# Revit family: QMXVP_with_Isolation_Box
name_source: partatom
category: Mechanical Equipment
units: mm (PartAtom-declared; Revit-internal decimal feet)

## family parameters
Always vertical = Yes
Cut with Voids When Loaded = No
Part Type = Normal
Room Calculation Point = No
Round Connector Dimension = Use Diameter
Shared = No
Work Plane-Based = No

## types (224) — shared parameters
0 = 0' - 0"
1" = 0' - 1"
1.5 = 0' - 1 1/2"
1/4 = 0' - 0 1/4"
2" = 0' - 2"
2' = 2' - 0"
3" = 0' - 3"
3.125" = 0' - 3 1/8"
4" = 0' - 4"
5" = 0' - 5"
6" = 0' - 6"
MB_HT = 1' - 4"
MB_HT+.25" = 1' - 4 1/4"
MB_HT-2.75" = 1' - 1 1/4"
Manufacturer = Loren Cook Company
ONE EIGTH = 0' - 0 1/8"
URL = www.lorencook.com

## per-type parameters (varying)
- 90_QMXVP-9L-Isolation_Box: (A/2)+.25"=1' - 2 1/4"; (NOZZLE_HEIGHT-(NOZZLE_HEIGHT/8*2))/2=0' - 10 1/2"; (NOZZLE_WB_OD-NOZZLE_TOP_OD)/2=0' - 2 3/8"; A=2' - 4"; A/2=1' - 2"; B=5' - 5"; B/2=2' - 8 1/2"; C=2' - 6"; C/2=1' - 3"; E=2' - 3 3/16"; GA=0' - 0 3/32"; Model=QMXVP-Isolation Box; NOZZLE_BOTTOM_ID=1' - 0 13/16"; NOZZLE_BOTTOM_RAD=0' - 6 13/32"; NOZZLE_HEIGHT=2' - 4"; NOZZLE_HEIGHT/7*2=0' - 7"; NOZZLE_SIZE=9' - 0"; NOZZLE_TOP_OD=1' - 1 1/2"; NOZZLE_TOP_RAD=0' - 6 3/4"; NOZZLE_WB/4=0' - 4 19/32"; NOZZLE_WB_OD=1' - 11"; NOZZLE_WB_RAD=0' - 11 1/2"; NOZZLE_WB_RAD-2"=0' - 9 1/2"; RO=1' - 9"; RO/2=0' - 10 1/2"; TRANSITION_TOP=3' - 1 1/16"; TYPE=0' - 0"; Type Comments=Vari-Plume Laboratory Exhaust Mixed-Flow Inline Belt Drive With Isolation Box; UNIT_HEIGHT=1' - 7 7/8"; UNIT_HEIGHT*.75=1' - 2 29/32"; UNIT_OD=1' - 0 13/16"; UNIT_RADIUS=0' - 6 13/32"; UNIT_RADIUS*.6=0' - 5 25/32"; UNIT_RADIUS+4"=0' - 10 13/32"
- 90_QMXVP-9H-Isolation_Box: (A/2)+.25"=1' - 2 1/4"; (NOZZLE_HEIGHT-(NOZZLE_HEIGHT/8*2))/2=0' - 10 1/2"; (NOZZLE_WB_OD-NOZZLE_TOP_OD)/2=0' - 2 3/8"; A=2' - 4"; A/2=1' - 2"; B=5' - 5"; B/2=2' - 8 1/2"; C=2' - 6"; C/2=1' - 3"; E=2' - 3 3/16"; GA=0' - 0 3/32"; Model=QMXVP-Isolation Box; NOZZLE_BOTTOM_ID=1' - 0 13/16"; NOZZLE_BOTTOM_RAD=0' - 6 13/32"; NOZZLE_HEIGHT=2' - 4"; NOZZLE_HEIGHT/7*2=0' - 7"; NOZZLE_SIZE=9' - 0"; NOZZLE_TOP_OD=1' - 1 1/2"; NOZZLE_TOP_RAD=0' - 6 3/4"; NOZZLE_WB/4=0' - 4 19/32"; NOZZLE_WB_OD=1' - 11"; NOZZLE_WB_RAD=0' - 11 1/2"; NOZZLE_WB_RAD-2"=0' - 9 1/2"; RO=1' - 9"; RO/2=0' - 10 1/2"; TRANSITION_TOP=3' - 1 1/16"; TYPE=0' - 0"; Type Comments=Vari-Plume Laboratory Exhaust Mixed-Flow Inline Belt Drive With Isolation Box; UNIT_HEIGHT=1' - 7 7/8"; UNIT_HEIGHT*.75=1' - 2 29/32"; UNIT_OD=1' - 0 13/16"; UNIT_RADIUS=0' - 6 13/32"; UNIT_RADIUS*.6=0' - 5 25/32"; UNIT_RADIUS+4"=0' - 10 13/32"
- 120_QMXVP-9L-Isolation_Box: (A/2)+.25"=1' - 2 1/4"; (NOZZLE_HEIGHT-(NOZZLE_HEIGHT/8*2))/2=0' - 10 1/2"; (NOZZLE_WB_OD-NOZZLE_TOP_OD)/2=0' - 2 3/8"; A=2' - 4"; A/2=1' - 2"; B=5' - 11"; B/2=2' - 11 1/2"; C=3' - 1"; C/2=1' - 6 1/2"; E=2' - 3 3/16"; GA=0' - 0 3/32"; Model=QMXVP-Isolation Box; NOZZLE_BOTTOM_ID=1' - 0 13/16"; NOZZLE_BOTTOM_RAD=0' - 6 13/32"; NOZZLE_HEIGHT=2' - 4"; NOZZLE_HEIGHT/7*2=0' - 7"; NOZZLE_SIZE=9' - 0"; NOZZLE_TOP_OD=1' - 1 1/2"; NOZZLE_TOP_RAD=0' - 6 3/4"; NOZZLE_WB/4=0' - 4 19/32"; NOZZLE_WB_OD=1' - 11"; NOZZLE_WB_RAD=0' - 11 1/2"; NOZZLE_WB_RAD-2"=0' - 9 1/2"; RO=1' - 9"; RO/2=0' - 10 1/2"; TRANSITION_TOP=3' - 7 3/16"; TYPE=0' - 0"; Type Comments=Vari-Plume Laboratory Exhaust Mixed-Flow Inline Belt Drive With Isolation Box; UNIT_HEIGHT=1' - 7 7/8"; UNIT_HEIGHT*.75=1' - 2 29/32"; UNIT_OD=1' - 5 1/16"; UNIT_RADIUS=0' - 8 17/32"; UNIT_RADIUS*.6=0' - 7 11/16"; UNIT_RADIUS+4"=1' - 0 17/32"
- 120_QMXVP-9H-Isolation_Box: (A/2)+.25"=1' - 2 1/4"; (NOZZLE_HEIGHT-(NOZZLE_HEIGHT/8*2))/2=0' - 10 1/2"; (NOZZLE_WB_OD-NOZZLE_TOP_OD)/2=0' - 2 3/8"; A=2' - 4"; A/2=1' - 2"; B=5' - 11"; B/2=2' - 11 1/2"; C=3' - 1"; C/2=1' - 6 1/2"; E=2' - 3 3/16"; GA=0' - 0 3/32"; Model=QMXVP-Isolation Box; NOZZLE_BOTTOM_ID=1' - 0 13/16"; NOZZLE_BOTTOM_RAD=0' - 6 13/32"; NOZZLE_HEIGHT=2' - 4"; NOZZLE_HEIGHT/7*2=0' - 7"; NOZZLE_SIZE=9' - 0"; NOZZLE_TOP_OD=1' - 1 1/2"; NOZZLE_TOP_RAD=0' - 6 3/4"; NOZZLE_WB/4=0' - 4 19/32"; NOZZLE_WB_OD=1' - 11"; NOZZLE_WB_RAD=0' - 11 1/2"; NOZZLE_WB_RAD-2"=0' - 9 1/2"; RO=1' - 9"; RO/2=0' - 10 1/2"; TRANSITION_TOP=3' - 7 3/16"; TYPE=0' - 0"; Type Comments=Vari-Plume Laboratory Exhaust Mixed-Flow Inline Belt Drive With Isolation Box; UNIT_HEIGHT=1' - 7 7/8"; UNIT_HEIGHT*.75=1' - 2 29/32"; UNIT_OD=1' - 5 1/16"; UNIT_RADIUS=0' - 8 17/32"; UNIT_RADIUS*.6=0' - 7 11/16"; UNIT_RADIUS+4"=1' - 0 17/32"
- 120_QMXVP-12L-Isolation_Box: (A/2)+.25"=1' - 2 1/4"; (NOZZLE_HEIGHT-(NOZZLE_HEIGHT/8*2))/2=1' - 0"; (NOZZLE_WB_OD-NOZZLE_TOP_OD)/2=0' - 2 1/8"; A=2' - 4"; A/2=1' - 2"; B=5' - 11"; B/2=2' - 11 1/2"; C=3' - 1"; C/2=1' - 6 1/2"; E=2' - 3 3/16"; GA=0' - 0 3/32"; Model=QMXVP-Isolation Box; NOZZLE_BOTTOM_ID=1' - 5 1/16"; NOZZLE_BOTTOM_RAD=0' - 8 17/32"; NOZZLE_HEIGHT=2' - 8"; NOZZLE_HEIGHT/7*2=0' - 8"; NOZZLE_SIZE=12' - 0"; NOZZLE_TOP_OD=1' - 7 1/2"; NOZZLE_TOP_RAD=0' - 9 3/4"; NOZZLE_WB/4=0' - 5 19/32"; NOZZLE_WB_OD=2' - 4"; NOZZLE_WB_RAD=1' - 2"; NOZZLE_WB_RAD-2"=1' - 0"; RO=1' - 9"; RO/2=0' - 10 1/2"; TRANSITION_TOP=3' - 3 7/16"; TYPE=0' - 0"; Type Comments=Vari-Plume Laboratory Exhaust Mixed-Flow Inline Belt Drive With Isolation Box; UNIT_HEIGHT=1' - 7 7/8"; UNIT_HEIGHT*.75=1' - 2 29/32"; UNIT_OD=1' - 5 1/16"; UNIT_RADIUS=0' - 8 17/32"; UNIT_RADIUS*.6=0' - 7 11/16"; UNIT_RADIUS+4"=1' - 0 17/32"
- 120_QMXVP-12H-Isolation_Box: (A/2)+.25"=1' - 2 1/4"; (NOZZLE_HEIGHT-(NOZZLE_HEIGHT/8*2))/2=1' - 0"; (NOZZLE_WB_OD-NOZZLE_TOP_OD)/2=0' - 2 1/8"; A=2' - 4"; A/2=1' - 2"; B=5' - 11"; B/2=2' - 11 1/2"; C=3' - 1"; C/2=1' - 6 1/2"; E=2' - 3 3/16"; GA=0' - 0 3/32"; Model=QMXVP-Isolation Box; NOZZLE_BOTTOM_ID=1' - 5 1/16"; NOZZLE_BOTTOM_RAD=0' - 8 17/32"; NOZZLE_HEIGHT=2' - 8"; NOZZLE_HEIGHT/7*2=0' - 8"; NOZZLE_SIZE=12' - 0"; NOZZLE_TOP_OD=1' - 7 1/2"; NOZZLE_TOP_RAD=0' - 9 3/4"; NOZZLE_WB/4=0' - 5 19/32"; NOZZLE_WB_OD=2' - 4"; NOZZLE_WB_RAD=1' - 2"; NOZZLE_WB_RAD-2"=1' - 0"; RO=1' - 9"; RO/2=0' - 10 1/2"; TRANSITION_TOP=3' - 3 7/16"; TYPE=0' - 0"; Type Comments=Vari-Plume Laboratory Exhaust Mixed-Flow Inline Belt Drive With Isolation Box; UNIT_HEIGHT=1' - 7 7/8"; UNIT_HEIGHT*.75=1' - 2 29/32"; UNIT_OD=1' - 5 1/16"; UNIT_RADIUS=0' - 8 17/32"; UNIT_RADIUS*.6=0' - 7 11/16"; UNIT_RADIUS+4"=1' - 0 17/32"
- 135_QMXVP-9L-Isolation_Box: (A/2)+.25"=1' - 2 1/4"; (NOZZLE_HEIGHT-(NOZZLE_HEIGHT/8*2))/2=0' - 10 1/2"; (NOZZLE_WB_OD-NOZZLE_TOP_OD)/2=0' - 2 3/8"; A=2' - 4"; A/2=1' - 2"; B=6' - 5"; B/2=3' - 2 1/2"; C=3' - 3"; C/2=1' - 7 1/2"; E=2' - 3 1/8"; GA=0' - 0 3/32"; Model=QMXVP-Isolation Box; NOZZLE_BOTTOM_ID=1' - 0 13/16"; NOZZLE_BOTTOM_RAD=0' - 6 13/32"; NOZZLE_HEIGHT=2' - 4"; NOZZLE_HEIGHT/7*2=0' - 7"; NOZZLE_SIZE=9' - 0"; NOZZLE_TOP_OD=1' - 1 1/2"; NOZZLE_TOP_RAD=0' - 6 3/4"; NOZZLE_WB/4=0' - 4 19/32"; NOZZLE_WB_OD=1' - 11"; NOZZLE_WB_RAD=0' - 11 1/2"; NOZZLE_WB_RAD-2"=0' - 9 1/2"; RO=1' - 8 15/16"; RO/2=0' - 10 15/32"; TRANSITION_TOP=4' - 0 11/16"; TYPE=0' - 0"; Type Comments=Vari-Plume Laboratory Exhaust Mixed-Flow Inline Belt Drive With Isolation Box; UNIT_HEIGHT=2' - 3"; UNIT_HEIGHT*.75=1' - 8 1/4"; UNIT_OD=1' - 7 1/4"; UNIT_RADIUS=0' - 9 5/8"; UNIT_RADIUS*.6=0' - 8 21/32"; UNIT_RADIUS+4"=1' - 1 5/8"
- 135_QMXVP-9H-Isolation_Box: (A/2)+.25"=1' - 2 1/4"; (NOZZLE_HEIGHT-(NOZZLE_HEIGHT/8*2))/2=0' - 10 1/2"; (NOZZLE_WB_OD-NOZZLE_TOP_OD)/2=0' - 2 3/8"; A=2' - 4"; A/2=1' - 2"; B=6' - 5"; B/2=3' - 2 1/2"; C=3' - 3"; C/2=1' - 7 1/2"; E=2' - 3 1/8"; GA=0' - 0 3/32"; Model=QMXVP-Isolation Box; NOZZLE_BOTTOM_ID=1' - 0 13/16"; NOZZLE_BOTTOM_RAD=0' - 6 13/32"; NOZZLE_HEIGHT=2' - 4"; NOZZLE_HEIGHT/7*2=0' - 7"; NOZZLE_SIZE=9' - 0"; NOZZLE_TOP_OD=1' - 1 1/2"; NOZZLE_TOP_RAD=0' - 6 3/4"; NOZZLE_WB/4=0' - 4 19/32"; NOZZLE_WB_OD=1' - 11"; NOZZLE_WB_RAD=0' - 11 1/2"; NOZZLE_WB_RAD-2"=0' - 9 1/2"; RO=1' - 8 15/16"; RO/2=0' - 10 15/32"; TRANSITION_TOP=4' - 0 11/16"; TYPE=0' - 0"; Type Comments=Vari-Plume Laboratory Exhaust Mixed-Flow Inline Belt Drive With Isolation Box; UNIT_HEIGHT=2' - 3"; UNIT_HEIGHT*.75=1' - 8 1/4"; UNIT_OD=1' - 7 1/4"; UNIT_RADIUS=0' - 9 5/8"; UNIT_RADIUS*.6=0' - 8 21/32"; UNIT_RADIUS+4"=1' - 1 5/8"
- 150_QMXVP-9L-Isolation_Box: (A/2)+.25"=1' - 3 1/4"; (NOZZLE_HEIGHT-(NOZZLE_HEIGHT/8*2))/2=0' - 10 1/2"; (NOZZLE_WB_OD-NOZZLE_TOP_OD)/2=0' - 2 3/8"; A=2' - 6"; A/2=1' - 3"; B=7' - 3"; B/2=3' - 7 1/2"; C=3' - 6"; C/2=1' - 9"; E=2' - 5 1/8"; GA=0' - 0 3/32"; Model=QMXVP-Isolation Box; NOZZLE_BOTTOM_ID=1' - 0 13/16"; NOZZLE_BOTTOM_RAD=0' - 6 13/32"; NOZZLE_HEIGHT=2' - 4"; NOZZLE_HEIGHT/7*2=0' - 7"; NOZZLE_SIZE=9' - 0"; NOZZLE_TOP_OD=1' - 1 1/2"; NOZZLE_TOP_RAD=0' - 6 3/4"; NOZZLE_WB/4=0' - 4 19/32"; NOZZLE_WB_OD=1' - 11"; NOZZLE_WB_RAD=0' - 11 1/2"; NOZZLE_WB_RAD-2"=0' - 9 1/2"; RO=1' - 10 15/16"; RO/2=0' - 11 15/32"; TRANSITION_TOP=4' - 6 1/4"; TYPE=0' - 0"; Type Comments=Vari-Plume Laboratory Exhaust Mixed-Flow Inline Belt Drive With Isolation Box; UNIT_HEIGHT=2' - 6"; UNIT_HEIGHT*.75=1' - 10 1/2"; UNIT_OD=1' - 9 3/8"; UNIT_RADIUS=0' - 10 11/16"; UNIT_RADIUS*.6=0' - 9 5/8"; UNIT_RADIUS+4"=1' - 2 11/16"
- 135_QMXVP-12L-Isolation_Box: (A/2)+.25"=1' - 2 1/4"; (NOZZLE_HEIGHT-(NOZZLE_HEIGHT/8*2))/2=1' - 0"; (NOZZLE_WB_OD-NOZZLE_TOP_OD)/2=0' - 2 1/8"; A=2' - 4"; A/2=1' - 2"; B=6' - 5"; B/2=3' - 2 1/2"; C=3' - 3"; C/2=1' - 7 1/2"; E=2' - 3 1/8"; GA=0' - 0 3/32"; Model=QMXVP-Isolation Box; NOZZLE_BOTTOM_ID=1' - 5 1/16"; NOZZLE_BOTTOM_RAD=0' - 8 17/32"; NOZZLE_HEIGHT=2' - 8"; NOZZLE_HEIGHT/7*2=0' - 8"; NOZZLE_SIZE=12' - 0"; NOZZLE_TOP_OD=1' - 7 1/2"; NOZZLE_TOP_RAD=0' - 9 3/4"; NOZZLE_WB/4=0' - 5 19/32"; NOZZLE_WB_OD=2' - 4"; NOZZLE_WB_RAD=1' - 2"; NOZZLE_WB_RAD-2"=1' - 0"; RO=1' - 8 15/16"; RO/2=0' - 10 15/32"; TRANSITION_TOP=3' - 4 11/16"; TYPE=0' - 0"; Type Comments=Vari-Plume Laboratory Exhaust Mixed-Flow Inline Belt Drive With Isolation Box; UNIT_HEIGHT=2' - 3"; UNIT_HEIGHT*.75=1' - 8 1/4"; UNIT_OD=1' - 7 1/4"; UNIT_RADIUS=0' - 9 5/8"; UNIT_RADIUS*.6=0' - 8 21/32"; UNIT_RADIUS+4"=1' - 1 5/8"
- 135_QMXVP-12H-Isolation_Box: (A/2)+.25"=1' - 2 1/4"; (NOZZLE_HEIGHT-(NOZZLE_HEIGHT/8*2))/2=1' - 0"; (NOZZLE_WB_OD-NOZZLE_TOP_OD)/2=0' - 2 1/8"; A=2' - 4"; A/2=1' - 2"; B=6' - 5"; B/2=3' - 2 1/2"; C=3' - 3"; C/2=1' - 7 1/2"; E=2' - 3 1/8"; GA=0' - 0 3/32"; Model=QMXVP-Isolation Box; NOZZLE_BOTTOM_ID=1' - 5 1/16"; NOZZLE_BOTTOM_RAD=0' - 8 17/32"; NOZZLE_HEIGHT=2' - 8"; NOZZLE_HEIGHT/7*2=0' - 8"; NOZZLE_SIZE=12' - 0"; NOZZLE_TOP_OD=1' - 7 1/2"; NOZZLE_TOP_RAD=0' - 9 3/4"; NOZZLE_WB/4=0' - 5 19/32"; NOZZLE_WB_OD=2' - 4"; NOZZLE_WB_RAD=1' - 2"; NOZZLE_WB_RAD-2"=1' - 0"; RO=1' - 8 15/16"; RO/2=0' - 10 15/32"; TRANSITION_TOP=3' - 4 11/16"; TYPE=0' - 0"; Type Comments=Vari-Plume Laboratory Exhaust Mixed-Flow Inline Belt Drive With Isolation Box; UNIT_HEIGHT=2' - 3"; UNIT_HEIGHT*.75=1' - 8 1/4"; UNIT_OD=1' - 7 1/4"; UNIT_RADIUS=0' - 9 5/8"; UNIT_RADIUS*.6=0' - 8 21/32"; UNIT_RADIUS+4"=1' - 1 5/8"
- 150_QMXVP-9H-Isolation_Box: (A/2)+.25"=1' - 3 1/4"; (NOZZLE_HEIGHT-(NOZZLE_HEIGHT/8*2))/2=0' - 10 1/2"; (NOZZLE_WB_OD-NOZZLE_TOP_OD)/2=0' - 2 3/8"; A=2' - 6"; A/2=1' - 3"; B=7' - 3"; B/2=3' - 7 1/2"; C=3' - 6"; C/2=1' - 9"; E=2' - 5 1/8"; GA=0' - 0 3/32"; Model=QMXVP-Isolation Box; NOZZLE_BOTTOM_ID=1' - 0 13/16"; NOZZLE_BOTTOM_RAD=0' - 6 13/32"; NOZZLE_HEIGHT=2' - 4"; NOZZLE_HEIGHT/7*2=0' - 7"; NOZZLE_SIZE=9' - 0"; NOZZLE_TOP_OD=1' - 1 1/2"; NOZZLE_TOP_RAD=0' - 6 3/4"; NOZZLE_WB/4=0' - 4 19/32"; NOZZLE_WB_OD=1' - 11"; NOZZLE_WB_RAD=0' - 11 1/2"; NOZZLE_WB_RAD-2"=0' - 9 1/2"; RO=1' - 10 15/16"; RO/2=0' - 11 15/32"; TRANSITION_TOP=4' - 6 1/4"; TYPE=0' - 0"; Type Comments=Vari-Plume Laboratory Exhaust Mixed-Flow Inline Belt Drive With Isolation Box; UNIT_HEIGHT=2' - 6"; UNIT_HEIGHT*.75=1' - 10 1/2"; UNIT_OD=1' - 9 3/8"; UNIT_RADIUS=0' - 10 11/16"; UNIT_RADIUS*.6=0' - 9 5/8"; UNIT_RADIUS+4"=1' - 2 11/16"
- 150_QMXVP-12L-Isolation_Box: (A/2)+.25"=1' - 3 1/4"; (NOZZLE_HEIGHT-(NOZZLE_HEIGHT/8*2))/2=1' - 0"; (NOZZLE_WB_OD-NOZZLE_TOP_OD)/2=0' - 2 1/8"; A=2' - 6"; A/2=1' - 3"; B=7' - 3"; B/2=3' - 7 1/2"; C=3' - 6"; C/2=1' - 9"; E=2' - 5 1/8"; GA=0' - 0 3/32"; Model=QMXVP-Isolation Box; NOZZLE_BOTTOM_ID=1' - 5 1/16"; NOZZLE_BOTTOM_RAD=0' - 8 17/32"; NOZZLE_HEIGHT=2' - 8"; NOZZLE_HEIGHT/7*2=0' - 8"; NOZZLE_SIZE=12' - 0"; NOZZLE_TOP_OD=1' - 7 1/2"; NOZZLE_TOP_RAD=0' - 9 3/4"; NOZZLE_WB/4=0' - 5 19/32"; NOZZLE_WB_OD=2' - 4"; NOZZLE_WB_RAD=1' - 2"; NOZZLE_WB_RAD-2"=1' - 0"; RO=1' - 10 15/16"; RO/2=0' - 11 15/32"; TRANSITION_TOP=3' - 10 1/4"; TYPE=0' - 0"; Type Comments=Vari-Plume Laboratory Exhaust Mixed-Flow Inline Belt Drive With Isolation Box; UNIT_HEIGHT=2' - 6"; UNIT_HEIGHT*.75=1' - 10 1/2"; UNIT_OD=1' - 9 3/8"; UNIT_RADIUS=0' - 10 11/16"; UNIT_RADIUS*.6=0' - 9 5/8"; UNIT_RADIUS+4"=1' - 2 11/16"
- 150_QMXVP-12H-Isolation_Box: (A/2)+.25"=1' - 3 1/4"; (NOZZLE_HEIGHT-(NOZZLE_HEIGHT/8*2))/2=1' - 0"; (NOZZLE_WB_OD-NOZZLE_TOP_OD)/2=0' - 2 1/8"; A=2' - 6"; A/2=1' - 3"; B=7' - 3"; B/2=3' - 7 1/2"; C=3' - 6"; C/2=1' - 9"; E=2' - 5 1/8"; GA=0' - 0 3/32"; Model=QMXVP-Isolation Box; NOZZLE_BOTTOM_ID=1' - 5 1/16"; NOZZLE_BOTTOM_RAD=0' - 8 17/32"; NOZZLE_HEIGHT=2' - 8"; NOZZLE_HEIGHT/7*2=0' - 8"; NOZZLE_SIZE=12' - 0"; NOZZLE_TOP_OD=1' - 7 1/2"; NOZZLE_TOP_RAD=0' - 9 3/4"; NOZZLE_WB/4=0' - 5 19/32"; NOZZLE_WB_OD=2' - 4"; NOZZLE_WB_RAD=1' - 2"; NOZZLE_WB_RAD-2"=1' - 0"; RO=1' - 10 15/16"; RO/2=0' - 11 15/32"; TRANSITION_TOP=3' - 10 1/4"; TYPE=0' - 0"; Type Comments=Vari-Plume Laboratory Exhaust Mixed-Flow Inline Belt Drive With Isolation Box; UNIT_HEIGHT=2' - 6"; UNIT_HEIGHT*.75=1' - 10 1/2"; UNIT_OD=1' - 9 3/8"; UNIT_RADIUS=0' - 10 11/16"; UNIT_RADIUS*.6=0' - 9 5/8"; UNIT_RADIUS+4"=1' - 2 11/16"
- 150_QMXVP-15L-Isolation_Box: (A/2)+.25"=1' - 3 1/4"; (NOZZLE_HEIGHT-(NOZZLE_HEIGHT/8*2))/2=1' - 4 1/8"; (NOZZLE_WB_OD-NOZZLE_TOP_OD)/2=0' - 3 1/4"; A=2' - 6"; A/2=1' - 3"; B=7' - 3"; B/2=3' - 7 1/2"; C=3' - 6"; C/2=1' - 9"; E=2' - 5 1/8"; GA=0' - 0 3/32"; Model=QMXVP-Isolation Box; NOZZLE_BOTTOM_ID=1' - 9 3/8"; NOZZLE_BOTTOM_RAD=0' - 10 11/16"; NOZZLE_HEIGHT=3' - 7"; NOZZLE_HEIGHT/7*2=0' - 10 3/4"; NOZZLE_SIZE=15' - 0"; NOZZLE_TOP_OD=1' - 11"; NOZZLE_TOP_RAD=0' - 11 1/2"; NOZZLE_WB/4=0' - 7 3/16"; NOZZLE_WB_OD=3' - 0"; NOZZLE_WB_RAD=1' - 6"; NOZZLE_WB_RAD-2"=1' - 4"; RO=1' - 10 15/16"; RO/2=0' - 11 15/32"; TRANSITION_TOP=3' - 7 5/16"; TYPE=0' - 0"; Type Comments=Vari-Plume Laboratory Exhaust Mixed-Flow Inline Belt Drive With Isolation Box; UNIT_HEIGHT=2' - 6"; UNIT_HEIGHT*.75=1' - 10 1/2"; UNIT_OD=1' - 9 3/8"; UNIT_RADIUS=0' - 10 11/16"; UNIT_RADIUS*.6=0' - 9 5/8"; UNIT_RADIUS+4"=1' - 2 11/16"
- 150_QMXVP-15H-Isolation_Box: (A/2)+.25"=1' - 3 1/4"; (NOZZLE_HEIGHT-(NOZZLE_HEIGHT/8*2))/2=1' - 4 1/8"; (NOZZLE_WB_OD-NOZZLE_TOP_OD)/2=0' - 3 1/4"; A=2' - 6"; A/2=1' - 3"; B=7' - 3"; B/2=3' - 7 1/2"; C=3' - 6"; C/2=1' - 9"; E=2' - 5 1/8"; GA=0' - 0 3/32"; Model=QMXVP-Isolation Box; NOZZLE_BOTTOM_ID=1' - 9 3/8"; NOZZLE_BOTTOM_RAD=0' - 10 11/16"; NOZZLE_HEIGHT=3' - 7"; NOZZLE_HEIGHT/7*2=0' - 10 3/4"; NOZZLE_SIZE=15' - 0"; NOZZLE_TOP_OD=1' - 11"; NOZZLE_TOP_RAD=0' - 11 1/2"; NOZZLE_WB/4=0' - 7 3/16"; NOZZLE_WB_OD=3' - 0"; NOZZLE_WB_RAD=1' - 6"; NOZZLE_WB_RAD-2"=1' - 4"; RO=1' - 10 15/16"; RO/2=0' - 11 15/32"; TRANSITION_TOP=3' - 7 5/16"; TYPE=0' - 0"; Type Comments=Vari-Plume Laboratory Exhaust Mixed-Flow Inline Belt Drive With Isolation Box; UNIT_HEIGHT=2' - 6"; UNIT_HEIGHT*.75=1' - 10 1/2"; UNIT_OD=1' - 9 3/8"; UNIT_RADIUS=0' - 10 11/16"; UNIT_RADIUS*.6=0' - 9 5/8"; UNIT_RADIUS+4"=1' - 2 11/16"
- 165_QMXVP-9L-Isolation_Box: (A/2)+.25"=1' - 4 1/4"; (NOZZLE_HEIGHT-(NOZZLE_HEIGHT/8*2))/2=0' - 10 1/2"; (NOZZLE_WB_OD-NOZZLE_TOP_OD)/2=0' - 2 3/8"; A=2' - 8"; A/2=1' - 4"; B=7' - 5"; B/2=3' - 8 1/2"; C=3' - 8"; C/2=1' - 10"; E=2' - 7 1/8"; GA=0' - 0 3/32"; Model=QMXVP-Isolation Box; NOZZLE_BOTTOM_ID=1' - 0 13/16"; NOZZLE_BOTTOM_RAD=0' - 6 13/32"; NOZZLE_HEIGHT=2' - 4"; NOZZLE_HEIGHT/7*2=0' - 7"; NOZZLE_SIZE=9' - 0"; NOZZLE_TOP_OD=1' - 1 1/2"; NOZZLE_TOP_RAD=0' - 6 3/4"; NOZZLE_WB/4=0' - 4 19/32"; NOZZLE_WB_OD=1' - 11"; NOZZLE_WB_RAD=0' - 11 1/2"; NOZZLE_WB_RAD-2"=0' - 9 1/2"; RO=2' - 0 15/16"; RO/2=1' - 0 15/32"; TRANSITION_TOP=5' - 1 1/4"; TYPE=0' - 0"; Type Comments=Vari-Plume Laboratory Exhaust Mixed-Flow Inline Belt Drive With Isolation Box; UNIT_HEIGHT=2' - 9"; UNIT_HEIGHT*.75=2' - 0 3/4"; UNIT_OD=1' - 11 1/2"; UNIT_RADIUS=0' - 11 3/4"; UNIT_RADIUS*.6=0' - 10 9/16"; UNIT_RADIUS+4"=1' - 3 3/4"
- 165_QMXVP-9H-Isolation_Box: (A/2)+.25"=1' - 4 1/4"; (NOZZLE_HEIGHT-(NOZZLE_HEIGHT/8*2))/2=0' - 10 1/2"; (NOZZLE_WB_OD-NOZZLE_TOP_OD)/2=0' - 2 3/8"; A=2' - 8"; A/2=1' - 4"; B=7' - 5"; B/2=3' - 8 1/2"; C=3' - 8"; C/2=1' - 10"; E=2' - 7 1/8"; GA=0' - 0 3/32"; Model=QMXVP-Isolation Box; NOZZLE_BOTTOM_ID=1' - 0 13/16"; NOZZLE_BOTTOM_RAD=0' - 6 13/32"; NOZZLE_HEIGHT=2' - 4"; NOZZLE_HEIGHT/7*2=0' - 7"; NOZZLE_SIZE=9' - 0"; NOZZLE_TOP_OD=1' - 1 1/2"; NOZZLE_TOP_RAD=0' - 6 3/4"; NOZZLE_WB/4=0' - 4 19/32"; NOZZLE_WB_OD=1' - 11"; NOZZLE_WB_RAD=0' - 11 1/2"; NOZZLE_WB_RAD-2"=0' - 9 1/2"; RO=2' - 0 15/16"; RO/2=1' - 0 15/32"; TRANSITION_TOP=5' - 1 1/4"; TYPE=0' - 0"; Type Comments=Vari-Plume Laboratory Exhaust Mixed-Flow Inline Belt Drive With Isolation Box; UNIT_HEIGHT=2' - 9"; UNIT_HEIGHT*.75=2' - 0 3/4"; UNIT_OD=1' - 11 1/2"; UNIT_RADIUS=0' - 11 3/4"; UNIT_RADIUS*.6=0' - 10 9/16"; UNIT_RADIUS+4"=1' - 3 3/4"
- 165_QMXVP-12L-Isolation_Box: (A/2)+.25"=1' - 4 1/4"; (NOZZLE_HEIGHT-(NOZZLE_HEIGHT/8*2))/2=1' - 0"; (NOZZLE_WB_OD-NOZZLE_TOP_OD)/2=0' - 2 1/8"; A=2' - 8"; A/2=1' - 4"; B=7' - 5"; B/2=3' - 8 1/2"; C=3' - 8"; C/2=1' - 10"; E=2' - 7 1/8"; GA=0' - 0 3/32"; Model=QMXVP-Isolation Box; NOZZLE_BOTTOM_ID=1' - 5 1/16"; NOZZLE_BOTTOM_RAD=0' - 8 17/32"; NOZZLE_HEIGHT=2' - 8"; NOZZLE_HEIGHT/7*2=0' - 8"; NOZZLE_SIZE=12' - 0"; NOZZLE_TOP_OD=1' - 7 1/2"; NOZZLE_TOP_RAD=0' - 9 3/4"; NOZZLE_WB/4=0' - 5 19/32"; NOZZLE_WB_OD=2' - 4"; NOZZLE_WB_RAD=1' - 2"; NOZZLE_WB_RAD-2"=1' - 0"; RO=2' - 0 15/16"; RO/2=1' - 0 15/32"; TRANSITION_TOP=4' - 5 1/4"; TYPE=0' - 0"; Type Comments=Vari-Plume Laboratory Exhaust Mixed-Flow Inline Belt Drive With Isolation Box; UNIT_HEIGHT=2' - 9"; UNIT_HEIGHT*.75=2' - 0 3/4"; UNIT_OD=1' - 11 1/2"; UNIT_RADIUS=0' - 11 3/4"; UNIT_RADIUS*.6=0' - 10 9/16"; UNIT_RADIUS+4"=1' - 3 3/4"
- 165_QMXVP-12H-Isolation_Box: (A/2)+.25"=1' - 4 1/4"; (NOZZLE_HEIGHT-(NOZZLE_HEIGHT/8*2))/2=1' - 0"; (NOZZLE_WB_OD-NOZZLE_TOP_OD)/2=0' - 2 1/8"; A=2' - 8"; A/2=1' - 4"; B=7' - 5"; B/2=3' - 8 1/2"; C=3' - 8"; C/2=1' - 10"; E=2' - 7 1/8"; GA=0' - 0 3/32"; Model=QMXVP-Isolation Box; NOZZLE_BOTTOM_ID=1' - 5 1/16"; NOZZLE_BOTTOM_RAD=0' - 8 17/32"; NOZZLE_HEIGHT=2' - 8"; NOZZLE_HEIGHT/7*2=0' - 8"; NOZZLE_SIZE=12' - 0"; NOZZLE_TOP_OD=1' - 7 1/2"; NOZZLE_TOP_RAD=0' - 9 3/4"; NOZZLE_WB/4=0' - 5 19/32"; NOZZLE_WB_OD=2' - 4"; NOZZLE_WB_RAD=1' - 2"; NOZZLE_WB_RAD-2"=1' - 0"; RO=2' - 0 15/16"; RO/2=1' - 0 15/32"; TRANSITION_TOP=4' - 5 1/4"; TYPE=0' - 0"; Type Comments=Vari-Plume Laboratory Exhaust Mixed-Flow Inline Belt Drive With Isolation Box; UNIT_HEIGHT=2' - 9"; UNIT_HEIGHT*.75=2' - 0 3/4"; UNIT_OD=1' - 11 1/2"; UNIT_RADIUS=0' - 11 3/4"; UNIT_RADIUS*.6=0' - 10 9/16"; UNIT_RADIUS+4"=1' - 3 3/4"
- 165_QMXVP-15L-Isolation_Box: (A/2)+.25"=1' - 4 1/4"; (NOZZLE_HEIGHT-(NOZZLE_HEIGHT/8*2))/2=1' - 4 1/8"; (NOZZLE_WB_OD-NOZZLE_TOP_OD)/2=0' - 3 1/4"; A=2' - 8"; A/2=1' - 4"; B=7' - 5"; B/2=3' - 8 1/2"; C=3' - 8"; C/2=1' - 10"; E=2' - 7 1/8"; GA=0' - 0 3/32"; Model=QMXVP-Isolation Box; NOZZLE_BOTTOM_ID=1' - 9 3/8"; NOZZLE_BOTTOM_RAD=0' - 10 11/16"; NOZZLE_HEIGHT=3' - 7"; NOZZLE_HEIGHT/7*2=0' - 10 3/4"; NOZZLE_SIZE=15' - 0"; NOZZLE_TOP_OD=1' - 11"; NOZZLE_TOP_RAD=0' - 11 1/2"; NOZZLE_WB/4=0' - 7 3/16"; NOZZLE_WB_OD=3' - 0"; NOZZLE_WB_RAD=1' - 6"; NOZZLE_WB_RAD-2"=1' - 4"; RO=2' - 0 15/16"; RO/2=1' - 0 15/32"; TRANSITION_TOP=3' - 9 5/16"; TYPE=0' - 0"; Type Comments=Vari-Plume Laboratory Exhaust Mixed-Flow Inline Belt Drive With Isolation Box; UNIT_HEIGHT=2' - 9"; UNIT_HEIGHT*.75=2' - 0 3/4"; UNIT_OD=1' - 11 1/2"; UNIT_RADIUS=0' - 11 3/4"; UNIT_RADIUS*.6=0' - 10 9/16"; UNIT_RADIUS+4"=1' - 3 3/4"
- 165_QMXVP-15H-Isolation_Box: (A/2)+.25"=1' - 4 1/4"; (NOZZLE_HEIGHT-(NOZZLE_HEIGHT/8*2))/2=1' - 4 1/8"; (NOZZLE_WB_OD-NOZZLE_TOP_OD)/2=0' - 3 1/4"; A=2' - 8"; A/2=1' - 4"; B=7' - 5"; B/2=3' - 8 1/2"; C=3' - 8"; C/2=1' - 10"; E=2' - 7 1/8"; GA=0' - 0 3/32"; Model=QMXVP-Isolation Box; NOZZLE_BOTTOM_ID=1' - 9 3/8"; NOZZLE_BOTTOM_RAD=0' - 10 11/16"; NOZZLE_HEIGHT=3' - 7"; NOZZLE_HEIGHT/7*2=0' - 10 3/4"; NOZZLE_SIZE=15' - 0"; NOZZLE_TOP_OD=1' - 11"; NOZZLE_TOP_RAD=0' - 11 1/2"; NOZZLE_WB/4=0' - 7 3/16"; NOZZLE_WB_OD=3' - 0"; NOZZLE_WB_RAD=1' - 6"; NOZZLE_WB_RAD-2"=1' - 4"; RO=2' - 0 15/16"; RO/2=1' - 0 15/32"; TRANSITION_TOP=3' - 9 5/16"; TYPE=0' - 0"; Type Comments=Vari-Plume Laboratory Exhaust Mixed-Flow Inline Belt Drive With Isolation Box; UNIT_HEIGHT=2' - 9"; UNIT_HEIGHT*.75=2' - 0 3/4"; UNIT_OD=1' - 11 1/2"; UNIT_RADIUS=0' - 11 3/4"; UNIT_RADIUS*.6=0' - 10 9/16"; UNIT_RADIUS+4"=1' - 3 3/4"
- 180_QMXVP-12L-Isolation_Box: (A/2)+.25"=1' - 5 1/4"; (NOZZLE_HEIGHT-(NOZZLE_HEIGHT/8*2))/2=1' - 0"; (NOZZLE_WB_OD-NOZZLE_TOP_OD)/2=0' - 2 1/8"; A=2' - 10"; A/2=1' - 5"; B=8' - 2"; B/2=4' - 1"; C=3' - 10"; C/2=1' - 11"; E=2' - 9 1/8"; GA=0' - 0 3/32"; Model=QMXVP-Isolation Box; NOZZLE_BOTTOM_ID=1' - 5 1/16"; NOZZLE_BOTTOM_RAD=0' - 8 17/32"; NOZZLE_HEIGHT=2' - 8"; NOZZLE_HEIGHT/7*2=0' - 8"; NOZZLE_SIZE=12' - 0"; NOZZLE_TOP_OD=1' - 7 1/2"; NOZZLE_TOP_RAD=0' - 9 3/4"; NOZZLE_WB/4=0' - 5 19/32"; NOZZLE_WB_OD=2' - 4"; NOZZLE_WB_RAD=1' - 2"; NOZZLE_WB_RAD-2"=1' - 0"; RO=2' - 2 15/16"; RO/2=1' - 1 15/32"; TRANSITION_TOP=4' - 11 1/16"; TYPE=0' - 0"; Type Comments=Vari-Plume Laboratory Exhaust Mixed-Flow Inline Belt Drive With Isolation Box; UNIT_HEIGHT=2' - 11"; UNIT_HEIGHT*.75=2' - 2 1/4"; UNIT_OD=2' - 1 5/8"; UNIT_RADIUS=1' - 0 13/16"; UNIT_RADIUS*.6=0' - 11 17/32"; UNIT_RADIUS+4"=1' - 4 13/16"
- 180_QMXVP-12H-Isolation_Box: (A/2)+.25"=1' - 5 1/4"; (NOZZLE_HEIGHT-(NOZZLE_HEIGHT/8*2))/2=1' - 0"; (NOZZLE_WB_OD-NOZZLE_TOP_OD)/2=0' - 2 1/8"; A=2' - 10"; A/2=1' - 5"; B=8' - 2"; B/2=4' - 1"; C=3' - 10"; C/2=1' - 11"; E=2' - 9 1/8"; GA=0' - 0 3/32"; Model=QMXVP-Isolation Box; NOZZLE_BOTTOM_ID=1' - 5 1/16"; NOZZLE_BOTTOM_RAD=0' - 8 17/32"; NOZZLE_HEIGHT=2' - 8"; NOZZLE_HEIGHT/7*2=0' - 8"; NOZZLE_SIZE=12' - 0"; NOZZLE_TOP_OD=1' - 7 1/2"; NOZZLE_TOP_RAD=0' - 9 3/4"; NOZZLE_WB/4=0' - 5 19/32"; NOZZLE_WB_OD=2' - 4"; NOZZLE_WB_RAD=1' - 2"; NOZZLE_WB_RAD-2"=1' - 0"; RO=2' - 2 15/16"; RO/2=1' - 1 15/32"; TRANSITION_TOP=4' - 11 1/16"; TYPE=0' - 0"; Type Comments=Vari-Plume Laboratory Exhaust Mixed-Flow Inline Belt Drive With Isolation Box; UNIT_HEIGHT=2' - 11"; UNIT_HEIGHT*.75=2' - 2 1/4"; UNIT_OD=2' - 1 5/8"; UNIT_RADIUS=1' - 0 13/16"; UNIT_RADIUS*.6=0' - 11 17/32"; UNIT_RADIUS+4"=1' - 4 13/16"
- 180_QMXVP-15L-Isolation_Box: (A/2)+.25"=1' - 5 1/4"; (NOZZLE_HEIGHT-(NOZZLE_HEIGHT/8*2))/2=1' - 4 1/8"; (NOZZLE_WB_OD-NOZZLE_TOP_OD)/2=0' - 3 1/4"; A=2' - 10"; A/2=1' - 5"; B=8' - 2"; B/2=4' - 1"; C=3' - 10"; C/2=1' - 11"; E=2' - 9 1/8"; GA=0' - 0 3/32"; Model=QMXVP-Isolation Box; NOZZLE_BOTTOM_ID=1' - 9 3/8"; NOZZLE_BOTTOM_RAD=0' - 10 11/16"; NOZZLE_HEIGHT=3' - 7"; NOZZLE_HEIGHT/7*2=0' - 10 3/4"; NOZZLE_SIZE=15' - 0"; NOZZLE_TOP_OD=1' - 11"; NOZZLE_TOP_RAD=0' - 11 1/2"; NOZZLE_WB/4=0' - 7 3/16"; NOZZLE_WB_OD=3' - 0"; NOZZLE_WB_RAD=1' - 6"; NOZZLE_WB_RAD-2"=1' - 4"; RO=2' - 2 15/16"; RO/2=1' - 1 15/32"; TRANSITION_TOP=4' - 3 1/8"; TYPE=0' - 0"; Type Comments=Vari-Plume Laboratory Exhaust Mixed-Flow Inline Belt Drive With Isolation Box; UNIT_HEIGHT=2' - 11"; UNIT_HEIGHT*.75=2' - 2 1/4"; UNIT_OD=2' - 1 5/8"; UNIT_RADIUS=1' - 0 13/16"; UNIT_RADIUS*.6=0' - 11 17/32"; UNIT_RADIUS+4"=1' - 4 13/16"
- 180_QMXVP-15H-Isolation_Box: (A/2)+.25"=1' - 5 1/4"; (NOZZLE_HEIGHT-(NOZZLE_HEIGHT/8*2))/2=1' - 4 1/8"; (NOZZLE_WB_OD-NOZZLE_TOP_OD)/2=0' - 3 1/4"; A=2' - 10"; A/2=1' - 5"; B=8' - 2"; B/2=4' - 1"; C=3' - 10"; C/2=1' - 11"; E=2' - 9 1/8"; GA=0' - 0 3/32"; Model=QMXVP-Isolation Box; NOZZLE_BOTTOM_ID=1' - 9 3/8"; NOZZLE_BOTTOM_RAD=0' - 10 11/16"; NOZZLE_HEIGHT=3' - 7"; NOZZLE_HEIGHT/7*2=0' - 10 3/4"; NOZZLE_SIZE=15' - 0"; NOZZLE_TOP_OD=1' - 11"; NOZZLE_TOP_RAD=0' - 11 1/2"; NOZZLE_WB/4=0' - 7 3/16"; NOZZLE_WB_OD=3' - 0"; NOZZLE_WB_RAD=1' - 6"; NOZZLE_WB_RAD-2"=1' - 4"; RO=2' - 2 15/16"; RO/2=1' - 1 15/32"; TRANSITION_TOP=4' - 3 1/8"; TYPE=0' - 0"; Type Comments=Vari-Plume Laboratory Exhaust Mixed-Flow Inline Belt Drive With Isolation Box; UNIT_HEIGHT=2' - 11"; UNIT_HEIGHT*.75=2' - 2 1/4"; UNIT_OD=2' - 1 5/8"; UNIT_RADIUS=1' - 0 13/16"; UNIT_RADIUS*.6=0' - 11 17/32"; UNIT_RADIUS+4"=1' - 4 13/16"
- 180_QMXVP-18L-Isolation_Box: (A/2)+.25"=1' - 5 1/4"; (NOZZLE_HEIGHT-(NOZZLE_HEIGHT/8*2))/2=1' - 6"; (NOZZLE_WB_OD-NOZZLE_TOP_OD)/2=0' - 3 7/8"; A=2' - 10"; A/2=1' - 5"; B=8' - 2"; B/2=4' - 1"; C=3' - 10"; C/2=1' - 11"; E=2' - 9 1/8"; GA=0' - 0 3/32"; Model=QMXVP-Isolation Box; NOZZLE_BOTTOM_ID=2' - 1 5/8"; NOZZLE_BOTTOM_RAD=1' - 0 13/16"; NOZZLE_HEIGHT=4' - 0"; NOZZLE_HEIGHT/7*2=1' - 0"; NOZZLE_SIZE=18' - 0"; NOZZLE_TOP_OD=2' - 3 1/2"; NOZZLE_TOP_RAD=1' - 1 3/4"; NOZZLE_WB/4=0' - 8 19/32"; NOZZLE_WB_OD=3' - 7"; NOZZLE_WB_RAD=1' - 9 1/2"; NOZZLE_WB_RAD-2"=1' - 7 1/2"; RO=2' - 2 15/16"; RO/2=1' - 1 15/32"; TRANSITION_TOP=4' - 0 1/2"; TYPE=0' - 0"; Type Comments=Vari-Plume Laboratory Exhaust Mixed-Flow Inline Belt Drive With Isolation Box; UNIT_HEIGHT=2' - 11"; UNIT_HEIGHT*.75=2' - 2 1/4"; UNIT_OD=2' - 1 5/8"; UNIT_RADIUS=1' - 0 13/16"; UNIT_RADIUS*.6=0' - 11 17/32"; UNIT_RADIUS+4"=1' - 4 13/16"
- 180_QMXVP-18H-Isolation_Box: (A/2)+.25"=1' - 5 1/4"; (NOZZLE_HEIGHT-(NOZZLE_HEIGHT/8*2))/2=1' - 6"; (NOZZLE_WB_OD-NOZZLE_TOP_OD)/2=0' - 3 7/8"; A=2' - 10"; A/2=1' - 5"; B=8' - 2"; B/2=4' - 1"; C=3' - 10"; C/2=1' - 11"; E=2' - 9 1/8"; GA=0' - 0 3/32"; Model=QMXVP-Isolation Box; NOZZLE_BOTTOM_ID=2' - 1 5/8"; NOZZLE_BOTTOM_RAD=1' - 0 13/16"; NOZZLE_HEIGHT=4' - 0"; NOZZLE_HEIGHT/7*2=1' - 0"; NOZZLE_SIZE=18' - 0"; NOZZLE_TOP_OD=2' - 3 1/2"; NOZZLE_TOP_RAD=1' - 1 3/4"; NOZZLE_WB/4=0' - 8 19/32"; NOZZLE_WB_OD=3' - 7"; NOZZLE_WB_RAD=1' - 9 1/2"; NOZZLE_WB_RAD-2"=1' - 7 1/2"; RO=2' - 2 15/16"; RO/2=1' - 1 15/32"; TRANSITION_TOP=4' - 0 1/2"; TYPE=0' - 0"; Type Comments=Vari-Plume Laboratory Exhaust Mixed-Flow Inline Belt Drive With Isolation Box; UNIT_HEIGHT=2' - 11"; UNIT_HEIGHT*.75=2' - 2 1/4"; UNIT_OD=2' - 1 5/8"; UNIT_RADIUS=1' - 0 13/16"; UNIT_RADIUS*.6=0' - 11 17/32"; UNIT_RADIUS+4"=1' - 4 13/16"
- 202_QMXVP-12L-Isolation_Box: (A/2)+.25"=1' - 7 1/4"; (NOZZLE_HEIGHT-(NOZZLE_HEIGHT/8*2))/2=1' - 0"; (NOZZLE_WB_OD-NOZZLE_TOP_OD)/2=0' - 2 1/8"; A=3' - 2"; A/2=1' - 7"; B=8' - 8"; B/2=4' - 4"; C=4' - 2"; C/2=2' - 1"; E=3' - 0 15/16"; GA=0' - 0 3/32"; Model=QMXVP-Isolation Box; NOZZLE_BOTTOM_ID=1' - 5 1/16"; NOZZLE_BOTTOM_RAD=0' - 8 17/32"; NOZZLE_HEIGHT=2' - 8"; NOZZLE_HEIGHT/7*2=0' - 8"; NOZZLE_SIZE=12' - 0"; NOZZLE_TOP_OD=1' - 7 1/2"; NOZZLE_TOP_RAD=0' - 9 3/4"; NOZZLE_WB/4=0' - 5 19/32"; NOZZLE_WB_OD=2' - 4"; NOZZLE_WB_RAD=1' - 2"; NOZZLE_WB_RAD-2"=1' - 0"; RO=2' - 6 3/4"; RO/2=1' - 3 3/8"; TRANSITION_TOP=5' - 7 9/16"; TYPE=0' - 0"; Type Comments=Vari-Plume Laboratory Exhaust Mixed-Flow Inline Belt Drive With Isolation Box; UNIT_HEIGHT=3' - 1 1/2"; UNIT_HEIGHT*.75=2' - 4 1/8"; UNIT_OD=2' - 4 3/4"; UNIT_RADIUS=1' - 2 3/8"; UNIT_RADIUS*.6=1' - 0 15/16"; UNIT_RADIUS+4"=1' - 6 3/8"
- 202_QMXVP-12H-Isolation_Box: (A/2)+.25"=1' - 7 1/4"; (NOZZLE_HEIGHT-(NOZZLE_HEIGHT/8*2))/2=1' - 0"; (NOZZLE_WB_OD-NOZZLE_TOP_OD)/2=0' - 2 1/8"; A=3' - 2"; A/2=1' - 7"; B=8' - 8"; B/2=4' - 4"; C=4' - 2"; C/2=2' - 1"; E=3' - 0 15/16"; GA=0' - 0 3/32"; Model=QMXVP-Isolation Box; NOZZLE_BOTTOM_ID=1' - 5 1/16"; NOZZLE_BOTTOM_RAD=0' - 8 17/32"; NOZZLE_HEIGHT=2' - 8"; NOZZLE_HEIGHT/7*2=0' - 8"; NOZZLE_SIZE=12' - 0"; NOZZLE_TOP_OD=1' - 7 1/2"; NOZZLE_TOP_RAD=0' - 9 3/4"; NOZZLE_WB/4=0' - 5 19/32"; NOZZLE_WB_OD=2' - 4"; NOZZLE_WB_RAD=1' - 2"; NOZZLE_WB_RAD-2"=1' - 0"; RO=2' - 6 3/4"; RO/2=1' - 3 3/8"; TRANSITION_TOP=5' - 7 9/16"; TYPE=0' - 0"; Type Comments=Vari-Plume Laboratory Exhaust Mixed-Flow Inline Belt Drive With Isolation Box; UNIT_HEIGHT=3' - 1 1/2"; UNIT_HEIGHT*.75=2' - 4 1/8"; UNIT_OD=2' - 4 3/4"; UNIT_RADIUS=1' - 2 3/8"; UNIT_RADIUS*.6=1' - 0 15/16"; UNIT_RADIUS+4"=1' - 6 3/8"
- 202_QMXVP-15L-Isolation_Box: (A/2)+.25"=1' - 7 1/4"; (NOZZLE_HEIGHT-(NOZZLE_HEIGHT/8*2))/2=1' - 4 1/8"; (NOZZLE_WB_OD-NOZZLE_TOP_OD)/2=0' - 3 1/4"; A=3' - 2"; A/2=1' - 7"; B=8' - 8"; B/2=4' - 4"; C=4' - 2"; C/2=2' - 1"; E=3' - 0 15/16"; GA=0' - 0 3/32"; Model=QMXVP-Isolation Box; NOZZLE_BOTTOM_ID=1' - 9 3/8"; NOZZLE_BOTTOM_RAD=0' - 10 11/16"; NOZZLE_HEIGHT=3' - 7"; NOZZLE_HEIGHT/7*2=0' - 10 3/4"; NOZZLE_SIZE=15' - 0"; NOZZLE_TOP_OD=1' - 11"; NOZZLE_TOP_RAD=0' - 11 1/2"; NOZZLE_WB/4=0' - 7 3/16"; NOZZLE_WB_OD=3' - 0"; NOZZLE_WB_RAD=1' - 6"; NOZZLE_WB_RAD-2"=1' - 4"; RO=2' - 6 3/4"; RO/2=1' - 3 3/8"; TRANSITION_TOP=4' - 11 5/8"; TYPE=0' - 0"; Type Comments=Vari-Plume Laboratory Exhaust Mixed-Flow Inline Belt Drive With Isolation Box; UNIT_HEIGHT=3' - 1 1/2"; UNIT_HEIGHT*.75=2' - 4 1/8"; UNIT_OD=2' - 4 3/4"; UNIT_RADIUS=1' - 2 3/8"; UNIT_RADIUS*.6=1' - 0 15/16"; UNIT_RADIUS+4"=1' - 6 3/8"
- 202_QMXVP-15H-Isolation_Box: (A/2)+.25"=1' - 7 1/4"; (NOZZLE_HEIGHT-(NOZZLE_HEIGHT/8*2))/2=1' - 4 1/8"; (NOZZLE_WB_OD-NOZZLE_TOP_OD)/2=0' - 3 1/4"; A=3' - 2"; A/2=1' - 7"; B=8' - 8"; B/2=4' - 4"; C=4' - 2"; C/2=2' - 1"; E=3' - 0 15/16"; GA=0' - 0 3/32"; Model=QMXVP-Isolation Box; NOZZLE_BOTTOM_ID=1' - 9 3/8"; NOZZLE_BOTTOM_RAD=0' - 10 11/16"; NOZZLE_HEIGHT=3' - 7"; NOZZLE_HEIGHT/7*2=0' - 10 3/4"; NOZZLE_SIZE=15' - 0"; NOZZLE_TOP_OD=1' - 11"; NOZZLE_TOP_RAD=0' - 11 1/2"; NOZZLE_WB/4=0' - 7 3/16"; NOZZLE_WB_OD=3' - 0"; NOZZLE_WB_RAD=1' - 6"; NOZZLE_WB_RAD-2"=1' - 4"; RO=2' - 6 3/4"; RO/2=1' - 3 3/8"; TRANSITION_TOP=4' - 11 5/8"; TYPE=0' - 0"; Type Comments=Vari-Plume Laboratory Exhaust Mixed-Flow Inline Belt Drive With Isolation Box; UNIT_HEIGHT=3' - 1 1/2"; UNIT_HEIGHT*.75=2' - 4 1/8"; UNIT_OD=2' - 4 3/4"; UNIT_RADIUS=1' - 2 3/8"; UNIT_RADIUS*.6=1' - 0 15/16"; UNIT_RADIUS+4"=1' - 6 3/8"
- 202_QMXVP-18L-Isolation_Box: (A/2)+.25"=1' - 7 1/4"; (NOZZLE_HEIGHT-(NOZZLE_HEIGHT/8*2))/2=1' - 6"; (NOZZLE_WB_OD-NOZZLE_TOP_OD)/2=0' - 3 7/8"; A=3' - 2"; A/2=1' - 7"; B=8' - 8"; B/2=4' - 4"; C=4' - 2"; C/2=2' - 1"; E=3' - 0 15/16"; GA=0' - 0 3/32"; Model=QMXVP-Isolation Box; NOZZLE_BOTTOM_ID=2' - 1 5/8"; NOZZLE_BOTTOM_RAD=1' - 0 13/16"; NOZZLE_HEIGHT=4' - 0"; NOZZLE_HEIGHT/7*2=1' - 0"; NOZZLE_SIZE=18' - 0"; NOZZLE_TOP_OD=2' - 3 1/2"; NOZZLE_TOP_RAD=1' - 1 3/4"; NOZZLE_WB/4=0' - 8 19/32"; NOZZLE_WB_OD=3' - 7"; NOZZLE_WB_RAD=1' - 9 1/2"; NOZZLE_WB_RAD-2"=1' - 7 1/2"; RO=2' - 6 3/4"; RO/2=1' - 3 3/8"; TRANSITION_TOP=4' - 3 5/8"; TYPE=0' - 0"; Type Comments=Vari-Plume Laboratory Exhaust Mixed-Flow Inline Belt Drive With Isolation Box; UNIT_HEIGHT=3' - 1 1/2"; UNIT_HEIGHT*.75=2' - 4 1/8"; UNIT_OD=2' - 4 3/4"; UNIT_RADIUS=1' - 2 3/8"; UNIT_RADIUS*.6=1' - 0 15/16"; UNIT_RADIUS+4"=1' - 6 3/8"
- 202_QMXVP-18H-Isolation_Box: (A/2)+.25"=1' - 7 1/4"; (NOZZLE_HEIGHT-(NOZZLE_HEIGHT/8*2))/2=1' - 6"; (NOZZLE_WB_OD-NOZZLE_TOP_OD)/2=0' - 3 7/8"; A=3' - 2"; A/2=1' - 7"; B=8' - 8"; B/2=4' - 4"; C=4' - 2"; C/2=2' - 1"; E=3' - 0 15/16"; GA=0' - 0 3/32"; Model=QMXVP-Isolation Box; NOZZLE_BOTTOM_ID=2' - 1 5/8"; NOZZLE_BOTTOM_RAD=1' - 0 13/16"; NOZZLE_HEIGHT=4' - 0"; NOZZLE_HEIGHT/7*2=1' - 0"; NOZZLE_SIZE=18' - 0"; NOZZLE_TOP_OD=2' - 3 1/2"; NOZZLE_TOP_RAD=1' - 1 3/4"; NOZZLE_WB/4=0' - 8 19/32"; NOZZLE_WB_OD=3' - 7"; NOZZLE_WB_RAD=1' - 9 1/2"; NOZZLE_WB_RAD-2"=1' - 7 1/2"; RO=2' - 6 3/4"; RO/2=1' - 3 3/8"; TRANSITION_TOP=4' - 3 5/8"; TYPE=0' - 0"; Type Comments=Vari-Plume Laboratory Exhaust Mixed-Flow Inline Belt Drive With Isolation Box; UNIT_HEIGHT=3' - 1 1/2"; UNIT_HEIGHT*.75=2' - 4 1/8"; UNIT_OD=2' - 4 3/4"; UNIT_RADIUS=1' - 2 3/8"; UNIT_RADIUS*.6=1' - 0 15/16"; UNIT_RADIUS+4"=1' - 6 3/8"
- 225_QMXVP-12L-Isolation_Box: (A/2)+.25"=1' - 9 1/4"; (NOZZLE_HEIGHT-(NOZZLE_HEIGHT/8*2))/2=1' - 0"; (NOZZLE_WB_OD-NOZZLE_TOP_OD)/2=0' - 2 1/8"; A=3' - 6"; A/2=1' - 9"; B=9' - 5"; B/2=4' - 8 1/2"; C=4' - 8"; C/2=2' - 4"; E=3' - 4 15/16"; GA=0' - 0 3/32"; Model=QMXVP-Isolation Box; NOZZLE_BOTTOM_ID=1' - 5 1/16"; NOZZLE_BOTTOM_RAD=0' - 8 17/32"; NOZZLE_HEIGHT=2' - 8"; NOZZLE_HEIGHT/7*2=0' - 8"; NOZZLE_SIZE=12' - 0"; NOZZLE_TOP_OD=1' - 7 1/2"; NOZZLE_TOP_RAD=0' - 9 3/4"; NOZZLE_WB/4=0' - 5 19/32"; NOZZLE_WB_OD=2' - 4"; NOZZLE_WB_RAD=1' - 2"; NOZZLE_WB_RAD-2"=1' - 0"; RO=2' - 10 3/4"; RO/2=1' - 5 3/8"; TRANSITION_TOP=6' - 5 1/16"; TYPE=0' - 0"; Type Comments=Vari-Plume Laboratory Exhaust Mixed-Flow Inline Belt Drive With Isolation Box; UNIT_HEIGHT=3' - 5"; UNIT_HEIGHT*.75=2' - 6 3/4"; UNIT_OD=2' - 7 15/16"; UNIT_RADIUS=1' - 3 31/32"; UNIT_RADIUS*.6=1' - 2 3/8"; UNIT_RADIUS+4"=1' - 7 31/32"
- 225_QMXVP-12H-Isolation_Box: (A/2)+.25"=1' - 9 1/4"; (NOZZLE_HEIGHT-(NOZZLE_HEIGHT/8*2))/2=1' - 0"; (NOZZLE_WB_OD-NOZZLE_TOP_OD)/2=0' - 2 1/8"; A=3' - 6"; A/2=1' - 9"; B=9' - 5"; B/2=4' - 8 1/2"; C=4' - 8"; C/2=2' - 4"; E=3' - 4 15/16"; GA=0' - 0 3/32"; Model=QMXVP-Isolation Box; NOZZLE_BOTTOM_ID=1' - 5 1/16"; NOZZLE_BOTTOM_RAD=0' - 8 17/32"; NOZZLE_HEIGHT=2' - 8"; NOZZLE_HEIGHT/7*2=0' - 8"; NOZZLE_SIZE=12' - 0"; NOZZLE_TOP_OD=1' - 7 1/2"; NOZZLE_TOP_RAD=0' - 9 3/4"; NOZZLE_WB/4=0' - 5 19/32"; NOZZLE_WB_OD=2' - 4"; NOZZLE_WB_RAD=1' - 2"; NOZZLE_WB_RAD-2"=1' - 0"; RO=2' - 10 3/4"; RO/2=1' - 5 3/8"; TRANSITION_TOP=6' - 5 1/16"; TYPE=0' - 0"; Type Comments=Vari-Plume Laboratory Exhaust Mixed-Flow Inline Belt Drive With Isolation Box; UNIT_HEIGHT=3' - 5"; UNIT_HEIGHT*.75=2' - 6 3/4"; UNIT_OD=2' - 7 15/16"; UNIT_RADIUS=1' - 3 31/32"; UNIT_RADIUS*.6=1' - 2 3/8"; UNIT_RADIUS+4"=1' - 7 31/32"
- 225_QMXVP-15L-Isolation_Box: (A/2)+.25"=1' - 9 1/4"; (NOZZLE_HEIGHT-(NOZZLE_HEIGHT/8*2))/2=1' - 4 1/8"; (NOZZLE_WB_OD-NOZZLE_TOP_OD)/2=0' - 3 1/4"; A=3' - 6"; A/2=1' - 9"; B=9' - 5"; B/2=4' - 8 1/2"; C=4' - 8"; C/2=2' - 4"; E=3' - 4 15/16"; GA=0' - 0 3/32"; Model=QMXVP-Isolation Box; NOZZLE_BOTTOM_ID=1' - 9 3/8"; NOZZLE_BOTTOM_RAD=0' - 10 11/16"; NOZZLE_HEIGHT=3' - 7"; NOZZLE_HEIGHT/7*2=0' - 10 3/4"; NOZZLE_SIZE=15' - 0"; NOZZLE_TOP_OD=1' - 11"; NOZZLE_TOP_RAD=0' - 11 1/2"; NOZZLE_WB/4=0' - 7 3/16"; NOZZLE_WB_OD=3' - 0"; NOZZLE_WB_RAD=1' - 6"; NOZZLE_WB_RAD-2"=1' - 4"; RO=2' - 10 3/4"; RO/2=1' - 5 3/8"; TRANSITION_TOP=5' - 9 1/8"; TYPE=0' - 0"; Type Comments=Vari-Plume Laboratory Exhaust Mixed-Flow Inline Belt Drive With Isolation Box; UNIT_HEIGHT=3' - 5"; UNIT_HEIGHT*.75=2' - 6 3/4"; UNIT_OD=2' - 7 15/16"; UNIT_RADIUS=1' - 3 31/32"; UNIT_RADIUS*.6=1' - 2 3/8"; UNIT_RADIUS+4"=1' - 7 31/32"
- 225_QMXVP-15H-Isolation_Box: (A/2)+.25"=1' - 9 1/4"; (NOZZLE_HEIGHT-(NOZZLE_HEIGHT/8*2))/2=1' - 4 1/8"; (NOZZLE_WB_OD-NOZZLE_TOP_OD)/2=0' - 3 1/4"; A=3' - 6"; A/2=1' - 9"; B=9' - 5"; B/2=4' - 8 1/2"; C=4' - 8"; C/2=2' - 4"; E=3' - 4 15/16"; GA=0' - 0 3/32"; Model=QMXVP-Isolation Box; NOZZLE_BOTTOM_ID=1' - 9 3/8"; NOZZLE_BOTTOM_RAD=0' - 10 11/16"; NOZZLE_HEIGHT=3' - 7"; NOZZLE_HEIGHT/7*2=0' - 10 3/4"; NOZZLE_SIZE=15' - 0"; NOZZLE_TOP_OD=1' - 11"; NOZZLE_TOP_RAD=0' - 11 1/2"; NOZZLE_WB/4=0' - 7 3/16"; NOZZLE_WB_OD=3' - 0"; NOZZLE_WB_RAD=1' - 6"; NOZZLE_WB_RAD-2"=1' - 4"; RO=2' - 10 3/4"; RO/2=1' - 5 3/8"; TRANSITION_TOP=5' - 9 1/8"; TYPE=0' - 0"; Type Comments=Vari-Plume Laboratory Exhaust Mixed-Flow Inline Belt Drive With Isolation Box; UNIT_HEIGHT=3' - 5"; UNIT_HEIGHT*.75=2' - 6 3/4"; UNIT_OD=2' - 7 15/16"; UNIT_RADIUS=1' - 3 31/32"; UNIT_RADIUS*.6=1' - 2 3/8"; UNIT_RADIUS+4"=1' - 7 31/32"
- 225_QMXVP-18L-Isolation_Box: (A/2)+.25"=1' - 9 1/4"; (NOZZLE_HEIGHT-(NOZZLE_HEIGHT/8*2))/2=1' - 6"; (NOZZLE_WB_OD-NOZZLE_TOP_OD)/2=0' - 3 7/8"; A=3' - 6"; A/2=1' - 9"; B=9' - 5"; B/2=4' - 8 1/2"; C=4' - 8"; C/2=2' - 4"; E=3' - 4 15/16"; GA=0' - 0 3/32"; Model=QMXVP-Isolation Box; NOZZLE_BOTTOM_ID=2' - 1 5/8"; NOZZLE_BOTTOM_RAD=1' - 0 13/16"; NOZZLE_HEIGHT=4' - 0"; NOZZLE_HEIGHT/7*2=1' - 0"; NOZZLE_SIZE=18' - 0"; NOZZLE_TOP_OD=2' - 3 1/2"; NOZZLE_TOP_RAD=1' - 1 3/4"; NOZZLE_WB/4=0' - 8 19/32"; NOZZLE_WB_OD=3' - 7"; NOZZLE_WB_RAD=1' - 9 1/2"; NOZZLE_WB_RAD-2"=1' - 7 1/2"; RO=2' - 10 3/4"; RO/2=1' - 5 3/8"; TRANSITION_TOP=5' - 1 1/8"; TYPE=0' - 0"; Type Comments=Vari-Plume Laboratory Exhaust Mixed-Flow Inline Belt Drive With Isolation Box; UNIT_HEIGHT=3' - 5"; UNIT_HEIGHT*.75=2' - 6 3/4"; UNIT_OD=2' - 7 15/16"; UNIT_RADIUS=1' - 3 31/32"; UNIT_RADIUS*.6=1' - 2 3/8"; UNIT_RADIUS+4"=1' - 7 31/32"
- 245_QMXVP-15L-Isolation_Box: (A/2)+.25"=1' - 10 1/4"; (NOZZLE_HEIGHT-(NOZZLE_HEIGHT/8*2))/2=1' - 4 1/8"; (NOZZLE_WB_OD-NOZZLE_TOP_OD)/2=0' - 3 1/4"; A=3' - 8"; A/2=1' - 10"; B=10' - 1"; B/2=5' - 0 1/2"; C=4' - 11"; C/2=2' - 5 1/2"; E=3' - 6 15/16"; GA=0' - 0 3/32"; Model=QMXVP-Isolation Box; NOZZLE_BOTTOM_ID=1' - 9 3/8"; NOZZLE_BOTTOM_RAD=0' - 10 11/16"; NOZZLE_HEIGHT=3' - 7"; NOZZLE_HEIGHT/7*2=0' - 10 3/4"; NOZZLE_SIZE=15' - 0"; NOZZLE_TOP_OD=1' - 11"; NOZZLE_TOP_RAD=0' - 11 1/2"; NOZZLE_WB/4=0' - 7 3/16"; NOZZLE_WB_OD=3' - 0"; NOZZLE_WB_RAD=1' - 6"; NOZZLE_WB_RAD-2"=1' - 4"; RO=3' - 0 3/4"; RO/2=1' - 6 3/8"; TRANSITION_TOP=6' - 5 11/16"; TYPE=0' - 0"; Type Comments=Vari-Plume Laboratory Exhaust Mixed-Flow Inline Belt Drive With Isolation Box; UNIT_HEIGHT=3' - 8 1/2"; UNIT_HEIGHT*.75=2' - 9 3/8"; UNIT_OD=2' - 10 3/4"; UNIT_RADIUS=1' - 5 3/8"; UNIT_RADIUS*.6=1' - 3 5/8"; UNIT_RADIUS+4"=1' - 9 3/8"
- 245_QMXVP-15H-Isolation_Box: (A/2)+.25"=1' - 10 1/4"; (NOZZLE_HEIGHT-(NOZZLE_HEIGHT/8*2))/2=1' - 4 1/8"; (NOZZLE_WB_OD-NOZZLE_TOP_OD)/2=0' - 3 1/4"; A=3' - 8"; A/2=1' - 10"; B=10' - 1"; B/2=5' - 0 1/2"; C=4' - 11"; C/2=2' - 5 1/2"; E=3' - 6 15/16"; GA=0' - 0 3/32"; Model=QMXVP-Isolation Box; NOZZLE_BOTTOM_ID=1' - 9 3/8"; NOZZLE_BOTTOM_RAD=0' - 10 11/16"; NOZZLE_HEIGHT=3' - 7"; NOZZLE_HEIGHT/7*2=0' - 10 3/4"; NOZZLE_SIZE=15' - 0"; NOZZLE_TOP_OD=1' - 11"; NOZZLE_TOP_RAD=0' - 11 1/2"; NOZZLE_WB/4=0' - 7 3/16"; NOZZLE_WB_OD=3' - 0"; NOZZLE_WB_RAD=1' - 6"; NOZZLE_WB_RAD-2"=1' - 4"; RO=3' - 0 3/4"; RO/2=1' - 6 3/8"; TRANSITION_TOP=6' - 5 11/16"; TYPE=0' - 0"; Type Comments=Vari-Plume Laboratory Exhaust Mixed-Flow Inline Belt Drive With Isolation Box; UNIT_HEIGHT=3' - 8 1/2"; UNIT_HEIGHT*.75=2' - 9 3/8"; UNIT_OD=2' - 10 3/4"; UNIT_RADIUS=1' - 5 3/8"; UNIT_RADIUS*.6=1' - 3 5/8"; UNIT_RADIUS+4"=1' - 9 3/8"
- 245_QMXVP-18L-Isolation_Box: (A/2)+.25"=1' - 10 1/4"; (NOZZLE_HEIGHT-(NOZZLE_HEIGHT/8*2))/2=1' - 6"; (NOZZLE_WB_OD-NOZZLE_TOP_OD)/2=0' - 3 7/8"; A=3' - 8"; A/2=1' - 10"; B=10' - 1"; B/2=5' - 0 1/2"; C=4' - 11"; C/2=2' - 5 1/2"; E=3' - 6 15/16"; GA=0' - 0 3/32"; Model=QMXVP-Isolation Box; NOZZLE_BOTTOM_ID=2' - 1 5/8"; NOZZLE_BOTTOM_RAD=1' - 0 13/16"; NOZZLE_HEIGHT=4' - 0"; NOZZLE_HEIGHT/7*2=1' - 0"; NOZZLE_SIZE=18' - 0"; NOZZLE_TOP_OD=2' - 3 1/2"; NOZZLE_TOP_RAD=1' - 1 3/4"; NOZZLE_WB/4=0' - 8 19/32"; NOZZLE_WB_OD=3' - 7"; NOZZLE_WB_RAD=1' - 9 1/2"; NOZZLE_WB_RAD-2"=1' - 7 1/2"; RO=3' - 0 3/4"; RO/2=1' - 6 3/8"; TRANSITION_TOP=5' - 9 11/16"; TYPE=0' - 0"; Type Comments=Vari-Plume Laboratory Exhaust Mixed-Flow Inline Belt Drive With Isolation Box; UNIT_HEIGHT=3' - 8 1/2"; UNIT_HEIGHT*.75=2' - 9 3/8"; UNIT_OD=2' - 10 3/4"; UNIT_RADIUS=1' - 5 3/8"; UNIT_RADIUS*.6=1' - 3 5/8"; UNIT_RADIUS+4"=1' - 9 3/8"
- 245_QMXVP-18H-Isolation_Box: (A/2)+.25"=1' - 10 1/4"; (NOZZLE_HEIGHT-(NOZZLE_HEIGHT/8*2))/2=1' - 6"; (NOZZLE_WB_OD-NOZZLE_TOP_OD)/2=0' - 3 7/8"; A=3' - 8"; A/2=1' - 10"; B=10' - 1"; B/2=5' - 0 1/2"; C=4' - 11"; C/2=2' - 5 1/2"; E=3' - 6 15/16"; GA=0' - 0 3/32"; Model=QMXVP-Isolation Box; NOZZLE_BOTTOM_ID=2' - 1 5/8"; NOZZLE_BOTTOM_RAD=1' - 0 13/16"; NOZZLE_HEIGHT=4' - 0"; NOZZLE_HEIGHT/7*2=1' - 0"; NOZZLE_SIZE=18' - 0"; NOZZLE_TOP_OD=2' - 3 1/2"; NOZZLE_TOP_RAD=1' - 1 3/4"; NOZZLE_WB/4=0' - 8 19/32"; NOZZLE_WB_OD=3' - 7"; NOZZLE_WB_RAD=1' - 9 1/2"; NOZZLE_WB_RAD-2"=1' - 7 1/2"; RO=3' - 0 3/4"; RO/2=1' - 6 3/8"; TRANSITION_TOP=5' - 9 11/16"; TYPE=0' - 0"; Type Comments=Vari-Plume Laboratory Exhaust Mixed-Flow Inline Belt Drive With Isolation Box; UNIT_HEIGHT=3' - 8 1/2"; UNIT_HEIGHT*.75=2' - 9 3/8"; UNIT_OD=2' - 10 3/4"; UNIT_RADIUS=1' - 5 3/8"; UNIT_RADIUS*.6=1' - 3 5/8"; UNIT_RADIUS+4"=1' - 9 3/8"
- 245_QMXVP-24L-Isolation_Box: (A/2)+.25"=1' - 10 1/4"; (NOZZLE_HEIGHT-(NOZZLE_HEIGHT/8*2))/2=1' - 11 1/4"; (NOZZLE_WB_OD-NOZZLE_TOP_OD)/2=0' - 6 1/8"; A=3' - 8"; A/2=1' - 10"; B=10' - 1"; B/2=5' - 0 1/2"; C=4' - 11"; C/2=2' - 5 1/2"; E=3' - 6 15/16"; GA=0' - 0 3/32"; Model=QMXVP-Isolation Box; NOZZLE_BOTTOM_ID=2' - 10 3/4"; NOZZLE_BOTTOM_RAD=1' - 5 3/8"; NOZZLE_HEIGHT=5' - 2"; NOZZLE_HEIGHT/7*2=1' - 3 1/2"; NOZZLE_SIZE=24' - 0"; NOZZLE_TOP_OD=3' - 0 1/2"; NOZZLE_TOP_RAD=1' - 6 1/4"; NOZZLE_WB/4=1' - 0 3/16"; NOZZLE_WB_OD=5' - 1"; NOZZLE_WB_RAD=2' - 6 1/2"; NOZZLE_WB_RAD-2"=2' - 4 1/2"; RO=3' - 0 3/4"; RO/2=1' - 6 3/8"; TRANSITION_TOP=4' - 9 3/4"; TYPE=0' - 0"; Type Comments=Vari-Plume Laboratory Exhaust Mixed-Flow Inline Belt Drive With Isolation Box; UNIT_HEIGHT=3' - 8 1/2"; UNIT_HEIGHT*.75=2' - 9 3/8"; UNIT_OD=2' - 10 3/4"; UNIT_RADIUS=1' - 5 3/8"; UNIT_RADIUS*.6=1' - 3 5/8"; UNIT_RADIUS+4"=1' - 9 3/8"
- 245_QMXVP-24H-Isolation_Box: (A/2)+.25"=1' - 10 1/4"; (NOZZLE_HEIGHT-(NOZZLE_HEIGHT/8*2))/2=1' - 11 1/4"; (NOZZLE_WB_OD-NOZZLE_TOP_OD)/2=0' - 6 1/8"; A=3' - 8"; A/2=1' - 10"; B=10' - 1"; B/2=5' - 0 1/2"; C=4' - 11"; C/2=2' - 5 1/2"; E=3' - 6 15/16"; GA=0' - 0 3/32"; Model=QMXVP-Isolation Box; NOZZLE_BOTTOM_ID=2' - 10 3/4"; NOZZLE_BOTTOM_RAD=1' - 5 3/8"; NOZZLE_HEIGHT=5' - 2"; NOZZLE_HEIGHT/7*2=1' - 3 1/2"; NOZZLE_SIZE=24' - 0"; NOZZLE_TOP_OD=3' - 0 1/2"; NOZZLE_TOP_RAD=1' - 6 1/4"; NOZZLE_WB/4=1' - 0 3/16"; NOZZLE_WB_OD=5' - 1"; NOZZLE_WB_RAD=2' - 6 1/2"; NOZZLE_WB_RAD-2"=2' - 4 1/2"; RO=3' - 0 3/4"; RO/2=1' - 6 3/8"; TRANSITION_TOP=4' - 9 3/4"; TYPE=0' - 0"; Type Comments=Vari-Plume Laboratory Exhaust Mixed-Flow Inline Belt Drive With Isolation Box; UNIT_HEIGHT=3' - 8 1/2"; UNIT_HEIGHT*.75=2' - 9 3/8"; UNIT_OD=2' - 10 3/4"; UNIT_RADIUS=1' - 5 3/8"; UNIT_RADIUS*.6=1' - 3 5/8"; UNIT_RADIUS+4"=1' - 9 3/8"
- 270_QMXVP-15L-Isolation_Box: (A/2)+.25"=2' - 0 1/4"; (NOZZLE_HEIGHT-(NOZZLE_HEIGHT/8*2))/2=1' - 4 1/8"; (NOZZLE_WB_OD-NOZZLE_TOP_OD)/2=0' - 3 1/4"; A=4' - 0"; A/2=2' - 0"; B=10' - 8"; B/2=5' - 4"; C=5' - 3"; C/2=2' - 7 1/2"; E=3' - 10 15/16"; GA=0' - 0 3/32"; Model=QMXVP-Isolation Box; NOZZLE_BOTTOM_ID=1' - 9 3/8"; NOZZLE_BOTTOM_RAD=0' - 10 11/16"; NOZZLE_HEIGHT=3' - 7"; NOZZLE_HEIGHT/7*2=0' - 10 3/4"; NOZZLE_SIZE=15' - 0"; NOZZLE_TOP_OD=1' - 11"; NOZZLE_TOP_RAD=0' - 11 1/2"; NOZZLE_WB/4=0' - 7 3/16"; NOZZLE_WB_OD=3' - 0"; NOZZLE_WB_RAD=1' - 6"; NOZZLE_WB_RAD-2"=1' - 4"; RO=3' - 4 3/4"; RO/2=1' - 8 3/8"; TRANSITION_TOP=7' - 2 3/16"; TYPE=0' - 0"; Type Comments=Vari-Plume Laboratory Exhaust Mixed-Flow Inline Belt Drive With Isolation Box; UNIT_HEIGHT=3' - 11"; UNIT_HEIGHT*.75=2' - 11 1/4"; UNIT_OD=3' - 2 5/16"; UNIT_RADIUS=1' - 7 5/32"; UNIT_RADIUS*.6=1' - 5 1/4"; UNIT_RADIUS+4"=1' - 11 5/32"
- 270_QMXVP-15H-Isolation_Box: (A/2)+.25"=2' - 0 1/4"; (NOZZLE_HEIGHT-(NOZZLE_HEIGHT/8*2))/2=1' - 4 1/8"; (NOZZLE_WB_OD-NOZZLE_TOP_OD)/2=0' - 3 1/4"; A=4' - 0"; A/2=2' - 0"; B=10' - 8"; B/2=5' - 4"; C=5' - 3"; C/2=2' - 7 1/2"; E=3' - 10 15/16"; GA=0' - 0 3/32"; Model=QMXVP-Isolation Box; NOZZLE_BOTTOM_ID=1' - 9 3/8"; NOZZLE_BOTTOM_RAD=0' - 10 11/16"; NOZZLE_HEIGHT=3' - 7"; NOZZLE_HEIGHT/7*2=0' - 10 3/4"; NOZZLE_SIZE=15' - 0"; NOZZLE_TOP_OD=1' - 11"; NOZZLE_TOP_RAD=0' - 11 1/2"; NOZZLE_WB/4=0' - 7 3/16"; NOZZLE_WB_OD=3' - 0"; NOZZLE_WB_RAD=1' - 6"; NOZZLE_WB_RAD-2"=1' - 4"; RO=3' - 4 3/4"; RO/2=1' - 8 3/8"; TRANSITION_TOP=7' - 2 3/16"; TYPE=0' - 0"; Type Comments=Vari-Plume Laboratory Exhaust Mixed-Flow Inline Belt Drive With Isolation Box; UNIT_HEIGHT=3' - 11"; UNIT_HEIGHT*.75=2' - 11 1/4"; UNIT_OD=3' - 2 5/16"; UNIT_RADIUS=1' - 7 5/32"; UNIT_RADIUS*.6=1' - 5 1/4"; UNIT_RADIUS+4"=1' - 11 5/32"
- 270_QMXVP-18L-Isolation_Box: (A/2)+.25"=2' - 0 1/4"; (NOZZLE_HEIGHT-(NOZZLE_HEIGHT/8*2))/2=1' - 6"; (NOZZLE_WB_OD-NOZZLE_TOP_OD)/2=0' - 3 7/8"; A=4' - 0"; A/2=2' - 0"; B=10' - 8"; B/2=5' - 4"; C=5' - 3"; C/2=2' - 7 1/2"; E=3' - 10 15/16"; GA=0' - 0 3/32"; Model=QMXVP-Isolation Box; NOZZLE_BOTTOM_ID=2' - 1 5/8"; NOZZLE_BOTTOM_RAD=1' - 0 13/16"; NOZZLE_HEIGHT=4' - 0"; NOZZLE_HEIGHT/7*2=1' - 0"; NOZZLE_SIZE=18' - 0"; NOZZLE_TOP_OD=2' - 3 1/2"; NOZZLE_TOP_RAD=1' - 1 3/4"; NOZZLE_WB/4=0' - 8 19/32"; NOZZLE_WB_OD=3' - 7"; NOZZLE_WB_RAD=1' - 9 1/2"; NOZZLE_WB_RAD-2"=1' - 7 1/2"; RO=3' - 4 3/4"; RO/2=1' - 8 3/8"; TRANSITION_TOP=6' - 7 3/16"; TYPE=0' - 0"; Type Comments=Vari-Plume Laboratory Exhaust Mixed-Flow Inline Belt Drive With Isolation Box; UNIT_HEIGHT=3' - 11"; UNIT_HEIGHT*.75=2' - 11 1/4"; UNIT_OD=3' - 2 5/16"; UNIT_RADIUS=1' - 7 5/32"; UNIT_RADIUS*.6=1' - 5 1/4"; UNIT_RADIUS+4"=1' - 11 5/32"
- 270_QMXVP-18H-Isolation_Box: (A/2)+.25"=2' - 0 1/4"; (NOZZLE_HEIGHT-(NOZZLE_HEIGHT/8*2))/2=1' - 6"; (NOZZLE_WB_OD-NOZZLE_TOP_OD)/2=0' - 3 7/8"; A=4' - 0"; A/2=2' - 0"; B=10' - 8"; B/2=5' - 4"; C=5' - 3"; C/2=2' - 7 1/2"; E=3' - 10 15/16"; GA=0' - 0 3/32"; Model=QMXVP-Isolation Box; NOZZLE_BOTTOM_ID=2' - 1 5/8"; NOZZLE_BOTTOM_RAD=1' - 0 13/16"; NOZZLE_HEIGHT=4' - 0"; NOZZLE_HEIGHT/7*2=1' - 0"; NOZZLE_SIZE=18' - 0"; NOZZLE_TOP_OD=2' - 3 1/2"; NOZZLE_TOP_RAD=1' - 1 3/4"; NOZZLE_WB/4=0' - 8 19/32"; NOZZLE_WB_OD=3' - 7"; NOZZLE_WB_RAD=1' - 9 1/2"; NOZZLE_WB_RAD-2"=1' - 7 1/2"; RO=3' - 4 3/4"; RO/2=1' - 8 3/8"; TRANSITION_TOP=6' - 7 3/16"; TYPE=0' - 0"; Type Comments=Vari-Plume Laboratory Exhaust Mixed-Flow Inline Belt Drive With Isolation Box; UNIT_HEIGHT=3' - 11"; UNIT_HEIGHT*.75=2' - 11 1/4"; UNIT_OD=3' - 2 5/16"; UNIT_RADIUS=1' - 7 5/32"; UNIT_RADIUS*.6=1' - 5 1/4"; UNIT_RADIUS+4"=1' - 11 5/32"
- 270_QMXVP-24L-Isolation_Box: (A/2)+.25"=2' - 0 1/4"; (NOZZLE_HEIGHT-(NOZZLE_HEIGHT/8*2))/2=1' - 11 1/4"; (NOZZLE_WB_OD-NOZZLE_TOP_OD)/2=0' - 6 1/8"; A=4' - 0"; A/2=2' - 0"; B=10' - 8"; B/2=5' - 4"; C=5' - 3"; C/2=2' - 7 1/2"; E=3' - 10 15/16"; GA=0' - 0 3/32"; Model=QMXVP-Isolation Box; NOZZLE_BOTTOM_ID=2' - 10 3/4"; NOZZLE_BOTTOM_RAD=1' - 5 3/8"; NOZZLE_HEIGHT=5' - 2"; NOZZLE_HEIGHT/7*2=1' - 3 1/2"; NOZZLE_SIZE=24' - 0"; NOZZLE_TOP_OD=3' - 0 1/2"; NOZZLE_TOP_RAD=1' - 6 1/4"; NOZZLE_WB/4=1' - 0 3/16"; NOZZLE_WB_OD=5' - 1"; NOZZLE_WB_RAD=2' - 6 1/2"; NOZZLE_WB_RAD-2"=2' - 4 1/2"; RO=3' - 4 3/4"; RO/2=1' - 8 3/8"; TRANSITION_TOP=5' - 2 1/4"; TYPE=0' - 0"; Type Comments=Vari-Plume Laboratory Exhaust Mixed-Flow Inline Belt Drive With Isolation Box; UNIT_HEIGHT=3' - 11"; UNIT_HEIGHT*.75=2' - 11 1/4"; UNIT_OD=3' - 2 5/16"; UNIT_RADIUS=1' - 7 5/32"; UNIT_RADIUS*.6=1' - 5 1/4"; UNIT_RADIUS+4"=1' - 11 5/32"
- 270_QMXVP-24H-Isolation_Box: (A/2)+.25"=2' - 0 1/4"; (NOZZLE_HEIGHT-(NOZZLE_HEIGHT/8*2))/2=1' - 11 1/4"; (NOZZLE_WB_OD-NOZZLE_TOP_OD)/2=0' - 6 1/8"; A=4' - 0"; A/2=2' - 0"; B=10' - 8"; B/2=5' - 4"; C=5' - 3"; C/2=2' - 7 1/2"; E=3' - 10 15/16"; GA=0' - 0 3/32"; Model=QMXVP-Isolation Box; NOZZLE_BOTTOM_ID=2' - 10 3/4"; NOZZLE_BOTTOM_RAD=1' - 5 3/8"; NOZZLE_HEIGHT=5' - 2"; NOZZLE_HEIGHT/7*2=1' - 3 1/2"; NOZZLE_SIZE=24' - 0"; NOZZLE_TOP_OD=3' - 0 1/2"; NOZZLE_TOP_RAD=1' - 6 1/4"; NOZZLE_WB/4=1' - 0 3/16"; NOZZLE_WB_OD=5' - 1"; NOZZLE_WB_RAD=2' - 6 1/2"; NOZZLE_WB_RAD-2"=2' - 4 1/2"; RO=3' - 4 3/4"; RO/2=1' - 8 3/8"; TRANSITION_TOP=5' - 2 1/4"; TYPE=0' - 0"; Type Comments=Vari-Plume Laboratory Exhaust Mixed-Flow Inline Belt Drive With Isolation Box; UNIT_HEIGHT=3' - 11"; UNIT_HEIGHT*.75=2' - 11 1/4"; UNIT_OD=3' - 2 5/16"; UNIT_RADIUS=1' - 7 5/32"; UNIT_RADIUS*.6=1' - 5 1/4"; UNIT_RADIUS+4"=1' - 11 5/32"
- 300_QMXVP-18L-Isolation_Box: (A/2)+.25"=2' - 2 1/4"; (NOZZLE_HEIGHT-(NOZZLE_HEIGHT/8*2))/2=1' - 6"; (NOZZLE_WB_OD-NOZZLE_TOP_OD)/2=0' - 3 7/8"; A=4' - 4"; A/2=2' - 2"; B=12' - 4"; B/2=6' - 2"; C=5' - 7"; C/2=2' - 9 1/2"; E=4' - 2 15/16"; GA=0' - 0 3/32"; Model=QMXVP-Isolation Box; NOZZLE_BOTTOM_ID=2' - 1 5/8"; NOZZLE_BOTTOM_RAD=1' - 0 13/16"; NOZZLE_HEIGHT=4' - 0"; NOZZLE_HEIGHT/7*2=1' - 0"; NOZZLE_SIZE=18' - 0"; NOZZLE_TOP_OD=2' - 3 1/2"; NOZZLE_TOP_RAD=1' - 1 3/4"; NOZZLE_WB/4=0' - 8 19/32"; NOZZLE_WB_OD=3' - 7"; NOZZLE_WB_RAD=1' - 9 1/2"; NOZZLE_WB_RAD-2"=1' - 7 1/2"; RO=3' - 8 3/4"; RO/2=1' - 10 3/8"; TRANSITION_TOP=7' - 10 3/16"; TYPE=0' - 0"; Type Comments=Vari-Plume Laboratory Exhaust Mixed-Flow Inline Belt Drive With Isolation Box; UNIT_HEIGHT=4' - 6"; UNIT_HEIGHT*.75=3' - 4 1/2"; UNIT_OD=3' - 6 1/2"; UNIT_RADIUS=1' - 9 1/4"; UNIT_RADIUS*.6=1' - 7 1/8"; UNIT_RADIUS+4"=2' - 1 1/4"
- 300_QMXVP-18H-Isolation_Box: (A/2)+.25"=2' - 2 1/4"; (NOZZLE_HEIGHT-(NOZZLE_HEIGHT/8*2))/2=1' - 6"; (NOZZLE_WB_OD-NOZZLE_TOP_OD)/2=0' - 3 7/8"; A=4' - 4"; A/2=2' - 2"; B=12' - 4"; B/2=6' - 2"; C=5' - 7"; C/2=2' - 9 1/2"; E=4' - 2 15/16"; GA=0' - 0 3/32"; Model=QMXVP-Isolation Box; NOZZLE_BOTTOM_ID=2' - 1 5/8"; NOZZLE_BOTTOM_RAD=1' - 0 13/16"; NOZZLE_HEIGHT=4' - 0"; NOZZLE_HEIGHT/7*2=1' - 0"; NOZZLE_SIZE=18' - 0"; NOZZLE_TOP_OD=2' - 3 1/2"; NOZZLE_TOP_RAD=1' - 1 3/4"; NOZZLE_WB/4=0' - 8 19/32"; NOZZLE_WB_OD=3' - 7"; NOZZLE_WB_RAD=1' - 9 1/2"; NOZZLE_WB_RAD-2"=1' - 7 1/2"; RO=3' - 8 3/4"; RO/2=1' - 10 3/8"; TRANSITION_TOP=7' - 10 3/16"; TYPE=0' - 0"; Type Comments=Vari-Plume Laboratory Exhaust Mixed-Flow Inline Belt Drive With Isolation Box; UNIT_HEIGHT=4' - 6"; UNIT_HEIGHT*.75=3' - 4 1/2"; UNIT_OD=3' - 6 1/2"; UNIT_RADIUS=1' - 9 1/4"; UNIT_RADIUS*.6=1' - 7 1/8"; UNIT_RADIUS+4"=2' - 1 1/4"
- 300_QMXVP-24L-Isolation_Box: (A/2)+.25"=2' - 2 1/4"; (NOZZLE_HEIGHT-(NOZZLE_HEIGHT/8*2))/2=1' - 11 1/4"; (NOZZLE_WB_OD-NOZZLE_TOP_OD)/2=0' - 6 1/8"; A=4' - 4"; A/2=2' - 2"; B=12' - 4"; B/2=6' - 2"; C=5' - 7"; C/2=2' - 9 1/2"; E=4' - 2 15/16"; GA=0' - 0 3/32"; Model=QMXVP-Isolation Box; NOZZLE_BOTTOM_ID=2' - 10 3/4"; NOZZLE_BOTTOM_RAD=1' - 5 3/8"; NOZZLE_HEIGHT=5' - 2"; NOZZLE_HEIGHT/7*2=1' - 3 1/2"; NOZZLE_SIZE=24' - 0"; NOZZLE_TOP_OD=3' - 0 1/2"; NOZZLE_TOP_RAD=1' - 6 1/4"; NOZZLE_WB/4=1' - 0 3/16"; NOZZLE_WB_OD=5' - 1"; NOZZLE_WB_RAD=2' - 6 1/2"; NOZZLE_WB_RAD-2"=2' - 4 1/2"; RO=3' - 8 3/4"; RO/2=1' - 10 3/8"; TRANSITION_TOP=6' - 5 1/4"; TYPE=0' - 0"; Type Comments=Vari-Plume Laboratory Exhaust Mixed-Flow Inline Belt Drive With Isolation Box; UNIT_HEIGHT=4' - 6"; UNIT_HEIGHT*.75=3' - 4 1/2"; UNIT_OD=3' - 6 1/2"; UNIT_RADIUS=1' - 9 1/4"; UNIT_RADIUS*.6=1' - 7 1/8"; UNIT_RADIUS+4"=2' - 1 1/4"
- 300_QMXVP-24H-Isolation_Box: (A/2)+.25"=2' - 2 1/4"; (NOZZLE_HEIGHT-(NOZZLE_HEIGHT/8*2))/2=1' - 11 1/4"; (NOZZLE_WB_OD-NOZZLE_TOP_OD)/2=0' - 6 1/8"; A=4' - 4"; A/2=2' - 2"; B=12' - 4"; B/2=6' - 2"; C=5' - 7"; C/2=2' - 9 1/2"; E=4' - 2 15/16"; GA=0' - 0 3/32"; Model=QMXVP-Isolation Box; NOZZLE_BOTTOM_ID=2' - 10 3/4"; NOZZLE_BOTTOM_RAD=1' - 5 3/8"; NOZZLE_HEIGHT=5' - 2"; NOZZLE_HEIGHT/7*2=1' - 3 1/2"; NOZZLE_SIZE=24' - 0"; NOZZLE_TOP_OD=3' - 0 1/2"; NOZZLE_TOP_RAD=1' - 6 1/4"; NOZZLE_WB/4=1' - 0 3/16"; NOZZLE_WB_OD=5' - 1"; NOZZLE_WB_RAD=2' - 6 1/2"; NOZZLE_WB_RAD-2"=2' - 4 1/2"; RO=3' - 8 3/4"; RO/2=1' - 10 3/8"; TRANSITION_TOP=6' - 5 1/4"; TYPE=0' - 0"; Type Comments=Vari-Plume Laboratory Exhaust Mixed-Flow Inline Belt Drive With Isolation Box; UNIT_HEIGHT=4' - 6"; UNIT_HEIGHT*.75=3' - 4 1/2"; UNIT_OD=3' - 6 1/2"; UNIT_RADIUS=1' - 9 1/4"; UNIT_RADIUS*.6=1' - 7 1/8"; UNIT_RADIUS+4"=2' - 1 1/4"
- 300_QMXVP-30L-Isolation_Box: (A/2)+.25"=2' - 2 1/4"; (NOZZLE_HEIGHT-(NOZZLE_HEIGHT/8*2))/2=2' - 5 1/4"; (NOZZLE_WB_OD-NOZZLE_TOP_OD)/2=0' - 7 1/8"; A=4' - 4"; A/2=2' - 2"; B=12' - 4"; B/2=6' - 2"; C=5' - 7"; C/2=2' - 9 1/2"; E=4' - 2 15/16"; GA=0' - 0 3/32"; Model=QMXVP-Isolation Box; NOZZLE_BOTTOM_ID=3' - 6 1/2"; NOZZLE_BOTTOM_RAD=1' - 9 1/4"; NOZZLE_HEIGHT=6' - 6"; NOZZLE_HEIGHT/7*2=1' - 7 1/2"; NOZZLE_SIZE=30' - 0"; NOZZLE_TOP_OD=3' - 9 1/2"; NOZZLE_TOP_RAD=1' - 10 3/4"; NOZZLE_WB/4=1' - 2 13/16"; NOZZLE_WB_OD=6' - 2"; NOZZLE_WB_RAD=3' - 1"; NOZZLE_WB_RAD-2"=2' - 11"; RO=3' - 8 3/4"; RO/2=1' - 10 3/8"; TRANSITION_TOP=5' - 8 1/4"; TYPE=0' - 0"; Type Comments=Vari-Plume Laboratory Exhaust Mixed-Flow Inline Belt Drive With Isolation Box; UNIT_HEIGHT=4' - 6"; UNIT_HEIGHT*.75=3' - 4 1/2"; UNIT_OD=3' - 6 1/2"; UNIT_RADIUS=1' - 9 1/4"; UNIT_RADIUS*.6=1' - 7 1/8"; UNIT_RADIUS+4"=2' - 1 1/4"
- 300_QMXVP-30H-Isolation_Box: (A/2)+.25"=2' - 2 1/4"; (NOZZLE_HEIGHT-(NOZZLE_HEIGHT/8*2))/2=2' - 5 1/4"; (NOZZLE_WB_OD-NOZZLE_TOP_OD)/2=0' - 7 1/8"; A=4' - 4"; A/2=2' - 2"; B=12' - 4"; B/2=6' - 2"; C=5' - 7"; C/2=2' - 9 1/2"; E=4' - 2 15/16"; GA=0' - 0 3/32"; Model=QMXVP-Isolation Box; NOZZLE_BOTTOM_ID=3' - 6 1/2"; NOZZLE_BOTTOM_RAD=1' - 9 1/4"; NOZZLE_HEIGHT=6' - 6"; NOZZLE_HEIGHT/7*2=1' - 7 1/2"; NOZZLE_SIZE=30' - 0"; NOZZLE_TOP_OD=3' - 9 1/2"; NOZZLE_TOP_RAD=1' - 10 3/4"; NOZZLE_WB/4=1' - 2 13/16"; NOZZLE_WB_OD=6' - 2"; NOZZLE_WB_RAD=3' - 1"; NOZZLE_WB_RAD-2"=2' - 11"; RO=3' - 8 3/4"; RO/2=1' - 10 3/8"; TRANSITION_TOP=5' - 8 1/4"; TYPE=0' - 0"; Type Comments=Vari-Plume Laboratory Exhaust Mixed-Flow Inline Belt Drive With Isolation Box; UNIT_HEIGHT=4' - 6"; UNIT_HEIGHT*.75=3' - 4 1/2"; UNIT_OD=3' - 6 1/2"; UNIT_RADIUS=1' - 9 1/4"; UNIT_RADIUS*.6=1' - 7 1/8"; UNIT_RADIUS+4"=2' - 1 1/4"
- 330_QMXVP-24L-Isolation_Box: (A/2)+.25"=2' - 4 1/4"; (NOZZLE_HEIGHT-(NOZZLE_HEIGHT/8*2))/2=1' - 11 1/4"; (NOZZLE_WB_OD-NOZZLE_TOP_OD)/2=0' - 6 1/8"; A=4' - 8"; A/2=2' - 4"; B=12' - 10"; B/2=6' - 5"; C=6' - 1"; C/2=3' - 0 1/2"; E=4' - 6 13/16"; GA=0' - 0 3/32"; Model=QMXVP-Isolation Box; NOZZLE_BOTTOM_ID=2' - 10 3/4"; NOZZLE_BOTTOM_RAD=1' - 5 3/8"; NOZZLE_HEIGHT=5' - 2"; NOZZLE_HEIGHT/7*2=1' - 3 1/2"; NOZZLE_SIZE=24' - 0"; NOZZLE_TOP_OD=3' - 0 1/2"; NOZZLE_TOP_RAD=1' - 6 1/4"; NOZZLE_WB/4=1' - 0 3/16"; NOZZLE_WB_OD=5' - 1"; NOZZLE_WB_RAD=2' - 6 1/2"; NOZZLE_WB_RAD-2"=2' - 4 1/2"; RO=4' - 0 5/8"; RO/2=2' - 0 5/16"; TRANSITION_TOP=7' - 5 3/4"; TYPE=0' - 0"; Type Comments=Vari-Plume Laboratory Exhaust Mixed-Flow Inline Belt Drive With Isolation Box; UNIT_HEIGHT=4' - 10 1/2"; UNIT_HEIGHT*.75=3' - 7 7/8"; UNIT_OD=3' - 10 3/4"; UNIT_RADIUS=1' - 11 3/8"; UNIT_RADIUS*.6=1' - 9 1/32"; UNIT_RADIUS+4"=2' - 3 3/8"
- 330_QMXVP-24H-Isolation_Box: (A/2)+.25"=2' - 4 1/4"; (NOZZLE_HEIGHT-(NOZZLE_HEIGHT/8*2))/2=1' - 11 1/4"; (NOZZLE_WB_OD-NOZZLE_TOP_OD)/2=0' - 6 1/8"; A=4' - 8"; A/2=2' - 4"; B=12' - 10"; B/2=6' - 5"; C=6' - 1"; C/2=3' - 0 1/2"; E=4' - 6 13/16"; GA=0' - 0 3/32"; Model=QMXVP-Isolation Box; NOZZLE_BOTTOM_ID=2' - 10 3/4"; NOZZLE_BOTTOM_RAD=1' - 5 3/8"; NOZZLE_HEIGHT=5' - 2"; NOZZLE_HEIGHT/7*2=1' - 3 1/2"; NOZZLE_SIZE=24' - 0"; NOZZLE_TOP_OD=3' - 0 1/2"; NOZZLE_TOP_RAD=1' - 6 1/4"; NOZZLE_WB/4=1' - 0 3/16"; NOZZLE_WB_OD=5' - 1"; NOZZLE_WB_RAD=2' - 6 1/2"; NOZZLE_WB_RAD-2"=2' - 4 1/2"; RO=4' - 0 5/8"; RO/2=2' - 0 5/16"; TRANSITION_TOP=7' - 5 3/4"; TYPE=0' - 0"; Type Comments=Vari-Plume Laboratory Exhaust Mixed-Flow Inline Belt Drive With Isolation Box; UNIT_HEIGHT=4' - 10 1/2"; UNIT_HEIGHT*.75=3' - 7 7/8"; UNIT_OD=3' - 10 3/4"; UNIT_RADIUS=1' - 11 3/8"; UNIT_RADIUS*.6=1' - 9 1/32"; UNIT_RADIUS+4"=2' - 3 3/8"
- 330_QMXVP-30L-Isolation_Box: (A/2)+.25"=2' - 4 1/4"; (NOZZLE_HEIGHT-(NOZZLE_HEIGHT/8*2))/2=2' - 5 1/4"; (NOZZLE_WB_OD-NOZZLE_TOP_OD)/2=0' - 7 1/8"; A=4' - 8"; A/2=2' - 4"; B=12' - 10"; B/2=6' - 5"; C=6' - 1"; C/2=3' - 0 1/2"; E=4' - 6 13/16"; GA=0' - 0 3/32"; Model=QMXVP-Isolation Box; NOZZLE_BOTTOM_ID=3' - 6 1/2"; NOZZLE_BOTTOM_RAD=1' - 9 1/4"; NOZZLE_HEIGHT=6' - 6"; NOZZLE_HEIGHT/7*2=1' - 7 1/2"; NOZZLE_SIZE=30' - 0"; NOZZLE_TOP_OD=3' - 9 1/2"; NOZZLE_TOP_RAD=1' - 10 3/4"; NOZZLE_WB/4=1' - 2 13/16"; NOZZLE_WB_OD=6' - 2"; NOZZLE_WB_RAD=3' - 1"; NOZZLE_WB_RAD-2"=2' - 11"; RO=4' - 0 5/8"; RO/2=2' - 0 5/16"; TRANSITION_TOP=6' - 2 3/4"; TYPE=0' - 0"; Type Comments=Vari-Plume Laboratory Exhaust Mixed-Flow Inline Belt Drive With Isolation Box; UNIT_HEIGHT=4' - 10 1/2"; UNIT_HEIGHT*.75=3' - 7 7/8"; UNIT_OD=3' - 10 3/4"; UNIT_RADIUS=1' - 11 3/8"; UNIT_RADIUS*.6=1' - 9 1/32"; UNIT_RADIUS+4"=2' - 3 3/8"
- 330_QMXVP-30H-Isolation_Box: (A/2)+.25"=2' - 4 1/4"; (NOZZLE_HEIGHT-(NOZZLE_HEIGHT/8*2))/2=2' - 5 1/4"; (NOZZLE_WB_OD-NOZZLE_TOP_OD)/2=0' - 7 1/8"; A=4' - 8"; A/2=2' - 4"; B=12' - 10"; B/2=6' - 5"; C=6' - 1"; C/2=3' - 0 1/2"; E=4' - 6 13/16"; GA=0' - 0 3/32"; Model=QMXVP-Isolation Box; NOZZLE_BOTTOM_ID=3' - 6 1/2"; NOZZLE_BOTTOM_RAD=1' - 9 1/4"; NOZZLE_HEIGHT=6' - 6"; NOZZLE_HEIGHT/7*2=1' - 7 1/2"; NOZZLE_SIZE=30' - 0"; NOZZLE_TOP_OD=3' - 9 1/2"; NOZZLE_TOP_RAD=1' - 10 3/4"; NOZZLE_WB/4=1' - 2 13/16"; NOZZLE_WB_OD=6' - 2"; NOZZLE_WB_RAD=3' - 1"; NOZZLE_WB_RAD-2"=2' - 11"; RO=4' - 0 5/8"; RO/2=2' - 0 5/16"; TRANSITION_TOP=6' - 2 3/4"; TYPE=0' - 0"; Type Comments=Vari-Plume Laboratory Exhaust Mixed-Flow Inline Belt Drive With Isolation Box; UNIT_HEIGHT=4' - 10 1/2"; UNIT_HEIGHT*.75=3' - 7 7/8"; UNIT_OD=3' - 10 3/4"; UNIT_RADIUS=1' - 11 3/8"; UNIT_RADIUS*.6=1' - 9 1/32"; UNIT_RADIUS+4"=2' - 3 3/8"
- 365_QMXVP-24L-Isolation_Box: (A/2)+.25"=2' - 7 1/4"; (NOZZLE_HEIGHT-(NOZZLE_HEIGHT/8*2))/2=1' - 11 1/4"; (NOZZLE_WB_OD-NOZZLE_TOP_OD)/2=0' - 6 1/8"; A=5' - 2"; A/2=2' - 7"; B=14' - 7"; B/2=7' - 3 1/2"; C=6' - 7"; C/2=3' - 3 1/2"; E=5' - 0 3/4"; GA=0' - 0 3/32"; Model=QMXVP-Isolation Box; NOZZLE_BOTTOM_ID=2' - 10 3/4"; NOZZLE_BOTTOM_RAD=1' - 5 3/8"; NOZZLE_HEIGHT=5' - 2"; NOZZLE_HEIGHT/7*2=1' - 3 1/2"; NOZZLE_SIZE=24' - 0"; NOZZLE_TOP_OD=3' - 0 1/2"; NOZZLE_TOP_RAD=1' - 6 1/4"; NOZZLE_WB/4=1' - 0 3/16"; NOZZLE_WB_OD=5' - 1"; NOZZLE_WB_RAD=2' - 6 1/2"; NOZZLE_WB_RAD-2"=2' - 4 1/2"; RO=4' - 6 1/2"; RO/2=2' - 3 1/4"; TRANSITION_TOP=8' - 8 1/4"; TYPE=0' - 0"; Type Comments=Vari-Plume Laboratory Exhaust Mixed-Flow Inline Belt Drive With Isolation Box; UNIT_HEIGHT=5' - 4"; UNIT_HEIGHT*.75=4' - 0"; UNIT_OD=4' - 3 3/4"; UNIT_RADIUS=2' - 1 7/8"; UNIT_RADIUS*.6=1' - 11 9/32"; UNIT_RADIUS+4"=2' - 5 7/8"
- 365_QMXVP-24H-Isolation_Box: (A/2)+.25"=2' - 7 1/4"; (NOZZLE_HEIGHT-(NOZZLE_HEIGHT/8*2))/2=1' - 11 1/4"; (NOZZLE_WB_OD-NOZZLE_TOP_OD)/2=0' - 6 1/8"; A=5' - 2"; A/2=2' - 7"; B=14' - 7"; B/2=7' - 3 1/2"; C=6' - 7"; C/2=3' - 3 1/2"; E=5' - 0 3/4"; GA=0' - 0 3/32"; Model=QMXVP-Isolation Box; NOZZLE_BOTTOM_ID=2' - 10 3/4"; NOZZLE_BOTTOM_RAD=1' - 5 3/8"; NOZZLE_HEIGHT=5' - 2"; NOZZLE_HEIGHT/7*2=1' - 3 1/2"; NOZZLE_SIZE=24' - 0"; NOZZLE_TOP_OD=3' - 0 1/2"; NOZZLE_TOP_RAD=1' - 6 1/4"; NOZZLE_WB/4=1' - 0 3/16"; NOZZLE_WB_OD=5' - 1"; NOZZLE_WB_RAD=2' - 6 1/2"; NOZZLE_WB_RAD-2"=2' - 4 1/2"; RO=4' - 6 1/2"; RO/2=2' - 3 1/4"; TRANSITION_TOP=8' - 8 1/4"; TYPE=0' - 0"; Type Comments=Vari-Plume Laboratory Exhaust Mixed-Flow Inline Belt Drive With Isolation Box; UNIT_HEIGHT=5' - 4"; UNIT_HEIGHT*.75=4' - 0"; UNIT_OD=4' - 3 3/4"; UNIT_RADIUS=2' - 1 7/8"; UNIT_RADIUS*.6=1' - 11 9/32"; UNIT_RADIUS+4"=2' - 5 7/8"
- 365_QMXVP-30L-Isolation_Box: (A/2)+.25"=2' - 7 1/4"; (NOZZLE_HEIGHT-(NOZZLE_HEIGHT/8*2))/2=2' - 5 1/4"; (NOZZLE_WB_OD-NOZZLE_TOP_OD)/2=0' - 7 1/8"; A=5' - 2"; A/2=2' - 7"; B=14' - 7"; B/2=7' - 3 1/2"; C=6' - 7"; C/2=3' - 3 1/2"; E=5' - 0 3/4"; GA=0' - 0 3/32"; Model=QMXVP-Isolation Box; NOZZLE_BOTTOM_ID=3' - 6 1/2"; NOZZLE_BOTTOM_RAD=1' - 9 1/4"; NOZZLE_HEIGHT=6' - 6"; NOZZLE_HEIGHT/7*2=1' - 7 1/2"; NOZZLE_SIZE=30' - 0"; NOZZLE_TOP_OD=3' - 9 1/2"; NOZZLE_TOP_RAD=1' - 10 3/4"; NOZZLE_WB/4=1' - 2 13/16"; NOZZLE_WB_OD=6' - 2"; NOZZLE_WB_RAD=3' - 1"; NOZZLE_WB_RAD-2"=2' - 11"; RO=4' - 6 1/2"; RO/2=2' - 3 1/4"; TRANSITION_TOP=7' - 5 1/2"; TYPE=0' - 0"; Type Comments=Vari-Plume Laboratory Exhaust Mixed-Flow Inline Belt Drive With Isolation Box; UNIT_HEIGHT=5' - 4"; UNIT_HEIGHT*.75=4' - 0"; UNIT_OD=4' - 3 3/4"; UNIT_RADIUS=2' - 1 7/8"; UNIT_RADIUS*.6=1' - 11 9/32"; UNIT_RADIUS+4"=2' - 5 7/8"
- 365_QMXVP-30H-Isolation_Box: (A/2)+.25"=2' - 7 1/4"; (NOZZLE_HEIGHT-(NOZZLE_HEIGHT/8*2))/2=2' - 5 1/4"; (NOZZLE_WB_OD-NOZZLE_TOP_OD)/2=0' - 7 1/8"; A=5' - 2"; A/2=2' - 7"; B=14' - 7"; B/2=7' - 3 1/2"; C=6' - 7"; C/2=3' - 3 1/2"; E=5' - 0 3/4"; GA=0' - 0 3/32"; Model=QMXVP-Isolation Box; NOZZLE_BOTTOM_ID=3' - 6 1/2"; NOZZLE_BOTTOM_RAD=1' - 9 1/4"; NOZZLE_HEIGHT=6' - 6"; NOZZLE_HEIGHT/7*2=1' - 7 1/2"; NOZZLE_SIZE=30' - 0"; NOZZLE_TOP_OD=3' - 9 1/2"; NOZZLE_TOP_RAD=1' - 10 3/4"; NOZZLE_WB/4=1' - 2 13/16"; NOZZLE_WB_OD=6' - 2"; NOZZLE_WB_RAD=3' - 1"; NOZZLE_WB_RAD-2"=2' - 11"; RO=4' - 6 1/2"; RO/2=2' - 3 1/4"; TRANSITION_TOP=7' - 5 1/2"; TYPE=0' - 0"; Type Comments=Vari-Plume Laboratory Exhaust Mixed-Flow Inline Belt Drive With Isolation Box; UNIT_HEIGHT=5' - 4"; UNIT_HEIGHT*.75=4' - 0"; UNIT_OD=4' - 3 3/4"; UNIT_RADIUS=2' - 1 7/8"; UNIT_RADIUS*.6=1' - 11 9/32"; UNIT_RADIUS+4"=2' - 5 7/8"
- 365_QMXVP-36L-Isolation_Box: (A/2)+.25"=2' - 7 1/4"; (NOZZLE_HEIGHT-(NOZZLE_HEIGHT/8*2))/2=2' - 11 5/8"; (NOZZLE_WB_OD-NOZZLE_TOP_OD)/2=0' - 8"; A=5' - 2"; A/2=2' - 7"; B=14' - 7"; B/2=7' - 3 1/2"; C=6' - 7"; C/2=3' - 3 1/2"; E=5' - 0 3/4"; GA=0' - 0 3/32"; Model=QMXVP-Isolation Box; NOZZLE_BOTTOM_ID=4' - 3 3/4"; NOZZLE_BOTTOM_RAD=2' - 1 7/8"; NOZZLE_HEIGHT=7' - 11"; NOZZLE_HEIGHT/7*2=1' - 11 3/4"; NOZZLE_SIZE=36' - 0"; NOZZLE_TOP_OD=4' - 10"; NOZZLE_TOP_RAD=2' - 5"; NOZZLE_WB/4=1' - 6"; NOZZLE_WB_OD=7' - 6"; NOZZLE_WB_RAD=3' - 9"; NOZZLE_WB_RAD-2"=3' - 7"; RO=4' - 6 1/2"; RO/2=2' - 3 1/4"; TRANSITION_TOP=6' - 6 1/4"; TYPE=0' - 0"; Type Comments=Vari-Plume Laboratory Exhaust Mixed-Flow Inline Belt Drive With Isolation Box; UNIT_HEIGHT=5' - 4"; UNIT_HEIGHT*.75=4' - 0"; UNIT_OD=4' - 3 3/4"; UNIT_RADIUS=2' - 1 7/8"; UNIT_RADIUS*.6=1' - 11 9/32"; UNIT_RADIUS+4"=2' - 5 7/8"
- 402_QMXVP-24L-Isolation_Box: (A/2)+.25"=2' - 9 3/4"; (NOZZLE_HEIGHT-(NOZZLE_HEIGHT/8*2))/2=1' - 11 1/4"; (NOZZLE_WB_OD-NOZZLE_TOP_OD)/2=0' - 6 1/8"; A=5' - 7"; A/2=2' - 9 1/2"; B=15' - 3"; B/2=7' - 7 1/2"; C=7' - 4"; C/2=3' - 8"; E=5' - 5 3/4"; GA=0' - 0 3/32"; Model=QMXVP-Isolation Box; NOZZLE_BOTTOM_ID=2' - 10 3/4"; NOZZLE_BOTTOM_RAD=1' - 5 3/8"; NOZZLE_HEIGHT=5' - 2"; NOZZLE_HEIGHT/7*2=1' - 3 1/2"; NOZZLE_SIZE=24' - 0"; NOZZLE_TOP_OD=3' - 0 1/2"; NOZZLE_TOP_RAD=1' - 6 1/4"; NOZZLE_WB/4=1' - 0 3/16"; NOZZLE_WB_OD=5' - 1"; NOZZLE_WB_RAD=2' - 6 1/2"; NOZZLE_WB_RAD-2"=2' - 4 1/2"; RO=4' - 11 7/16"; RO/2=2' - 5 23/32"; TRANSITION_TOP=9' - 10 3/4"; TYPE=0' - 0"; Type Comments=Vari-Plume Laboratory Exhaust Mixed-Flow Inline Belt Drive With Isolation Box; UNIT_HEIGHT=5' - 8 1/2"; UNIT_HEIGHT*.75=4' - 3 3/8"; UNIT_OD=4' - 8 15/16"; UNIT_RADIUS=2' - 4 15/32"; UNIT_RADIUS*.6=2' - 1 5/8"; UNIT_RADIUS+4"=2' - 8 15/32"
- 402_QMXVP-24H-Isolation_Box: (A/2)+.25"=2' - 9 3/4"; (NOZZLE_HEIGHT-(NOZZLE_HEIGHT/8*2))/2=1' - 11 1/4"; (NOZZLE_WB_OD-NOZZLE_TOP_OD)/2=0' - 6 1/8"; A=5' - 7"; A/2=2' - 9 1/2"; B=15' - 3"; B/2=7' - 7 1/2"; C=7' - 4"; C/2=3' - 8"; E=5' - 5 3/4"; GA=0' - 0 3/32"; Model=QMXVP-Isolation Box; NOZZLE_BOTTOM_ID=2' - 10 3/4"; NOZZLE_BOTTOM_RAD=1' - 5 3/8"; NOZZLE_HEIGHT=5' - 2"; NOZZLE_HEIGHT/7*2=1' - 3 1/2"; NOZZLE_SIZE=24' - 0"; NOZZLE_TOP_OD=3' - 0 1/2"; NOZZLE_TOP_RAD=1' - 6 1/4"; NOZZLE_WB/4=1' - 0 3/16"; NOZZLE_WB_OD=5' - 1"; NOZZLE_WB_RAD=2' - 6 1/2"; NOZZLE_WB_RAD-2"=2' - 4 1/2"; RO=4' - 11 7/16"; RO/2=2' - 5 23/32"; TRANSITION_TOP=9' - 10 3/4"; TYPE=0' - 0"; Type Comments=Vari-Plume Laboratory Exhaust Mixed-Flow Inline Belt Drive With Isolation Box; UNIT_HEIGHT=5' - 8 1/2"; UNIT_HEIGHT*.75=4' - 3 3/8"; UNIT_OD=4' - 8 15/16"; UNIT_RADIUS=2' - 4 15/32"; UNIT_RADIUS*.6=2' - 1 5/8"; UNIT_RADIUS+4"=2' - 8 15/32"
- 402_QMXVP-30L-Isolation_Box: (A/2)+.25"=2' - 9 3/4"; (NOZZLE_HEIGHT-(NOZZLE_HEIGHT/8*2))/2=2' - 5 1/4"; (NOZZLE_WB_OD-NOZZLE_TOP_OD)/2=0' - 7 1/8"; A=5' - 7"; A/2=2' - 9 1/2"; B=15' - 3"; B/2=7' - 7 1/2"; C=7' - 4"; C/2=3' - 8"; E=5' - 5 3/4"; GA=0' - 0 3/32"; Model=QMXVP-Isolation Box; NOZZLE_BOTTOM_ID=3' - 6 1/2"; NOZZLE_BOTTOM_RAD=1' - 9 1/4"; NOZZLE_HEIGHT=6' - 6"; NOZZLE_HEIGHT/7*2=1' - 7 1/2"; NOZZLE_SIZE=30' - 0"; NOZZLE_TOP_OD=3' - 9 1/2"; NOZZLE_TOP_RAD=1' - 10 3/4"; NOZZLE_WB/4=1' - 2 13/16"; NOZZLE_WB_OD=6' - 2"; NOZZLE_WB_RAD=3' - 1"; NOZZLE_WB_RAD-2"=2' - 11"; RO=4' - 11 7/16"; RO/2=2' - 5 23/32"; TRANSITION_TOP=8' - 7 3/4"; TYPE=0' - 0"; Type Comments=Vari-Plume Laboratory Exhaust Mixed-Flow Inline Belt Drive With Isolation Box; UNIT_HEIGHT=5' - 8 1/2"; UNIT_HEIGHT*.75=4' - 3 3/8"; UNIT_OD=4' - 8 15/16"; UNIT_RADIUS=2' - 4 15/32"; UNIT_RADIUS*.6=2' - 1 5/8"; UNIT_RADIUS+4"=2' - 8 15/32"
- 402_QMXVP-30H-Isolation_Box: (A/2)+.25"=2' - 9 3/4"; (NOZZLE_HEIGHT-(NOZZLE_HEIGHT/8*2))/2=2' - 5 1/4"; (NOZZLE_WB_OD-NOZZLE_TOP_OD)/2=0' - 7 1/8"; A=5' - 7"; A/2=2' - 9 1/2"; B=15' - 3"; B/2=7' - 7 1/2"; C=7' - 4"; C/2=3' - 8"; E=5' - 5 3/4"; GA=0' - 0 3/32"; Model=QMXVP-Isolation Box; NOZZLE_BOTTOM_ID=3' - 6 1/2"; NOZZLE_BOTTOM_RAD=1' - 9 1/4"; NOZZLE_HEIGHT=6' - 6"; NOZZLE_HEIGHT/7*2=1' - 7 1/2"; NOZZLE_SIZE=30' - 0"; NOZZLE_TOP_OD=3' - 9 1/2"; NOZZLE_TOP_RAD=1' - 10 3/4"; NOZZLE_WB/4=1' - 2 13/16"; NOZZLE_WB_OD=6' - 2"; NOZZLE_WB_RAD=3' - 1"; NOZZLE_WB_RAD-2"=2' - 11"; RO=4' - 11 7/16"; RO/2=2' - 5 23/32"; TRANSITION_TOP=8' - 7 3/4"; TYPE=0' - 0"; Type Comments=Vari-Plume Laboratory Exhaust Mixed-Flow Inline Belt Drive With Isolation Box; UNIT_HEIGHT=5' - 8 1/2"; UNIT_HEIGHT*.75=4' - 3 3/8"; UNIT_OD=4' - 8 15/16"; UNIT_RADIUS=2' - 4 15/32"; UNIT_RADIUS*.6=2' - 1 5/8"; UNIT_RADIUS+4"=2' - 8 15/32"
- 402_QMXVP-36L-Isolation_Box: (A/2)+.25"=2' - 9 3/4"; (NOZZLE_HEIGHT-(NOZZLE_HEIGHT/8*2))/2=2' - 11 5/8"; (NOZZLE_WB_OD-NOZZLE_TOP_OD)/2=0' - 8"; A=5' - 7"; A/2=2' - 9 1/2"; B=15' - 3"; B/2=7' - 7 1/2"; C=7' - 4"; C/2=3' - 8"; E=5' - 5 3/4"; GA=0' - 0 3/32"; Model=QMXVP-Isolation Box; NOZZLE_BOTTOM_ID=4' - 3 3/4"; NOZZLE_BOTTOM_RAD=2' - 1 7/8"; NOZZLE_HEIGHT=7' - 11"; NOZZLE_HEIGHT/7*2=1' - 11 3/4"; NOZZLE_SIZE=36' - 0"; NOZZLE_TOP_OD=4' - 10"; NOZZLE_TOP_RAD=2' - 5"; NOZZLE_WB/4=1' - 6"; NOZZLE_WB_OD=7' - 6"; NOZZLE_WB_RAD=3' - 9"; NOZZLE_WB_RAD-2"=3' - 7"; RO=4' - 11 7/16"; RO/2=2' - 5 23/32"; TRANSITION_TOP=7' - 2 3/4"; TYPE=0' - 0"; Type Comments=Vari-Plume Laboratory Exhaust Mixed-Flow Inline Belt Drive With Isolation Box; UNIT_HEIGHT=5' - 8 1/2"; UNIT_HEIGHT*.75=4' - 3 3/8"; UNIT_OD=4' - 8 15/16"; UNIT_RADIUS=2' - 4 15/32"; UNIT_RADIUS*.6=2' - 1 5/8"; UNIT_RADIUS+4"=2' - 8 15/32"
- 402_QMXVP-36H-Isolation_Box: (A/2)+.25"=2' - 9 3/4"; (NOZZLE_HEIGHT-(NOZZLE_HEIGHT/8*2))/2=2' - 11 5/8"; (NOZZLE_WB_OD-NOZZLE_TOP_OD)/2=0' - 8"; A=5' - 7"; A/2=2' - 9 1/2"; B=15' - 3"; B/2=7' - 7 1/2"; C=7' - 4"; C/2=3' - 8"; E=5' - 5 3/4"; GA=0' - 0 3/32"; Model=QMXVP-Isolation Box; NOZZLE_BOTTOM_ID=4' - 3 3/4"; NOZZLE_BOTTOM_RAD=2' - 1 7/8"; NOZZLE_HEIGHT=7' - 11"; NOZZLE_HEIGHT/7*2=1' - 11 3/4"; NOZZLE_SIZE=36' - 0"; NOZZLE_TOP_OD=4' - 10"; NOZZLE_TOP_RAD=2' - 5"; NOZZLE_WB/4=1' - 6"; NOZZLE_WB_OD=7' - 6"; NOZZLE_WB_RAD=3' - 9"; NOZZLE_WB_RAD-2"=3' - 7"; RO=4' - 11 7/16"; RO/2=2' - 5 23/32"; TRANSITION_TOP=7' - 2 3/4"; TYPE=0' - 0"; Type Comments=Vari-Plume Laboratory Exhaust Mixed-Flow Inline Belt Drive With Isolation Box; UNIT_HEIGHT=5' - 8 1/2"; UNIT_HEIGHT*.75=4' - 3 3/8"; UNIT_OD=4' - 8 15/16"; UNIT_RADIUS=2' - 4 15/32"; UNIT_RADIUS*.6=2' - 1 5/8"; UNIT_RADIUS+4"=2' - 8 15/32"
- 445_QMXVP-30L-Isolation_Box: (A/2)+.25"=3' - 1 1/4"; (NOZZLE_HEIGHT-(NOZZLE_HEIGHT/8*2))/2=2' - 5 1/4"; (NOZZLE_WB_OD-NOZZLE_TOP_OD)/2=0' - 7 1/8"; A=6' - 2"; A/2=3' - 1"; B=16' - 9"; B/2=8' - 4 1/2"; C=7' - 11"; C/2=3' - 11 1/2"; E=6' - 0 5/8"; GA=0' - 0 3/32"; Model=QMXVP-Isolation Box; NOZZLE_BOTTOM_ID=3' - 6 1/2"; NOZZLE_BOTTOM_RAD=1' - 9 1/4"; NOZZLE_HEIGHT=6' - 6"; NOZZLE_HEIGHT/7*2=1' - 7 1/2"; NOZZLE_SIZE=30' - 0"; NOZZLE_TOP_OD=3' - 9 1/2"; NOZZLE_TOP_RAD=1' - 10 3/4"; NOZZLE_WB/4=1' - 2 13/16"; NOZZLE_WB_OD=6' - 2"; NOZZLE_WB_RAD=3' - 1"; NOZZLE_WB_RAD-2"=2' - 11"; RO=5' - 6 7/16"; RO/2=2' - 9 7/32"; TRANSITION_TOP=10' - 1 1/4"; TYPE=0' - 0"; Type Comments=Vari-Plume Laboratory Exhaust Mixed-Flow Inline Belt Drive With Isolation Box; UNIT_HEIGHT=6' - 2"; UNIT_HEIGHT*.75=4' - 7 1/2"; UNIT_OD=5' - 3 1/16"; UNIT_RADIUS=2' - 7 17/32"; UNIT_RADIUS*.6=2' - 4 3/8"; UNIT_RADIUS+4"=2' - 11 17/32"
- 445_QMXVP-30H-Isolation_Box: (A/2)+.25"=3' - 1 1/4"; (NOZZLE_HEIGHT-(NOZZLE_HEIGHT/8*2))/2=2' - 5 1/4"; (NOZZLE_WB_OD-NOZZLE_TOP_OD)/2=0' - 7 1/8"; A=6' - 2"; A/2=3' - 1"; B=16' - 9"; B/2=8' - 4 1/2"; C=7' - 11"; C/2=3' - 11 1/2"; E=6' - 0 5/8"; GA=0' - 0 3/32"; Model=QMXVP-Isolation Box; NOZZLE_BOTTOM_ID=3' - 6 1/2"; NOZZLE_BOTTOM_RAD=1' - 9 1/4"; NOZZLE_HEIGHT=6' - 6"; NOZZLE_HEIGHT/7*2=1' - 7 1/2"; NOZZLE_SIZE=30' - 0"; NOZZLE_TOP_OD=3' - 9 1/2"; NOZZLE_TOP_RAD=1' - 10 3/4"; NOZZLE_WB/4=1' - 2 13/16"; NOZZLE_WB_OD=6' - 2"; NOZZLE_WB_RAD=3' - 1"; NOZZLE_WB_RAD-2"=2' - 11"; RO=5' - 6 7/16"; RO/2=2' - 9 7/32"; TRANSITION_TOP=10' - 1 1/4"; TYPE=0' - 0"; Type Comments=Vari-Plume Laboratory Exhaust Mixed-Flow Inline Belt Drive With Isolation Box; UNIT_HEIGHT=6' - 2"; UNIT_HEIGHT*.75=4' - 7 1/2"; UNIT_OD=5' - 3 1/16"; UNIT_RADIUS=2' - 7 17/32"; UNIT_RADIUS*.6=2' - 4 3/8"; UNIT_RADIUS+4"=2' - 11 17/32"
- 445_QMXVP-36L-Isolation_Box: (A/2)+.25"=3' - 1 1/4"; (NOZZLE_HEIGHT-(NOZZLE_HEIGHT/8*2))/2=2' - 11 5/8"; (NOZZLE_WB_OD-NOZZLE_TOP_OD)/2=0' - 8"; A=6' - 2"; A/2=3' - 1"; B=16' - 9"; B/2=8' - 4 1/2"; C=7' - 11"; C/2=3' - 11 1/2"; E=6' - 0 5/8"; GA=0' - 0 3/32"; Model=QMXVP-Isolation Box; NOZZLE_BOTTOM_ID=4' - 3 3/4"; NOZZLE_BOTTOM_RAD=2' - 1 7/8"; NOZZLE_HEIGHT=7' - 11"; NOZZLE_HEIGHT/7*2=1' - 11 3/4"; NOZZLE_SIZE=36' - 0"; NOZZLE_TOP_OD=4' - 10"; NOZZLE_TOP_RAD=2' - 5"; NOZZLE_WB/4=1' - 6"; NOZZLE_WB_OD=7' - 6"; NOZZLE_WB_RAD=3' - 9"; NOZZLE_WB_RAD-2"=3' - 7"; RO=5' - 6 7/16"; RO/2=2' - 9 7/32"; TRANSITION_TOP=8' - 7 1/4"; TYPE=0' - 0"; Type Comments=Vari-Plume Laboratory Exhaust Mixed-Flow Inline Belt Drive With Isolation Box; UNIT_HEIGHT=6' - 2"; UNIT_HEIGHT*.75=4' - 7 1/2"; UNIT_OD=5' - 3 1/16"; UNIT_RADIUS=2' - 7 17/32"; UNIT_RADIUS*.6=2' - 4 3/8"; UNIT_RADIUS+4"=2' - 11 17/32"
- 445_QMXVP-36H-Isolation_Box: (A/2)+.25"=3' - 1 1/4"; (NOZZLE_HEIGHT-(NOZZLE_HEIGHT/8*2))/2=2' - 11 5/8"; (NOZZLE_WB_OD-NOZZLE_TOP_OD)/2=0' - 8"; A=6' - 2"; A/2=3' - 1"; B=16' - 9"; B/2=8' - 4 1/2"; C=7' - 11"; C/2=3' - 11 1/2"; E=6' - 0 5/8"; GA=0' - 0 3/32"; Model=QMXVP-Isolation Box; NOZZLE_BOTTOM_ID=4' - 3 3/4"; NOZZLE_BOTTOM_RAD=2' - 1 7/8"; NOZZLE_HEIGHT=7' - 11"; NOZZLE_HEIGHT/7*2=1' - 11 3/4"; NOZZLE_SIZE=36' - 0"; NOZZLE_TOP_OD=4' - 10"; NOZZLE_TOP_RAD=2' - 5"; NOZZLE_WB/4=1' - 6"; NOZZLE_WB_OD=7' - 6"; NOZZLE_WB_RAD=3' - 9"; NOZZLE_WB_RAD-2"=3' - 7"; RO=5' - 6 7/16"; RO/2=2' - 9 7/32"; TRANSITION_TOP=8' - 7 1/4"; TYPE=0' - 0"; Type Comments=Vari-Plume Laboratory Exhaust Mixed-Flow Inline Belt Drive With Isolation Box; UNIT_HEIGHT=6' - 2"; UNIT_HEIGHT*.75=4' - 7 1/2"; UNIT_OD=5' - 3 1/16"; UNIT_RADIUS=2' - 7 17/32"; UNIT_RADIUS*.6=2' - 4 3/8"; UNIT_RADIUS+4"=2' - 11 17/32"
- 490_QMXVP-30L-Isolation_Box: (A/2)+.25"=3' - 4 1/4"; (NOZZLE_HEIGHT-(NOZZLE_HEIGHT/8*2))/2=2' - 5 1/4"; (NOZZLE_WB_OD-NOZZLE_TOP_OD)/2=0' - 7 1/8"; A=6' - 8"; A/2=3' - 4"; B=18' - 3"; B/2=9' - 1 1/2"; C=8' - 7"; C/2=4' - 3 1/2"; E=6' - 6 1/2"; GA=0' - 0 1/8"; Model=QMXVP-Isolation Box; NOZZLE_BOTTOM_ID=3' - 6 1/2"; NOZZLE_BOTTOM_RAD=1' - 9 1/4"; NOZZLE_HEIGHT=6' - 6"; NOZZLE_HEIGHT/7*2=1' - 7 1/2"; NOZZLE_SIZE=30' - 0"; NOZZLE_TOP_OD=3' - 9 1/2"; NOZZLE_TOP_RAD=1' - 10 3/4"; NOZZLE_WB/4=1' - 2 13/16"; NOZZLE_WB_OD=6' - 2"; NOZZLE_WB_RAD=3' - 1"; NOZZLE_WB_RAD-2"=2' - 11"; RO=6' - 0 1/4"; RO/2=3' - 0 1/8"; TRANSITION_TOP=11' - 7 3/4"; TYPE=0' - 0"; Type Comments=Vari-Plume Laboratory Exhaust Mixed-Flow Inline Belt Drive With Isolation Box; UNIT_HEIGHT=6' - 8 1/2"; UNIT_HEIGHT*.75=5' - 0 3/8"; UNIT_OD=5' - 9 3/8"; UNIT_RADIUS=2' - 10 11/16"; UNIT_RADIUS*.6=2' - 7 7/32"; UNIT_RADIUS+4"=3' - 2 11/16"
- 490_QMXVP-30H-Isolation_Box: (A/2)+.25"=3' - 4 1/4"; (NOZZLE_HEIGHT-(NOZZLE_HEIGHT/8*2))/2=2' - 5 1/4"; (NOZZLE_WB_OD-NOZZLE_TOP_OD)/2=0' - 7 1/8"; A=6' - 8"; A/2=3' - 4"; B=18' - 3"; B/2=9' - 1 1/2"; C=8' - 7"; C/2=4' - 3 1/2"; E=6' - 6 1/2"; GA=0' - 0 1/8"; Model=QMXVP-Isolation Box; NOZZLE_BOTTOM_ID=3' - 6 1/2"; NOZZLE_BOTTOM_RAD=1' - 9 1/4"; NOZZLE_HEIGHT=6' - 6"; NOZZLE_HEIGHT/7*2=1' - 7 1/2"; NOZZLE_SIZE=30' - 0"; NOZZLE_TOP_OD=3' - 9 1/2"; NOZZLE_TOP_RAD=1' - 10 3/4"; NOZZLE_WB/4=1' - 2 13/16"; NOZZLE_WB_OD=6' - 2"; NOZZLE_WB_RAD=3' - 1"; NOZZLE_WB_RAD-2"=2' - 11"; RO=6' - 0 1/4"; RO/2=3' - 0 1/8"; TRANSITION_TOP=11' - 7 3/4"; TYPE=0' - 0"; Type Comments=Vari-Plume Laboratory Exhaust Mixed-Flow Inline Belt Drive With Isolation Box; UNIT_HEIGHT=6' - 8 1/2"; UNIT_HEIGHT*.75=5' - 0 3/8"; UNIT_OD=5' - 9 3/8"; UNIT_RADIUS=2' - 10 11/16"; UNIT_RADIUS*.6=2' - 7 7/32"; UNIT_RADIUS+4"=3' - 2 11/16"
- 490_QMXVP-36L-Isolation_Box: (A/2)+.25"=3' - 4 1/4"; (NOZZLE_HEIGHT-(NOZZLE_HEIGHT/8*2))/2=2' - 11 5/8"; (NOZZLE_WB_OD-NOZZLE_TOP_OD)/2=0' - 8"; A=6' - 8"; A/2=3' - 4"; B=18' - 3"; B/2=9' - 1 1/2"; C=8' - 7"; C/2=4' - 3 1/2"; E=6' - 6 1/2"; GA=0' - 0 1/8"; Model=QMXVP-Isolation Box; NOZZLE_BOTTOM_ID=4' - 3 3/4"; NOZZLE_BOTTOM_RAD=2' - 1 7/8"; NOZZLE_HEIGHT=7' - 11"; NOZZLE_HEIGHT/7*2=1' - 11 3/4"; NOZZLE_SIZE=36' - 0"; NOZZLE_TOP_OD=4' - 10"; NOZZLE_TOP_RAD=2' - 5"; NOZZLE_WB/4=1' - 6"; NOZZLE_WB_OD=7' - 6"; NOZZLE_WB_RAD=3' - 9"; NOZZLE_WB_RAD-2"=3' - 7"; RO=6' - 0 1/4"; RO/2=3' - 0 1/8"; TRANSITION_TOP=10' - 2 3/4"; TYPE=0' - 0"; Type Comments=Vari-Plume Laboratory Exhaust Mixed-Flow Inline Belt Drive With Isolation Box; UNIT_HEIGHT=6' - 8 1/2"; UNIT_HEIGHT*.75=5' - 0 3/8"; UNIT_OD=5' - 9 3/8"; UNIT_RADIUS=2' - 10 11/16"; UNIT_RADIUS*.6=2' - 7 7/32"; UNIT_RADIUS+4"=3' - 2 11/16"
- 490_QMXVP-36H-Isolation_Box: (A/2)+.25"=3' - 4 1/4"; (NOZZLE_HEIGHT-(NOZZLE_HEIGHT/8*2))/2=2' - 11 5/8"; (NOZZLE_WB_OD-NOZZLE_TOP_OD)/2=0' - 8"; A=6' - 8"; A/2=3' - 4"; B=18' - 3"; B/2=9' - 1 1/2"; C=8' - 7"; C/2=4' - 3 1/2"; E=6' - 6 1/2"; GA=0' - 0 1/8"; Model=QMXVP-Isolation Box; NOZZLE_BOTTOM_ID=4' - 3 3/4"; NOZZLE_BOTTOM_RAD=2' - 1 7/8"; NOZZLE_HEIGHT=7' - 11"; NOZZLE_HEIGHT/7*2=1' - 11 3/4"; NOZZLE_SIZE=36' - 0"; NOZZLE_TOP_OD=4' - 10"; NOZZLE_TOP_RAD=2' - 5"; NOZZLE_WB/4=1' - 6"; NOZZLE_WB_OD=7' - 6"; NOZZLE_WB_RAD=3' - 9"; NOZZLE_WB_RAD-2"=3' - 7"; RO=6' - 0 1/4"; RO/2=3' - 0 1/8"; TRANSITION_TOP=10' - 2 3/4"; TYPE=0' - 0"; Type Comments=Vari-Plume Laboratory Exhaust Mixed-Flow Inline Belt Drive With Isolation Box; UNIT_HEIGHT=6' - 8 1/2"; UNIT_HEIGHT*.75=5' - 0 3/8"; UNIT_OD=5' - 9 3/8"; UNIT_RADIUS=2' - 10 11/16"; UNIT_RADIUS*.6=2' - 7 7/32"; UNIT_RADIUS+4"=3' - 2 11/16"
- 540_QMXVP-36L-Isolation_Box: (A/2)+.25"=3' - 9 1/4"; (NOZZLE_HEIGHT-(NOZZLE_HEIGHT/8*2))/2=2' - 11 5/8"; (NOZZLE_WB_OD-NOZZLE_TOP_OD)/2=0' - 8"; A=7' - 6"; A/2=3' - 9"; B=19' - 11"; B/2=9' - 11 1/2"; C=9' - 3"; C/2=4' - 7 1/2"; E=7' - 1 3/8"; GA=0' - 0 1/8"; Model=QMXVP-Isolation Box; NOZZLE_BOTTOM_ID=4' - 3 3/4"; NOZZLE_BOTTOM_RAD=2' - 1 7/8"; NOZZLE_HEIGHT=7' - 11"; NOZZLE_HEIGHT/7*2=1' - 11 3/4"; NOZZLE_SIZE=36' - 0"; NOZZLE_TOP_OD=4' - 10"; NOZZLE_TOP_RAD=2' - 5"; NOZZLE_WB/4=1' - 6"; NOZZLE_WB_OD=7' - 6"; NOZZLE_WB_RAD=3' - 9"; NOZZLE_WB_RAD-2"=3' - 7"; RO=6' - 7 1/8"; RO/2=3' - 3 9/16"; TRANSITION_TOP=11' - 10 1/4"; TYPE=0' - 0"; Type Comments=Vari-Plume Laboratory Exhaust Mixed-Flow Inline Belt Drive With Isolation Box; UNIT_HEIGHT=7' - 3"; UNIT_HEIGHT*.75=5' - 5 1/4"; UNIT_OD=6' - 4 7/16"; UNIT_RADIUS=3' - 2 7/32"; UNIT_RADIUS*.6=2' - 10 13/32"; UNIT_RADIUS+4"=3' - 6 7/32"
- 540_QMXVP-36H-Isolation_Box: (A/2)+.25"=3' - 9 1/4"; (NOZZLE_HEIGHT-(NOZZLE_HEIGHT/8*2))/2=2' - 11 5/8"; (NOZZLE_WB_OD-NOZZLE_TOP_OD)/2=0' - 8"; A=7' - 6"; A/2=3' - 9"; B=19' - 11"; B/2=9' - 11 1/2"; C=9' - 3"; C/2=4' - 7 1/2"; E=7' - 1 3/8"; GA=0' - 0 1/8"; Model=QMXVP-Isolation Box; NOZZLE_BOTTOM_ID=4' - 3 3/4"; NOZZLE_BOTTOM_RAD=2' - 1 7/8"; NOZZLE_HEIGHT=7' - 11"; NOZZLE_HEIGHT/7*2=1' - 11 3/4"; NOZZLE_SIZE=36' - 0"; NOZZLE_TOP_OD=4' - 10"; NOZZLE_TOP_RAD=2' - 5"; NOZZLE_WB/4=1' - 6"; NOZZLE_WB_OD=7' - 6"; NOZZLE_WB_RAD=3' - 9"; NOZZLE_WB_RAD-2"=3' - 7"; RO=6' - 7 1/8"; RO/2=3' - 3 9/16"; TRANSITION_TOP=11' - 10 1/4"; TYPE=0' - 0"; Type Comments=Vari-Plume Laboratory Exhaust Mixed-Flow Inline Belt Drive With Isolation Box; UNIT_HEIGHT=7' - 3"; UNIT_HEIGHT*.75=5' - 5 1/4"; UNIT_OD=6' - 4 7/16"; UNIT_RADIUS=3' - 2 7/32"; UNIT_RADIUS*.6=2' - 10 13/32"; UNIT_RADIUS+4"=3' - 6 7/32"
- 540_QMXVP-49L-Isolation_Box: (A/2)+.25"=3' - 9 1/4"; (NOZZLE_HEIGHT-(NOZZLE_HEIGHT/8*2))/2=3' - 5 1/4"; (NOZZLE_WB_OD-NOZZLE_TOP_OD)/2=0' - 6 1/4"; A=7' - 6"; A/2=3' - 9"; B=19' - 11"; B/2=9' - 11 1/2"; C=9' - 3"; C/2=4' - 7 1/2"; E=7' - 1 3/8"; GA=0' - 0 1/8"; Model=QMXVP-Isolation Box; NOZZLE_BOTTOM_ID=5' - 9 3/8"; NOZZLE_BOTTOM_RAD=2' - 10 11/16"; NOZZLE_HEIGHT=9' - 2"; NOZZLE_HEIGHT/7*2=2' - 3 1/2"; NOZZLE_SIZE=49' - 0"; NOZZLE_TOP_OD=6' - 4"; NOZZLE_TOP_RAD=3' - 2"; NOZZLE_WB/4=1' - 8 3/16"; NOZZLE_WB_OD=8' - 5"; NOZZLE_WB_RAD=4' - 2 1/2"; NOZZLE_WB_RAD-2"=4' - 0 1/2"; RO=6' - 7 1/8"; RO/2=3' - 3 9/16"; TRANSITION_TOP=10' - 1 1/4"; TYPE=0' - 0"; Type Comments=Vari-Plume Laboratory Exhaust Mixed-Flow Inline Belt Drive With Isolation Box; UNIT_HEIGHT=7' - 3"; UNIT_HEIGHT*.75=5' - 5 1/4"; UNIT_OD=6' - 4 7/16"; UNIT_RADIUS=3' - 2 7/32"; UNIT_RADIUS*.6=2' - 10 13/32"; UNIT_RADIUS+4"=3' - 6 7/32"
- 540_QMXVP-49H-Isolation_Box: (A/2)+.25"=3' - 9 1/4"; (NOZZLE_HEIGHT-(NOZZLE_HEIGHT/8*2))/2=3' - 5 1/4"; (NOZZLE_WB_OD-NOZZLE_TOP_OD)/2=0' - 6 1/4"; A=7' - 6"; A/2=3' - 9"; B=19' - 11"; B/2=9' - 11 1/2"; C=9' - 3"; C/2=4' - 7 1/2"; E=7' - 1 3/8"; GA=0' - 0 1/8"; Model=QMXVP-Isolation Box; NOZZLE_BOTTOM_ID=5' - 9 3/8"; NOZZLE_BOTTOM_RAD=2' - 10 11/16"; NOZZLE_HEIGHT=9' - 2"; NOZZLE_HEIGHT/7*2=2' - 3 1/2"; NOZZLE_SIZE=49' - 0"; NOZZLE_TOP_OD=6' - 4"; NOZZLE_TOP_RAD=3' - 2"; NOZZLE_WB/4=1' - 8 3/16"; NOZZLE_WB_OD=8' - 5"; NOZZLE_WB_RAD=4' - 2 1/2"; NOZZLE_WB_RAD-2"=4' - 0 1/2"; RO=6' - 7 1/8"; RO/2=3' - 3 9/16"; TRANSITION_TOP=10' - 1 1/4"; TYPE=0' - 0"; Type Comments=Vari-Plume Laboratory Exhaust Mixed-Flow Inline Belt Drive With Isolation Box; UNIT_HEIGHT=7' - 3"; UNIT_HEIGHT*.75=5' - 5 1/4"; UNIT_OD=6' - 4 7/16"; UNIT_RADIUS=3' - 2 7/32"; UNIT_RADIUS*.6=2' - 10 13/32"; UNIT_RADIUS+4"=3' - 6 7/32"
- 600_QMXVP-36L-Isolation_Box: (A/2)+.25"=4' - 2 3/4"; (NOZZLE_HEIGHT-(NOZZLE_HEIGHT/8*2))/2=2' - 11 5/8"; (NOZZLE_WB_OD-NOZZLE_TOP_OD)/2=0' - 8"; A=8' - 5"; A/2=4' - 2 1/2"; B=21' - 11"; B/2=10' - 11 1/2"; C=10' - 2"; C/2=5' - 1"; E=7' - 10 3/8"; GA=0' - 0 3/16"; Model=QMXVP-Isolation Box; NOZZLE_BOTTOM_ID=4' - 3 3/4"; NOZZLE_BOTTOM_RAD=2' - 1 7/8"; NOZZLE_HEIGHT=7' - 11"; NOZZLE_HEIGHT/7*2=1' - 11 3/4"; NOZZLE_SIZE=36' - 0"; NOZZLE_TOP_OD=4' - 10"; NOZZLE_TOP_RAD=2' - 5"; NOZZLE_WB/4=1' - 6"; NOZZLE_WB_OD=7' - 6"; NOZZLE_WB_RAD=3' - 9"; NOZZLE_WB_RAD-2"=3' - 7"; RO=7' - 4 1/16"; RO/2=3' - 8 1/32"; TRANSITION_TOP=14' - 2 3/4"; TYPE=0' - 0"; Type Comments=Vari-Plume Laboratory Exhaust Mixed-Flow Inline Belt Drive With Isolation Box; UNIT_HEIGHT=7' - 11 1/2"; UNIT_HEIGHT*.75=5' - 11 5/8"; UNIT_OD=7' - 0 7/8"; UNIT_RADIUS=3' - 6 7/16"; UNIT_RADIUS*.6=3' - 2 3/16"; UNIT_RADIUS+4"=3' - 10 7/16"
- 600_QMXVP-36H-Isolation_Box: (A/2)+.25"=4' - 2 3/4"; (NOZZLE_HEIGHT-(NOZZLE_HEIGHT/8*2))/2=2' - 11 5/8"; (NOZZLE_WB_OD-NOZZLE_TOP_OD)/2=0' - 8"; A=8' - 5"; A/2=4' - 2 1/2"; B=21' - 11"; B/2=10' - 11 1/2"; C=10' - 2"; C/2=5' - 1"; E=7' - 10 3/8"; GA=0' - 0 3/16"; Model=QMXVP-Isolation Box; NOZZLE_BOTTOM_ID=4' - 3 3/4"; NOZZLE_BOTTOM_RAD=2' - 1 7/8"; NOZZLE_HEIGHT=7' - 11"; NOZZLE_HEIGHT/7*2=1' - 11 3/4"; NOZZLE_SIZE=36' - 0"; NOZZLE_TOP_OD=4' - 10"; NOZZLE_TOP_RAD=2' - 5"; NOZZLE_WB/4=1' - 6"; NOZZLE_WB_OD=7' - 6"; NOZZLE_WB_RAD=3' - 9"; NOZZLE_WB_RAD-2"=3' - 7"; RO=7' - 4 1/16"; RO/2=3' - 8 1/32"; TRANSITION_TOP=14' - 2 3/4"; TYPE=0' - 0"; Type Comments=Vari-Plume Laboratory Exhaust Mixed-Flow Inline Belt Drive With Isolation Box; UNIT_HEIGHT=7' - 11 1/2"; UNIT_HEIGHT*.75=5' - 11 5/8"; UNIT_OD=7' - 0 7/8"; UNIT_RADIUS=3' - 6 7/16"; UNIT_RADIUS*.6=3' - 2 3/16"; UNIT_RADIUS+4"=3' - 10 7/16"
- 600_QMXVP-49L-Isolation_Box: (A/2)+.25"=4' - 2 3/4"; (NOZZLE_HEIGHT-(NOZZLE_HEIGHT/8*2))/2=3' - 5 1/4"; (NOZZLE_WB_OD-NOZZLE_TOP_OD)/2=0' - 6 1/4"; A=8' - 5"; A/2=4' - 2 1/2"; B=21' - 11"; B/2=10' - 11 1/2"; C=10' - 2"; C/2=5' - 1"; E=7' - 10 3/8"; GA=0' - 0 3/16"; Model=QMXVP-Isolation Box; NOZZLE_BOTTOM_ID=5' - 9 3/8"; NOZZLE_BOTTOM_RAD=2' - 10 11/16"; NOZZLE_HEIGHT=9' - 2"; NOZZLE_HEIGHT/7*2=2' - 3 1/2"; NOZZLE_SIZE=49' - 0"; NOZZLE_TOP_OD=6' - 4"; NOZZLE_TOP_RAD=3' - 2"; NOZZLE_WB/4=1' - 8 3/16"; NOZZLE_WB_OD=8' - 5"; NOZZLE_WB_RAD=4' - 2 1/2"; NOZZLE_WB_RAD-2"=4' - 0 1/2"; RO=7' - 4 1/16"; RO/2=3' - 8 1/32"; TRANSITION_TOP=12' - 4 3/4"; TYPE=0' - 0"; Type Comments=Vari-Plume Laboratory Exhaust Mixed-Flow Inline Belt Drive With Isolation Box; UNIT_HEIGHT=7' - 11 1/2"; UNIT_HEIGHT*.75=5' - 11 5/8"; UNIT_OD=7' - 0 7/8"; UNIT_RADIUS=3' - 6 7/16"; UNIT_RADIUS*.6=3' - 2 3/16"; UNIT_RADIUS+4"=3' - 10 7/16"
- 600_QMXVP-49H-Isolation_Box: (A/2)+.25"=4' - 2 3/4"; (NOZZLE_HEIGHT-(NOZZLE_HEIGHT/8*2))/2=3' - 5 1/4"; (NOZZLE_WB_OD-NOZZLE_TOP_OD)/2=0' - 6 1/4"; A=8' - 5"; A/2=4' - 2 1/2"; B=21' - 11"; B/2=10' - 11 1/2"; C=10' - 2"; C/2=5' - 1"; E=7' - 10 3/8"; GA=0' - 0 3/16"; Model=QMXVP-Isolation Box; NOZZLE_BOTTOM_ID=5' - 9 3/8"; NOZZLE_BOTTOM_RAD=2' - 10 11/16"; NOZZLE_HEIGHT=9' - 2"; NOZZLE_HEIGHT/7*2=2' - 3 1/2"; NOZZLE_SIZE=49' - 0"; NOZZLE_TOP_OD=6' - 4"; NOZZLE_TOP_RAD=3' - 2"; NOZZLE_WB/4=1' - 8 3/16"; NOZZLE_WB_OD=8' - 5"; NOZZLE_WB_RAD=4' - 2 1/2"; NOZZLE_WB_RAD-2"=4' - 0 1/2"; RO=7' - 4 1/16"; RO/2=3' - 8 1/32"; TRANSITION_TOP=12' - 4 3/4"; TYPE=0' - 0"; Type Comments=Vari-Plume Laboratory Exhaust Mixed-Flow Inline Belt Drive With Isolation Box; UNIT_HEIGHT=7' - 11 1/2"; UNIT_HEIGHT*.75=5' - 11 5/8"; UNIT_OD=7' - 0 7/8"; UNIT_RADIUS=3' - 6 7/16"; UNIT_RADIUS*.6=3' - 2 3/16"; UNIT_RADIUS+4"=3' - 10 7/16"
- 120_QMXHPVP-12H-Isolation_Box: (A/2)+.25"=1' - 2 1/4"; (NOZZLE_HEIGHT-(NOZZLE_HEIGHT/8*2))/2=1' - 0"; (NOZZLE_WB_OD-NOZZLE_TOP_OD)/2=0' - 2 1/8"; A=2' - 4"; A/2=1' - 2"; B=5' - 11"; B/2=2' - 11 1/2"; C=3' - 1"; C/2=1' - 6 1/2"; E=2' - 3 3/16"; GA=0' - 0 3/32"; Model=QMXHPVP-Isolation Box; NOZZLE_BOTTOM_ID=1' - 5 1/16"; NOZZLE_BOTTOM_RAD=0' - 8 17/32"; NOZZLE_HEIGHT=2' - 8"; NOZZLE_HEIGHT/7*2=0' - 8"; NOZZLE_SIZE=12' - 0"; NOZZLE_TOP_OD=1' - 7 1/2"; NOZZLE_TOP_RAD=0' - 9 3/4"; NOZZLE_WB/4=0' - 5 19/32"; NOZZLE_WB_OD=2' - 4"; NOZZLE_WB_RAD=1' - 2"; NOZZLE_WB_RAD-2"=1' - 0"; RO=1' - 9"; RO/2=0' - 10 1/2"; TRANSITION_TOP=3' - 3 7/16"; TYPE=1' - 0"; Type Comments=Vari-Plume Laboratory Exhaust Mixed-Flow High Pressure Inline Belt Drive With Isolation Box; UNIT_HEIGHT=1' - 7 7/8"; UNIT_HEIGHT*.75=1' - 2 29/32"; UNIT_OD=1' - 5 1/16"; UNIT_RADIUS=0' - 8 17/32"; UNIT_RADIUS*.6=0' - 7 11/16"; UNIT_RADIUS+4"=1' - 0 17/32"
- 120_QMXHPVP-12L-Isolation_Box: (A/2)+.25"=1' - 2 1/4"; (NOZZLE_HEIGHT-(NOZZLE_HEIGHT/8*2))/2=1' - 0"; (NOZZLE_WB_OD-NOZZLE_TOP_OD)/2=0' - 2 1/8"; A=2' - 4"; A/2=1' - 2"; B=5' - 11"; B/2=2' - 11 1/2"; C=3' - 1"; C/2=1' - 6 1/2"; E=2' - 3 3/16"; GA=0' - 0 3/32"; Model=QMXHPVP-Isolation Box; NOZZLE_BOTTOM_ID=1' - 5 1/16"; NOZZLE_BOTTOM_RAD=0' - 8 17/32"; NOZZLE_HEIGHT=2' - 8"; NOZZLE_HEIGHT/7*2=0' - 8"; NOZZLE_SIZE=12' - 0"; NOZZLE_TOP_OD=1' - 7 1/2"; NOZZLE_TOP_RAD=0' - 9 3/4"; NOZZLE_WB/4=0' - 5 19/32"; NOZZLE_WB_OD=2' - 4"; NOZZLE_WB_RAD=1' - 2"; NOZZLE_WB_RAD-2"=1' - 0"; RO=1' - 9"; RO/2=0' - 10 1/2"; TRANSITION_TOP=3' - 3 7/16"; TYPE=1' - 0"; Type Comments=Vari-Plume Laboratory Exhaust Mixed-Flow High Pressure Inline Belt Drive With Isolation Box; UNIT_HEIGHT=1' - 7 7/8"; UNIT_HEIGHT*.75=1' - 2 29/32"; UNIT_OD=1' - 5 1/16"; UNIT_RADIUS=0' - 8 17/32"; UNIT_RADIUS*.6=0' - 7 11/16"; UNIT_RADIUS+4"=1' - 0 17/32"
- 120_QMXHPVP-9H-Isolation_Box: (A/2)+.25"=1' - 2 1/4"; (NOZZLE_HEIGHT-(NOZZLE_HEIGHT/8*2))/2=0' - 10 1/2"; (NOZZLE_WB_OD-NOZZLE_TOP_OD)/2=0' - 2 3/8"; A=2' - 4"; A/2=1' - 2"; B=5' - 11"; B/2=2' - 11 1/2"; C=3' - 1"; C/2=1' - 6 1/2"; E=2' - 3 3/16"; GA=0' - 0 3/32"; Model=QMXHPVP-Isolation Box; NOZZLE_BOTTOM_ID=1' - 0 13/16"; NOZZLE_BOTTOM_RAD=0' - 6 13/32"; NOZZLE_HEIGHT=2' - 4"; NOZZLE_HEIGHT/7*2=0' - 7"; NOZZLE_SIZE=9' - 0"; NOZZLE_TOP_OD=1' - 1 1/2"; NOZZLE_TOP_RAD=0' - 6 3/4"; NOZZLE_WB/4=0' - 4 19/32"; NOZZLE_WB_OD=1' - 11"; NOZZLE_WB_RAD=0' - 11 1/2"; NOZZLE_WB_RAD-2"=0' - 9 1/2"; RO=1' - 9"; RO/2=0' - 10 1/2"; TRANSITION_TOP=3' - 7 3/16"; TYPE=1' - 0"; Type Comments=Vari-Plume Laboratory Exhaust Mixed-Flow High Pressure Inline Belt Drive With Isolation Box; UNIT_HEIGHT=1' - 7 7/8"; UNIT_HEIGHT*.75=1' - 2 29/32"; UNIT_OD=1' - 5 1/16"; UNIT_RADIUS=0' - 8 17/32"; UNIT_RADIUS*.6=0' - 7 11/16"; UNIT_RADIUS+4"=1' - 0 17/32"
- 120_QMXHPVP-9L-Isolation_Box: (A/2)+.25"=1' - 2 1/4"; (NOZZLE_HEIGHT-(NOZZLE_HEIGHT/8*2))/2=0' - 10 1/2"; (NOZZLE_WB_OD-NOZZLE_TOP_OD)/2=0' - 2 3/8"; A=2' - 4"; A/2=1' - 2"; B=5' - 11"; B/2=2' - 11 1/2"; C=3' - 1"; C/2=1' - 6 1/2"; E=2' - 3 3/16"; GA=0' - 0 3/32"; Model=QMXHPVP-Isolation Box; NOZZLE_BOTTOM_ID=1' - 0 13/16"; NOZZLE_BOTTOM_RAD=0' - 6 13/32"; NOZZLE_HEIGHT=2' - 4"; NOZZLE_HEIGHT/7*2=0' - 7"; NOZZLE_SIZE=9' - 0"; NOZZLE_TOP_OD=1' - 1 1/2"; NOZZLE_TOP_RAD=0' - 6 3/4"; NOZZLE_WB/4=0' - 4 19/32"; NOZZLE_WB_OD=1' - 11"; NOZZLE_WB_RAD=0' - 11 1/2"; NOZZLE_WB_RAD-2"=0' - 9 1/2"; RO=1' - 9"; RO/2=0' - 10 1/2"; TRANSITION_TOP=3' - 7 3/16"; TYPE=1' - 0"; Type Comments=Vari-Plume Laboratory Exhaust Mixed-Flow High Pressure Inline Belt Drive With Isolation Box; UNIT_HEIGHT=1' - 7 7/8"; UNIT_HEIGHT*.75=1' - 2 29/32"; UNIT_OD=1' - 5 1/16"; UNIT_RADIUS=0' - 8 17/32"; UNIT_RADIUS*.6=0' - 7 11/16"; UNIT_RADIUS+4"=1' - 0 17/32"
- 135_QMXHPVP-12H-Isolation_Box: (A/2)+.25"=1' - 2 1/4"; (NOZZLE_HEIGHT-(NOZZLE_HEIGHT/8*2))/2=1' - 0"; (NOZZLE_WB_OD-NOZZLE_TOP_OD)/2=0' - 2 1/8"; A=2' - 4"; A/2=1' - 2"; B=6' - 5"; B/2=3' - 2 1/2"; C=3' - 3"; C/2=1' - 7 1/2"; E=2' - 3 1/8"; GA=0' - 0 3/32"; Model=QMXHPVP-Isolation Box; NOZZLE_BOTTOM_ID=1' - 5 1/16"; NOZZLE_BOTTOM_RAD=0' - 8 17/32"; NOZZLE_HEIGHT=2' - 8"; NOZZLE_HEIGHT/7*2=0' - 8"; NOZZLE_SIZE=12' - 0"; NOZZLE_TOP_OD=1' - 7 1/2"; NOZZLE_TOP_RAD=0' - 9 3/4"; NOZZLE_WB/4=0' - 5 19/32"; NOZZLE_WB_OD=2' - 4"; NOZZLE_WB_RAD=1' - 2"; NOZZLE_WB_RAD-2"=1' - 0"; RO=1' - 8 15/16"; RO/2=0' - 10 15/32"; TRANSITION_TOP=3' - 4 11/16"; TYPE=1' - 0"; Type Comments=Vari-Plume Laboratory Exhaust Mixed-Flow High Pressure Inline Belt Drive With Isolation Box; UNIT_HEIGHT=2' - 3"; UNIT_HEIGHT*.75=1' - 8 1/4"; UNIT_OD=1' - 7 1/4"; UNIT_RADIUS=0' - 9 5/8"; UNIT_RADIUS*.6=0' - 8 21/32"; UNIT_RADIUS+4"=1' - 1 5/8"
- 135_QMXHPVP-12L-Isolation_Box: (A/2)+.25"=1' - 2 1/4"; (NOZZLE_HEIGHT-(NOZZLE_HEIGHT/8*2))/2=1' - 0"; (NOZZLE_WB_OD-NOZZLE_TOP_OD)/2=0' - 2 1/8"; A=2' - 4"; A/2=1' - 2"; B=6' - 5"; B/2=3' - 2 1/2"; C=3' - 3"; C/2=1' - 7 1/2"; E=2' - 3 1/8"; GA=0' - 0 3/32"; Model=QMXHPVP-Isolation Box; NOZZLE_BOTTOM_ID=1' - 5 1/16"; NOZZLE_BOTTOM_RAD=0' - 8 17/32"; NOZZLE_HEIGHT=2' - 8"; NOZZLE_HEIGHT/7*2=0' - 8"; NOZZLE_SIZE=12' - 0"; NOZZLE_TOP_OD=1' - 7 1/2"; NOZZLE_TOP_RAD=0' - 9 3/4"; NOZZLE_WB/4=0' - 5 19/32"; NOZZLE_WB_OD=2' - 4"; NOZZLE_WB_RAD=1' - 2"; NOZZLE_WB_RAD-2"=1' - 0"; RO=1' - 8 15/16"; RO/2=0' - 10 15/32"; TRANSITION_TOP=3' - 4 11/16"; TYPE=1' - 0"; Type Comments=Vari-Plume Laboratory Exhaust Mixed-Flow High Pressure Inline Belt Drive With Isolation Box; UNIT_HEIGHT=2' - 3"; UNIT_HEIGHT*.75=1' - 8 1/4"; UNIT_OD=1' - 7 1/4"; UNIT_RADIUS=0' - 9 5/8"; UNIT_RADIUS*.6=0' - 8 21/32"; UNIT_RADIUS+4"=1' - 1 5/8"
- 135_QMXHPVP-9H-Isolation_Box: (A/2)+.25"=1' - 2 1/4"; (NOZZLE_HEIGHT-(NOZZLE_HEIGHT/8*2))/2=0' - 10 1/2"; (NOZZLE_WB_OD-NOZZLE_TOP_OD)/2=0' - 2 3/8"; A=2' - 4"; A/2=1' - 2"; B=6' - 5"; B/2=3' - 2 1/2"; C=3' - 3"; C/2=1' - 7 1/2"; E=2' - 3 1/8"; GA=0' - 0 3/32"; Model=QMXHPVP-Isolation Box; NOZZLE_BOTTOM_ID=1' - 0 13/16"; NOZZLE_BOTTOM_RAD=0' - 6 13/32"; NOZZLE_HEIGHT=2' - 4"; NOZZLE_HEIGHT/7*2=0' - 7"; NOZZLE_SIZE=9' - 0"; NOZZLE_TOP_OD=1' - 1 1/2"; NOZZLE_TOP_RAD=0' - 6 3/4"; NOZZLE_WB/4=0' - 4 19/32"; NOZZLE_WB_OD=1' - 11"; NOZZLE_WB_RAD=0' - 11 1/2"; NOZZLE_WB_RAD-2"=0' - 9 1/2"; RO=1' - 8 15/16"; RO/2=0' - 10 15/32"; TRANSITION_TOP=4' - 0 11/16"; TYPE=1' - 0"; Type Comments=Vari-Plume Laboratory Exhaust Mixed-Flow High Pressure Inline Belt Drive With Isolation Box; UNIT_HEIGHT=2' - 3"; UNIT_HEIGHT*.75=1' - 8 1/4"; UNIT_OD=1' - 7 1/4"; UNIT_RADIUS=0' - 9 5/8"; UNIT_RADIUS*.6=0' - 8 21/32"; UNIT_RADIUS+4"=1' - 1 5/8"
- 135_QMXHPVP-9L-Isolation_Box: (A/2)+.25"=1' - 2 1/4"; (NOZZLE_HEIGHT-(NOZZLE_HEIGHT/8*2))/2=0' - 10 1/2"; (NOZZLE_WB_OD-NOZZLE_TOP_OD)/2=0' - 2 3/8"; A=2' - 4"; A/2=1' - 2"; B=6' - 5"; B/2=3' - 2 1/2"; C=3' - 3"; C/2=1' - 7 1/2"; E=2' - 3 1/8"; GA=0' - 0 3/32"; Model=QMXHPVP-Isolation Box; NOZZLE_BOTTOM_ID=1' - 0 13/16"; NOZZLE_BOTTOM_RAD=0' - 6 13/32"; NOZZLE_HEIGHT=2' - 4"; NOZZLE_HEIGHT/7*2=0' - 7"; NOZZLE_SIZE=9' - 0"; NOZZLE_TOP_OD=1' - 1 1/2"; NOZZLE_TOP_RAD=0' - 6 3/4"; NOZZLE_WB/4=0' - 4 19/32"; NOZZLE_WB_OD=1' - 11"; NOZZLE_WB_RAD=0' - 11 1/2"; NOZZLE_WB_RAD-2"=0' - 9 1/2"; RO=1' - 8 15/16"; RO/2=0' - 10 15/32"; TRANSITION_TOP=4' - 0 11/16"; TYPE=1' - 0"; Type Comments=Vari-Plume Laboratory Exhaust Mixed-Flow High Pressure Inline Belt Drive With Isolation Box; UNIT_HEIGHT=2' - 3"; UNIT_HEIGHT*.75=1' - 8 1/4"; UNIT_OD=1' - 7 1/4"; UNIT_RADIUS=0' - 9 5/8"; UNIT_RADIUS*.6=0' - 8 21/32"; UNIT_RADIUS+4"=1' - 1 5/8"
- 150_QMXHPVP-12H-Isolation_Box: (A/2)+.25"=1' - 3 1/4"; (NOZZLE_HEIGHT-(NOZZLE_HEIGHT/8*2))/2=1' - 0"; (NOZZLE_WB_OD-NOZZLE_TOP_OD)/2=0' - 2 1/8"; A=2' - 6"; A/2=1' - 3"; B=7' - 3"; B/2=3' - 7 1/2"; C=3' - 6"; C/2=1' - 9"; E=2' - 5 1/8"; GA=0' - 0 3/32"; Model=QMXHPVP-Isolation Box; NOZZLE_BOTTOM_ID=1' - 5 1/16"; NOZZLE_BOTTOM_RAD=0' - 8 17/32"; NOZZLE_HEIGHT=2' - 8"; NOZZLE_HEIGHT/7*2=0' - 8"; NOZZLE_SIZE=12' - 0"; NOZZLE_TOP_OD=1' - 7 1/2"; NOZZLE_TOP_RAD=0' - 9 3/4"; NOZZLE_WB/4=0' - 5 19/32"; NOZZLE_WB_OD=2' - 4"; NOZZLE_WB_RAD=1' - 2"; NOZZLE_WB_RAD-2"=1' - 0"; RO=1' - 10 15/16"; RO/2=0' - 11 15/32"; TRANSITION_TOP=3' - 10 1/4"; TYPE=1' - 0"; Type Comments=Vari-Plume Laboratory Exhaust Mixed-Flow High Pressure Inline Belt Drive With Isolation Box; UNIT_HEIGHT=2' - 6"; UNIT_HEIGHT*.75=1' - 10 1/2"; UNIT_OD=1' - 9 3/8"; UNIT_RADIUS=0' - 10 11/16"; UNIT_RADIUS*.6=0' - 9 5/8"; UNIT_RADIUS+4"=1' - 2 11/16"
- 150_QMXHPVP-12L-Isolation_Box: (A/2)+.25"=1' - 3 1/4"; (NOZZLE_HEIGHT-(NOZZLE_HEIGHT/8*2))/2=1' - 0"; (NOZZLE_WB_OD-NOZZLE_TOP_OD)/2=0' - 2 1/8"; A=2' - 6"; A/2=1' - 3"; B=7' - 3"; B/2=3' - 7 1/2"; C=3' - 6"; C/2=1' - 9"; E=2' - 5 1/8"; GA=0' - 0 3/32"; Model=QMXHPVP-Isolation Box; NOZZLE_BOTTOM_ID=1' - 5 1/16"; NOZZLE_BOTTOM_RAD=0' - 8 17/32"; NOZZLE_HEIGHT=2' - 8"; NOZZLE_HEIGHT/7*2=0' - 8"; NOZZLE_SIZE=12' - 0"; NOZZLE_TOP_OD=1' - 7 1/2"; NOZZLE_TOP_RAD=0' - 9 3/4"; NOZZLE_WB/4=0' - 5 19/32"; NOZZLE_WB_OD=2' - 4"; NOZZLE_WB_RAD=1' - 2"; NOZZLE_WB_RAD-2"=1' - 0"; RO=1' - 10 15/16"; RO/2=0' - 11 15/32"; TRANSITION_TOP=3' - 10 1/4"; TYPE=1' - 0"; Type Comments=Vari-Plume Laboratory Exhaust Mixed-Flow High Pressure Inline Belt Drive With Isolation Box; UNIT_HEIGHT=2' - 6"; UNIT_HEIGHT*.75=1' - 10 1/2"; UNIT_OD=1' - 9 3/8"; UNIT_RADIUS=0' - 10 11/16"; UNIT_RADIUS*.6=0' - 9 5/8"; UNIT_RADIUS+4"=1' - 2 11/16"
- 150_QMXHPVP-15H-Isolation_Box: (A/2)+.25"=1' - 3 1/4"; (NOZZLE_HEIGHT-(NOZZLE_HEIGHT/8*2))/2=1' - 4 1/8"; (NOZZLE_WB_OD-NOZZLE_TOP_OD)/2=0' - 3 1/4"; A=2' - 6"; A/2=1' - 3"; B=7' - 3"; B/2=3' - 7 1/2"; C=3' - 6"; C/2=1' - 9"; E=2' - 5 1/8"; GA=0' - 0 3/32"; Model=QMXHPVP-Isolation Box; NOZZLE_BOTTOM_ID=1' - 9 3/8"; NOZZLE_BOTTOM_RAD=0' - 10 11/16"; NOZZLE_HEIGHT=3' - 7"; NOZZLE_HEIGHT/7*2=0' - 10 3/4"; NOZZLE_SIZE=15' - 0"; NOZZLE_TOP_OD=1' - 11"; NOZZLE_TOP_RAD=0' - 11 1/2"; NOZZLE_WB/4=0' - 7 3/16"; NOZZLE_WB_OD=3' - 0"; NOZZLE_WB_RAD=1' - 6"; NOZZLE_WB_RAD-2"=1' - 4"; RO=1' - 10 15/16"; RO/2=0' - 11 15/32"; TRANSITION_TOP=3' - 7 5/16"; TYPE=1' - 0"; Type Comments=Vari-Plume Laboratory Exhaust Mixed-Flow High Pressure Inline Belt Drive With Isolation Box; UNIT_HEIGHT=2' - 6"; UNIT_HEIGHT*.75=1' - 10 1/2"; UNIT_OD=1' - 9 3/8"; UNIT_RADIUS=0' - 10 11/16"; UNIT_RADIUS*.6=0' - 9 5/8"; UNIT_RADIUS+4"=1' - 2 11/16"
- 150_QMXHPVP-15L-Isolation_Box: (A/2)+.25"=1' - 3 1/4"; (NOZZLE_HEIGHT-(NOZZLE_HEIGHT/8*2))/2=1' - 4 1/8"; (NOZZLE_WB_OD-NOZZLE_TOP_OD)/2=0' - 3 1/4"; A=2' - 6"; A/2=1' - 3"; B=7' - 3"; B/2=3' - 7 1/2"; C=3' - 6"; C/2=1' - 9"; E=2' - 5 1/8"; GA=0' - 0 3/32"; Model=QMXHPVP-Isolation Box; NOZZLE_BOTTOM_ID=1' - 9 3/8"; NOZZLE_BOTTOM_RAD=0' - 10 11/16"; NOZZLE_HEIGHT=3' - 7"; NOZZLE_HEIGHT/7*2=0' - 10 3/4"; NOZZLE_SIZE=15' - 0"; NOZZLE_TOP_OD=1' - 11"; NOZZLE_TOP_RAD=0' - 11 1/2"; NOZZLE_WB/4=0' - 7 3/16"; NOZZLE_WB_OD=3' - 0"; NOZZLE_WB_RAD=1' - 6"; NOZZLE_WB_RAD-2"=1' - 4"; RO=1' - 10 15/16"; RO/2=0' - 11 15/32"; TRANSITION_TOP=3' - 7 5/16"; TYPE=1' - 0"; Type Comments=Vari-Plume Laboratory Exhaust Mixed-Flow High Pressure Inline Belt Drive With Isolation Box; UNIT_HEIGHT=2' - 6"; UNIT_HEIGHT*.75=1' - 10 1/2"; UNIT_OD=1' - 9 3/8"; UNIT_RADIUS=0' - 10 11/16"; UNIT_RADIUS*.6=0' - 9 5/8"; UNIT_RADIUS+4"=1' - 2 11/16"
- 150_QMXHPVP-9H-Isolation_Box: (A/2)+.25"=1' - 3 1/4"; (NOZZLE_HEIGHT-(NOZZLE_HEIGHT/8*2))/2=0' - 10 1/2"; (NOZZLE_WB_OD-NOZZLE_TOP_OD)/2=0' - 2 3/8"; A=2' - 6"; A/2=1' - 3"; B=7' - 3"; B/2=3' - 7 1/2"; C=3' - 6"; C/2=1' - 9"; E=2' - 5 1/8"; GA=0' - 0 3/32"; Model=QMXHPVP-Isolation Box; NOZZLE_BOTTOM_ID=1' - 0 13/16"; NOZZLE_BOTTOM_RAD=0' - 6 13/32"; NOZZLE_HEIGHT=2' - 4"; NOZZLE_HEIGHT/7*2=0' - 7"; NOZZLE_SIZE=9' - 0"; NOZZLE_TOP_OD=1' - 1 1/2"; NOZZLE_TOP_RAD=0' - 6 3/4"; NOZZLE_WB/4=0' - 4 19/32"; NOZZLE_WB_OD=1' - 11"; NOZZLE_WB_RAD=0' - 11 1/2"; NOZZLE_WB_RAD-2"=0' - 9 1/2"; RO=1' - 10 15/16"; RO/2=0' - 11 15/32"; TRANSITION_TOP=4' - 6 1/4"; TYPE=1' - 0"; Type Comments=Vari-Plume Laboratory Exhaust Mixed-Flow High Pressure Inline Belt Drive With Isolation Box; UNIT_HEIGHT=2' - 6"; UNIT_HEIGHT*.75=1' - 10 1/2"; UNIT_OD=1' - 9 3/8"; UNIT_RADIUS=0' - 10 11/16"; UNIT_RADIUS*.6=0' - 9 5/8"; UNIT_RADIUS+4"=1' - 2 11/16"
- 150_QMXHPVP-9L-Isolation_Box: (A/2)+.25"=1' - 3 1/4"; (NOZZLE_HEIGHT-(NOZZLE_HEIGHT/8*2))/2=0' - 10 1/2"; (NOZZLE_WB_OD-NOZZLE_TOP_OD)/2=0' - 2 3/8"; A=2' - 6"; A/2=1' - 3"; B=7' - 3"; B/2=3' - 7 1/2"; C=3' - 6"; C/2=1' - 9"; E=2' - 5 1/8"; GA=0' - 0 3/32"; Model=QMXHPVP-Isolation Box; NOZZLE_BOTTOM_ID=1' - 0 13/16"; NOZZLE_BOTTOM_RAD=0' - 6 13/32"; NOZZLE_HEIGHT=2' - 4"; NOZZLE_HEIGHT/7*2=0' - 7"; NOZZLE_SIZE=9' - 0"; NOZZLE_TOP_OD=1' - 1 1/2"; NOZZLE_TOP_RAD=0' - 6 3/4"; NOZZLE_WB/4=0' - 4 19/32"; NOZZLE_WB_OD=1' - 11"; NOZZLE_WB_RAD=0' - 11 1/2"; NOZZLE_WB_RAD-2"=0' - 9 1/2"; RO=1' - 10 15/16"; RO/2=0' - 11 15/32"; TRANSITION_TOP=4' - 6 1/4"; TYPE=1' - 0"; Type Comments=Vari-Plume Laboratory Exhaust Mixed-Flow High Pressure Inline Belt Drive With Isolation Box; UNIT_HEIGHT=2' - 6"; UNIT_HEIGHT*.75=1' - 10 1/2"; UNIT_OD=1' - 9 3/8"; UNIT_RADIUS=0' - 10 11/16"; UNIT_RADIUS*.6=0' - 9 5/8"; UNIT_RADIUS+4"=1' - 2 11/16"
- 165_QMXHPVP-12H-Isolation_Box: (A/2)+.25"=1' - 4 1/4"; (NOZZLE_HEIGHT-(NOZZLE_HEIGHT/8*2))/2=1' - 0"; (NOZZLE_WB_OD-NOZZLE_TOP_OD)/2=0' - 2 1/8"; A=2' - 8"; A/2=1' - 4"; B=7' - 5"; B/2=3' - 8 1/2"; C=3' - 8"; C/2=1' - 10"; E=2' - 7 1/8"; GA=0' - 0 3/32"; Model=QMXHPVP-Isolation Box; NOZZLE_BOTTOM_ID=1' - 5 1/16"; NOZZLE_BOTTOM_RAD=0' - 8 17/32"; NOZZLE_HEIGHT=2' - 8"; NOZZLE_HEIGHT/7*2=0' - 8"; NOZZLE_SIZE=12' - 0"; NOZZLE_TOP_OD=1' - 7 1/2"; NOZZLE_TOP_RAD=0' - 9 3/4"; NOZZLE_WB/4=0' - 5 19/32"; NOZZLE_WB_OD=2' - 4"; NOZZLE_WB_RAD=1' - 2"; NOZZLE_WB_RAD-2"=1' - 0"; RO=2' - 0 15/16"; RO/2=1' - 0 15/32"; TRANSITION_TOP=4' - 5 1/4"; TYPE=1' - 0"; Type Comments=Vari-Plume Laboratory Exhaust Mixed-Flow High Pressure Inline Belt Drive With Isolation Box; UNIT_HEIGHT=2' - 9"; UNIT_HEIGHT*.75=2' - 0 3/4"; UNIT_OD=1' - 11 1/2"; UNIT_RADIUS=0' - 11 3/4"; UNIT_RADIUS*.6=0' - 10 9/16"; UNIT_RADIUS+4"=1' - 3 3/4"
- 165_QMXHPVP-12L-Isolation_Box: (A/2)+.25"=1' - 4 1/4"; (NOZZLE_HEIGHT-(NOZZLE_HEIGHT/8*2))/2=1' - 0"; (NOZZLE_WB_OD-NOZZLE_TOP_OD)/2=0' - 2 1/8"; A=2' - 8"; A/2=1' - 4"; B=7' - 5"; B/2=3' - 8 1/2"; C=3' - 8"; C/2=1' - 10"; E=2' - 7 1/8"; GA=0' - 0 3/32"; Model=QMXHPVP-Isolation Box; NOZZLE_BOTTOM_ID=1' - 5 1/16"; NOZZLE_BOTTOM_RAD=0' - 8 17/32"; NOZZLE_HEIGHT=2' - 8"; NOZZLE_HEIGHT/7*2=0' - 8"; NOZZLE_SIZE=12' - 0"; NOZZLE_TOP_OD=1' - 7 1/2"; NOZZLE_TOP_RAD=0' - 9 3/4"; NOZZLE_WB/4=0' - 5 19/32"; NOZZLE_WB_OD=2' - 4"; NOZZLE_WB_RAD=1' - 2"; NOZZLE_WB_RAD-2"=1' - 0"; RO=2' - 0 15/16"; RO/2=1' - 0 15/32"; TRANSITION_TOP=4' - 5 1/4"; TYPE=1' - 0"; Type Comments=Vari-Plume Laboratory Exhaust Mixed-Flow High Pressure Inline Belt Drive With Isolation Box; UNIT_HEIGHT=2' - 9"; UNIT_HEIGHT*.75=2' - 0 3/4"; UNIT_OD=1' - 11 1/2"; UNIT_RADIUS=0' - 11 3/4"; UNIT_RADIUS*.6=0' - 10 9/16"; UNIT_RADIUS+4"=1' - 3 3/4"
- 165_QMXHPVP-15H-Isolation_Box: (A/2)+.25"=1' - 4 1/4"; (NOZZLE_HEIGHT-(NOZZLE_HEIGHT/8*2))/2=1' - 4 1/8"; (NOZZLE_WB_OD-NOZZLE_TOP_OD)/2=0' - 3 1/4"; A=2' - 8"; A/2=1' - 4"; B=7' - 5"; B/2=3' - 8 1/2"; C=3' - 8"; C/2=1' - 10"; E=2' - 7 1/8"; GA=0' - 0 3/32"; Model=QMXHPVP-Isolation Box; NOZZLE_BOTTOM_ID=1' - 9 3/8"; NOZZLE_BOTTOM_RAD=0' - 10 11/16"; NOZZLE_HEIGHT=3' - 7"; NOZZLE_HEIGHT/7*2=0' - 10 3/4"; NOZZLE_SIZE=15' - 0"; NOZZLE_TOP_OD=1' - 11"; NOZZLE_TOP_RAD=0' - 11 1/2"; NOZZLE_WB/4=0' - 7 3/16"; NOZZLE_WB_OD=3' - 0"; NOZZLE_WB_RAD=1' - 6"; NOZZLE_WB_RAD-2"=1' - 4"; RO=2' - 0 15/16"; RO/2=1' - 0 15/32"; TRANSITION_TOP=3' - 9 5/16"; TYPE=1' - 0"; Type Comments=Vari-Plume Laboratory Exhaust Mixed-Flow High Pressure Inline Belt Drive With Isolation Box; UNIT_HEIGHT=2' - 9"; UNIT_HEIGHT*.75=2' - 0 3/4"; UNIT_OD=1' - 11 1/2"; UNIT_RADIUS=0' - 11 3/4"; UNIT_RADIUS*.6=0' - 10 9/16"; UNIT_RADIUS+4"=1' - 3 3/4"
- 165_QMXHPVP-15L-Isolation_Box: (A/2)+.25"=1' - 4 1/4"; (NOZZLE_HEIGHT-(NOZZLE_HEIGHT/8*2))/2=1' - 4 1/8"; (NOZZLE_WB_OD-NOZZLE_TOP_OD)/2=0' - 3 1/4"; A=2' - 8"; A/2=1' - 4"; B=7' - 5"; B/2=3' - 8 1/2"; C=3' - 8"; C/2=1' - 10"; E=2' - 7 1/8"; GA=0' - 0 3/32"; Model=QMXHPVP-Isolation Box; NOZZLE_BOTTOM_ID=1' - 9 3/8"; NOZZLE_BOTTOM_RAD=0' - 10 11/16"; NOZZLE_HEIGHT=3' - 7"; NOZZLE_HEIGHT/7*2=0' - 10 3/4"; NOZZLE_SIZE=15' - 0"; NOZZLE_TOP_OD=1' - 11"; NOZZLE_TOP_RAD=0' - 11 1/2"; NOZZLE_WB/4=0' - 7 3/16"; NOZZLE_WB_OD=3' - 0"; NOZZLE_WB_RAD=1' - 6"; NOZZLE_WB_RAD-2"=1' - 4"; RO=2' - 0 15/16"; RO/2=1' - 0 15/32"; TRANSITION_TOP=3' - 9 5/16"; TYPE=1' - 0"; Type Comments=Vari-Plume Laboratory Exhaust Mixed-Flow High Pressure Inline Belt Drive With Isolation Box; UNIT_HEIGHT=2' - 9"; UNIT_HEIGHT*.75=2' - 0 3/4"; UNIT_OD=1' - 11 1/2"; UNIT_RADIUS=0' - 11 3/4"; UNIT_RADIUS*.6=0' - 10 9/16"; UNIT_RADIUS+4"=1' - 3 3/4"
- 165_QMXHPVP-9H-Isolation_Box: (A/2)+.25"=1' - 4 1/4"; (NOZZLE_HEIGHT-(NOZZLE_HEIGHT/8*2))/2=0' - 10 1/2"; (NOZZLE_WB_OD-NOZZLE_TOP_OD)/2=0' - 2 3/8"; A=2' - 8"; A/2=1' - 4"; B=7' - 5"; B/2=3' - 8 1/2"; C=3' - 8"; C/2=1' - 10"; E=2' - 7 1/8"; GA=0' - 0 3/32"; Model=QMXHPVP-Isolation Box; NOZZLE_BOTTOM_ID=1' - 0 13/16"; NOZZLE_BOTTOM_RAD=0' - 6 13/32"; NOZZLE_HEIGHT=2' - 4"; NOZZLE_HEIGHT/7*2=0' - 7"; NOZZLE_SIZE=9' - 0"; NOZZLE_TOP_OD=1' - 1 1/2"; NOZZLE_TOP_RAD=0' - 6 3/4"; NOZZLE_WB/4=0' - 4 19/32"; NOZZLE_WB_OD=1' - 11"; NOZZLE_WB_RAD=0' - 11 1/2"; NOZZLE_WB_RAD-2"=0' - 9 1/2"; RO=2' - 0 15/16"; RO/2=1' - 0 15/32"; TRANSITION_TOP=5' - 1 1/4"; TYPE=1' - 0"; Type Comments=Vari-Plume Laboratory Exhaust Mixed-Flow High Pressure Inline Belt Drive With Isolation Box; UNIT_HEIGHT=2' - 9"; UNIT_HEIGHT*.75=2' - 0 3/4"; UNIT_OD=1' - 11 1/2"; UNIT_RADIUS=0' - 11 3/4"; UNIT_RADIUS*.6=0' - 10 9/16"; UNIT_RADIUS+4"=1' - 3 3/4"
- 165_QMXHPVP-9L-Isolation_Box: (A/2)+.25"=1' - 4 1/4"; (NOZZLE_HEIGHT-(NOZZLE_HEIGHT/8*2))/2=0' - 10 1/2"; (NOZZLE_WB_OD-NOZZLE_TOP_OD)/2=0' - 2 3/8"; A=2' - 8"; A/2=1' - 4"; B=7' - 5"; B/2=3' - 8 1/2"; C=3' - 8"; C/2=1' - 10"; E=2' - 7 1/8"; GA=0' - 0 3/32"; Model=QMXHPVP-Isolation Box; NOZZLE_BOTTOM_ID=1' - 0 13/16"; NOZZLE_BOTTOM_RAD=0' - 6 13/32"; NOZZLE_HEIGHT=2' - 4"; NOZZLE_HEIGHT/7*2=0' - 7"; NOZZLE_SIZE=9' - 0"; NOZZLE_TOP_OD=1' - 1 1/2"; NOZZLE_TOP_RAD=0' - 6 3/4"; NOZZLE_WB/4=0' - 4 19/32"; NOZZLE_WB_OD=1' - 11"; NOZZLE_WB_RAD=0' - 11 1/2"; NOZZLE_WB_RAD-2"=0' - 9 1/2"; RO=2' - 0 15/16"; RO/2=1' - 0 15/32"; TRANSITION_TOP=5' - 1 1/4"; TYPE=1' - 0"; Type Comments=Vari-Plume Laboratory Exhaust Mixed-Flow High Pressure Inline Belt Drive With Isolation Box; UNIT_HEIGHT=2' - 9"; UNIT_HEIGHT*.75=2' - 0 3/4"; UNIT_OD=1' - 11 1/2"; UNIT_RADIUS=0' - 11 3/4"; UNIT_RADIUS*.6=0' - 10 9/16"; UNIT_RADIUS+4"=1' - 3 3/4"
- 180_QMXHPVP-12H-Isolation_Box: (A/2)+.25"=1' - 5 1/4"; (NOZZLE_HEIGHT-(NOZZLE_HEIGHT/8*2))/2=1' - 0"; (NOZZLE_WB_OD-NOZZLE_TOP_OD)/2=0' - 2 1/8"; A=2' - 10"; A/2=1' - 5"; B=8' - 2"; B/2=4' - 1"; C=3' - 10"; C/2=1' - 11"; E=2' - 9 1/8"; GA=0' - 0 3/32"; Model=QMXHPVP-Isolation Box; NOZZLE_BOTTOM_ID=1' - 5 1/16"; NOZZLE_BOTTOM_RAD=0' - 8 17/32"; NOZZLE_HEIGHT=2' - 8"; NOZZLE_HEIGHT/7*2=0' - 8"; NOZZLE_SIZE=12' - 0"; NOZZLE_TOP_OD=1' - 7 1/2"; NOZZLE_TOP_RAD=0' - 9 3/4"; NOZZLE_WB/4=0' - 5 19/32"; NOZZLE_WB_OD=2' - 4"; NOZZLE_WB_RAD=1' - 2"; NOZZLE_WB_RAD-2"=1' - 0"; RO=2' - 2 15/16"; RO/2=1' - 1 15/32"; TRANSITION_TOP=4' - 11 1/16"; TYPE=1' - 0"; Type Comments=Vari-Plume Laboratory Exhaust Mixed-Flow High Pressure Inline Belt Drive With Isolation Box; UNIT_HEIGHT=2' - 11"; UNIT_HEIGHT*.75=2' - 2 1/4"; UNIT_OD=2' - 1 5/8"; UNIT_RADIUS=1' - 0 13/16"; UNIT_RADIUS*.6=0' - 11 17/32"; UNIT_RADIUS+4"=1' - 4 13/16"
- 180_QMXHPVP-12L-Isolation_Box: (A/2)+.25"=1' - 5 1/4"; (NOZZLE_HEIGHT-(NOZZLE_HEIGHT/8*2))/2=1' - 0"; (NOZZLE_WB_OD-NOZZLE_TOP_OD)/2=0' - 2 1/8"; A=2' - 10"; A/2=1' - 5"; B=8' - 2"; B/2=4' - 1"; C=3' - 10"; C/2=1' - 11"; E=2' - 9 1/8"; GA=0' - 0 3/32"; Model=QMXHPVP-Isolation Box; NOZZLE_BOTTOM_ID=1' - 5 1/16"; NOZZLE_BOTTOM_RAD=0' - 8 17/32"; NOZZLE_HEIGHT=2' - 8"; NOZZLE_HEIGHT/7*2=0' - 8"; NOZZLE_SIZE=12' - 0"; NOZZLE_TOP_OD=1' - 7 1/2"; NOZZLE_TOP_RAD=0' - 9 3/4"; NOZZLE_WB/4=0' - 5 19/32"; NOZZLE_WB_OD=2' - 4"; NOZZLE_WB_RAD=1' - 2"; NOZZLE_WB_RAD-2"=1' - 0"; RO=2' - 2 15/16"; RO/2=1' - 1 15/32"; TRANSITION_TOP=4' - 11 1/16"; TYPE=1' - 0"; Type Comments=Vari-Plume Laboratory Exhaust Mixed-Flow High Pressure Inline Belt Drive With Isolation Box; UNIT_HEIGHT=2' - 11"; UNIT_HEIGHT*.75=2' - 2 1/4"; UNIT_OD=2' - 1 5/8"; UNIT_RADIUS=1' - 0 13/16"; UNIT_RADIUS*.6=0' - 11 17/32"; UNIT_RADIUS+4"=1' - 4 13/16"
- 180_QMXHPVP-15H-Isolation_Box: (A/2)+.25"=1' - 5 1/4"; (NOZZLE_HEIGHT-(NOZZLE_HEIGHT/8*2))/2=1' - 4 1/8"; (NOZZLE_WB_OD-NOZZLE_TOP_OD)/2=0' - 3 1/4"; A=2' - 10"; A/2=1' - 5"; B=8' - 2"; B/2=4' - 1"; C=3' - 10"; C/2=1' - 11"; E=2' - 9 1/8"; GA=0' - 0 3/32"; Model=QMXHPVP-Isolation Box; NOZZLE_BOTTOM_ID=1' - 9 3/8"; NOZZLE_BOTTOM_RAD=0' - 10 11/16"; NOZZLE_HEIGHT=3' - 7"; NOZZLE_HEIGHT/7*2=0' - 10 3/4"; NOZZLE_SIZE=15' - 0"; NOZZLE_TOP_OD=1' - 11"; NOZZLE_TOP_RAD=0' - 11 1/2"; NOZZLE_WB/4=0' - 7 3/16"; NOZZLE_WB_OD=3' - 0"; NOZZLE_WB_RAD=1' - 6"; NOZZLE_WB_RAD-2"=1' - 4"; RO=2' - 2 15/16"; RO/2=1' - 1 15/32"; TRANSITION_TOP=4' - 3 1/8"; TYPE=1' - 0"; Type Comments=Vari-Plume Laboratory Exhaust Mixed-Flow High Pressure Inline Belt Drive With Isolation Box; UNIT_HEIGHT=2' - 11"; UNIT_HEIGHT*.75=2' - 2 1/4"; UNIT_OD=2' - 1 5/8"; UNIT_RADIUS=1' - 0 13/16"; UNIT_RADIUS*.6=0' - 11 17/32"; UNIT_RADIUS+4"=1' - 4 13/16"
- 180_QMXHPVP-15L-Isolation_Box: (A/2)+.25"=1' - 5 1/4"; (NOZZLE_HEIGHT-(NOZZLE_HEIGHT/8*2))/2=1' - 4 1/8"; (NOZZLE_WB_OD-NOZZLE_TOP_OD)/2=0' - 3 1/4"; A=2' - 10"; A/2=1' - 5"; B=8' - 2"; B/2=4' - 1"; C=3' - 10"; C/2=1' - 11"; E=2' - 9 1/8"; GA=0' - 0 3/32"; Model=QMXHPVP-Isolation Box; NOZZLE_BOTTOM_ID=1' - 9 3/8"; NOZZLE_BOTTOM_RAD=0' - 10 11/16"; NOZZLE_HEIGHT=3' - 7"; NOZZLE_HEIGHT/7*2=0' - 10 3/4"; NOZZLE_SIZE=15' - 0"; NOZZLE_TOP_OD=1' - 11"; NOZZLE_TOP_RAD=0' - 11 1/2"; NOZZLE_WB/4=0' - 7 3/16"; NOZZLE_WB_OD=3' - 0"; NOZZLE_WB_RAD=1' - 6"; NOZZLE_WB_RAD-2"=1' - 4"; RO=2' - 2 15/16"; RO/2=1' - 1 15/32"; TRANSITION_TOP=4' - 3 1/8"; TYPE=1' - 0"; Type Comments=Vari-Plume Laboratory Exhaust Mixed-Flow High Pressure Inline Belt Drive With Isolation Box; UNIT_HEIGHT=2' - 11"; UNIT_HEIGHT*.75=2' - 2 1/4"; UNIT_OD=2' - 1 5/8"; UNIT_RADIUS=1' - 0 13/16"; UNIT_RADIUS*.6=0' - 11 17/32"; UNIT_RADIUS+4"=1' - 4 13/16"
- 180_QMXHPVP-18H-Isolation_Box: (A/2)+.25"=1' - 5 1/4"; (NOZZLE_HEIGHT-(NOZZLE_HEIGHT/8*2))/2=1' - 6"; (NOZZLE_WB_OD-NOZZLE_TOP_OD)/2=0' - 3 7/8"; A=2' - 10"; A/2=1' - 5"; B=8' - 2"; B/2=4' - 1"; C=3' - 10"; C/2=1' - 11"; E=2' - 9 1/8"; GA=0' - 0 3/32"; Model=QMXHPVP-Isolation Box; NOZZLE_BOTTOM_ID=2' - 1 5/8"; NOZZLE_BOTTOM_RAD=1' - 0 13/16"; NOZZLE_HEIGHT=4' - 0"; NOZZLE_HEIGHT/7*2=1' - 0"; NOZZLE_SIZE=18' - 0"; NOZZLE_TOP_OD=2' - 3 1/2"; NOZZLE_TOP_RAD=1' - 1 3/4"; NOZZLE_WB/4=0' - 8 19/32"; NOZZLE_WB_OD=3' - 7"; NOZZLE_WB_RAD=1' - 9 1/2"; NOZZLE_WB_RAD-2"=1' - 7 1/2"; RO=2' - 2 15/16"; RO/2=1' - 1 15/32"; TRANSITION_TOP=4' - 0 1/2"; TYPE=1' - 0"; Type Comments=Vari-Plume Laboratory Exhaust Mixed-Flow High Pressure Inline Belt Drive With Isolation Box; UNIT_HEIGHT=2' - 11"; UNIT_HEIGHT*.75=2' - 2 1/4"; UNIT_OD=2' - 1 5/8"; UNIT_RADIUS=1' - 0 13/16"; UNIT_RADIUS*.6=0' - 11 17/32"; UNIT_RADIUS+4"=1' - 4 13/16"
- 180_QMXHPVP-18L-Isolation_Box: (A/2)+.25"=1' - 5 1/4"; (NOZZLE_HEIGHT-(NOZZLE_HEIGHT/8*2))/2=1' - 6"; (NOZZLE_WB_OD-NOZZLE_TOP_OD)/2=0' - 3 7/8"; A=2' - 10"; A/2=1' - 5"; B=8' - 2"; B/2=4' - 1"; C=3' - 10"; C/2=1' - 11"; E=2' - 9 1/8"; GA=0' - 0 3/32"; Model=QMXHPVP-Isolation Box; NOZZLE_BOTTOM_ID=2' - 1 5/8"; NOZZLE_BOTTOM_RAD=1' - 0 13/16"; NOZZLE_HEIGHT=4' - 0"; NOZZLE_HEIGHT/7*2=1' - 0"; NOZZLE_SIZE=18' - 0"; NOZZLE_TOP_OD=2' - 3 1/2"; NOZZLE_TOP_RAD=1' - 1 3/4"; NOZZLE_WB/4=0' - 8 19/32"; NOZZLE_WB_OD=3' - 7"; NOZZLE_WB_RAD=1' - 9 1/2"; NOZZLE_WB_RAD-2"=1' - 7 1/2"; RO=2' - 2 15/16"; RO/2=1' - 1 15/32"; TRANSITION_TOP=4' - 0 1/2"; TYPE=1' - 0"; Type Comments=Vari-Plume Laboratory Exhaust Mixed-Flow High Pressure Inline Belt Drive With Isolation Box; UNIT_HEIGHT=2' - 11"; UNIT_HEIGHT*.75=2' - 2 1/4"; UNIT_OD=2' - 1 5/8"; UNIT_RADIUS=1' - 0 13/16"; UNIT_RADIUS*.6=0' - 11 17/32"; UNIT_RADIUS+4"=1' - 4 13/16"
- 202_QMXHPVP-12H-Isolation_Box: (A/2)+.25"=1' - 7 1/4"; (NOZZLE_HEIGHT-(NOZZLE_HEIGHT/8*2))/2=1' - 0"; (NOZZLE_WB_OD-NOZZLE_TOP_OD)/2=0' - 2 1/8"; A=3' - 2"; A/2=1' - 7"; B=8' - 8"; B/2=4' - 4"; C=4' - 2"; C/2=2' - 1"; E=3' - 0 15/16"; GA=0' - 0 3/32"; Model=QMXHPVP-Isolation Box; NOZZLE_BOTTOM_ID=1' - 5 1/16"; NOZZLE_BOTTOM_RAD=0' - 8 17/32"; NOZZLE_HEIGHT=2' - 8"; NOZZLE_HEIGHT/7*2=0' - 8"; NOZZLE_SIZE=12' - 0"; NOZZLE_TOP_OD=1' - 7 1/2"; NOZZLE_TOP_RAD=0' - 9 3/4"; NOZZLE_WB/4=0' - 5 19/32"; NOZZLE_WB_OD=2' - 4"; NOZZLE_WB_RAD=1' - 2"; NOZZLE_WB_RAD-2"=1' - 0"; RO=2' - 6 3/4"; RO/2=1' - 3 3/8"; TRANSITION_TOP=5' - 7 9/16"; TYPE=1' - 0"; Type Comments=Vari-Plume Laboratory Exhaust Mixed-Flow High Pressure Inline Belt Drive With Isolation Box; UNIT_HEIGHT=3' - 1 1/2"; UNIT_HEIGHT*.75=2' - 4 1/8"; UNIT_OD=2' - 4 3/4"; UNIT_RADIUS=1' - 2 3/8"; UNIT_RADIUS*.6=1' - 0 15/16"; UNIT_RADIUS+4"=1' - 6 3/8"
- 202_QMXHPVP-12L-Isolation_Box: (A/2)+.25"=1' - 7 1/4"; (NOZZLE_HEIGHT-(NOZZLE_HEIGHT/8*2))/2=1' - 0"; (NOZZLE_WB_OD-NOZZLE_TOP_OD)/2=0' - 2 1/8"; A=3' - 2"; A/2=1' - 7"; B=8' - 8"; B/2=4' - 4"; C=4' - 2"; C/2=2' - 1"; E=3' - 0 15/16"; GA=0' - 0 3/32"; Model=QMXHPVP-Isolation Box; NOZZLE_BOTTOM_ID=1' - 5 1/16"; NOZZLE_BOTTOM_RAD=0' - 8 17/32"; NOZZLE_HEIGHT=2' - 8"; NOZZLE_HEIGHT/7*2=0' - 8"; NOZZLE_SIZE=12' - 0"; NOZZLE_TOP_OD=1' - 7 1/2"; NOZZLE_TOP_RAD=0' - 9 3/4"; NOZZLE_WB/4=0' - 5 19/32"; NOZZLE_WB_OD=2' - 4"; NOZZLE_WB_RAD=1' - 2"; NOZZLE_WB_RAD-2"=1' - 0"; RO=2' - 6 3/4"; RO/2=1' - 3 3/8"; TRANSITION_TOP=5' - 7 9/16"; TYPE=1' - 0"; Type Comments=Vari-Plume Laboratory Exhaust Mixed-Flow High Pressure Inline Belt Drive With Isolation Box; UNIT_HEIGHT=3' - 1 1/2"; UNIT_HEIGHT*.75=2' - 4 1/8"; UNIT_OD=2' - 4 3/4"; UNIT_RADIUS=1' - 2 3/8"; UNIT_RADIUS*.6=1' - 0 15/16"; UNIT_RADIUS+4"=1' - 6 3/8"
- 202_QMXHPVP-15H-Isolation_Box: (A/2)+.25"=1' - 7 1/4"; (NOZZLE_HEIGHT-(NOZZLE_HEIGHT/8*2))/2=1' - 4 1/8"; (NOZZLE_WB_OD-NOZZLE_TOP_OD)/2=0' - 3 1/4"; A=3' - 2"; A/2=1' - 7"; B=8' - 8"; B/2=4' - 4"; C=4' - 2"; C/2=2' - 1"; E=3' - 0 15/16"; GA=0' - 0 3/32"; Model=QMXHPVP-Isolation Box; NOZZLE_BOTTOM_ID=1' - 9 3/8"; NOZZLE_BOTTOM_RAD=0' - 10 11/16"; NOZZLE_HEIGHT=3' - 7"; NOZZLE_HEIGHT/7*2=0' - 10 3/4"; NOZZLE_SIZE=15' - 0"; NOZZLE_TOP_OD=1' - 11"; NOZZLE_TOP_RAD=0' - 11 1/2"; NOZZLE_WB/4=0' - 7 3/16"; NOZZLE_WB_OD=3' - 0"; NOZZLE_WB_RAD=1' - 6"; NOZZLE_WB_RAD-2"=1' - 4"; RO=2' - 6 3/4"; RO/2=1' - 3 3/8"; TRANSITION_TOP=4' - 11 5/8"; TYPE=1' - 0"; Type Comments=Vari-Plume Laboratory Exhaust Mixed-Flow High Pressure Inline Belt Drive With Isolation Box; UNIT_HEIGHT=3' - 1 1/2"; UNIT_HEIGHT*.75=2' - 4 1/8"; UNIT_OD=2' - 4 3/4"; UNIT_RADIUS=1' - 2 3/8"; UNIT_RADIUS*.6=1' - 0 15/16"; UNIT_RADIUS+4"=1' - 6 3/8"
- 202_QMXHPVP-15L-Isolation_Box: (A/2)+.25"=1' - 7 1/4"; (NOZZLE_HEIGHT-(NOZZLE_HEIGHT/8*2))/2=1' - 4 1/8"; (NOZZLE_WB_OD-NOZZLE_TOP_OD)/2=0' - 3 1/4"; A=3' - 2"; A/2=1' - 7"; B=8' - 8"; B/2=4' - 4"; C=4' - 2"; C/2=2' - 1"; E=3' - 0 15/16"; GA=0' - 0 3/32"; Model=QMXHPVP-Isolation Box; NOZZLE_BOTTOM_ID=1' - 9 3/8"; NOZZLE_BOTTOM_RAD=0' - 10 11/16"; NOZZLE_HEIGHT=3' - 7"; NOZZLE_HEIGHT/7*2=0' - 10 3/4"; NOZZLE_SIZE=15' - 0"; NOZZLE_TOP_OD=1' - 11"; NOZZLE_TOP_RAD=0' - 11 1/2"; NOZZLE_WB/4=0' - 7 3/16"; NOZZLE_WB_OD=3' - 0"; NOZZLE_WB_RAD=1' - 6"; NOZZLE_WB_RAD-2"=1' - 4"; RO=2' - 6 3/4"; RO/2=1' - 3 3/8"; TRANSITION_TOP=4' - 11 5/8"; TYPE=1' - 0"; Type Comments=Vari-Plume Laboratory Exhaust Mixed-Flow High Pressure Inline Belt Drive With Isolation Box; UNIT_HEIGHT=3' - 1 1/2"; UNIT_HEIGHT*.75=2' - 4 1/8"; UNIT_OD=2' - 4 3/4"; UNIT_RADIUS=1' - 2 3/8"; UNIT_RADIUS*.6=1' - 0 15/16"; UNIT_RADIUS+4"=1' - 6 3/8"
- 202_QMXHPVP-18H-Isolation_Box: (A/2)+.25"=1' - 7 1/4"; (NOZZLE_HEIGHT-(NOZZLE_HEIGHT/8*2))/2=1' - 6"; (NOZZLE_WB_OD-NOZZLE_TOP_OD)/2=0' - 3 7/8"; A=3' - 2"; A/2=1' - 7"; B=8' - 8"; B/2=4' - 4"; C=4' - 2"; C/2=2' - 1"; E=3' - 0 15/16"; GA=0' - 0 3/32"; Model=QMXHPVP-Isolation Box; NOZZLE_BOTTOM_ID=2' - 1 5/8"; NOZZLE_BOTTOM_RAD=1' - 0 13/16"; NOZZLE_HEIGHT=4' - 0"; NOZZLE_HEIGHT/7*2=1' - 0"; NOZZLE_SIZE=18' - 0"; NOZZLE_TOP_OD=2' - 3 1/2"; NOZZLE_TOP_RAD=1' - 1 3/4"; NOZZLE_WB/4=0' - 8 19/32"; NOZZLE_WB_OD=3' - 7"; NOZZLE_WB_RAD=1' - 9 1/2"; NOZZLE_WB_RAD-2"=1' - 7 1/2"; RO=2' - 6 3/4"; RO/2=1' - 3 3/8"; TRANSITION_TOP=4' - 3 5/8"; TYPE=1' - 0"; Type Comments=Vari-Plume Laboratory Exhaust Mixed-Flow High Pressure Inline Belt Drive With Isolation Box; UNIT_HEIGHT=3' - 1 1/2"; UNIT_HEIGHT*.75=2' - 4 1/8"; UNIT_OD=2' - 4 3/4"; UNIT_RADIUS=1' - 2 3/8"; UNIT_RADIUS*.6=1' - 0 15/16"; UNIT_RADIUS+4"=1' - 6 3/8"
- 202_QMXHPVP-18L-Isolation_Box: (A/2)+.25"=1' - 7 1/4"; (NOZZLE_HEIGHT-(NOZZLE_HEIGHT/8*2))/2=1' - 6"; (NOZZLE_WB_OD-NOZZLE_TOP_OD)/2=0' - 3 7/8"; A=3' - 2"; A/2=1' - 7"; B=8' - 8"; B/2=4' - 4"; C=4' - 2"; C/2=2' - 1"; E=3' - 0 15/16"; GA=0' - 0 3/32"; Model=QMXHPVP-Isolation Box; NOZZLE_BOTTOM_ID=2' - 1 5/8"; NOZZLE_BOTTOM_RAD=1' - 0 13/16"; NOZZLE_HEIGHT=4' - 0"; NOZZLE_HEIGHT/7*2=1' - 0"; NOZZLE_SIZE=18' - 0"; NOZZLE_TOP_OD=2' - 3 1/2"; NOZZLE_TOP_RAD=1' - 1 3/4"; NOZZLE_WB/4=0' - 8 19/32"; NOZZLE_WB_OD=3' - 7"; NOZZLE_WB_RAD=1' - 9 1/2"; NOZZLE_WB_RAD-2"=1' - 7 1/2"; RO=2' - 6 3/4"; RO/2=1' - 3 3/8"; TRANSITION_TOP=4' - 3 5/8"; TYPE=1' - 0"; Type Comments=Vari-Plume Laboratory Exhaust Mixed-Flow High Pressure Inline Belt Drive With Isolation Box; UNIT_HEIGHT=3' - 1 1/2"; UNIT_HEIGHT*.75=2' - 4 1/8"; UNIT_OD=2' - 4 3/4"; UNIT_RADIUS=1' - 2 3/8"; UNIT_RADIUS*.6=1' - 0 15/16"; UNIT_RADIUS+4"=1' - 6 3/8"
- 225_QMXHPVP-12H-Isolation_Box: (A/2)+.25"=1' - 9 1/4"; (NOZZLE_HEIGHT-(NOZZLE_HEIGHT/8*2))/2=1' - 0"; (NOZZLE_WB_OD-NOZZLE_TOP_OD)/2=0' - 2 1/8"; A=3' - 6"; A/2=1' - 9"; B=9' - 5"; B/2=4' - 8 1/2"; C=4' - 8"; C/2=2' - 4"; E=3' - 4 15/16"; GA=0' - 0 3/32"; Model=QMXHPVP-Isolation Box; NOZZLE_BOTTOM_ID=1' - 5 1/16"; NOZZLE_BOTTOM_RAD=0' - 8 17/32"; NOZZLE_HEIGHT=2' - 8"; NOZZLE_HEIGHT/7*2=0' - 8"; NOZZLE_SIZE=12' - 0"; NOZZLE_TOP_OD=1' - 7 1/2"; NOZZLE_TOP_RAD=0' - 9 3/4"; NOZZLE_WB/4=0' - 5 19/32"; NOZZLE_WB_OD=2' - 4"; NOZZLE_WB_RAD=1' - 2"; NOZZLE_WB_RAD-2"=1' - 0"; RO=2' - 10 3/4"; RO/2=1' - 5 3/8"; TRANSITION_TOP=6' - 5 1/16"; TYPE=1' - 0"; Type Comments=Vari-Plume Laboratory Exhaust Mixed-Flow High Pressure Inline Belt Drive With Isolation Box; UNIT_HEIGHT=3' - 5"; UNIT_HEIGHT*.75=2' - 6 3/4"; UNIT_OD=2' - 7 15/16"; UNIT_RADIUS=1' - 3 31/32"; UNIT_RADIUS*.6=1' - 2 3/8"; UNIT_RADIUS+4"=1' - 7 31/32"
- 225_QMXHPVP-12L-Isolation_Box: (A/2)+.25"=1' - 9 1/4"; (NOZZLE_HEIGHT-(NOZZLE_HEIGHT/8*2))/2=1' - 0"; (NOZZLE_WB_OD-NOZZLE_TOP_OD)/2=0' - 2 1/8"; A=3' - 6"; A/2=1' - 9"; B=9' - 5"; B/2=4' - 8 1/2"; C=4' - 8"; C/2=2' - 4"; E=3' - 4 15/16"; GA=0' - 0 3/32"; Model=QMXHPVP-Isolation Box; NOZZLE_BOTTOM_ID=1' - 5 1/16"; NOZZLE_BOTTOM_RAD=0' - 8 17/32"; NOZZLE_HEIGHT=2' - 8"; NOZZLE_HEIGHT/7*2=0' - 8"; NOZZLE_SIZE=12' - 0"; NOZZLE_TOP_OD=1' - 7 1/2"; NOZZLE_TOP_RAD=0' - 9 3/4"; NOZZLE_WB/4=0' - 5 19/32"; NOZZLE_WB_OD=2' - 4"; NOZZLE_WB_RAD=1' - 2"; NOZZLE_WB_RAD-2"=1' - 0"; RO=2' - 10 3/4"; RO/2=1' - 5 3/8"; TRANSITION_TOP=6' - 5 1/16"; TYPE=1' - 0"; Type Comments=Vari-Plume Laboratory Exhaust Mixed-Flow High Pressure Inline Belt Drive With Isolation Box; UNIT_HEIGHT=3' - 5"; UNIT_HEIGHT*.75=2' - 6 3/4"; UNIT_OD=2' - 7 15/16"; UNIT_RADIUS=1' - 3 31/32"; UNIT_RADIUS*.6=1' - 2 3/8"; UNIT_RADIUS+4"=1' - 7 31/32"
- 225_QMXHPVP-15H-Isolation_Box: (A/2)+.25"=1' - 9 1/4"; (NOZZLE_HEIGHT-(NOZZLE_HEIGHT/8*2))/2=1' - 4 1/8"; (NOZZLE_WB_OD-NOZZLE_TOP_OD)/2=0' - 3 1/4"; A=3' - 6"; A/2=1' - 9"; B=9' - 5"; B/2=4' - 8 1/2"; C=4' - 8"; C/2=2' - 4"; E=3' - 4 15/16"; GA=0' - 0 3/32"; Model=QMXHPVP-Isolation Box; NOZZLE_BOTTOM_ID=1' - 9 3/8"; NOZZLE_BOTTOM_RAD=0' - 10 11/16"; NOZZLE_HEIGHT=3' - 7"; NOZZLE_HEIGHT/7*2=0' - 10 3/4"; NOZZLE_SIZE=15' - 0"; NOZZLE_TOP_OD=1' - 11"; NOZZLE_TOP_RAD=0' - 11 1/2"; NOZZLE_WB/4=0' - 7 3/16"; NOZZLE_WB_OD=3' - 0"; NOZZLE_WB_RAD=1' - 6"; NOZZLE_WB_RAD-2"=1' - 4"; RO=2' - 10 3/4"; RO/2=1' - 5 3/8"; TRANSITION_TOP=5' - 9 1/8"; TYPE=1' - 0"; Type Comments=Vari-Plume Laboratory Exhaust Mixed-Flow High Pressure Inline Belt Drive With Isolation Box; UNIT_HEIGHT=3' - 5"; UNIT_HEIGHT*.75=2' - 6 3/4"; UNIT_OD=2' - 7 15/16"; UNIT_RADIUS=1' - 3 31/32"; UNIT_RADIUS*.6=1' - 2 3/8"; UNIT_RADIUS+4"=1' - 7 31/32"
- 225_QMXHPVP-15L-Isolation_Box: (A/2)+.25"=1' - 9 1/4"; (NOZZLE_HEIGHT-(NOZZLE_HEIGHT/8*2))/2=1' - 4 1/8"; (NOZZLE_WB_OD-NOZZLE_TOP_OD)/2=0' - 3 1/4"; A=3' - 6"; A/2=1' - 9"; B=9' - 5"; B/2=4' - 8 1/2"; C=4' - 8"; C/2=2' - 4"; E=3' - 4 15/16"; GA=0' - 0 3/32"; Model=QMXHPVP-Isolation Box; NOZZLE_BOTTOM_ID=1' - 9 3/8"; NOZZLE_BOTTOM_RAD=0' - 10 11/16"; NOZZLE_HEIGHT=3' - 7"; NOZZLE_HEIGHT/7*2=0' - 10 3/4"; NOZZLE_SIZE=15' - 0"; NOZZLE_TOP_OD=1' - 11"; NOZZLE_TOP_RAD=0' - 11 1/2"; NOZZLE_WB/4=0' - 7 3/16"; NOZZLE_WB_OD=3' - 0"; NOZZLE_WB_RAD=1' - 6"; NOZZLE_WB_RAD-2"=1' - 4"; RO=2' - 10 3/4"; RO/2=1' - 5 3/8"; TRANSITION_TOP=5' - 9 1/8"; TYPE=1' - 0"; Type Comments=Vari-Plume Laboratory Exhaust Mixed-Flow High Pressure Inline Belt Drive With Isolation Box; UNIT_HEIGHT=3' - 5"; UNIT_HEIGHT*.75=2' - 6 3/4"; UNIT_OD=2' - 7 15/16"; UNIT_RADIUS=1' - 3 31/32"; UNIT_RADIUS*.6=1' - 2 3/8"; UNIT_RADIUS+4"=1' - 7 31/32"
- 225_QMXVP-18H-Isolation_Box: (A/2)+.25"=1' - 9 1/4"; (NOZZLE_HEIGHT-(NOZZLE_HEIGHT/8*2))/2=1' - 6"; (NOZZLE_WB_OD-NOZZLE_TOP_OD)/2=0' - 3 7/8"; A=3' - 6"; A/2=1' - 9"; B=9' - 5"; B/2=4' - 8 1/2"; C=4' - 8"; C/2=2' - 4"; E=3' - 4 15/16"; GA=0' - 0 3/32"; Model=QMXVP-Isolation Box; NOZZLE_BOTTOM_ID=2' - 1 5/8"; NOZZLE_BOTTOM_RAD=1' - 0 13/16"; NOZZLE_HEIGHT=4' - 0"; NOZZLE_HEIGHT/7*2=1' - 0"; NOZZLE_SIZE=18' - 0"; NOZZLE_TOP_OD=2' - 3 1/2"; NOZZLE_TOP_RAD=1' - 1 3/4"; NOZZLE_WB/4=0' - 8 19/32"; NOZZLE_WB_OD=3' - 7"; NOZZLE_WB_RAD=1' - 9 1/2"; NOZZLE_WB_RAD-2"=1' - 7 1/2"; RO=2' - 10 3/4"; RO/2=1' - 5 3/8"; TRANSITION_TOP=5' - 1 1/8"; TYPE=0' - 0"; Type Comments=Vari-Plume Laboratory Exhaust Mixed-Flow Inline Belt Drive With Isolation Box; UNIT_HEIGHT=3' - 5"; UNIT_HEIGHT*.75=2' - 6 3/4"; UNIT_OD=2' - 7 15/16"; UNIT_RADIUS=1' - 3 31/32"; UNIT_RADIUS*.6=1' - 2 3/8"; UNIT_RADIUS+4"=1' - 7 31/32"
- 225_QMXHPVP-18L-Isolation_Box: (A/2)+.25"=1' - 9 1/4"; (NOZZLE_HEIGHT-(NOZZLE_HEIGHT/8*2))/2=1' - 6"; (NOZZLE_WB_OD-NOZZLE_TOP_OD)/2=0' - 3 7/8"; A=3' - 6"; A/2=1' - 9"; B=9' - 5"; B/2=4' - 8 1/2"; C=4' - 8"; C/2=2' - 4"; E=3' - 4 15/16"; GA=0' - 0 3/32"; Model=QMXHPVP-Isolation Box; NOZZLE_BOTTOM_ID=2' - 1 5/8"; NOZZLE_BOTTOM_RAD=1' - 0 13/16"; NOZZLE_HEIGHT=4' - 0"; NOZZLE_HEIGHT/7*2=1' - 0"; NOZZLE_SIZE=18' - 0"; NOZZLE_TOP_OD=2' - 3 1/2"; NOZZLE_TOP_RAD=1' - 1 3/4"; NOZZLE_WB/4=0' - 8 19/32"; NOZZLE_WB_OD=3' - 7"; NOZZLE_WB_RAD=1' - 9 1/2"; NOZZLE_WB_RAD-2"=1' - 7 1/2"; RO=2' - 10 3/4"; RO/2=1' - 5 3/8"; TRANSITION_TOP=5' - 1 1/8"; TYPE=1' - 0"; Type Comments=Vari-Plume Laboratory Exhaust Mixed-Flow High Pressure Inline Belt Drive With Isolation Box; UNIT_HEIGHT=3' - 5"; UNIT_HEIGHT*.75=2' - 6 3/4"; UNIT_OD=2' - 7 15/16"; UNIT_RADIUS=1' - 3 31/32"; UNIT_RADIUS*.6=1' - 2 3/8"; UNIT_RADIUS+4"=1' - 7 31/32"
- 225_QMXHPVP-18H-Isolation_Box: (A/2)+.25"=1' - 9 1/4"; (NOZZLE_HEIGHT-(NOZZLE_HEIGHT/8*2))/2=1' - 6"; (NOZZLE_WB_OD-NOZZLE_TOP_OD)/2=0' - 3 7/8"; A=3' - 6"; A/2=1' - 9"; B=9' - 5"; B/2=4' - 8 1/2"; C=4' - 8"; C/2=2' - 4"; E=3' - 4 15/16"; GA=0' - 0 3/32"; Model=QMXHPVP-Isolation Box; NOZZLE_BOTTOM_ID=2' - 1 5/8"; NOZZLE_BOTTOM_RAD=1' - 0 13/16"; NOZZLE_HEIGHT=4' - 0"; NOZZLE_HEIGHT/7*2=1' - 0"; NOZZLE_SIZE=18' - 0"; NOZZLE_TOP_OD=2' - 3 1/2"; NOZZLE_TOP_RAD=1' - 1 3/4"; NOZZLE_WB/4=0' - 8 19/32"; NOZZLE_WB_OD=3' - 7"; NOZZLE_WB_RAD=1' - 9 1/2"; NOZZLE_WB_RAD-2"=1' - 7 1/2"; RO=2' - 10 3/4"; RO/2=1' - 5 3/8"; TRANSITION_TOP=5' - 1 1/8"; TYPE=1' - 0"; Type Comments=Vari-Plume Laboratory Exhaust Mixed-Flow High Pressure Inline Belt Drive With Isolation Box; UNIT_HEIGHT=3' - 5"; UNIT_HEIGHT*.75=2' - 6 3/4"; UNIT_OD=2' - 7 15/16"; UNIT_RADIUS=1' - 3 31/32"; UNIT_RADIUS*.6=1' - 2 3/8"; UNIT_RADIUS+4"=1' - 7 31/32"
- 245_QMXHPVP-15H-Isolation_Box: (A/2)+.25"=1' - 10 1/4"; (NOZZLE_HEIGHT-(NOZZLE_HEIGHT/8*2))/2=1' - 4 1/8"; (NOZZLE_WB_OD-NOZZLE_TOP_OD)/2=0' - 3 1/4"; A=3' - 8"; A/2=1' - 10"; B=10' - 1"; B/2=5' - 0 1/2"; C=4' - 11"; C/2=2' - 5 1/2"; E=3' - 6 15/16"; GA=0' - 0 3/32"; Model=QMXHPVP-Isolation Box; NOZZLE_BOTTOM_ID=1' - 9 3/8"; NOZZLE_BOTTOM_RAD=0' - 10 11/16"; NOZZLE_HEIGHT=3' - 7"; NOZZLE_HEIGHT/7*2=0' - 10 3/4"; NOZZLE_SIZE=15' - 0"; NOZZLE_TOP_OD=1' - 11"; NOZZLE_TOP_RAD=0' - 11 1/2"; NOZZLE_WB/4=0' - 7 3/16"; NOZZLE_WB_OD=3' - 0"; NOZZLE_WB_RAD=1' - 6"; NOZZLE_WB_RAD-2"=1' - 4"; RO=3' - 0 3/4"; RO/2=1' - 6 3/8"; TRANSITION_TOP=6' - 5 11/16"; TYPE=1' - 0"; Type Comments=Vari-Plume Laboratory Exhaust Mixed-Flow High Pressure Inline Belt Drive With Isolation Box; UNIT_HEIGHT=3' - 8 1/2"; UNIT_HEIGHT*.75=2' - 9 3/8"; UNIT_OD=2' - 10 3/4"; UNIT_RADIUS=1' - 5 3/8"; UNIT_RADIUS*.6=1' - 3 5/8"; UNIT_RADIUS+4"=1' - 9 3/8"
- 245_QMXHPVP-15L-Isolation_Box: (A/2)+.25"=1' - 10 1/4"; (NOZZLE_HEIGHT-(NOZZLE_HEIGHT/8*2))/2=1' - 4 1/8"; (NOZZLE_WB_OD-NOZZLE_TOP_OD)/2=0' - 3 1/4"; A=3' - 8"; A/2=1' - 10"; B=10' - 1"; B/2=5' - 0 1/2"; C=4' - 11"; C/2=2' - 5 1/2"; E=3' - 6 15/16"; GA=0' - 0 3/32"; Model=QMXHPVP-Isolation Box; NOZZLE_BOTTOM_ID=1' - 9 3/8"; NOZZLE_BOTTOM_RAD=0' - 10 11/16"; NOZZLE_HEIGHT=3' - 7"; NOZZLE_HEIGHT/7*2=0' - 10 3/4"; NOZZLE_SIZE=15' - 0"; NOZZLE_TOP_OD=1' - 11"; NOZZLE_TOP_RAD=0' - 11 1/2"; NOZZLE_WB/4=0' - 7 3/16"; NOZZLE_WB_OD=3' - 0"; NOZZLE_WB_RAD=1' - 6"; NOZZLE_WB_RAD-2"=1' - 4"; RO=3' - 0 3/4"; RO/2=1' - 6 3/8"; TRANSITION_TOP=6' - 5 11/16"; TYPE=1' - 0"; Type Comments=Vari-Plume Laboratory Exhaust Mixed-Flow High Pressure Inline Belt Drive With Isolation Box; UNIT_HEIGHT=3' - 8 1/2"; UNIT_HEIGHT*.75=2' - 9 3/8"; UNIT_OD=2' - 10 3/4"; UNIT_RADIUS=1' - 5 3/8"; UNIT_RADIUS*.6=1' - 3 5/8"; UNIT_RADIUS+4"=1' - 9 3/8"
- 245_QMXHPVP-18H-Isolation_Box: (A/2)+.25"=1' - 10 1/4"; (NOZZLE_HEIGHT-(NOZZLE_HEIGHT/8*2))/2=1' - 6"; (NOZZLE_WB_OD-NOZZLE_TOP_OD)/2=0' - 3 7/8"; A=3' - 8"; A/2=1' - 10"; B=10' - 1"; B/2=5' - 0 1/2"; C=4' - 11"; C/2=2' - 5 1/2"; E=3' - 6 15/16"; GA=0' - 0 3/32"; Model=QMXHPVP-Isolation Box; NOZZLE_BOTTOM_ID=2' - 1 5/8"; NOZZLE_BOTTOM_RAD=1' - 0 13/16"; NOZZLE_HEIGHT=4' - 0"; NOZZLE_HEIGHT/7*2=1' - 0"; NOZZLE_SIZE=18' - 0"; NOZZLE_TOP_OD=2' - 3 1/2"; NOZZLE_TOP_RAD=1' - 1 3/4"; NOZZLE_WB/4=0' - 8 19/32"; NOZZLE_WB_OD=3' - 7"; NOZZLE_WB_RAD=1' - 9 1/2"; NOZZLE_WB_RAD-2"=1' - 7 1/2"; RO=3' - 0 3/4"; RO/2=1' - 6 3/8"; TRANSITION_TOP=5' - 9 11/16"; TYPE=1' - 0"; Type Comments=Vari-Plume Laboratory Exhaust Mixed-Flow High Pressure Inline Belt Drive With Isolation Box; UNIT_HEIGHT=3' - 8 1/2"; UNIT_HEIGHT*.75=2' - 9 3/8"; UNIT_OD=2' - 10 3/4"; UNIT_RADIUS=1' - 5 3/8"; UNIT_RADIUS*.6=1' - 3 5/8"; UNIT_RADIUS+4"=1' - 9 3/8"
- 245_QMXHPVP-18L-Isolation_Box: (A/2)+.25"=1' - 10 1/4"; (NOZZLE_HEIGHT-(NOZZLE_HEIGHT/8*2))/2=1' - 6"; (NOZZLE_WB_OD-NOZZLE_TOP_OD)/2=0' - 3 7/8"; A=3' - 8"; A/2=1' - 10"; B=10' - 1"; B/2=5' - 0 1/2"; C=4' - 11"; C/2=2' - 5 1/2"; E=3' - 6 15/16"; GA=0' - 0 3/32"; Model=QMXHPVP-Isolation Box; NOZZLE_BOTTOM_ID=2' - 1 5/8"; NOZZLE_BOTTOM_RAD=1' - 0 13/16"; NOZZLE_HEIGHT=4' - 0"; NOZZLE_HEIGHT/7*2=1' - 0"; NOZZLE_SIZE=18' - 0"; NOZZLE_TOP_OD=2' - 3 1/2"; NOZZLE_TOP_RAD=1' - 1 3/4"; NOZZLE_WB/4=0' - 8 19/32"; NOZZLE_WB_OD=3' - 7"; NOZZLE_WB_RAD=1' - 9 1/2"; NOZZLE_WB_RAD-2"=1' - 7 1/2"; RO=3' - 0 3/4"; RO/2=1' - 6 3/8"; TRANSITION_TOP=5' - 9 11/16"; TYPE=1' - 0"; Type Comments=Vari-Plume Laboratory Exhaust Mixed-Flow High Pressure Inline Belt Drive With Isolation Box; UNIT_HEIGHT=3' - 8 1/2"; UNIT_HEIGHT*.75=2' - 9 3/8"; UNIT_OD=2' - 10 3/4"; UNIT_RADIUS=1' - 5 3/8"; UNIT_RADIUS*.6=1' - 3 5/8"; UNIT_RADIUS+4"=1' - 9 3/8"
- 245_QMXHPVP-24H-Isolation_Box: (A/2)+.25"=1' - 10 1/4"; (NOZZLE_HEIGHT-(NOZZLE_HEIGHT/8*2))/2=1' - 11 1/4"; (NOZZLE_WB_OD-NOZZLE_TOP_OD)/2=0' - 6 1/8"; A=3' - 8"; A/2=1' - 10"; B=10' - 1"; B/2=5' - 0 1/2"; C=4' - 11"; C/2=2' - 5 1/2"; E=3' - 6 15/16"; GA=0' - 0 3/32"; Model=QMXHPVP-Isolation Box; NOZZLE_BOTTOM_ID=2' - 10 3/4"; NOZZLE_BOTTOM_RAD=1' - 5 3/8"; NOZZLE_HEIGHT=5' - 2"; NOZZLE_HEIGHT/7*2=1' - 3 1/2"; NOZZLE_SIZE=24' - 0"; NOZZLE_TOP_OD=3' - 0 1/2"; NOZZLE_TOP_RAD=1' - 6 1/4"; NOZZLE_WB/4=1' - 0 3/16"; NOZZLE_WB_OD=5' - 1"; NOZZLE_WB_RAD=2' - 6 1/2"; NOZZLE_WB_RAD-2"=2' - 4 1/2"; RO=3' - 0 3/4"; RO/2=1' - 6 3/8"; TRANSITION_TOP=4' - 9 3/4"; TYPE=1' - 0"; Type Comments=Vari-Plume Laboratory Exhaust Mixed-Flow High Pressure Inline Belt Drive With Isolation Box; UNIT_HEIGHT=3' - 8 1/2"; UNIT_HEIGHT*.75=2' - 9 3/8"; UNIT_OD=2' - 10 3/4"; UNIT_RADIUS=1' - 5 3/8"; UNIT_RADIUS*.6=1' - 3 5/8"; UNIT_RADIUS+4"=1' - 9 3/8"
- 245_QMXHPVP-24L-Isolation_Box: (A/2)+.25"=1' - 10 1/4"; (NOZZLE_HEIGHT-(NOZZLE_HEIGHT/8*2))/2=1' - 11 1/4"; (NOZZLE_WB_OD-NOZZLE_TOP_OD)/2=0' - 6 1/8"; A=3' - 8"; A/2=1' - 10"; B=10' - 1"; B/2=5' - 0 1/2"; C=4' - 11"; C/2=2' - 5 1/2"; E=3' - 6 15/16"; GA=0' - 0 3/32"; Model=QMXHPVP-Isolation Box; NOZZLE_BOTTOM_ID=2' - 10 3/4"; NOZZLE_BOTTOM_RAD=1' - 5 3/8"; NOZZLE_HEIGHT=5' - 2"; NOZZLE_HEIGHT/7*2=1' - 3 1/2"; NOZZLE_SIZE=24' - 0"; NOZZLE_TOP_OD=3' - 0 1/2"; NOZZLE_TOP_RAD=1' - 6 1/4"; NOZZLE_WB/4=1' - 0 3/16"; NOZZLE_WB_OD=5' - 1"; NOZZLE_WB_RAD=2' - 6 1/2"; NOZZLE_WB_RAD-2"=2' - 4 1/2"; RO=3' - 0 3/4"; RO/2=1' - 6 3/8"; TRANSITION_TOP=4' - 9 3/4"; TYPE=1' - 0"; Type Comments=Vari-Plume Laboratory Exhaust Mixed-Flow High Pressure Inline Belt Drive With Isolation Box; UNIT_HEIGHT=3' - 8 1/2"; UNIT_HEIGHT*.75=2' - 9 3/8"; UNIT_OD=2' - 10 3/4"; UNIT_RADIUS=1' - 5 3/8"; UNIT_RADIUS*.6=1' - 3 5/8"; UNIT_RADIUS+4"=1' - 9 3/8"
- 270_QMXHPVP-15H-Isolation_Box: (A/2)+.25"=2' - 0 1/4"; (NOZZLE_HEIGHT-(NOZZLE_HEIGHT/8*2))/2=1' - 4 1/8"; (NOZZLE_WB_OD-NOZZLE_TOP_OD)/2=0' - 3 1/4"; A=4' - 0"; A/2=2' - 0"; B=10' - 8"; B/2=5' - 4"; C=5' - 3"; C/2=2' - 7 1/2"; E=3' - 10 15/16"; GA=0' - 0 3/32"; Model=QMXHPVP-Isolation Box; NOZZLE_BOTTOM_ID=1' - 9 3/8"; NOZZLE_BOTTOM_RAD=0' - 10 11/16"; NOZZLE_HEIGHT=3' - 7"; NOZZLE_HEIGHT/7*2=0' - 10 3/4"; NOZZLE_SIZE=15' - 0"; NOZZLE_TOP_OD=1' - 11"; NOZZLE_TOP_RAD=0' - 11 1/2"; NOZZLE_WB/4=0' - 7 3/16"; NOZZLE_WB_OD=3' - 0"; NOZZLE_WB_RAD=1' - 6"; NOZZLE_WB_RAD-2"=1' - 4"; RO=3' - 4 3/4"; RO/2=1' - 8 3/8"; TRANSITION_TOP=7' - 2 3/16"; TYPE=1' - 0"; Type Comments=Vari-Plume Laboratory Exhaust Mixed-Flow High Pressure Inline Belt Drive With Isolation Box; UNIT_HEIGHT=3' - 11"; UNIT_HEIGHT*.75=2' - 11 1/4"; UNIT_OD=3' - 2 5/16"; UNIT_RADIUS=1' - 7 5/32"; UNIT_RADIUS*.6=1' - 5 1/4"; UNIT_RADIUS+4"=1' - 11 5/32"
- 270_QMXHPVP-15L-Isolation_Box: (A/2)+.25"=2' - 0 1/4"; (NOZZLE_HEIGHT-(NOZZLE_HEIGHT/8*2))/2=1' - 4 1/8"; (NOZZLE_WB_OD-NOZZLE_TOP_OD)/2=0' - 3 1/4"; A=4' - 0"; A/2=2' - 0"; B=10' - 8"; B/2=5' - 4"; C=5' - 3"; C/2=2' - 7 1/2"; E=3' - 10 15/16"; GA=0' - 0 3/32"; Model=QMXHPVP-Isolation Box; NOZZLE_BOTTOM_ID=1' - 9 3/8"; NOZZLE_BOTTOM_RAD=0' - 10 11/16"; NOZZLE_HEIGHT=3' - 7"; NOZZLE_HEIGHT/7*2=0' - 10 3/4"; NOZZLE_SIZE=15' - 0"; NOZZLE_TOP_OD=1' - 11"; NOZZLE_TOP_RAD=0' - 11 1/2"; NOZZLE_WB/4=0' - 7 3/16"; NOZZLE_WB_OD=3' - 0"; NOZZLE_WB_RAD=1' - 6"; NOZZLE_WB_RAD-2"=1' - 4"; RO=3' - 4 3/4"; RO/2=1' - 8 3/8"; TRANSITION_TOP=7' - 2 3/16"; TYPE=1' - 0"; Type Comments=Vari-Plume Laboratory Exhaust Mixed-Flow High Pressure Inline Belt Drive With Isolation Box; UNIT_HEIGHT=3' - 11"; UNIT_HEIGHT*.75=2' - 11 1/4"; UNIT_OD=3' - 2 5/16"; UNIT_RADIUS=1' - 7 5/32"; UNIT_RADIUS*.6=1' - 5 1/4"; UNIT_RADIUS+4"=1' - 11 5/32"
- 270_QMXHPVP-18H-Isolation_Box: (A/2)+.25"=2' - 0 1/4"; (NOZZLE_HEIGHT-(NOZZLE_HEIGHT/8*2))/2=1' - 6"; (NOZZLE_WB_OD-NOZZLE_TOP_OD)/2=0' - 3 7/8"; A=4' - 0"; A/2=2' - 0"; B=10' - 8"; B/2=5' - 4"; C=5' - 3"; C/2=2' - 7 1/2"; E=3' - 10 15/16"; GA=0' - 0 3/32"; Model=QMXHPVP-Isolation Box; NOZZLE_BOTTOM_ID=2' - 1 5/8"; NOZZLE_BOTTOM_RAD=1' - 0 13/16"; NOZZLE_HEIGHT=4' - 0"; NOZZLE_HEIGHT/7*2=1' - 0"; NOZZLE_SIZE=18' - 0"; NOZZLE_TOP_OD=2' - 3 1/2"; NOZZLE_TOP_RAD=1' - 1 3/4"; NOZZLE_WB/4=0' - 8 19/32"; NOZZLE_WB_OD=3' - 7"; NOZZLE_WB_RAD=1' - 9 1/2"; NOZZLE_WB_RAD-2"=1' - 7 1/2"; RO=3' - 4 3/4"; RO/2=1' - 8 3/8"; TRANSITION_TOP=6' - 7 3/16"; TYPE=1' - 0"; Type Comments=Vari-Plume Laboratory Exhaust Mixed-Flow High Pressure Inline Belt Drive With Isolation Box; UNIT_HEIGHT=3' - 11"; UNIT_HEIGHT*.75=2' - 11 1/4"; UNIT_OD=3' - 2 5/16"; UNIT_RADIUS=1' - 7 5/32"; UNIT_RADIUS*.6=1' - 5 1/4"; UNIT_RADIUS+4"=1' - 11 5/32"
- 270_QMXHPVP-18L-Isolation_Box: (A/2)+.25"=2' - 0 1/4"; (NOZZLE_HEIGHT-(NOZZLE_HEIGHT/8*2))/2=1' - 6"; (NOZZLE_WB_OD-NOZZLE_TOP_OD)/2=0' - 3 7/8"; A=4' - 0"; A/2=2' - 0"; B=10' - 8"; B/2=5' - 4"; C=5' - 3"; C/2=2' - 7 1/2"; E=3' - 10 15/16"; GA=0' - 0 3/32"; Model=QMXHPVP-Isolation Box; NOZZLE_BOTTOM_ID=2' - 1 5/8"; NOZZLE_BOTTOM_RAD=1' - 0 13/16"; NOZZLE_HEIGHT=4' - 0"; NOZZLE_HEIGHT/7*2=1' - 0"; NOZZLE_SIZE=18' - 0"; NOZZLE_TOP_OD=2' - 3 1/2"; NOZZLE_TOP_RAD=1' - 1 3/4"; NOZZLE_WB/4=0' - 8 19/32"; NOZZLE_WB_OD=3' - 7"; NOZZLE_WB_RAD=1' - 9 1/2"; NOZZLE_WB_RAD-2"=1' - 7 1/2"; RO=3' - 4 3/4"; RO/2=1' - 8 3/8"; TRANSITION_TOP=6' - 7 3/16"; TYPE=1' - 0"; Type Comments=Vari-Plume Laboratory Exhaust Mixed-Flow High Pressure Inline Belt Drive With Isolation Box; UNIT_HEIGHT=3' - 11"; UNIT_HEIGHT*.75=2' - 11 1/4"; UNIT_OD=3' - 2 5/16"; UNIT_RADIUS=1' - 7 5/32"; UNIT_RADIUS*.6=1' - 5 1/4"; UNIT_RADIUS+4"=1' - 11 5/32"
- 270_QMXHPVP-24H-Isolation_Box: (A/2)+.25"=2' - 0 1/4"; (NOZZLE_HEIGHT-(NOZZLE_HEIGHT/8*2))/2=1' - 11 1/4"; (NOZZLE_WB_OD-NOZZLE_TOP_OD)/2=0' - 6 1/8"; A=4' - 0"; A/2=2' - 0"; B=10' - 8"; B/2=5' - 4"; C=5' - 3"; C/2=2' - 7 1/2"; E=3' - 10 15/16"; GA=0' - 0 3/32"; Model=QMXHPVP-Isolation Box; NOZZLE_BOTTOM_ID=2' - 10 3/4"; NOZZLE_BOTTOM_RAD=1' - 5 3/8"; NOZZLE_HEIGHT=5' - 2"; NOZZLE_HEIGHT/7*2=1' - 3 1/2"; NOZZLE_SIZE=24' - 0"; NOZZLE_TOP_OD=3' - 0 1/2"; NOZZLE_TOP_RAD=1' - 6 1/4"; NOZZLE_WB/4=1' - 0 3/16"; NOZZLE_WB_OD=5' - 1"; NOZZLE_WB_RAD=2' - 6 1/2"; NOZZLE_WB_RAD-2"=2' - 4 1/2"; RO=3' - 4 3/4"; RO/2=1' - 8 3/8"; TRANSITION_TOP=5' - 2 1/4"; TYPE=1' - 0"; Type Comments=Vari-Plume Laboratory Exhaust Mixed-Flow High Pressure Inline Belt Drive With Isolation Box; UNIT_HEIGHT=3' - 11"; UNIT_HEIGHT*.75=2' - 11 1/4"; UNIT_OD=3' - 2 5/16"; UNIT_RADIUS=1' - 7 5/32"; UNIT_RADIUS*.6=1' - 5 1/4"; UNIT_RADIUS+4"=1' - 11 5/32"
- 270_QMXHPVP-24L-Isolation_Box: (A/2)+.25"=2' - 0 1/4"; (NOZZLE_HEIGHT-(NOZZLE_HEIGHT/8*2))/2=1' - 11 1/4"; (NOZZLE_WB_OD-NOZZLE_TOP_OD)/2=0' - 6 1/8"; A=4' - 0"; A/2=2' - 0"; B=10' - 8"; B/2=5' - 4"; C=5' - 3"; C/2=2' - 7 1/2"; E=3' - 10 15/16"; GA=0' - 0 3/32"; Model=QMXHPVP-Isolation Box; NOZZLE_BOTTOM_ID=2' - 10 3/4"; NOZZLE_BOTTOM_RAD=1' - 5 3/8"; NOZZLE_HEIGHT=5' - 2"; NOZZLE_HEIGHT/7*2=1' - 3 1/2"; NOZZLE_SIZE=24' - 0"; NOZZLE_TOP_OD=3' - 0 1/2"; NOZZLE_TOP_RAD=1' - 6 1/4"; NOZZLE_WB/4=1' - 0 3/16"; NOZZLE_WB_OD=5' - 1"; NOZZLE_WB_RAD=2' - 6 1/2"; NOZZLE_WB_RAD-2"=2' - 4 1/2"; RO=3' - 4 3/4"; RO/2=1' - 8 3/8"; TRANSITION_TOP=5' - 2 1/4"; TYPE=1' - 0"; Type Comments=Vari-Plume Laboratory Exhaust Mixed-Flow High Pressure Inline Belt Drive With Isolation Box; UNIT_HEIGHT=3' - 11"; UNIT_HEIGHT*.75=2' - 11 1/4"; UNIT_OD=3' - 2 5/16"; UNIT_RADIUS=1' - 7 5/32"; UNIT_RADIUS*.6=1' - 5 1/4"; UNIT_RADIUS+4"=1' - 11 5/32"
- 300_QMXHPVP-18H-Isolation_Box: (A/2)+.25"=2' - 2 1/4"; (NOZZLE_HEIGHT-(NOZZLE_HEIGHT/8*2))/2=1' - 6"; (NOZZLE_WB_OD-NOZZLE_TOP_OD)/2=0' - 3 7/8"; A=4' - 4"; A/2=2' - 2"; B=12' - 4"; B/2=6' - 2"; C=5' - 7"; C/2=2' - 9 1/2"; E=4' - 2 15/16"; GA=0' - 0 3/32"; Model=QMXHPVP-Isolation Box; NOZZLE_BOTTOM_ID=2' - 1 5/8"; NOZZLE_BOTTOM_RAD=1' - 0 13/16"; NOZZLE_HEIGHT=4' - 0"; NOZZLE_HEIGHT/7*2=1' - 0"; NOZZLE_SIZE=18' - 0"; NOZZLE_TOP_OD=2' - 3 1/2"; NOZZLE_TOP_RAD=1' - 1 3/4"; NOZZLE_WB/4=0' - 8 19/32"; NOZZLE_WB_OD=3' - 7"; NOZZLE_WB_RAD=1' - 9 1/2"; NOZZLE_WB_RAD-2"=1' - 7 1/2"; RO=3' - 8 3/4"; RO/2=1' - 10 3/8"; TRANSITION_TOP=7' - 10 3/16"; TYPE=1' - 0"; Type Comments=Vari-Plume Laboratory Exhaust Mixed-Flow High Pressure Inline Belt Drive With Isolation Box; UNIT_HEIGHT=4' - 6"; UNIT_HEIGHT*.75=3' - 4 1/2"; UNIT_OD=3' - 6 1/2"; UNIT_RADIUS=1' - 9 1/4"; UNIT_RADIUS*.6=1' - 7 1/8"; UNIT_RADIUS+4"=2' - 1 1/4"
- 300_QMXHPVP-18L-Isolation_Box: (A/2)+.25"=2' - 2 1/4"; (NOZZLE_HEIGHT-(NOZZLE_HEIGHT/8*2))/2=1' - 6"; (NOZZLE_WB_OD-NOZZLE_TOP_OD)/2=0' - 3 7/8"; A=4' - 4"; A/2=2' - 2"; B=12' - 4"; B/2=6' - 2"; C=5' - 7"; C/2=2' - 9 1/2"; E=4' - 2 15/16"; GA=0' - 0 3/32"; Model=QMXHPVP-Isolation Box; NOZZLE_BOTTOM_ID=2' - 1 5/8"; NOZZLE_BOTTOM_RAD=1' - 0 13/16"; NOZZLE_HEIGHT=4' - 0"; NOZZLE_HEIGHT/7*2=1' - 0"; NOZZLE_SIZE=18' - 0"; NOZZLE_TOP_OD=2' - 3 1/2"; NOZZLE_TOP_RAD=1' - 1 3/4"; NOZZLE_WB/4=0' - 8 19/32"; NOZZLE_WB_OD=3' - 7"; NOZZLE_WB_RAD=1' - 9 1/2"; NOZZLE_WB_RAD-2"=1' - 7 1/2"; RO=3' - 8 3/4"; RO/2=1' - 10 3/8"; TRANSITION_TOP=7' - 10 3/16"; TYPE=1' - 0"; Type Comments=Vari-Plume Laboratory Exhaust Mixed-Flow High Pressure Inline Belt Drive With Isolation Box; UNIT_HEIGHT=4' - 6"; UNIT_HEIGHT*.75=3' - 4 1/2"; UNIT_OD=3' - 6 1/2"; UNIT_RADIUS=1' - 9 1/4"; UNIT_RADIUS*.6=1' - 7 1/8"; UNIT_RADIUS+4"=2' - 1 1/4"
- 300_QMXHPVP-24H-Isolation_Box: (A/2)+.25"=2' - 2 1/4"; (NOZZLE_HEIGHT-(NOZZLE_HEIGHT/8*2))/2=1' - 11 1/4"; (NOZZLE_WB_OD-NOZZLE_TOP_OD)/2=0' - 6 1/8"; A=4' - 4"; A/2=2' - 2"; B=12' - 4"; B/2=6' - 2"; C=5' - 7"; C/2=2' - 9 1/2"; E=4' - 2 15/16"; GA=0' - 0 3/32"; Model=QMXHPVP-Isolation Box; NOZZLE_BOTTOM_ID=2' - 10 3/4"; NOZZLE_BOTTOM_RAD=1' - 5 3/8"; NOZZLE_HEIGHT=5' - 2"; NOZZLE_HEIGHT/7*2=1' - 3 1/2"; NOZZLE_SIZE=24' - 0"; NOZZLE_TOP_OD=3' - 0 1/2"; NOZZLE_TOP_RAD=1' - 6 1/4"; NOZZLE_WB/4=1' - 0 3/16"; NOZZLE_WB_OD=5' - 1"; NOZZLE_WB_RAD=2' - 6 1/2"; NOZZLE_WB_RAD-2"=2' - 4 1/2"; RO=3' - 8 3/4"; RO/2=1' - 10 3/8"; TRANSITION_TOP=6' - 5 1/4"; TYPE=1' - 0"; Type Comments=Vari-Plume Laboratory Exhaust Mixed-Flow High Pressure Inline Belt Drive With Isolation Box; UNIT_HEIGHT=4' - 6"; UNIT_HEIGHT*.75=3' - 4 1/2"; UNIT_OD=3' - 6 1/2"; UNIT_RADIUS=1' - 9 1/4"; UNIT_RADIUS*.6=1' - 7 1/8"; UNIT_RADIUS+4"=2' - 1 1/4"
- 300_QMXHPVP-24L-Isolation_Box: (A/2)+.25"=2' - 2 1/4"; (NOZZLE_HEIGHT-(NOZZLE_HEIGHT/8*2))/2=1' - 11 1/4"; (NOZZLE_WB_OD-NOZZLE_TOP_OD)/2=0' - 6 1/8"; A=4' - 4"; A/2=2' - 2"; B=12' - 4"; B/2=6' - 2"; C=5' - 7"; C/2=2' - 9 1/2"; E=4' - 2 15/16"; GA=0' - 0 3/32"; Model=QMXHPVP-Isolation Box; NOZZLE_BOTTOM_ID=2' - 10 3/4"; NOZZLE_BOTTOM_RAD=1' - 5 3/8"; NOZZLE_HEIGHT=5' - 2"; NOZZLE_HEIGHT/7*2=1' - 3 1/2"; NOZZLE_SIZE=24' - 0"; NOZZLE_TOP_OD=3' - 0 1/2"; NOZZLE_TOP_RAD=1' - 6 1/4"; NOZZLE_WB/4=1' - 0 3/16"; NOZZLE_WB_OD=5' - 1"; NOZZLE_WB_RAD=2' - 6 1/2"; NOZZLE_WB_RAD-2"=2' - 4 1/2"; RO=3' - 8 3/4"; RO/2=1' - 10 3/8"; TRANSITION_TOP=6' - 5 1/4"; TYPE=1' - 0"; Type Comments=Vari-Plume Laboratory Exhaust Mixed-Flow High Pressure Inline Belt Drive With Isolation Box; UNIT_HEIGHT=4' - 6"; UNIT_HEIGHT*.75=3' - 4 1/2"; UNIT_OD=3' - 6 1/2"; UNIT_RADIUS=1' - 9 1/4"; UNIT_RADIUS*.6=1' - 7 1/8"; UNIT_RADIUS+4"=2' - 1 1/4"
- 300_QMXHPVP-30H-Isolation_Box: (A/2)+.25"=2' - 2 1/4"; (NOZZLE_HEIGHT-(NOZZLE_HEIGHT/8*2))/2=2' - 5 1/4"; (NOZZLE_WB_OD-NOZZLE_TOP_OD)/2=0' - 7 1/8"; A=4' - 4"; A/2=2' - 2"; B=12' - 4"; B/2=6' - 2"; C=5' - 7"; C/2=2' - 9 1/2"; E=4' - 2 15/16"; GA=0' - 0 3/32"; Model=QMXHPVP-Isolation Box; NOZZLE_BOTTOM_ID=3' - 6 1/2"; NOZZLE_BOTTOM_RAD=1' - 9 1/4"; NOZZLE_HEIGHT=6' - 6"; NOZZLE_HEIGHT/7*2=1' - 7 1/2"; NOZZLE_SIZE=30' - 0"; NOZZLE_TOP_OD=3' - 9 1/2"; NOZZLE_TOP_RAD=1' - 10 3/4"; NOZZLE_WB/4=1' - 2 13/16"; NOZZLE_WB_OD=6' - 2"; NOZZLE_WB_RAD=3' - 1"; NOZZLE_WB_RAD-2"=2' - 11"; RO=3' - 8 3/4"; RO/2=1' - 10 3/8"; TRANSITION_TOP=5' - 8 1/4"; TYPE=1' - 0"; Type Comments=Vari-Plume Laboratory Exhaust Mixed-Flow High Pressure Inline Belt Drive With Isolation Box; UNIT_HEIGHT=4' - 6"; UNIT_HEIGHT*.75=3' - 4 1/2"; UNIT_OD=3' - 6 1/2"; UNIT_RADIUS=1' - 9 1/4"; UNIT_RADIUS*.6=1' - 7 1/8"; UNIT_RADIUS+4"=2' - 1 1/4"
- 300_QMXHPVP-30L-Isolation_Box: (A/2)+.25"=2' - 2 1/4"; (NOZZLE_HEIGHT-(NOZZLE_HEIGHT/8*2))/2=2' - 5 1/4"; (NOZZLE_WB_OD-NOZZLE_TOP_OD)/2=0' - 7 1/8"; A=4' - 4"; A/2=2' - 2"; B=12' - 4"; B/2=6' - 2"; C=5' - 7"; C/2=2' - 9 1/2"; E=4' - 2 15/16"; GA=0' - 0 3/32"; Model=QMXHPVP-Isolation Box; NOZZLE_BOTTOM_ID=3' - 6 1/2"; NOZZLE_BOTTOM_RAD=1' - 9 1/4"; NOZZLE_HEIGHT=6' - 6"; NOZZLE_HEIGHT/7*2=1' - 7 1/2"; NOZZLE_SIZE=30' - 0"; NOZZLE_TOP_OD=3' - 9 1/2"; NOZZLE_TOP_RAD=1' - 10 3/4"; NOZZLE_WB/4=1' - 2 13/16"; NOZZLE_WB_OD=6' - 2"; NOZZLE_WB_RAD=3' - 1"; NOZZLE_WB_RAD-2"=2' - 11"; RO=3' - 8 3/4"; RO/2=1' - 10 3/8"; TRANSITION_TOP=5' - 8 1/4"; TYPE=1' - 0"; Type Comments=Vari-Plume Laboratory Exhaust Mixed-Flow High Pressure Inline Belt Drive With Isolation Box; UNIT_HEIGHT=4' - 6"; UNIT_HEIGHT*.75=3' - 4 1/2"; UNIT_OD=3' - 6 1/2"; UNIT_RADIUS=1' - 9 1/4"; UNIT_RADIUS*.6=1' - 7 1/8"; UNIT_RADIUS+4"=2' - 1 1/4"
- 330_QMXHPVP-24H-Isolation_Box: (A/2)+.25"=2' - 4 1/4"; (NOZZLE_HEIGHT-(NOZZLE_HEIGHT/8*2))/2=1' - 11 1/4"; (NOZZLE_WB_OD-NOZZLE_TOP_OD)/2=0' - 6 1/8"; A=4' - 8"; A/2=2' - 4"; B=12' - 10"; B/2=6' - 5"; C=6' - 1"; C/2=3' - 0 1/2"; E=4' - 6 13/16"; GA=0' - 0 3/32"; Model=QMXHPVP-Isolation Box; NOZZLE_BOTTOM_ID=2' - 10 3/4"; NOZZLE_BOTTOM_RAD=1' - 5 3/8"; NOZZLE_HEIGHT=5' - 2"; NOZZLE_HEIGHT/7*2=1' - 3 1/2"; NOZZLE_SIZE=24' - 0"; NOZZLE_TOP_OD=3' - 0 1/2"; NOZZLE_TOP_RAD=1' - 6 1/4"; NOZZLE_WB/4=1' - 0 3/16"; NOZZLE_WB_OD=5' - 1"; NOZZLE_WB_RAD=2' - 6 1/2"; NOZZLE_WB_RAD-2"=2' - 4 1/2"; RO=4' - 0 5/8"; RO/2=2' - 0 5/16"; TRANSITION_TOP=7' - 5 3/4"; TYPE=1' - 0"; Type Comments=Vari-Plume Laboratory Exhaust Mixed-Flow High Pressure Inline Belt Drive With Isolation Box; UNIT_HEIGHT=4' - 10 1/2"; UNIT_HEIGHT*.75=3' - 7 7/8"; UNIT_OD=3' - 10 3/4"; UNIT_RADIUS=1' - 11 3/8"; UNIT_RADIUS*.6=1' - 9 1/32"; UNIT_RADIUS+4"=2' - 3 3/8"
- 330_QMXHPVP-24L-Isolation_Box: (A/2)+.25"=2' - 4 1/4"; (NOZZLE_HEIGHT-(NOZZLE_HEIGHT/8*2))/2=1' - 11 1/4"; (NOZZLE_WB_OD-NOZZLE_TOP_OD)/2=0' - 6 1/8"; A=4' - 8"; A/2=2' - 4"; B=12' - 10"; B/2=6' - 5"; C=6' - 1"; C/2=3' - 0 1/2"; E=4' - 6 13/16"; GA=0' - 0 3/32"; Model=QMXHPVP-Isolation Box; NOZZLE_BOTTOM_ID=2' - 10 3/4"; NOZZLE_BOTTOM_RAD=1' - 5 3/8"; NOZZLE_HEIGHT=5' - 2"; NOZZLE_HEIGHT/7*2=1' - 3 1/2"; NOZZLE_SIZE=24' - 0"; NOZZLE_TOP_OD=3' - 0 1/2"; NOZZLE_TOP_RAD=1' - 6 1/4"; NOZZLE_WB/4=1' - 0 3/16"; NOZZLE_WB_OD=5' - 1"; NOZZLE_WB_RAD=2' - 6 1/2"; NOZZLE_WB_RAD-2"=2' - 4 1/2"; RO=4' - 0 5/8"; RO/2=2' - 0 5/16"; TRANSITION_TOP=7' - 5 3/4"; TYPE=1' - 0"; Type Comments=Vari-Plume Laboratory Exhaust Mixed-Flow High Pressure Inline Belt Drive With Isolation Box; UNIT_HEIGHT=4' - 10 1/2"; UNIT_HEIGHT*.75=3' - 7 7/8"; UNIT_OD=3' - 10 3/4"; UNIT_RADIUS=1' - 11 3/8"; UNIT_RADIUS*.6=1' - 9 1/32"; UNIT_RADIUS+4"=2' - 3 3/8"
- 330_QMXHPVP-30H-Isolation_Box: (A/2)+.25"=2' - 4 1/4"; (NOZZLE_HEIGHT-(NOZZLE_HEIGHT/8*2))/2=2' - 5 1/4"; (NOZZLE_WB_OD-NOZZLE_TOP_OD)/2=0' - 7 1/8"; A=4' - 8"; A/2=2' - 4"; B=12' - 10"; B/2=6' - 5"; C=6' - 1"; C/2=3' - 0 1/2"; E=4' - 6 13/16"; GA=0' - 0 3/32"; Model=QMXHPVP-Isolation Box; NOZZLE_BOTTOM_ID=3' - 6 1/2"; NOZZLE_BOTTOM_RAD=1' - 9 1/4"; NOZZLE_HEIGHT=6' - 6"; NOZZLE_HEIGHT/7*2=1' - 7 1/2"; NOZZLE_SIZE=30' - 0"; NOZZLE_TOP_OD=3' - 9 1/2"; NOZZLE_TOP_RAD=1' - 10 3/4"; NOZZLE_WB/4=1' - 2 13/16"; NOZZLE_WB_OD=6' - 2"; NOZZLE_WB_RAD=3' - 1"; NOZZLE_WB_RAD-2"=2' - 11"; RO=4' - 0 5/8"; RO/2=2' - 0 5/16"; TRANSITION_TOP=6' - 2 3/4"; TYPE=1' - 0"; Type Comments=Vari-Plume Laboratory Exhaust Mixed-Flow High Pressure Inline Belt Drive With Isolation Box; UNIT_HEIGHT=4' - 10 1/2"; UNIT_HEIGHT*.75=3' - 7 7/8"; UNIT_OD=3' - 10 3/4"; UNIT_RADIUS=1' - 11 3/8"; UNIT_RADIUS*.6=1' - 9 1/32"; UNIT_RADIUS+4"=2' - 3 3/8"
- 330_QMXHPVP-30L-Isolation_Box: (A/2)+.25"=2' - 4 1/4"; (NOZZLE_HEIGHT-(NOZZLE_HEIGHT/8*2))/2=2' - 5 1/4"; (NOZZLE_WB_OD-NOZZLE_TOP_OD)/2=0' - 7 1/8"; A=4' - 8"; A/2=2' - 4"; B=12' - 10"; B/2=6' - 5"; C=6' - 1"; C/2=3' - 0 1/2"; E=4' - 6 13/16"; GA=0' - 0 3/32"; Model=QMXHPVP-Isolation Box; NOZZLE_BOTTOM_ID=3' - 6 1/2"; NOZZLE_BOTTOM_RAD=1' - 9 1/4"; NOZZLE_HEIGHT=6' - 6"; NOZZLE_HEIGHT/7*2=1' - 7 1/2"; NOZZLE_SIZE=30' - 0"; NOZZLE_TOP_OD=3' - 9 1/2"; NOZZLE_TOP_RAD=1' - 10 3/4"; NOZZLE_WB/4=1' - 2 13/16"; NOZZLE_WB_OD=6' - 2"; NOZZLE_WB_RAD=3' - 1"; NOZZLE_WB_RAD-2"=2' - 11"; RO=4' - 0 5/8"; RO/2=2' - 0 5/16"; TRANSITION_TOP=6' - 2 3/4"; TYPE=1' - 0"; Type Comments=Vari-Plume Laboratory Exhaust Mixed-Flow High Pressure Inline Belt Drive With Isolation Box; UNIT_HEIGHT=4' - 10 1/2"; UNIT_HEIGHT*.75=3' - 7 7/8"; UNIT_OD=3' - 10 3/4"; UNIT_RADIUS=1' - 11 3/8"; UNIT_RADIUS*.6=1' - 9 1/32"; UNIT_RADIUS+4"=2' - 3 3/8"
- 365_QMXHPVP-24H-Isolation_Box: (A/2)+.25"=2' - 7 1/4"; (NOZZLE_HEIGHT-(NOZZLE_HEIGHT/8*2))/2=1' - 11 1/4"; (NOZZLE_WB_OD-NOZZLE_TOP_OD)/2=0' - 6 1/8"; A=5' - 2"; A/2=2' - 7"; B=14' - 7"; B/2=7' - 3 1/2"; C=6' - 7"; C/2=3' - 3 1/2"; E=5' - 0 3/4"; GA=0' - 0 3/32"; Model=QMXHPVP-Isolation Box; NOZZLE_BOTTOM_ID=2' - 10 3/4"; NOZZLE_BOTTOM_RAD=1' - 5 3/8"; NOZZLE_HEIGHT=5' - 2"; NOZZLE_HEIGHT/7*2=1' - 3 1/2"; NOZZLE_SIZE=24' - 0"; NOZZLE_TOP_OD=3' - 0 1/2"; NOZZLE_TOP_RAD=1' - 6 1/4"; NOZZLE_WB/4=1' - 0 3/16"; NOZZLE_WB_OD=5' - 1"; NOZZLE_WB_RAD=2' - 6 1/2"; NOZZLE_WB_RAD-2"=2' - 4 1/2"; RO=4' - 6 1/2"; RO/2=2' - 3 1/4"; TRANSITION_TOP=8' - 8 1/4"; TYPE=1' - 0"; Type Comments=Vari-Plume Laboratory Exhaust Mixed-Flow High Pressure Inline Belt Drive With Isolation Box; UNIT_HEIGHT=5' - 4"; UNIT_HEIGHT*.75=4' - 0"; UNIT_OD=4' - 3 3/4"; UNIT_RADIUS=2' - 1 7/8"; UNIT_RADIUS*.6=1' - 11 9/32"; UNIT_RADIUS+4"=2' - 5 7/8"
- 365_QMXHPVP-24L-Isolation_Box: (A/2)+.25"=2' - 7 1/4"; (NOZZLE_HEIGHT-(NOZZLE_HEIGHT/8*2))/2=1' - 11 1/4"; (NOZZLE_WB_OD-NOZZLE_TOP_OD)/2=0' - 6 1/8"; A=5' - 2"; A/2=2' - 7"; B=14' - 7"; B/2=7' - 3 1/2"; C=6' - 7"; C/2=3' - 3 1/2"; E=5' - 0 3/4"; GA=0' - 0 3/32"; Model=QMXHPVP-Isolation Box; NOZZLE_BOTTOM_ID=2' - 10 3/4"; NOZZLE_BOTTOM_RAD=1' - 5 3/8"; NOZZLE_HEIGHT=5' - 2"; NOZZLE_HEIGHT/7*2=1' - 3 1/2"; NOZZLE_SIZE=24' - 0"; NOZZLE_TOP_OD=3' - 0 1/2"; NOZZLE_TOP_RAD=1' - 6 1/4"; NOZZLE_WB/4=1' - 0 3/16"; NOZZLE_WB_OD=5' - 1"; NOZZLE_WB_RAD=2' - 6 1/2"; NOZZLE_WB_RAD-2"=2' - 4 1/2"; RO=4' - 6 1/2"; RO/2=2' - 3 1/4"; TRANSITION_TOP=8' - 8 1/4"; TYPE=1' - 0"; Type Comments=Vari-Plume Laboratory Exhaust Mixed-Flow High Pressure Inline Belt Drive With Isolation Box; UNIT_HEIGHT=5' - 4"; UNIT_HEIGHT*.75=4' - 0"; UNIT_OD=4' - 3 3/4"; UNIT_RADIUS=2' - 1 7/8"; UNIT_RADIUS*.6=1' - 11 9/32"; UNIT_RADIUS+4"=2' - 5 7/8"
- 365_QMXHPVP-30H-Isolation_Box: (A/2)+.25"=2' - 7 1/4"; (NOZZLE_HEIGHT-(NOZZLE_HEIGHT/8*2))/2=2' - 5 1/4"; (NOZZLE_WB_OD-NOZZLE_TOP_OD)/2=0' - 7 1/8"; A=5' - 2"; A/2=2' - 7"; B=14' - 7"; B/2=7' - 3 1/2"; C=6' - 7"; C/2=3' - 3 1/2"; E=5' - 0 3/4"; GA=0' - 0 3/32"; Model=QMXHPVP-Isolation Box; NOZZLE_BOTTOM_ID=3' - 6 1/2"; NOZZLE_BOTTOM_RAD=1' - 9 1/4"; NOZZLE_HEIGHT=6' - 6"; NOZZLE_HEIGHT/7*2=1' - 7 1/2"; NOZZLE_SIZE=30' - 0"; NOZZLE_TOP_OD=3' - 9 1/2"; NOZZLE_TOP_RAD=1' - 10 3/4"; NOZZLE_WB/4=1' - 2 13/16"; NOZZLE_WB_OD=6' - 2"; NOZZLE_WB_RAD=3' - 1"; NOZZLE_WB_RAD-2"=2' - 11"; RO=4' - 6 1/2"; RO/2=2' - 3 1/4"; TRANSITION_TOP=7' - 5 1/2"; TYPE=1' - 0"; Type Comments=Vari-Plume Laboratory Exhaust Mixed-Flow High Pressure Inline Belt Drive With Isolation Box; UNIT_HEIGHT=5' - 4"; UNIT_HEIGHT*.75=4' - 0"; UNIT_OD=4' - 3 3/4"; UNIT_RADIUS=2' - 1 7/8"; UNIT_RADIUS*.6=1' - 11 9/32"; UNIT_RADIUS+4"=2' - 5 7/8"
- 365_QMXHPVP-30L-Isolation_Box: (A/2)+.25"=2' - 7 1/4"; (NOZZLE_HEIGHT-(NOZZLE_HEIGHT/8*2))/2=2' - 5 1/4"; (NOZZLE_WB_OD-NOZZLE_TOP_OD)/2=0' - 7 1/8"; A=5' - 2"; A/2=2' - 7"; B=14' - 7"; B/2=7' - 3 1/2"; C=6' - 7"; C/2=3' - 3 1/2"; E=5' - 0 3/4"; GA=0' - 0 3/32"; Model=QMXHPVP-Isolation Box; NOZZLE_BOTTOM_ID=3' - 6 1/2"; NOZZLE_BOTTOM_RAD=1' - 9 1/4"; NOZZLE_HEIGHT=6' - 6"; NOZZLE_HEIGHT/7*2=1' - 7 1/2"; NOZZLE_SIZE=30' - 0"; NOZZLE_TOP_OD=3' - 9 1/2"; NOZZLE_TOP_RAD=1' - 10 3/4"; NOZZLE_WB/4=1' - 2 13/16"; NOZZLE_WB_OD=6' - 2"; NOZZLE_WB_RAD=3' - 1"; NOZZLE_WB_RAD-2"=2' - 11"; RO=4' - 6 1/2"; RO/2=2' - 3 1/4"; TRANSITION_TOP=7' - 5 1/2"; TYPE=1' - 0"; Type Comments=Vari-Plume Laboratory Exhaust Mixed-Flow High Pressure Inline Belt Drive With Isolation Box; UNIT_HEIGHT=5' - 4"; UNIT_HEIGHT*.75=4' - 0"; UNIT_OD=4' - 3 3/4"; UNIT_RADIUS=2' - 1 7/8"; UNIT_RADIUS*.6=1' - 11 9/32"; UNIT_RADIUS+4"=2' - 5 7/8"
- 365_QMXVP-36H-Isolation_Box: (A/2)+.25"=2' - 7 1/4"; (NOZZLE_HEIGHT-(NOZZLE_HEIGHT/8*2))/2=2' - 11 5/8"; (NOZZLE_WB_OD-NOZZLE_TOP_OD)/2=0' - 8"; A=5' - 2"; A/2=2' - 7"; B=14' - 7"; B/2=7' - 3 1/2"; C=6' - 7"; C/2=3' - 3 1/2"; E=5' - 0 3/4"; GA=0' - 0 3/32"; Model=QMXVP-Isolation Box; NOZZLE_BOTTOM_ID=4' - 3 3/4"; NOZZLE_BOTTOM_RAD=2' - 1 7/8"; NOZZLE_HEIGHT=7' - 11"; NOZZLE_HEIGHT/7*2=1' - 11 3/4"; NOZZLE_SIZE=36' - 0"; NOZZLE_TOP_OD=4' - 10"; NOZZLE_TOP_RAD=2' - 5"; NOZZLE_WB/4=1' - 6"; NOZZLE_WB_OD=7' - 6"; NOZZLE_WB_RAD=3' - 9"; NOZZLE_WB_RAD-2"=3' - 7"; RO=4' - 6 1/2"; RO/2=2' - 3 1/4"; TRANSITION_TOP=6' - 6 1/4"; TYPE=0' - 0"; Type Comments=Vari-Plume Laboratory Exhaust Mixed-Flow Inline Belt Drive With Isolation Box; UNIT_HEIGHT=5' - 4"; UNIT_HEIGHT*.75=4' - 0"; UNIT_OD=4' - 3 3/4"; UNIT_RADIUS=2' - 1 7/8"; UNIT_RADIUS*.6=1' - 11 9/32"; UNIT_RADIUS+4"=2' - 5 7/8"
- 365_QMXHPVP-36L-Isolation_Box: (A/2)+.25"=2' - 7 1/4"; (NOZZLE_HEIGHT-(NOZZLE_HEIGHT/8*2))/2=2' - 11 5/8"; (NOZZLE_WB_OD-NOZZLE_TOP_OD)/2=0' - 8"; A=5' - 2"; A/2=2' - 7"; B=14' - 7"; B/2=7' - 3 1/2"; C=6' - 7"; C/2=3' - 3 1/2"; E=5' - 0 3/4"; GA=0' - 0 3/32"; Model=QMXHPVP-Isolation Box; NOZZLE_BOTTOM_ID=4' - 3 3/4"; NOZZLE_BOTTOM_RAD=2' - 1 7/8"; NOZZLE_HEIGHT=7' - 11"; NOZZLE_HEIGHT/7*2=1' - 11 3/4"; NOZZLE_SIZE=36' - 0"; NOZZLE_TOP_OD=4' - 10"; NOZZLE_TOP_RAD=2' - 5"; NOZZLE_WB/4=1' - 6"; NOZZLE_WB_OD=7' - 6"; NOZZLE_WB_RAD=3' - 9"; NOZZLE_WB_RAD-2"=3' - 7"; RO=4' - 6 1/2"; RO/2=2' - 3 1/4"; TRANSITION_TOP=6' - 6 1/4"; TYPE=1' - 0"; Type Comments=Vari-Plume Laboratory Exhaust Mixed-Flow High Pressure Inline Belt Drive With Isolation Box; UNIT_HEIGHT=5' - 4"; UNIT_HEIGHT*.75=4' - 0"; UNIT_OD=4' - 3 3/4"; UNIT_RADIUS=2' - 1 7/8"; UNIT_RADIUS*.6=1' - 11 9/32"; UNIT_RADIUS+4"=2' - 5 7/8"
- 365_QMXHPVP-36H-Isolation_Box: (A/2)+.25"=2' - 7 1/4"; (NOZZLE_HEIGHT-(NOZZLE_HEIGHT/8*2))/2=2' - 11 5/8"; (NOZZLE_WB_OD-NOZZLE_TOP_OD)/2=0' - 8"; A=5' - 2"; A/2=2' - 7"; B=14' - 7"; B/2=7' - 3 1/2"; C=6' - 7"; C/2=3' - 3 1/2"; E=5' - 0 3/4"; GA=0' - 0 3/32"; Model=QMXHPVP-Isolation Box; NOZZLE_BOTTOM_ID=4' - 3 3/4"; NOZZLE_BOTTOM_RAD=2' - 1 7/8"; NOZZLE_HEIGHT=7' - 11"; NOZZLE_HEIGHT/7*2=1' - 11 3/4"; NOZZLE_SIZE=36' - 0"; NOZZLE_TOP_OD=4' - 10"; NOZZLE_TOP_RAD=2' - 5"; NOZZLE_WB/4=1' - 6"; NOZZLE_WB_OD=7' - 6"; NOZZLE_WB_RAD=3' - 9"; NOZZLE_WB_RAD-2"=3' - 7"; RO=4' - 6 1/2"; RO/2=2' - 3 1/4"; TRANSITION_TOP=6' - 6 1/4"; TYPE=1' - 0"; Type Comments=Vari-Plume Laboratory Exhaust Mixed-Flow High Pressure Inline Belt Drive With Isolation Box; UNIT_HEIGHT=5' - 4"; UNIT_HEIGHT*.75=4' - 0"; UNIT_OD=4' - 3 3/4"; UNIT_RADIUS=2' - 1 7/8"; UNIT_RADIUS*.6=1' - 11 9/32"; UNIT_RADIUS+4"=2' - 5 7/8"
- 402_QMXHPVP-24H-Isolation_Box: (A/2)+.25"=2' - 9 3/4"; (NOZZLE_HEIGHT-(NOZZLE_HEIGHT/8*2))/2=1' - 11 1/4"; (NOZZLE_WB_OD-NOZZLE_TOP_OD)/2=0' - 6 1/8"; A=5' - 7"; A/2=2' - 9 1/2"; B=15' - 3"; B/2=7' - 7 1/2"; C=7' - 4"; C/2=3' - 8"; E=5' - 5 3/4"; GA=0' - 0 3/32"; Model=QMXHPVP-Isolation Box; NOZZLE_BOTTOM_ID=2' - 10 3/4"; NOZZLE_BOTTOM_RAD=1' - 5 3/8"; NOZZLE_HEIGHT=5' - 2"; NOZZLE_HEIGHT/7*2=1' - 3 1/2"; NOZZLE_SIZE=24' - 0"; NOZZLE_TOP_OD=3' - 0 1/2"; NOZZLE_TOP_RAD=1' - 6 1/4"; NOZZLE_WB/4=1' - 0 3/16"; NOZZLE_WB_OD=5' - 1"; NOZZLE_WB_RAD=2' - 6 1/2"; NOZZLE_WB_RAD-2"=2' - 4 1/2"; RO=4' - 11 7/16"; RO/2=2' - 5 23/32"; TRANSITION_TOP=9' - 10 3/4"; TYPE=1' - 0"; Type Comments=Vari-Plume Laboratory Exhaust Mixed-Flow High Pressure Inline Belt Drive With Isolation Box; UNIT_HEIGHT=5' - 8 1/2"; UNIT_HEIGHT*.75=4' - 3 3/8"; UNIT_OD=4' - 8 15/16"; UNIT_RADIUS=2' - 4 15/32"; UNIT_RADIUS*.6=2' - 1 5/8"; UNIT_RADIUS+4"=2' - 8 15/32"
- 402_QMXHPVP-24L-Isolation_Box: (A/2)+.25"=2' - 9 3/4"; (NOZZLE_HEIGHT-(NOZZLE_HEIGHT/8*2))/2=1' - 11 1/4"; (NOZZLE_WB_OD-NOZZLE_TOP_OD)/2=0' - 6 1/8"; A=5' - 7"; A/2=2' - 9 1/2"; B=15' - 3"; B/2=7' - 7 1/2"; C=7' - 4"; C/2=3' - 8"; E=5' - 5 3/4"; GA=0' - 0 3/32"; Model=QMXHPVP-Isolation Box; NOZZLE_BOTTOM_ID=2' - 10 3/4"; NOZZLE_BOTTOM_RAD=1' - 5 3/8"; NOZZLE_HEIGHT=5' - 2"; NOZZLE_HEIGHT/7*2=1' - 3 1/2"; NOZZLE_SIZE=24' - 0"; NOZZLE_TOP_OD=3' - 0 1/2"; NOZZLE_TOP_RAD=1' - 6 1/4"; NOZZLE_WB/4=1' - 0 3/16"; NOZZLE_WB_OD=5' - 1"; NOZZLE_WB_RAD=2' - 6 1/2"; NOZZLE_WB_RAD-2"=2' - 4 1/2"; RO=4' - 11 7/16"; RO/2=2' - 5 23/32"; TRANSITION_TOP=9' - 10 3/4"; TYPE=1' - 0"; Type Comments=Vari-Plume Laboratory Exhaust Mixed-Flow High Pressure Inline Belt Drive With Isolation Box; UNIT_HEIGHT=5' - 8 1/2"; UNIT_HEIGHT*.75=4' - 3 3/8"; UNIT_OD=4' - 8 15/16"; UNIT_RADIUS=2' - 4 15/32"; UNIT_RADIUS*.6=2' - 1 5/8"; UNIT_RADIUS+4"=2' - 8 15/32"
- 402_QMXHPVP-30H-Isolation_Box: (A/2)+.25"=2' - 9 3/4"; (NOZZLE_HEIGHT-(NOZZLE_HEIGHT/8*2))/2=2' - 5 1/4"; (NOZZLE_WB_OD-NOZZLE_TOP_OD)/2=0' - 7 1/8"; A=5' - 7"; A/2=2' - 9 1/2"; B=15' - 3"; B/2=7' - 7 1/2"; C=7' - 4"; C/2=3' - 8"; E=5' - 5 3/4"; GA=0' - 0 3/32"; Model=QMXHPVP-Isolation Box; NOZZLE_BOTTOM_ID=3' - 6 1/2"; NOZZLE_BOTTOM_RAD=1' - 9 1/4"; NOZZLE_HEIGHT=6' - 6"; NOZZLE_HEIGHT/7*2=1' - 7 1/2"; NOZZLE_SIZE=30' - 0"; NOZZLE_TOP_OD=3' - 9 1/2"; NOZZLE_TOP_RAD=1' - 10 3/4"; NOZZLE_WB/4=1' - 2 13/16"; NOZZLE_WB_OD=6' - 2"; NOZZLE_WB_RAD=3' - 1"; NOZZLE_WB_RAD-2"=2' - 11"; RO=4' - 11 7/16"; RO/2=2' - 5 23/32"; TRANSITION_TOP=8' - 7 3/4"; TYPE=1' - 0"; Type Comments=Vari-Plume Laboratory Exhaust Mixed-Flow High Pressure Inline Belt Drive With Isolation Box; UNIT_HEIGHT=5' - 8 1/2"; UNIT_HEIGHT*.75=4' - 3 3/8"; UNIT_OD=4' - 8 15/16"; UNIT_RADIUS=2' - 4 15/32"; UNIT_RADIUS*.6=2' - 1 5/8"; UNIT_RADIUS+4"=2' - 8 15/32"
- 402_QMXHPVP-30L-Isolation_Box: (A/2)+.25"=2' - 9 3/4"; (NOZZLE_HEIGHT-(NOZZLE_HEIGHT/8*2))/2=2' - 5 1/4"; (NOZZLE_WB_OD-NOZZLE_TOP_OD)/2=0' - 7 1/8"; A=5' - 7"; A/2=2' - 9 1/2"; B=15' - 3"; B/2=7' - 7 1/2"; C=7' - 4"; C/2=3' - 8"; E=5' - 5 3/4"; GA=0' - 0 3/32"; Model=QMXHPVP-Isolation Box; NOZZLE_BOTTOM_ID=3' - 6 1/2"; NOZZLE_BOTTOM_RAD=1' - 9 1/4"; NOZZLE_HEIGHT=6' - 6"; NOZZLE_HEIGHT/7*2=1' - 7 1/2"; NOZZLE_SIZE=30' - 0"; NOZZLE_TOP_OD=3' - 9 1/2"; NOZZLE_TOP_RAD=1' - 10 3/4"; NOZZLE_WB/4=1' - 2 13/16"; NOZZLE_WB_OD=6' - 2"; NOZZLE_WB_RAD=3' - 1"; NOZZLE_WB_RAD-2"=2' - 11"; RO=4' - 11 7/16"; RO/2=2' - 5 23/32"; TRANSITION_TOP=8' - 7 3/4"; TYPE=1' - 0"; Type Comments=Vari-Plume Laboratory Exhaust Mixed-Flow High Pressure Inline Belt Drive With Isolation Box; UNIT_HEIGHT=5' - 8 1/2"; UNIT_HEIGHT*.75=4' - 3 3/8"; UNIT_OD=4' - 8 15/16"; UNIT_RADIUS=2' - 4 15/32"; UNIT_RADIUS*.6=2' - 1 5/8"; UNIT_RADIUS+4"=2' - 8 15/32"
- 402_QMXHPVP-36H-Isolation_Box: (A/2)+.25"=2' - 9 3/4"; (NOZZLE_HEIGHT-(NOZZLE_HEIGHT/8*2))/2=2' - 11 5/8"; (NOZZLE_WB_OD-NOZZLE_TOP_OD)/2=0' - 8"; A=5' - 7"; A/2=2' - 9 1/2"; B=15' - 3"; B/2=7' - 7 1/2"; C=7' - 4"; C/2=3' - 8"; E=5' - 5 3/4"; GA=0' - 0 3/32"; Model=QMXHPVP-Isolation Box; NOZZLE_BOTTOM_ID=4' - 3 3/4"; NOZZLE_BOTTOM_RAD=2' - 1 7/8"; NOZZLE_HEIGHT=7' - 11"; NOZZLE_HEIGHT/7*2=1' - 11 3/4"; NOZZLE_SIZE=36' - 0"; NOZZLE_TOP_OD=4' - 10"; NOZZLE_TOP_RAD=2' - 5"; NOZZLE_WB/4=1' - 6"; NOZZLE_WB_OD=7' - 6"; NOZZLE_WB_RAD=3' - 9"; NOZZLE_WB_RAD-2"=3' - 7"; RO=4' - 11 7/16"; RO/2=2' - 5 23/32"; TRANSITION_TOP=7' - 2 3/4"; TYPE=1' - 0"; Type Comments=Vari-Plume Laboratory Exhaust Mixed-Flow High Pressure Inline Belt Drive With Isolation Box; UNIT_HEIGHT=5' - 8 1/2"; UNIT_HEIGHT*.75=4' - 3 3/8"; UNIT_OD=4' - 8 15/16"; UNIT_RADIUS=2' - 4 15/32"; UNIT_RADIUS*.6=2' - 1 5/8"; UNIT_RADIUS+4"=2' - 8 15/32"
- 402_QMXHPVP-36L-Isolation_Box: (A/2)+.25"=2' - 9 3/4"; (NOZZLE_HEIGHT-(NOZZLE_HEIGHT/8*2))/2=2' - 11 5/8"; (NOZZLE_WB_OD-NOZZLE_TOP_OD)/2=0' - 8"; A=5' - 7"; A/2=2' - 9 1/2"; B=15' - 3"; B/2=7' - 7 1/2"; C=7' - 4"; C/2=3' - 8"; E=5' - 5 3/4"; GA=0' - 0 3/32"; Model=QMXHPVP-Isolation Box; NOZZLE_BOTTOM_ID=4' - 3 3/4"; NOZZLE_BOTTOM_RAD=2' - 1 7/8"; NOZZLE_HEIGHT=7' - 11"; NOZZLE_HEIGHT/7*2=1' - 11 3/4"; NOZZLE_SIZE=36' - 0"; NOZZLE_TOP_OD=4' - 10"; NOZZLE_TOP_RAD=2' - 5"; NOZZLE_WB/4=1' - 6"; NOZZLE_WB_OD=7' - 6"; NOZZLE_WB_RAD=3' - 9"; NOZZLE_WB_RAD-2"=3' - 7"; RO=4' - 11 7/16"; RO/2=2' - 5 23/32"; TRANSITION_TOP=7' - 2 3/4"; TYPE=1' - 0"; Type Comments=Vari-Plume Laboratory Exhaust Mixed-Flow High Pressure Inline Belt Drive With Isolation Box; UNIT_HEIGHT=5' - 8 1/2"; UNIT_HEIGHT*.75=4' - 3 3/8"; UNIT_OD=4' - 8 15/16"; UNIT_RADIUS=2' - 4 15/32"; UNIT_RADIUS*.6=2' - 1 5/8"; UNIT_RADIUS+4"=2' - 8 15/32"
- 445_QMXHPVP-30H-Isolation_Box: (A/2)+.25"=3' - 1 1/4"; (NOZZLE_HEIGHT-(NOZZLE_HEIGHT/8*2))/2=2' - 5 1/4"; (NOZZLE_WB_OD-NOZZLE_TOP_OD)/2=0' - 7 1/8"; A=6' - 2"; A/2=3' - 1"; B=16' - 9"; B/2=8' - 4 1/2"; C=7' - 11"; C/2=3' - 11 1/2"; E=6' - 0 5/8"; GA=0' - 0 3/32"; Model=QMXHPVP-Isolation Box; NOZZLE_BOTTOM_ID=3' - 6 1/2"; NOZZLE_BOTTOM_RAD=1' - 9 1/4"; NOZZLE_HEIGHT=6' - 6"; NOZZLE_HEIGHT/7*2=1' - 7 1/2"; NOZZLE_SIZE=30' - 0"; NOZZLE_TOP_OD=3' - 9 1/2"; NOZZLE_TOP_RAD=1' - 10 3/4"; NOZZLE_WB/4=1' - 2 13/16"; NOZZLE_WB_OD=6' - 2"; NOZZLE_WB_RAD=3' - 1"; NOZZLE_WB_RAD-2"=2' - 11"; RO=5' - 6 7/16"; RO/2=2' - 9 7/32"; TRANSITION_TOP=10' - 1 1/4"; TYPE=1' - 0"; Type Comments=Vari-Plume Laboratory Exhaust Mixed-Flow High Pressure Inline Belt Drive With Isolation Box; UNIT_HEIGHT=6' - 2"; UNIT_HEIGHT*.75=4' - 7 1/2"; UNIT_OD=5' - 3 1/16"; UNIT_RADIUS=2' - 7 17/32"; UNIT_RADIUS*.6=2' - 4 3/8"; UNIT_RADIUS+4"=2' - 11 17/32"
- 445_QMXHPVP-30L-Isolation_Box: (A/2)+.25"=3' - 1 1/4"; (NOZZLE_HEIGHT-(NOZZLE_HEIGHT/8*2))/2=2' - 5 1/4"; (NOZZLE_WB_OD-NOZZLE_TOP_OD)/2=0' - 7 1/8"; A=6' - 2"; A/2=3' - 1"; B=16' - 9"; B/2=8' - 4 1/2"; C=7' - 11"; C/2=3' - 11 1/2"; E=6' - 0 5/8"; GA=0' - 0 3/32"; Model=QMXHPVP-Isolation Box; NOZZLE_BOTTOM_ID=3' - 6 1/2"; NOZZLE_BOTTOM_RAD=1' - 9 1/4"; NOZZLE_HEIGHT=6' - 6"; NOZZLE_HEIGHT/7*2=1' - 7 1/2"; NOZZLE_SIZE=30' - 0"; NOZZLE_TOP_OD=3' - 9 1/2"; NOZZLE_TOP_RAD=1' - 10 3/4"; NOZZLE_WB/4=1' - 2 13/16"; NOZZLE_WB_OD=6' - 2"; NOZZLE_WB_RAD=3' - 1"; NOZZLE_WB_RAD-2"=2' - 11"; RO=5' - 6 7/16"; RO/2=2' - 9 7/32"; TRANSITION_TOP=10' - 1 1/4"; TYPE=1' - 0"; Type Comments=Vari-Plume Laboratory Exhaust Mixed-Flow High Pressure Inline Belt Drive With Isolation Box; UNIT_HEIGHT=6' - 2"; UNIT_HEIGHT*.75=4' - 7 1/2"; UNIT_OD=5' - 3 1/16"; UNIT_RADIUS=2' - 7 17/32"; UNIT_RADIUS*.6=2' - 4 3/8"; UNIT_RADIUS+4"=2' - 11 17/32"
- 445_QMXHPVP-36H-Isolation_Box: (A/2)+.25"=3' - 1 1/4"; (NOZZLE_HEIGHT-(NOZZLE_HEIGHT/8*2))/2=2' - 11 5/8"; (NOZZLE_WB_OD-NOZZLE_TOP_OD)/2=0' - 8"; A=6' - 2"; A/2=3' - 1"; B=16' - 9"; B/2=8' - 4 1/2"; C=7' - 11"; C/2=3' - 11 1/2"; E=6' - 0 5/8"; GA=0' - 0 3/32"; Model=QMXHPVP-Isolation Box; NOZZLE_BOTTOM_ID=4' - 3 3/4"; NOZZLE_BOTTOM_RAD=2' - 1 7/8"; NOZZLE_HEIGHT=7' - 11"; NOZZLE_HEIGHT/7*2=1' - 11 3/4"; NOZZLE_SIZE=36' - 0"; NOZZLE_TOP_OD=4' - 10"; NOZZLE_TOP_RAD=2' - 5"; NOZZLE_WB/4=1' - 6"; NOZZLE_WB_OD=7' - 6"; NOZZLE_WB_RAD=3' - 9"; NOZZLE_WB_RAD-2"=3' - 7"; RO=5' - 6 7/16"; RO/2=2' - 9 7/32"; TRANSITION_TOP=8' - 7 1/4"; TYPE=1' - 0"; Type Comments=Vari-Plume Laboratory Exhaust Mixed-Flow High Pressure Inline Belt Drive With Isolation Box; UNIT_HEIGHT=6' - 2"; UNIT_HEIGHT*.75=4' - 7 1/2"; UNIT_OD=5' - 3 1/16"; UNIT_RADIUS=2' - 7 17/32"; UNIT_RADIUS*.6=2' - 4 3/8"; UNIT_RADIUS+4"=2' - 11 17/32"
- 445_QMXHPVP-36L-Isolation_Box: (A/2)+.25"=3' - 1 1/4"; (NOZZLE_HEIGHT-(NOZZLE_HEIGHT/8*2))/2=2' - 11 5/8"; (NOZZLE_WB_OD-NOZZLE_TOP_OD)/2=0' - 8"; A=6' - 2"; A/2=3' - 1"; B=16' - 9"; B/2=8' - 4 1/2"; C=7' - 11"; C/2=3' - 11 1/2"; E=6' - 0 5/8"; GA=0' - 0 3/32"; Model=QMXHPVP-Isolation Box; NOZZLE_BOTTOM_ID=4' - 3 3/4"; NOZZLE_BOTTOM_RAD=2' - 1 7/8"; NOZZLE_HEIGHT=7' - 11"; NOZZLE_HEIGHT/7*2=1' - 11 3/4"; NOZZLE_SIZE=36' - 0"; NOZZLE_TOP_OD=4' - 10"; NOZZLE_TOP_RAD=2' - 5"; NOZZLE_WB/4=1' - 6"; NOZZLE_WB_OD=7' - 6"; NOZZLE_WB_RAD=3' - 9"; NOZZLE_WB_RAD-2"=3' - 7"; RO=5' - 6 7/16"; RO/2=2' - 9 7/32"; TRANSITION_TOP=8' - 7 1/4"; TYPE=1' - 0"; Type Comments=Vari-Plume Laboratory Exhaust Mixed-Flow High Pressure Inline Belt Drive With Isolation Box; UNIT_HEIGHT=6' - 2"; UNIT_HEIGHT*.75=4' - 7 1/2"; UNIT_OD=5' - 3 1/16"; UNIT_RADIUS=2' - 7 17/32"; UNIT_RADIUS*.6=2' - 4 3/8"; UNIT_RADIUS+4"=2' - 11 17/32"
- 490_QMXHPVP-30H-Isolation_Box: (A/2)+.25"=3' - 4 1/4"; (NOZZLE_HEIGHT-(NOZZLE_HEIGHT/8*2))/2=2' - 5 1/4"; (NOZZLE_WB_OD-NOZZLE_TOP_OD)/2=0' - 7 1/8"; A=6' - 8"; A/2=3' - 4"; B=18' - 3"; B/2=9' - 1 1/2"; C=8' - 7"; C/2=4' - 3 1/2"; E=6' - 6 1/2"; GA=0' - 0 1/8"; Model=QMXHPVP-Isolation Box; NOZZLE_BOTTOM_ID=3' - 6 1/2"; NOZZLE_BOTTOM_RAD=1' - 9 1/4"; NOZZLE_HEIGHT=6' - 6"; NOZZLE_HEIGHT/7*2=1' - 7 1/2"; NOZZLE_SIZE=30' - 0"; NOZZLE_TOP_OD=3' - 9 1/2"; NOZZLE_TOP_RAD=1' - 10 3/4"; NOZZLE_WB/4=1' - 2 13/16"; NOZZLE_WB_OD=6' - 2"; NOZZLE_WB_RAD=3' - 1"; NOZZLE_WB_RAD-2"=2' - 11"; RO=6' - 0 1/4"; RO/2=3' - 0 1/8"; TRANSITION_TOP=11' - 7 3/4"; TYPE=1' - 0"; Type Comments=Vari-Plume Laboratory Exhaust Mixed-Flow High Pressure Inline Belt Drive With Isolation Box; UNIT_HEIGHT=6' - 8 1/2"; UNIT_HEIGHT*.75=5' - 0 3/8"; UNIT_OD=5' - 9 3/8"; UNIT_RADIUS=2' - 10 11/16"; UNIT_RADIUS*.6=2' - 7 7/32"; UNIT_RADIUS+4"=3' - 2 11/16"
- 490_QMXHPVP-30L-Isolation_Box: (A/2)+.25"=3' - 4 1/4"; (NOZZLE_HEIGHT-(NOZZLE_HEIGHT/8*2))/2=2' - 5 1/4"; (NOZZLE_WB_OD-NOZZLE_TOP_OD)/2=0' - 7 1/8"; A=6' - 8"; A/2=3' - 4"; B=18' - 3"; B/2=9' - 1 1/2"; C=8' - 7"; C/2=4' - 3 1/2"; E=6' - 6 1/2"; GA=0' - 0 1/8"; Model=QMXHPVP-Isolation Box; NOZZLE_BOTTOM_ID=3' - 6 1/2"; NOZZLE_BOTTOM_RAD=1' - 9 1/4"; NOZZLE_HEIGHT=6' - 6"; NOZZLE_HEIGHT/7*2=1' - 7 1/2"; NOZZLE_SIZE=30' - 0"; NOZZLE_TOP_OD=3' - 9 1/2"; NOZZLE_TOP_RAD=1' - 10 3/4"; NOZZLE_WB/4=1' - 2 13/16"; NOZZLE_WB_OD=6' - 2"; NOZZLE_WB_RAD=3' - 1"; NOZZLE_WB_RAD-2"=2' - 11"; RO=6' - 0 1/4"; RO/2=3' - 0 1/8"; TRANSITION_TOP=11' - 7 3/4"; TYPE=1' - 0"; Type Comments=Vari-Plume Laboratory Exhaust Mixed-Flow High Pressure Inline Belt Drive With Isolation Box; UNIT_HEIGHT=6' - 8 1/2"; UNIT_HEIGHT*.75=5' - 0 3/8"; UNIT_OD=5' - 9 3/8"; UNIT_RADIUS=2' - 10 11/16"; UNIT_RADIUS*.6=2' - 7 7/32"; UNIT_RADIUS+4"=3' - 2 11/16"
- 490_QMXHPVP-36H-Isolation_Box: (A/2)+.25"=3' - 4 1/4"; (NOZZLE_HEIGHT-(NOZZLE_HEIGHT/8*2))/2=2' - 11 5/8"; (NOZZLE_WB_OD-NOZZLE_TOP_OD)/2=0' - 8"; A=6' - 8"; A/2=3' - 4"; B=18' - 3"; B/2=9' - 1 1/2"; C=8' - 7"; C/2=4' - 3 1/2"; E=6' - 6 1/2"; GA=0' - 0 1/8"; Model=QMXHPVP-Isolation Box; NOZZLE_BOTTOM_ID=4' - 3 3/4"; NOZZLE_BOTTOM_RAD=2' - 1 7/8"; NOZZLE_HEIGHT=7' - 11"; NOZZLE_HEIGHT/7*2=1' - 11 3/4"; NOZZLE_SIZE=36' - 0"; NOZZLE_TOP_OD=4' - 10"; NOZZLE_TOP_RAD=2' - 5"; NOZZLE_WB/4=1' - 6"; NOZZLE_WB_OD=7' - 6"; NOZZLE_WB_RAD=3' - 9"; NOZZLE_WB_RAD-2"=3' - 7"; RO=6' - 0 1/4"; RO/2=3' - 0 1/8"; TRANSITION_TOP=10' - 2 3/4"; TYPE=1' - 0"; Type Comments=Vari-Plume Laboratory Exhaust Mixed-Flow High Pressure Inline Belt Drive With Isolation Box; UNIT_HEIGHT=6' - 8 1/2"; UNIT_HEIGHT*.75=5' - 0 3/8"; UNIT_OD=5' - 9 3/8"; UNIT_RADIUS=2' - 10 11/16"; UNIT_RADIUS*.6=2' - 7 7/32"; UNIT_RADIUS+4"=3' - 2 11/16"
- 490_QMXHPVP-36L-Isolation_Box: (A/2)+.25"=3' - 4 1/4"; (NOZZLE_HEIGHT-(NOZZLE_HEIGHT/8*2))/2=2' - 11 5/8"; (NOZZLE_WB_OD-NOZZLE_TOP_OD)/2=0' - 8"; A=6' - 8"; A/2=3' - 4"; B=18' - 3"; B/2=9' - 1 1/2"; C=8' - 7"; C/2=4' - 3 1/2"; E=6' - 6 1/2"; GA=0' - 0 1/8"; Model=QMXHPVP-Isolation Box; NOZZLE_BOTTOM_ID=4' - 3 3/4"; NOZZLE_BOTTOM_RAD=2' - 1 7/8"; NOZZLE_HEIGHT=7' - 11"; NOZZLE_HEIGHT/7*2=1' - 11 3/4"; NOZZLE_SIZE=36' - 0"; NOZZLE_TOP_OD=4' - 10"; NOZZLE_TOP_RAD=2' - 5"; NOZZLE_WB/4=1' - 6"; NOZZLE_WB_OD=7' - 6"; NOZZLE_WB_RAD=3' - 9"; NOZZLE_WB_RAD-2"=3' - 7"; RO=6' - 0 1/4"; RO/2=3' - 0 1/8"; TRANSITION_TOP=10' - 2 3/4"; TYPE=1' - 0"; Type Comments=Vari-Plume Laboratory Exhaust Mixed-Flow High Pressure Inline Belt Drive With Isolation Box; UNIT_HEIGHT=6' - 8 1/2"; UNIT_HEIGHT*.75=5' - 0 3/8"; UNIT_OD=5' - 9 3/8"; UNIT_RADIUS=2' - 10 11/16"; UNIT_RADIUS*.6=2' - 7 7/32"; UNIT_RADIUS+4"=3' - 2 11/16"
- 490_QMXHPVP-49H-Isolation_Box: (A/2)+.25"=3' - 4 1/4"; (NOZZLE_HEIGHT-(NOZZLE_HEIGHT/8*2))/2=3' - 5 1/4"; (NOZZLE_WB_OD-NOZZLE_TOP_OD)/2=0' - 6 1/4"; A=6' - 8"; A/2=3' - 4"; B=18' - 3"; B/2=9' - 1 1/2"; C=8' - 7"; C/2=4' - 3 1/2"; E=6' - 6 1/2"; GA=0' - 0 1/8"; Model=QMXHPVP-Isolation Box; NOZZLE_BOTTOM_ID=5' - 9 3/8"; NOZZLE_BOTTOM_RAD=2' - 10 11/16"; NOZZLE_HEIGHT=9' - 2"; NOZZLE_HEIGHT/7*2=2' - 3 1/2"; NOZZLE_SIZE=49' - 0"; NOZZLE_TOP_OD=6' - 4"; NOZZLE_TOP_RAD=3' - 2"; NOZZLE_WB/4=1' - 8 3/16"; NOZZLE_WB_OD=8' - 5"; NOZZLE_WB_RAD=4' - 2 1/2"; NOZZLE_WB_RAD-2"=4' - 0 1/2"; RO=6' - 0 1/4"; RO/2=3' - 0 1/8"; TRANSITION_TOP=8' - 0 3/4"; TYPE=1' - 0"; Type Comments=Vari-Plume Laboratory Exhaust Mixed-Flow High Pressure Inline Belt Drive With Isolation Box; UNIT_HEIGHT=6' - 8 1/2"; UNIT_HEIGHT*.75=5' - 0 3/8"; UNIT_OD=5' - 9 3/8"; UNIT_RADIUS=2' - 10 11/16"; UNIT_RADIUS*.6=2' - 7 7/32"; UNIT_RADIUS+4"=3' - 2 11/16"
- 540_QMXHPVP-36H-Isolation_Box: (A/2)+.25"=3' - 9 1/4"; (NOZZLE_HEIGHT-(NOZZLE_HEIGHT/8*2))/2=2' - 11 5/8"; (NOZZLE_WB_OD-NOZZLE_TOP_OD)/2=0' - 8"; A=7' - 6"; A/2=3' - 9"; B=19' - 11"; B/2=9' - 11 1/2"; C=9' - 3"; C/2=4' - 7 1/2"; E=7' - 1 3/8"; GA=0' - 0 1/8"; Model=QMXHPVP-Isolation Box; NOZZLE_BOTTOM_ID=4' - 3 3/4"; NOZZLE_BOTTOM_RAD=2' - 1 7/8"; NOZZLE_HEIGHT=7' - 11"; NOZZLE_HEIGHT/7*2=1' - 11 3/4"; NOZZLE_SIZE=36' - 0"; NOZZLE_TOP_OD=4' - 10"; NOZZLE_TOP_RAD=2' - 5"; NOZZLE_WB/4=1' - 6"; NOZZLE_WB_OD=7' - 6"; NOZZLE_WB_RAD=3' - 9"; NOZZLE_WB_RAD-2"=3' - 7"; RO=6' - 7 1/8"; RO/2=3' - 3 9/16"; TRANSITION_TOP=11' - 10 1/4"; TYPE=1' - 0"; Type Comments=Vari-Plume Laboratory Exhaust Mixed-Flow High Pressure Inline Belt Drive With Isolation Box; UNIT_HEIGHT=7' - 3"; UNIT_HEIGHT*.75=5' - 5 1/4"; UNIT_OD=6' - 4 7/16"; UNIT_RADIUS=3' - 2 7/32"; UNIT_RADIUS*.6=2' - 10 13/32"; UNIT_RADIUS+4"=3' - 6 7/32"
- 540_QMXHPVP-36L-Isolation_Box: (A/2)+.25"=3' - 9 1/4"; (NOZZLE_HEIGHT-(NOZZLE_HEIGHT/8*2))/2=2' - 11 5/8"; (NOZZLE_WB_OD-NOZZLE_TOP_OD)/2=0' - 8"; A=7' - 6"; A/2=3' - 9"; B=19' - 11"; B/2=9' - 11 1/2"; C=9' - 3"; C/2=4' - 7 1/2"; E=7' - 1 3/8"; GA=0' - 0 1/8"; Model=QMXHPVP-Isolation Box; NOZZLE_BOTTOM_ID=4' - 3 3/4"; NOZZLE_BOTTOM_RAD=2' - 1 7/8"; NOZZLE_HEIGHT=7' - 11"; NOZZLE_HEIGHT/7*2=1' - 11 3/4"; NOZZLE_SIZE=36' - 0"; NOZZLE_TOP_OD=4' - 10"; NOZZLE_TOP_RAD=2' - 5"; NOZZLE_WB/4=1' - 6"; NOZZLE_WB_OD=7' - 6"; NOZZLE_WB_RAD=3' - 9"; NOZZLE_WB_RAD-2"=3' - 7"; RO=6' - 7 1/8"; RO/2=3' - 3 9/16"; TRANSITION_TOP=11' - 10 1/4"; TYPE=1' - 0"; Type Comments=Vari-Plume Laboratory Exhaust Mixed-Flow High Pressure Inline Belt Drive With Isolation Box; UNIT_HEIGHT=7' - 3"; UNIT_HEIGHT*.75=5' - 5 1/4"; UNIT_OD=6' - 4 7/16"; UNIT_RADIUS=3' - 2 7/32"; UNIT_RADIUS*.6=2' - 10 13/32"; UNIT_RADIUS+4"=3' - 6 7/32"
- 540_QMXHPVP-49H-Isolation_Box: (A/2)+.25"=3' - 9 1/4"; (NOZZLE_HEIGHT-(NOZZLE_HEIGHT/8*2))/2=3' - 5 1/4"; (NOZZLE_WB_OD-NOZZLE_TOP_OD)/2=0' - 6 1/4"; A=7' - 6"; A/2=3' - 9"; B=19' - 11"; B/2=9' - 11 1/2"; C=9' - 3"; C/2=4' - 7 1/2"; E=7' - 1 3/8"; GA=0' - 0 1/8"; Model=QMXHPVP-Isolation Box; NOZZLE_BOTTOM_ID=5' - 9 3/8"; NOZZLE_BOTTOM_RAD=2' - 10 11/16"; NOZZLE_HEIGHT=9' - 2"; NOZZLE_HEIGHT/7*2=2' - 3 1/2"; NOZZLE_SIZE=49' - 0"; NOZZLE_TOP_OD=6' - 4"; NOZZLE_TOP_RAD=3' - 2"; NOZZLE_WB/4=1' - 8 3/16"; NOZZLE_WB_OD=8' - 5"; NOZZLE_WB_RAD=4' - 2 1/2"; NOZZLE_WB_RAD-2"=4' - 0 1/2"; RO=6' - 7 1/8"; RO/2=3' - 3 9/16"; TRANSITION_TOP=10' - 1 1/4"; TYPE=1' - 0"; Type Comments=Vari-Plume Laboratory Exhaust Mixed-Flow High Pressure Inline Belt Drive With Isolation Box; UNIT_HEIGHT=7' - 3"; UNIT_HEIGHT*.75=5' - 5 1/4"; UNIT_OD=6' - 4 7/16"; UNIT_RADIUS=3' - 2 7/32"; UNIT_RADIUS*.6=2' - 10 13/32"; UNIT_RADIUS+4"=3' - 6 7/32"
- 540_QMXHPVP-49L-Isolation_Box: (A/2)+.25"=3' - 9 1/4"; (NOZZLE_HEIGHT-(NOZZLE_HEIGHT/8*2))/2=3' - 5 1/4"; (NOZZLE_WB_OD-NOZZLE_TOP_OD)/2=0' - 6 1/4"; A=7' - 6"; A/2=3' - 9"; B=19' - 11"; B/2=9' - 11 1/2"; C=9' - 3"; C/2=4' - 7 1/2"; E=7' - 1 3/8"; GA=0' - 0 1/8"; Model=QMXHPVP-Isolation Box; NOZZLE_BOTTOM_ID=5' - 9 3/8"; NOZZLE_BOTTOM_RAD=2' - 10 11/16"; NOZZLE_HEIGHT=9' - 2"; NOZZLE_HEIGHT/7*2=2' - 3 1/2"; NOZZLE_SIZE=49' - 0"; NOZZLE_TOP_OD=6' - 4"; NOZZLE_TOP_RAD=3' - 2"; NOZZLE_WB/4=1' - 8 3/16"; NOZZLE_WB_OD=8' - 5"; NOZZLE_WB_RAD=4' - 2 1/2"; NOZZLE_WB_RAD-2"=4' - 0 1/2"; RO=6' - 7 1/8"; RO/2=3' - 3 9/16"; TRANSITION_TOP=10' - 1 1/4"; TYPE=1' - 0"; Type Comments=Vari-Plume Laboratory Exhaust Mixed-Flow High Pressure Inline Belt Drive With Isolation Box; UNIT_HEIGHT=7' - 3"; UNIT_HEIGHT*.75=5' - 5 1/4"; UNIT_OD=6' - 4 7/16"; UNIT_RADIUS=3' - 2 7/32"; UNIT_RADIUS*.6=2' - 10 13/32"; UNIT_RADIUS+4"=3' - 6 7/32"
- 600_QMXHPVP-36H-Isolation_Box: (A/2)+.25"=4' - 2 3/4"; (NOZZLE_HEIGHT-(NOZZLE_HEIGHT/8*2))/2=2' - 11 5/8"; (NOZZLE_WB_OD-NOZZLE_TOP_OD)/2=0' - 8"; A=8' - 5"; A/2=4' - 2 1/2"; B=21' - 11"; B/2=10' - 11 1/2"; C=10' - 2"; C/2=5' - 1"; E=7' - 10 3/8"; GA=0' - 0 3/16"; Model=QMXHPVP-Isolation Box; NOZZLE_BOTTOM_ID=4' - 3 3/4"; NOZZLE_BOTTOM_RAD=2' - 1 7/8"; NOZZLE_HEIGHT=7' - 11"; NOZZLE_HEIGHT/7*2=1' - 11 3/4"; NOZZLE_SIZE=36' - 0"; NOZZLE_TOP_OD=4' - 10"; NOZZLE_TOP_RAD=2' - 5"; NOZZLE_WB/4=1' - 6"; NOZZLE_WB_OD=7' - 6"; NOZZLE_WB_RAD=3' - 9"; NOZZLE_WB_RAD-2"=3' - 7"; RO=7' - 4 1/16"; RO/2=3' - 8 1/32"; TRANSITION_TOP=14' - 2 3/4"; TYPE=1' - 0"; Type Comments=Vari-Plume Laboratory Exhaust Mixed-Flow High Pressure Inline Belt Drive With Isolation Box; UNIT_HEIGHT=7' - 11 1/2"; UNIT_HEIGHT*.75=5' - 11 5/8"; UNIT_OD=7' - 0 7/8"; UNIT_RADIUS=3' - 6 7/16"; UNIT_RADIUS*.6=3' - 2 3/16"; UNIT_RADIUS+4"=3' - 10 7/16"
- 600_QMXHPVP-36L-Isolation_Box: (A/2)+.25"=4' - 2 3/4"; (NOZZLE_HEIGHT-(NOZZLE_HEIGHT/8*2))/2=2' - 11 5/8"; (NOZZLE_WB_OD-NOZZLE_TOP_OD)/2=0' - 8"; A=8' - 5"; A/2=4' - 2 1/2"; B=21' - 11"; B/2=10' - 11 1/2"; C=10' - 2"; C/2=5' - 1"; E=7' - 10 3/8"; GA=0' - 0 3/16"; Model=QMXHPVP-Isolation Box; NOZZLE_BOTTOM_ID=4' - 3 3/4"; NOZZLE_BOTTOM_RAD=2' - 1 7/8"; NOZZLE_HEIGHT=7' - 11"; NOZZLE_HEIGHT/7*2=1' - 11 3/4"; NOZZLE_SIZE=36' - 0"; NOZZLE_TOP_OD=4' - 10"; NOZZLE_TOP_RAD=2' - 5"; NOZZLE_WB/4=1' - 6"; NOZZLE_WB_OD=7' - 6"; NOZZLE_WB_RAD=3' - 9"; NOZZLE_WB_RAD-2"=3' - 7"; RO=7' - 4 1/16"; RO/2=3' - 8 1/32"; TRANSITION_TOP=14' - 2 3/4"; TYPE=1' - 0"; Type Comments=Vari-Plume Laboratory Exhaust Mixed-Flow High Pressure Inline Belt Drive With Isolation Box; UNIT_HEIGHT=7' - 11 1/2"; UNIT_HEIGHT*.75=5' - 11 5/8"; UNIT_OD=7' - 0 7/8"; UNIT_RADIUS=3' - 6 7/16"; UNIT_RADIUS*.6=3' - 2 3/16"; UNIT_RADIUS+4"=3' - 10 7/16"
- 600_QMXHPVP-49H-Isolation_Box: (A/2)+.25"=4' - 2 3/4"; (NOZZLE_HEIGHT-(NOZZLE_HEIGHT/8*2))/2=3' - 5 1/4"; (NOZZLE_WB_OD-NOZZLE_TOP_OD)/2=0' - 6 1/4"; A=8' - 5"; A/2=4' - 2 1/2"; B=21' - 11"; B/2=10' - 11 1/2"; C=10' - 2"; C/2=5' - 1"; E=7' - 10 3/8"; GA=0' - 0 3/16"; Model=QMXHPVP-Isolation Box; NOZZLE_BOTTOM_ID=5' - 9 3/8"; NOZZLE_BOTTOM_RAD=2' - 10 11/16"; NOZZLE_HEIGHT=9' - 2"; NOZZLE_HEIGHT/7*2=2' - 3 1/2"; NOZZLE_SIZE=49' - 0"; NOZZLE_TOP_OD=6' - 4"; NOZZLE_TOP_RAD=3' - 2"; NOZZLE_WB/4=1' - 8 3/16"; NOZZLE_WB_OD=8' - 5"; NOZZLE_WB_RAD=4' - 2 1/2"; NOZZLE_WB_RAD-2"=4' - 0 1/2"; RO=7' - 4 1/16"; RO/2=3' - 8 1/32"; TRANSITION_TOP=12' - 4 3/4"; TYPE=1' - 0"; Type Comments=Vari-Plume Laboratory Exhaust Mixed-Flow High Pressure Inline Belt Drive With Isolation Box; UNIT_HEIGHT=7' - 11 1/2"; UNIT_HEIGHT*.75=5' - 11 5/8"; UNIT_OD=7' - 0 7/8"; UNIT_RADIUS=3' - 6 7/16"; UNIT_RADIUS*.6=3' - 2 3/16"; UNIT_RADIUS+4"=3' - 10 7/16"
- 600_QMXHPVP-49L-Isolation_Box: (A/2)+.25"=4' - 2 3/4"; (NOZZLE_HEIGHT-(NOZZLE_HEIGHT/8*2))/2=3' - 5 1/4"; (NOZZLE_WB_OD-NOZZLE_TOP_OD)/2=0' - 6 1/4"; A=8' - 5"; A/2=4' - 2 1/2"; B=21' - 11"; B/2=10' - 11 1/2"; C=10' - 2"; C/2=5' - 1"; E=7' - 10 3/8"; GA=0' - 0 3/16"; Model=QMXHPVP-Isolation Box; NOZZLE_BOTTOM_ID=5' - 9 3/8"; NOZZLE_BOTTOM_RAD=2' - 10 11/16"; NOZZLE_HEIGHT=9' - 2"; NOZZLE_HEIGHT/7*2=2' - 3 1/2"; NOZZLE_SIZE=49' - 0"; NOZZLE_TOP_OD=6' - 4"; NOZZLE_TOP_RAD=3' - 2"; NOZZLE_WB/4=1' - 8 3/16"; NOZZLE_WB_OD=8' - 5"; NOZZLE_WB_RAD=4' - 2 1/2"; NOZZLE_WB_RAD-2"=4' - 0 1/2"; RO=7' - 4 1/16"; RO/2=3' - 8 1/32"; TRANSITION_TOP=12' - 4 3/4"; TYPE=1' - 0"; Type Comments=Vari-Plume Laboratory Exhaust Mixed-Flow High Pressure Inline Belt Drive With Isolation Box; UNIT_HEIGHT=7' - 11 1/2"; UNIT_HEIGHT*.75=5' - 11 5/8"; UNIT_OD=7' - 0 7/8"; UNIT_RADIUS=3' - 6 7/16"; UNIT_RADIUS*.6=3' - 2 3/16"; UNIT_RADIUS+4"=3' - 10 7/16"
- 90_QMXHPVP-9H-Isolation_Box: (A/2)+.25"=1' - 2 1/4"; (NOZZLE_HEIGHT-(NOZZLE_HEIGHT/8*2))/2=0' - 10 1/2"; (NOZZLE_WB_OD-NOZZLE_TOP_OD)/2=0' - 2 3/8"; A=2' - 4"; A/2=1' - 2"; B=5' - 5"; B/2=2' - 8 1/2"; C=2' - 6"; C/2=1' - 3"; E=2' - 3 3/16"; GA=0' - 0 3/32"; Model=QMXHPVP-Isolation Box; NOZZLE_BOTTOM_ID=1' - 0 13/16"; NOZZLE_BOTTOM_RAD=0' - 6 13/32"; NOZZLE_HEIGHT=2' - 4"; NOZZLE_HEIGHT/7*2=0' - 7"; NOZZLE_SIZE=9' - 0"; NOZZLE_TOP_OD=1' - 1 1/2"; NOZZLE_TOP_RAD=0' - 6 3/4"; NOZZLE_WB/4=0' - 4 19/32"; NOZZLE_WB_OD=1' - 11"; NOZZLE_WB_RAD=0' - 11 1/2"; NOZZLE_WB_RAD-2"=0' - 9 1/2"; RO=1' - 9"; RO/2=0' - 10 1/2"; TRANSITION_TOP=3' - 1 1/16"; TYPE=1' - 0"; Type Comments=Vari-Plume Laboratory Exhaust Mixed-Flow High Pressure Inline Belt Drive With Isolation Box; UNIT_HEIGHT=1' - 7 7/8"; UNIT_HEIGHT*.75=1' - 2 29/32"; UNIT_OD=1' - 0 13/16"; UNIT_RADIUS=0' - 6 13/32"; UNIT_RADIUS*.6=0' - 5 25/32"; UNIT_RADIUS+4"=0' - 10 13/32"
- 90_QMXHPVP-9L-Isolation_Box: (A/2)+.25"=1' - 2 1/4"; (NOZZLE_HEIGHT-(NOZZLE_HEIGHT/8*2))/2=0' - 10 1/2"; (NOZZLE_WB_OD-NOZZLE_TOP_OD)/2=0' - 2 3/8"; A=2' - 4"; A/2=1' - 2"; B=5' - 5"; B/2=2' - 8 1/2"; C=2' - 6"; C/2=1' - 3"; E=2' - 3 3/16"; GA=0' - 0 3/32"; Model=QMXHPVP-Isolation Box; NOZZLE_BOTTOM_ID=1' - 0 13/16"; NOZZLE_BOTTOM_RAD=0' - 6 13/32"; NOZZLE_HEIGHT=2' - 4"; NOZZLE_HEIGHT/7*2=0' - 7"; NOZZLE_SIZE=9' - 0"; NOZZLE_TOP_OD=1' - 1 1/2"; NOZZLE_TOP_RAD=0' - 6 3/4"; NOZZLE_WB/4=0' - 4 19/32"; NOZZLE_WB_OD=1' - 11"; NOZZLE_WB_RAD=0' - 11 1/2"; NOZZLE_WB_RAD-2"=0' - 9 1/2"; RO=1' - 9"; RO/2=0' - 10 1/2"; TRANSITION_TOP=3' - 1 1/16"; TYPE=1' - 0"; Type Comments=Vari-Plume Laboratory Exhaust Mixed-Flow High Pressure Inline Belt Drive With Isolation Box; UNIT_HEIGHT=1' - 7 7/8"; UNIT_HEIGHT*.75=1' - 2 29/32"; UNIT_OD=1' - 0 13/16"; UNIT_RADIUS=0' - 6 13/32"; UNIT_RADIUS*.6=0' - 5 25/32"; UNIT_RADIUS+4"=0' - 10 13/32"
- 490_QMXHPVP-49L-Isolation_Box: (A/2)+.25"=3' - 4 1/4"; (NOZZLE_HEIGHT-(NOZZLE_HEIGHT/8*2))/2=3' - 5 1/4"; (NOZZLE_WB_OD-NOZZLE_TOP_OD)/2=0' - 6 1/4"; A=6' - 8"; A/2=3' - 4"; B=18' - 3"; B/2=9' - 1 1/2"; C=8' - 7"; C/2=4' - 3 1/2"; E=6' - 6 1/2"; GA=0' - 0 1/8"; Model=QMXHPVP-Isolation Box; NOZZLE_BOTTOM_ID=5' - 9 3/8"; NOZZLE_BOTTOM_RAD=2' - 10 11/16"; NOZZLE_HEIGHT=9' - 2"; NOZZLE_HEIGHT/7*2=2' - 3 1/2"; NOZZLE_SIZE=49' - 0"; NOZZLE_TOP_OD=6' - 4"; NOZZLE_TOP_RAD=3' - 2"; NOZZLE_WB/4=1' - 8 3/16"; NOZZLE_WB_OD=8' - 5"; NOZZLE_WB_RAD=4' - 2 1/2"; NOZZLE_WB_RAD-2"=4' - 0 1/2"; RO=6' - 0 1/4"; RO/2=3' - 0 1/8"; TRANSITION_TOP=8' - 0 3/4"; TYPE=1' - 0"; Type Comments=Vari-Plume Laboratory Exhaust Mixed-Flow High Pressure Inline Belt Drive With Isolation Box; UNIT_HEIGHT=6' - 8 1/2"; UNIT_HEIGHT*.75=5' - 0 3/8"; UNIT_OD=5' - 9 3/8"; UNIT_RADIUS=2' - 10 11/16"; UNIT_RADIUS*.6=2' - 7 7/32"; UNIT_RADIUS+4"=3' - 2 11/16"
- 490_QMXVP-49H-Isolation_Box: (A/2)+.25"=3' - 4 1/4"; (NOZZLE_HEIGHT-(NOZZLE_HEIGHT/8*2))/2=3' - 5 1/4"; (NOZZLE_WB_OD-NOZZLE_TOP_OD)/2=0' - 6 1/4"; A=6' - 8"; A/2=3' - 4"; B=18' - 3"; B/2=9' - 1 1/2"; C=8' - 7"; C/2=4' - 3 1/2"; E=6' - 6 1/2"; GA=0' - 0 1/8"; Model=QMXVP-Isolation Box; NOZZLE_BOTTOM_ID=5' - 9 3/8"; NOZZLE_BOTTOM_RAD=2' - 10 11/16"; NOZZLE_HEIGHT=9' - 2"; NOZZLE_HEIGHT/7*2=2' - 3 1/2"; NOZZLE_SIZE=49' - 0"; NOZZLE_TOP_OD=6' - 4"; NOZZLE_TOP_RAD=3' - 2"; NOZZLE_WB/4=1' - 8 3/16"; NOZZLE_WB_OD=8' - 5"; NOZZLE_WB_RAD=4' - 2 1/2"; NOZZLE_WB_RAD-2"=4' - 0 1/2"; RO=6' - 0 1/4"; RO/2=3' - 0 1/8"; TRANSITION_TOP=8' - 0 3/4"; TYPE=0' - 0"; Type Comments=Vari-Plume Laboratory Exhaust Mixed-Flow Inline Belt Drive With Isolation Box; UNIT_HEIGHT=6' - 8 1/2"; UNIT_HEIGHT*.75=5' - 0 3/8"; UNIT_OD=5' - 9 3/8"; UNIT_RADIUS=2' - 10 11/16"; UNIT_RADIUS*.6=2' - 7 7/32"; UNIT_RADIUS+4"=3' - 2 11/16"
- 490_QMXVP-49L-Isolation_Box: (A/2)+.25"=3' - 4 1/4"; (NOZZLE_HEIGHT-(NOZZLE_HEIGHT/8*2))/2=3' - 5 1/4"; (NOZZLE_WB_OD-NOZZLE_TOP_OD)/2=0' - 6 1/4"; A=6' - 8"; A/2=3' - 4"; B=18' - 3"; B/2=9' - 1 1/2"; C=8' - 7"; C/2=4' - 3 1/2"; E=6' - 6 1/2"; GA=0' - 0 1/8"; Model=QMXVP-Isolation Box; NOZZLE_BOTTOM_ID=5' - 9 3/8"; NOZZLE_BOTTOM_RAD=2' - 10 11/16"; NOZZLE_HEIGHT=9' - 2"; NOZZLE_HEIGHT/7*2=2' - 3 1/2"; NOZZLE_SIZE=49' - 0"; NOZZLE_TOP_OD=6' - 4"; NOZZLE_TOP_RAD=3' - 2"; NOZZLE_WB/4=1' - 8 3/16"; NOZZLE_WB_OD=8' - 5"; NOZZLE_WB_RAD=4' - 2 1/2"; NOZZLE_WB_RAD-2"=4' - 0 1/2"; RO=6' - 0 1/4"; RO/2=3' - 0 1/8"; TRANSITION_TOP=8' - 0 3/4"; TYPE=0' - 0"; Type Comments=Vari-Plume Laboratory Exhaust Mixed-Flow Inline Belt Drive With Isolation Box; UNIT_HEIGHT=6' - 8 1/2"; UNIT_HEIGHT*.75=5' - 0 3/8"; UNIT_OD=5' - 9 3/8"; UNIT_RADIUS=2' - 10 11/16"; UNIT_RADIUS*.6=2' - 7 7/32"; UNIT_RADIUS+4"=3' - 2 11/16"
- 202_QMXHPVP-21H-Isolation_Box: (A/2)+.25"=1' - 7 1/4"; (NOZZLE_HEIGHT-(NOZZLE_HEIGHT/8*2))/2=1' - 7 25/32"; (NOZZLE_WB_OD-NOZZLE_TOP_OD)/2=0' - 4 9/16"; A=3' - 2"; A/2=1' - 7"; B=8' - 8"; B/2=4' - 4"; C=4' - 2"; C/2=2' - 1"; E=3' - 0 15/16"; GA=0' - 0 3/32"; Model=QMXHPVP-Isolation Box; NOZZLE_BOTTOM_ID=2' - 4 3/4"; NOZZLE_BOTTOM_RAD=1' - 2 3/8"; NOZZLE_HEIGHT=4' - 4 3/4"; NOZZLE_HEIGHT/7*2=1' - 1 3/16"; NOZZLE_SIZE=21' - 0"; NOZZLE_TOP_OD=2' - 6 3/4"; NOZZLE_TOP_RAD=1' - 3 3/8"; NOZZLE_WB/4=0' - 9 13/16"; NOZZLE_WB_OD=4' - 1"; NOZZLE_WB_RAD=2' - 0 1/2"; NOZZLE_WB_RAD-2"=1' - 10 1/2"; RO=2' - 6 3/4"; RO/2=1' - 3 3/8"; TRANSITION_TOP=4' - 3 5/8"; TYPE=1' - 0"; Type Comments=Vari-Plume Laboratory Exhaust Mixed-Flow High Pressure Inline Belt Drive With Isolation Box; UNIT_HEIGHT=3' - 1 1/2"; UNIT_HEIGHT*.75=2' - 4 1/8"; UNIT_OD=2' - 4 3/4"; UNIT_RADIUS=1' - 2 3/8"; UNIT_RADIUS*.6=1' - 0 15/16"; UNIT_RADIUS+4"=1' - 6 3/8"
- 202_QMXHPVP-21L-Isolation_Box: (A/2)+.25"=1' - 7 1/4"; (NOZZLE_HEIGHT-(NOZZLE_HEIGHT/8*2))/2=1' - 7 25/32"; (NOZZLE_WB_OD-NOZZLE_TOP_OD)/2=0' - 4 9/16"; A=3' - 2"; A/2=1' - 7"; B=8' - 8"; B/2=4' - 4"; C=4' - 2"; C/2=2' - 1"; E=3' - 0 15/16"; GA=0' - 0 3/32"; Model=QMXHPVP-Isolation Box; NOZZLE_BOTTOM_ID=2' - 4 3/4"; NOZZLE_BOTTOM_RAD=1' - 2 3/8"; NOZZLE_HEIGHT=4' - 4 3/4"; NOZZLE_HEIGHT/7*2=1' - 1 3/16"; NOZZLE_SIZE=21' - 0"; NOZZLE_TOP_OD=2' - 6 3/4"; NOZZLE_TOP_RAD=1' - 3 3/8"; NOZZLE_WB/4=0' - 9 13/16"; NOZZLE_WB_OD=4' - 1"; NOZZLE_WB_RAD=2' - 0 1/2"; NOZZLE_WB_RAD-2"=1' - 10 1/2"; RO=2' - 6 3/4"; RO/2=1' - 3 3/8"; TRANSITION_TOP=4' - 3 5/8"; TYPE=1' - 0"; Type Comments=Vari-Plume Laboratory Exhaust Mixed-Flow High Pressure Inline Belt Drive With Isolation Box; UNIT_HEIGHT=3' - 1 1/2"; UNIT_HEIGHT*.75=2' - 4 1/8"; UNIT_OD=2' - 4 3/4"; UNIT_RADIUS=1' - 2 3/8"; UNIT_RADIUS*.6=1' - 0 15/16"; UNIT_RADIUS+4"=1' - 6 3/8"
- 202_QMXVP-21H-Isolation_Box: (A/2)+.25"=1' - 7 1/4"; (NOZZLE_HEIGHT-(NOZZLE_HEIGHT/8*2))/2=1' - 7 25/32"; (NOZZLE_WB_OD-NOZZLE_TOP_OD)/2=0' - 4 9/16"; A=3' - 2"; A/2=1' - 7"; B=8' - 8"; B/2=4' - 4"; C=4' - 2"; C/2=2' - 1"; E=3' - 0 15/16"; GA=0' - 0 3/32"; Model=QMXVP-Isolation Box; NOZZLE_BOTTOM_ID=2' - 4 3/4"; NOZZLE_BOTTOM_RAD=1' - 2 3/8"; NOZZLE_HEIGHT=4' - 4 3/4"; NOZZLE_HEIGHT/7*2=1' - 1 3/16"; NOZZLE_SIZE=21' - 0"; NOZZLE_TOP_OD=2' - 6 3/4"; NOZZLE_TOP_RAD=1' - 3 3/8"; NOZZLE_WB/4=0' - 9 13/16"; NOZZLE_WB_OD=4' - 1"; NOZZLE_WB_RAD=2' - 0 1/2"; NOZZLE_WB_RAD-2"=1' - 10 1/2"; RO=2' - 6 3/4"; RO/2=1' - 3 3/8"; TRANSITION_TOP=4' - 3 5/8"; TYPE=0' - 0"; Type Comments=Vari-Plume Laboratory Exhaust Mixed-Flow Inline Belt Drive With Isolation Box; UNIT_HEIGHT=3' - 1 1/2"; UNIT_HEIGHT*.75=2' - 4 1/8"; UNIT_OD=2' - 4 3/4"; UNIT_RADIUS=1' - 2 3/8"; UNIT_RADIUS*.6=1' - 0 15/16"; UNIT_RADIUS+4"=1' - 6 3/8"
- 202_QMXVP-21L-Isolation_Box: (A/2)+.25"=1' - 7 1/4"; (NOZZLE_HEIGHT-(NOZZLE_HEIGHT/8*2))/2=1' - 7 25/32"; (NOZZLE_WB_OD-NOZZLE_TOP_OD)/2=0' - 4 9/16"; A=3' - 2"; A/2=1' - 7"; B=8' - 8"; B/2=4' - 4"; C=4' - 2"; C/2=2' - 1"; E=3' - 0 15/16"; GA=0' - 0 3/32"; Model=QMXVP-Isolation Box; NOZZLE_BOTTOM_ID=2' - 4 3/4"; NOZZLE_BOTTOM_RAD=1' - 2 3/8"; NOZZLE_HEIGHT=4' - 4 3/4"; NOZZLE_HEIGHT/7*2=1' - 1 3/16"; NOZZLE_SIZE=21' - 0"; NOZZLE_TOP_OD=2' - 6 3/4"; NOZZLE_TOP_RAD=1' - 3 3/8"; NOZZLE_WB/4=0' - 9 13/16"; NOZZLE_WB_OD=4' - 1"; NOZZLE_WB_RAD=2' - 0 1/2"; NOZZLE_WB_RAD-2"=1' - 10 1/2"; RO=2' - 6 3/4"; RO/2=1' - 3 3/8"; TRANSITION_TOP=4' - 3 5/8"; TYPE=0' - 0"; Type Comments=Vari-Plume Laboratory Exhaust Mixed-Flow Inline Belt Drive With Isolation Box; UNIT_HEIGHT=3' - 1 1/2"; UNIT_HEIGHT*.75=2' - 4 1/8"; UNIT_OD=2' - 4 3/4"; UNIT_RADIUS=1' - 2 3/8"; UNIT_RADIUS*.6=1' - 0 15/16"; UNIT_RADIUS+4"=1' - 6 3/8"
- 225_QMXHPVP-21H-Isolation_Box: (A/2)+.25"=1' - 9 1/4"; (NOZZLE_HEIGHT-(NOZZLE_HEIGHT/8*2))/2=1' - 7 25/32"; (NOZZLE_WB_OD-NOZZLE_TOP_OD)/2=0' - 4 9/16"; A=3' - 6"; A/2=1' - 9"; B=9' - 5"; B/2=4' - 8 1/2"; C=4' - 8"; C/2=2' - 4"; E=3' - 4 15/16"; GA=0' - 0 3/32"; Model=QMXHPVP-Isolation Box; NOZZLE_BOTTOM_ID=2' - 4 3/4"; NOZZLE_BOTTOM_RAD=1' - 2 3/8"; NOZZLE_HEIGHT=4' - 4 3/4"; NOZZLE_HEIGHT/7*2=1' - 1 3/16"; NOZZLE_SIZE=21' - 0"; NOZZLE_TOP_OD=2' - 6 3/4"; NOZZLE_TOP_RAD=1' - 3 3/8"; NOZZLE_WB/4=0' - 9 13/16"; NOZZLE_WB_OD=4' - 1"; NOZZLE_WB_RAD=2' - 0 1/2"; NOZZLE_WB_RAD-2"=1' - 10 1/2"; RO=2' - 10 3/4"; RO/2=1' - 5 3/8"; TRANSITION_TOP=5' - 1 1/8"; TYPE=1' - 0"; Type Comments=Vari-Plume Laboratory Exhaust Mixed-Flow High Pressure Inline Belt Drive With Isolation Box; UNIT_HEIGHT=3' - 5"; UNIT_HEIGHT*.75=2' - 6 3/4"; UNIT_OD=2' - 7 15/16"; UNIT_RADIUS=1' - 3 31/32"; UNIT_RADIUS*.6=1' - 2 3/8"; UNIT_RADIUS+4"=1' - 7 31/32"
- 225_QMXHPVP-21L-Isolation_Box: (A/2)+.25"=1' - 9 1/4"; (NOZZLE_HEIGHT-(NOZZLE_HEIGHT/8*2))/2=1' - 7 25/32"; (NOZZLE_WB_OD-NOZZLE_TOP_OD)/2=0' - 4 9/16"; A=3' - 6"; A/2=1' - 9"; B=9' - 5"; B/2=4' - 8 1/2"; C=4' - 8"; C/2=2' - 4"; E=3' - 4 15/16"; GA=0' - 0 3/32"; Model=QMXHPVP-Isolation Box; NOZZLE_BOTTOM_ID=2' - 4 3/4"; NOZZLE_BOTTOM_RAD=1' - 2 3/8"; NOZZLE_HEIGHT=4' - 4 3/4"; NOZZLE_HEIGHT/7*2=1' - 1 3/16"; NOZZLE_SIZE=21' - 0"; NOZZLE_TOP_OD=2' - 6 3/4"; NOZZLE_TOP_RAD=1' - 3 3/8"; NOZZLE_WB/4=0' - 9 13/16"; NOZZLE_WB_OD=4' - 1"; NOZZLE_WB_RAD=2' - 0 1/2"; NOZZLE_WB_RAD-2"=1' - 10 1/2"; RO=2' - 10 3/4"; RO/2=1' - 5 3/8"; TRANSITION_TOP=5' - 1 1/8"; TYPE=1' - 0"; Type Comments=Vari-Plume Laboratory Exhaust Mixed-Flow High Pressure Inline Belt Drive With Isolation Box; UNIT_HEIGHT=3' - 5"; UNIT_HEIGHT*.75=2' - 6 3/4"; UNIT_OD=2' - 7 15/16"; UNIT_RADIUS=1' - 3 31/32"; UNIT_RADIUS*.6=1' - 2 3/8"; UNIT_RADIUS+4"=1' - 7 31/32"
- 225_QMXVP-21H-Isolation_Box: (A/2)+.25"=1' - 9 1/4"; (NOZZLE_HEIGHT-(NOZZLE_HEIGHT/8*2))/2=1' - 7 25/32"; (NOZZLE_WB_OD-NOZZLE_TOP_OD)/2=0' - 4 9/16"; A=3' - 6"; A/2=1' - 9"; B=9' - 5"; B/2=4' - 8 1/2"; C=4' - 8"; C/2=2' - 4"; E=3' - 4 15/16"; GA=0' - 0 3/32"; Model=QMXVP-Isolation Box; NOZZLE_BOTTOM_ID=2' - 4 3/4"; NOZZLE_BOTTOM_RAD=1' - 2 3/8"; NOZZLE_HEIGHT=4' - 4 3/4"; NOZZLE_HEIGHT/7*2=1' - 1 3/16"; NOZZLE_SIZE=21' - 0"; NOZZLE_TOP_OD=2' - 6 3/4"; NOZZLE_TOP_RAD=1' - 3 3/8"; NOZZLE_WB/4=0' - 9 13/16"; NOZZLE_WB_OD=4' - 1"; NOZZLE_WB_RAD=2' - 0 1/2"; NOZZLE_WB_RAD-2"=1' - 10 1/2"; RO=2' - 10 3/4"; RO/2=1' - 5 3/8"; TRANSITION_TOP=5' - 1 1/8"; TYPE=0' - 0"; Type Comments=Vari-Plume Laboratory Exhaust Mixed-Flow Inline Belt Drive With Isolation Box; UNIT_HEIGHT=3' - 5"; UNIT_HEIGHT*.75=2' - 6 3/4"; UNIT_OD=2' - 7 15/16"; UNIT_RADIUS=1' - 3 31/32"; UNIT_RADIUS*.6=1' - 2 3/8"; UNIT_RADIUS+4"=1' - 7 31/32"
- 225_QMXVP-21L-Isolation_Box: (A/2)+.25"=1' - 9 1/4"; (NOZZLE_HEIGHT-(NOZZLE_HEIGHT/8*2))/2=1' - 7 25/32"; (NOZZLE_WB_OD-NOZZLE_TOP_OD)/2=0' - 4 9/16"; A=3' - 6"; A/2=1' - 9"; B=9' - 5"; B/2=4' - 8 1/2"; C=4' - 8"; C/2=2' - 4"; E=3' - 4 15/16"; GA=0' - 0 3/32"; Model=QMXVP-Isolation Box; NOZZLE_BOTTOM_ID=2' - 4 3/4"; NOZZLE_BOTTOM_RAD=1' - 2 3/8"; NOZZLE_HEIGHT=4' - 4 3/4"; NOZZLE_HEIGHT/7*2=1' - 1 3/16"; NOZZLE_SIZE=21' - 0"; NOZZLE_TOP_OD=2' - 6 3/4"; NOZZLE_TOP_RAD=1' - 3 3/8"; NOZZLE_WB/4=0' - 9 13/16"; NOZZLE_WB_OD=4' - 1"; NOZZLE_WB_RAD=2' - 0 1/2"; NOZZLE_WB_RAD-2"=1' - 10 1/2"; RO=2' - 10 3/4"; RO/2=1' - 5 3/8"; TRANSITION_TOP=5' - 1 1/8"; TYPE=0' - 0"; Type Comments=Vari-Plume Laboratory Exhaust Mixed-Flow Inline Belt Drive With Isolation Box; UNIT_HEIGHT=3' - 5"; UNIT_HEIGHT*.75=2' - 6 3/4"; UNIT_OD=2' - 7 15/16"; UNIT_RADIUS=1' - 3 31/32"; UNIT_RADIUS*.6=1' - 2 3/8"; UNIT_RADIUS+4"=1' - 7 31/32"
- 245_QMXHPVP-21H-Isolation_Box: (A/2)+.25"=1' - 10 1/4"; (NOZZLE_HEIGHT-(NOZZLE_HEIGHT/8*2))/2=1' - 7 25/32"; (NOZZLE_WB_OD-NOZZLE_TOP_OD)/2=0' - 4 9/16"; A=3' - 8"; A/2=1' - 10"; B=10' - 1"; B/2=5' - 0 1/2"; C=4' - 11"; C/2=2' - 5 1/2"; E=3' - 6 15/16"; GA=0' - 0 3/32"; Model=QMXHPVP-Isolation Box; NOZZLE_BOTTOM_ID=2' - 4 3/4"; NOZZLE_BOTTOM_RAD=1' - 2 3/8"; NOZZLE_HEIGHT=4' - 4 3/4"; NOZZLE_HEIGHT/7*2=1' - 1 3/16"; NOZZLE_SIZE=21' - 0"; NOZZLE_TOP_OD=2' - 6 3/4"; NOZZLE_TOP_RAD=1' - 3 3/8"; NOZZLE_WB/4=0' - 9 13/16"; NOZZLE_WB_OD=4' - 1"; NOZZLE_WB_RAD=2' - 0 1/2"; NOZZLE_WB_RAD-2"=1' - 10 1/2"; RO=3' - 0 3/4"; RO/2=1' - 6 3/8"; TRANSITION_TOP=5' - 9 11/16"; TYPE=1' - 0"; Type Comments=Vari-Plume Laboratory Exhaust Mixed-Flow High Pressure Inline Belt Drive With Isolation Box; UNIT_HEIGHT=3' - 8 1/2"; UNIT_HEIGHT*.75=2' - 9 3/8"; UNIT_OD=2' - 10 3/4"; UNIT_RADIUS=1' - 5 3/8"; UNIT_RADIUS*.6=1' - 3 5/8"; UNIT_RADIUS+4"=1' - 9 3/8"
- 245_QMXHPVP-21L-Isolation_Box: (A/2)+.25"=1' - 10 1/4"; (NOZZLE_HEIGHT-(NOZZLE_HEIGHT/8*2))/2=1' - 7 25/32"; (NOZZLE_WB_OD-NOZZLE_TOP_OD)/2=0' - 4 9/16"; A=3' - 8"; A/2=1' - 10"; B=10' - 1"; B/2=5' - 0 1/2"; C=4' - 11"; C/2=2' - 5 1/2"; E=3' - 6 15/16"; GA=0' - 0 3/32"; Model=QMXHPVP-Isolation Box; NOZZLE_BOTTOM_ID=2' - 4 3/4"; NOZZLE_BOTTOM_RAD=1' - 2 3/8"; NOZZLE_HEIGHT=4' - 4 3/4"; NOZZLE_HEIGHT/7*2=1' - 1 3/16"; NOZZLE_SIZE=21' - 0"; NOZZLE_TOP_OD=2' - 6 3/4"; NOZZLE_TOP_RAD=1' - 3 3/8"; NOZZLE_WB/4=0' - 9 13/16"; NOZZLE_WB_OD=4' - 1"; NOZZLE_WB_RAD=2' - 0 1/2"; NOZZLE_WB_RAD-2"=1' - 10 1/2"; RO=3' - 0 3/4"; RO/2=1' - 6 3/8"; TRANSITION_TOP=5' - 9 11/16"; TYPE=1' - 0"; Type Comments=Vari-Plume Laboratory Exhaust Mixed-Flow High Pressure Inline Belt Drive With Isolation Box; UNIT_HEIGHT=3' - 8 1/2"; UNIT_HEIGHT*.75=2' - 9 3/8"; UNIT_OD=2' - 10 3/4"; UNIT_RADIUS=1' - 5 3/8"; UNIT_RADIUS*.6=1' - 3 5/8"; UNIT_RADIUS+4"=1' - 9 3/8"
- 245_QMXVP-21H-Isolation_Box: (A/2)+.25"=1' - 10 1/4"; (NOZZLE_HEIGHT-(NOZZLE_HEIGHT/8*2))/2=1' - 7 25/32"; (NOZZLE_WB_OD-NOZZLE_TOP_OD)/2=0' - 4 9/16"; A=3' - 8"; A/2=1' - 10"; B=10' - 1"; B/2=5' - 0 1/2"; C=4' - 11"; C/2=2' - 5 1/2"; E=3' - 6 15/16"; GA=0' - 0 3/32"; Model=QMXVP-Isolation Box; NOZZLE_BOTTOM_ID=2' - 4 3/4"; NOZZLE_BOTTOM_RAD=1' - 2 3/8"; NOZZLE_HEIGHT=4' - 4 3/4"; NOZZLE_HEIGHT/7*2=1' - 1 3/16"; NOZZLE_SIZE=21' - 0"; NOZZLE_TOP_OD=2' - 6 3/4"; NOZZLE_TOP_RAD=1' - 3 3/8"; NOZZLE_WB/4=0' - 9 13/16"; NOZZLE_WB_OD=4' - 1"; NOZZLE_WB_RAD=2' - 0 1/2"; NOZZLE_WB_RAD-2"=1' - 10 1/2"; RO=3' - 0 3/4"; RO/2=1' - 6 3/8"; TRANSITION_TOP=5' - 9 11/16"; TYPE=0' - 0"; Type Comments=Vari-Plume Laboratory Exhaust Mixed-Flow Inline Belt Drive With Isolation Box; UNIT_HEIGHT=3' - 8 1/2"; UNIT_HEIGHT*.75=2' - 9 3/8"; UNIT_OD=2' - 10 3/4"; UNIT_RADIUS=1' - 5 3/8"; UNIT_RADIUS*.6=1' - 3 5/8"; UNIT_RADIUS+4"=1' - 9 3/8"
- 245_QMXVP-21L-Isolation_Box: (A/2)+.25"=1' - 10 1/4"; (NOZZLE_HEIGHT-(NOZZLE_HEIGHT/8*2))/2=1' - 7 25/32"; (NOZZLE_WB_OD-NOZZLE_TOP_OD)/2=0' - 4 9/16"; A=3' - 8"; A/2=1' - 10"; B=10' - 1"; B/2=5' - 0 1/2"; C=4' - 11"; C/2=2' - 5 1/2"; E=3' - 6 15/16"; GA=0' - 0 3/32"; Model=QMXVP-Isolation Box; NOZZLE_BOTTOM_ID=2' - 4 3/4"; NOZZLE_BOTTOM_RAD=1' - 2 3/8"; NOZZLE_HEIGHT=4' - 4 3/4"; NOZZLE_HEIGHT/7*2=1' - 1 3/16"; NOZZLE_SIZE=21' - 0"; NOZZLE_TOP_OD=2' - 6 3/4"; NOZZLE_TOP_RAD=1' - 3 3/8"; NOZZLE_WB/4=0' - 9 13/16"; NOZZLE_WB_OD=4' - 1"; NOZZLE_WB_RAD=2' - 0 1/2"; NOZZLE_WB_RAD-2"=1' - 10 1/2"; RO=3' - 0 3/4"; RO/2=1' - 6 3/8"; TRANSITION_TOP=5' - 9 11/16"; TYPE=0' - 0"; Type Comments=Vari-Plume Laboratory Exhaust Mixed-Flow Inline Belt Drive With Isolation Box; UNIT_HEIGHT=3' - 8 1/2"; UNIT_HEIGHT*.75=2' - 9 3/8"; UNIT_OD=2' - 10 3/4"; UNIT_RADIUS=1' - 5 3/8"; UNIT_RADIUS*.6=1' - 3 5/8"; UNIT_RADIUS+4"=1' - 9 3/8"
- 270_QMXHPVP-21H-Isolation_Box: (A/2)+.25"=2' - 0 1/4"; (NOZZLE_HEIGHT-(NOZZLE_HEIGHT/8*2))/2=1' - 7 25/32"; (NOZZLE_WB_OD-NOZZLE_TOP_OD)/2=0' - 4 9/16"; A=4' - 0"; A/2=2' - 0"; B=10' - 8"; B/2=5' - 4"; C=5' - 3"; C/2=2' - 7 1/2"; E=3' - 10 15/16"; GA=0' - 0 3/32"; Model=QMXHPVP-Isolation Box; NOZZLE_BOTTOM_ID=2' - 4 3/4"; NOZZLE_BOTTOM_RAD=1' - 2 3/8"; NOZZLE_HEIGHT=4' - 4 3/4"; NOZZLE_HEIGHT/7*2=1' - 1 3/16"; NOZZLE_SIZE=21' - 0"; NOZZLE_TOP_OD=2' - 6 3/4"; NOZZLE_TOP_RAD=1' - 3 3/8"; NOZZLE_WB/4=0' - 9 13/16"; NOZZLE_WB_OD=4' - 1"; NOZZLE_WB_RAD=2' - 0 1/2"; NOZZLE_WB_RAD-2"=1' - 10 1/2"; RO=3' - 4 3/4"; RO/2=1' - 8 3/8"; TRANSITION_TOP=6' - 7 3/16"; TYPE=1' - 0"; Type Comments=Vari-Plume Laboratory Exhaust Mixed-Flow High Pressure Inline Belt Drive With Isolation Box; UNIT_HEIGHT=3' - 11"; UNIT_HEIGHT*.75=2' - 11 1/4"; UNIT_OD=3' - 2 5/16"; UNIT_RADIUS=1' - 7 5/32"; UNIT_RADIUS*.6=1' - 5 1/4"; UNIT_RADIUS+4"=1' - 11 5/32"
- 270_QMXHPVP-21L-Isolation_Box: (A/2)+.25"=2' - 0 1/4"; (NOZZLE_HEIGHT-(NOZZLE_HEIGHT/8*2))/2=1' - 7 25/32"; (NOZZLE_WB_OD-NOZZLE_TOP_OD)/2=0' - 4 9/16"; A=4' - 0"; A/2=2' - 0"; B=10' - 8"; B/2=5' - 4"; C=5' - 3"; C/2=2' - 7 1/2"; E=3' - 10 15/16"; GA=0' - 0 3/32"; Model=QMXHPVP-Isolation Box; NOZZLE_BOTTOM_ID=2' - 4 3/4"; NOZZLE_BOTTOM_RAD=1' - 2 3/8"; NOZZLE_HEIGHT=4' - 4 3/4"; NOZZLE_HEIGHT/7*2=1' - 1 3/16"; NOZZLE_SIZE=21' - 0"; NOZZLE_TOP_OD=2' - 6 3/4"; NOZZLE_TOP_RAD=1' - 3 3/8"; NOZZLE_WB/4=0' - 9 13/16"; NOZZLE_WB_OD=4' - 1"; NOZZLE_WB_RAD=2' - 0 1/2"; NOZZLE_WB_RAD-2"=1' - 10 1/2"; RO=3' - 4 3/4"; RO/2=1' - 8 3/8"; TRANSITION_TOP=6' - 7 3/16"; TYPE=1' - 0"; Type Comments=Vari-Plume Laboratory Exhaust Mixed-Flow High Pressure Inline Belt Drive With Isolation Box; UNIT_HEIGHT=3' - 11"; UNIT_HEIGHT*.75=2' - 11 1/4"; UNIT_OD=3' - 2 5/16"; UNIT_RADIUS=1' - 7 5/32"; UNIT_RADIUS*.6=1' - 5 1/4"; UNIT_RADIUS+4"=1' - 11 5/32"
- 270_QMXVP-21H-Isolation_Box: (A/2)+.25"=2' - 0 1/4"; (NOZZLE_HEIGHT-(NOZZLE_HEIGHT/8*2))/2=1' - 7 25/32"; (NOZZLE_WB_OD-NOZZLE_TOP_OD)/2=0' - 4 9/16"; A=4' - 0"; A/2=2' - 0"; B=10' - 8"; B/2=5' - 4"; C=5' - 3"; C/2=2' - 7 1/2"; E=3' - 10 15/16"; GA=0' - 0 3/32"; Model=QMXVP-Isolation Box; NOZZLE_BOTTOM_ID=2' - 4 3/4"; NOZZLE_BOTTOM_RAD=1' - 2 3/8"; NOZZLE_HEIGHT=4' - 4 3/4"; NOZZLE_HEIGHT/7*2=1' - 1 3/16"; NOZZLE_SIZE=21' - 0"; NOZZLE_TOP_OD=2' - 6 3/4"; NOZZLE_TOP_RAD=1' - 3 3/8"; NOZZLE_WB/4=0' - 9 13/16"; NOZZLE_WB_OD=4' - 1"; NOZZLE_WB_RAD=2' - 0 1/2"; NOZZLE_WB_RAD-2"=1' - 10 1/2"; RO=3' - 4 3/4"; RO/2=1' - 8 3/8"; TRANSITION_TOP=6' - 7 3/16"; TYPE=0' - 0"; Type Comments=Vari-Plume Laboratory Exhaust Mixed-Flow Inline Belt Drive With Isolation Box; UNIT_HEIGHT=3' - 11"; UNIT_HEIGHT*.75=2' - 11 1/4"; UNIT_OD=3' - 2 5/16"; UNIT_RADIUS=1' - 7 5/32"; UNIT_RADIUS*.6=1' - 5 1/4"; UNIT_RADIUS+4"=1' - 11 5/32"
- 270_QMXVP-21L-Isolation_Box: (A/2)+.25"=2' - 0 1/4"; (NOZZLE_HEIGHT-(NOZZLE_HEIGHT/8*2))/2=1' - 7 25/32"; (NOZZLE_WB_OD-NOZZLE_TOP_OD)/2=0' - 4 9/16"; A=4' - 0"; A/2=2' - 0"; B=10' - 8"; B/2=5' - 4"; C=5' - 3"; C/2=2' - 7 1/2"; E=3' - 10 15/16"; GA=0' - 0 3/32"; Model=QMXVP-Isolation Box; NOZZLE_BOTTOM_ID=2' - 4 3/4"; NOZZLE_BOTTOM_RAD=1' - 2 3/8"; NOZZLE_HEIGHT=4' - 4 3/4"; NOZZLE_HEIGHT/7*2=1' - 1 3/16"; NOZZLE_SIZE=21' - 0"; NOZZLE_TOP_OD=2' - 6 3/4"; NOZZLE_TOP_RAD=1' - 3 3/8"; NOZZLE_WB/4=0' - 9 13/16"; NOZZLE_WB_OD=4' - 1"; NOZZLE_WB_RAD=2' - 0 1/2"; NOZZLE_WB_RAD-2"=1' - 10 1/2"; RO=3' - 4 3/4"; RO/2=1' - 8 3/8"; TRANSITION_TOP=6' - 7 3/16"; TYPE=0' - 0"; Type Comments=Vari-Plume Laboratory Exhaust Mixed-Flow Inline Belt Drive With Isolation Box; UNIT_HEIGHT=3' - 11"; UNIT_HEIGHT*.75=2' - 11 1/4"; UNIT_OD=3' - 2 5/16"; UNIT_RADIUS=1' - 7 5/32"; UNIT_RADIUS*.6=1' - 5 1/4"; UNIT_RADIUS+4"=1' - 11 5/32"
- 300_QMXHPVP-21H-Isolation_Box: (A/2)+.25"=2' - 2 1/4"; (NOZZLE_HEIGHT-(NOZZLE_HEIGHT/8*2))/2=1' - 7 25/32"; (NOZZLE_WB_OD-NOZZLE_TOP_OD)/2=0' - 4 9/16"; A=4' - 4"; A/2=2' - 2"; B=12' - 4"; B/2=6' - 2"; C=5' - 7"; C/2=2' - 9 1/2"; E=4' - 2 15/16"; GA=0' - 0 3/32"; Model=QMXHPVP-Isolation Box; NOZZLE_BOTTOM_ID=2' - 4 3/4"; NOZZLE_BOTTOM_RAD=1' - 2 3/8"; NOZZLE_HEIGHT=4' - 4 3/4"; NOZZLE_HEIGHT/7*2=1' - 1 3/16"; NOZZLE_SIZE=21' - 0"; NOZZLE_TOP_OD=2' - 6 3/4"; NOZZLE_TOP_RAD=1' - 3 3/8"; NOZZLE_WB/4=0' - 9 13/16"; NOZZLE_WB_OD=4' - 1"; NOZZLE_WB_RAD=2' - 0 1/2"; NOZZLE_WB_RAD-2"=1' - 10 1/2"; RO=3' - 8 3/4"; RO/2=1' - 10 3/8"; TRANSITION_TOP=7' - 10 3/16"; TYPE=1' - 0"; Type Comments=Vari-Plume Laboratory Exhaust Mixed-Flow High Pressure Inline Belt Drive With Isolation Box; UNIT_HEIGHT=4' - 6"; UNIT_HEIGHT*.75=3' - 4 1/2"; UNIT_OD=3' - 6 1/2"; UNIT_RADIUS=1' - 9 1/4"; UNIT_RADIUS*.6=1' - 7 1/8"; UNIT_RADIUS+4"=2' - 1 1/4"
- 300_QMXHPVP-21L-Isolation_Box: (A/2)+.25"=2' - 2 1/4"; (NOZZLE_HEIGHT-(NOZZLE_HEIGHT/8*2))/2=1' - 7 25/32"; (NOZZLE_WB_OD-NOZZLE_TOP_OD)/2=0' - 4 9/16"; A=4' - 4"; A/2=2' - 2"; B=12' - 4"; B/2=6' - 2"; C=5' - 7"; C/2=2' - 9 1/2"; E=4' - 2 15/16"; GA=0' - 0 3/32"; Model=QMXHPVP-Isolation Box; NOZZLE_BOTTOM_ID=2' - 4 3/4"; NOZZLE_BOTTOM_RAD=1' - 2 3/8"; NOZZLE_HEIGHT=4' - 4 3/4"; NOZZLE_HEIGHT/7*2=1' - 1 3/16"; NOZZLE_SIZE=21' - 0"; NOZZLE_TOP_OD=2' - 6 3/4"; NOZZLE_TOP_RAD=1' - 3 3/8"; NOZZLE_WB/4=0' - 9 13/16"; NOZZLE_WB_OD=4' - 1"; NOZZLE_WB_RAD=2' - 0 1/2"; NOZZLE_WB_RAD-2"=1' - 10 1/2"; RO=3' - 8 3/4"; RO/2=1' - 10 3/8"; TRANSITION_TOP=7' - 10 3/16"; TYPE=1' - 0"; Type Comments=Vari-Plume Laboratory Exhaust Mixed-Flow High Pressure Inline Belt Drive With Isolation Box; UNIT_HEIGHT=4' - 6"; UNIT_HEIGHT*.75=3' - 4 1/2"; UNIT_OD=3' - 6 1/2"; UNIT_RADIUS=1' - 9 1/4"; UNIT_RADIUS*.6=1' - 7 1/8"; UNIT_RADIUS+4"=2' - 1 1/4"
- 300_QMXVP-21H-Isolation_Box: (A/2)+.25"=2' - 2 1/4"; (NOZZLE_HEIGHT-(NOZZLE_HEIGHT/8*2))/2=1' - 7 25/32"; (NOZZLE_WB_OD-NOZZLE_TOP_OD)/2=0' - 4 9/16"; A=4' - 4"; A/2=2' - 2"; B=12' - 4"; B/2=6' - 2"; C=5' - 7"; C/2=2' - 9 1/2"; E=4' - 2 15/16"; GA=0' - 0 3/32"; Model=QMXVP-Isolation Box; NOZZLE_BOTTOM_ID=2' - 4 3/4"; NOZZLE_BOTTOM_RAD=1' - 2 3/8"; NOZZLE_HEIGHT=4' - 4 3/4"; NOZZLE_HEIGHT/7*2=1' - 1 3/16"; NOZZLE_SIZE=21' - 0"; NOZZLE_TOP_OD=2' - 6 3/4"; NOZZLE_TOP_RAD=1' - 3 3/8"; NOZZLE_WB/4=0' - 9 13/16"; NOZZLE_WB_OD=4' - 1"; NOZZLE_WB_RAD=2' - 0 1/2"; NOZZLE_WB_RAD-2"=1' - 10 1/2"; RO=3' - 8 3/4"; RO/2=1' - 10 3/8"; TRANSITION_TOP=7' - 10 3/16"; TYPE=0' - 0"; Type Comments=Vari-Plume Laboratory Exhaust Mixed-Flow Inline Belt Drive With Isolation Box; UNIT_HEIGHT=4' - 6"; UNIT_HEIGHT*.75=3' - 4 1/2"; UNIT_OD=3' - 6 1/2"; UNIT_RADIUS=1' - 9 1/4"; UNIT_RADIUS*.6=1' - 7 1/8"; UNIT_RADIUS+4"=2' - 1 1/4"
- 300_QMXVP-21L-Isolation_Box: (A/2)+.25"=2' - 2 1/4"; (NOZZLE_HEIGHT-(NOZZLE_HEIGHT/8*2))/2=1' - 7 25/32"; (NOZZLE_WB_OD-NOZZLE_TOP_OD)/2=0' - 4 9/16"; A=4' - 4"; A/2=2' - 2"; B=12' - 4"; B/2=6' - 2"; C=5' - 7"; C/2=2' - 9 1/2"; E=4' - 2 15/16"; GA=0' - 0 3/32"; Model=QMXVP-Isolation Box; NOZZLE_BOTTOM_ID=2' - 4 3/4"; NOZZLE_BOTTOM_RAD=1' - 2 3/8"; NOZZLE_HEIGHT=4' - 4 3/4"; NOZZLE_HEIGHT/7*2=1' - 1 3/16"; NOZZLE_SIZE=21' - 0"; NOZZLE_TOP_OD=2' - 6 3/4"; NOZZLE_TOP_RAD=1' - 3 3/8"; NOZZLE_WB/4=0' - 9 13/16"; NOZZLE_WB_OD=4' - 1"; NOZZLE_WB_RAD=2' - 0 1/2"; NOZZLE_WB_RAD-2"=1' - 10 1/2"; RO=3' - 8 3/4"; RO/2=1' - 10 3/8"; TRANSITION_TOP=7' - 10 3/16"; TYPE=0' - 0"; Type Comments=Vari-Plume Laboratory Exhaust Mixed-Flow Inline Belt Drive With Isolation Box; UNIT_HEIGHT=4' - 6"; UNIT_HEIGHT*.75=3' - 4 1/2"; UNIT_OD=3' - 6 1/2"; UNIT_RADIUS=1' - 9 1/4"; UNIT_RADIUS*.6=1' - 7 1/8"; UNIT_RADIUS+4"=2' - 1 1/4"
- 270_QMXHPVP-27H-Isolation_Box: (A/2)+.25"=2' - 0 1/4"; (NOZZLE_HEIGHT-(NOZZLE_HEIGHT/8*2))/2=1' - 10 3/4"; (NOZZLE_WB_OD-NOZZLE_TOP_OD)/2=0' - 5 11/32"; A=4' - 0"; A/2=2' - 0"; B=10' - 8"; B/2=5' - 4"; C=5' - 3"; C/2=2' - 7 1/2"; E=3' - 10 15/16"; GA=0' - 0 3/32"; Model=QMXHPVP-Isolation Box; NOZZLE_BOTTOM_ID=3' - 2 5/16"; NOZZLE_BOTTOM_RAD=1' - 7 5/32"; NOZZLE_HEIGHT=5' - 0 5/8"; NOZZLE_HEIGHT/7*2=1' - 3 5/32"; NOZZLE_SIZE=27' - 0"; NOZZLE_TOP_OD=3' - 3 11/16"; NOZZLE_TOP_RAD=1' - 7 27/32"; NOZZLE_WB/4=1' - 0 3/16"; NOZZLE_WB_OD=5' - 1"; NOZZLE_WB_RAD=2' - 6 1/2"; NOZZLE_WB_RAD-2"=2' - 4 1/2"; RO=3' - 4 3/4"; RO/2=1' - 8 3/8"; TRANSITION_TOP=5' - 2 1/4"; TYPE=1' - 0"; Type Comments=Vari-Plume Laboratory Exhaust Mixed-Flow High Pressure Inline Belt Drive With Isolation Box; UNIT_HEIGHT=3' - 11"; UNIT_HEIGHT*.75=2' - 11 1/4"; UNIT_OD=3' - 2 5/16"; UNIT_RADIUS=1' - 7 5/32"; UNIT_RADIUS*.6=1' - 5 1/4"; UNIT_RADIUS+4"=1' - 11 5/32"
- 270_QMXHPVP-27L-Isolation_Box: (A/2)+.25"=2' - 0 1/4"; (NOZZLE_HEIGHT-(NOZZLE_HEIGHT/8*2))/2=1' - 10 3/4"; (NOZZLE_WB_OD-NOZZLE_TOP_OD)/2=0' - 5 11/32"; A=4' - 0"; A/2=2' - 0"; B=10' - 8"; B/2=5' - 4"; C=5' - 3"; C/2=2' - 7 1/2"; E=3' - 10 15/16"; GA=0' - 0 3/32"; Model=QMXHPVP-Isolation Box; NOZZLE_BOTTOM_ID=3' - 2 5/16"; NOZZLE_BOTTOM_RAD=1' - 7 5/32"; NOZZLE_HEIGHT=5' - 0 5/8"; NOZZLE_HEIGHT/7*2=1' - 3 5/32"; NOZZLE_SIZE=27' - 0"; NOZZLE_TOP_OD=3' - 3 11/16"; NOZZLE_TOP_RAD=1' - 7 27/32"; NOZZLE_WB/4=1' - 0 3/16"; NOZZLE_WB_OD=5' - 1"; NOZZLE_WB_RAD=2' - 6 1/2"; NOZZLE_WB_RAD-2"=2' - 4 1/2"; RO=3' - 4 3/4"; RO/2=1' - 8 3/8"; TRANSITION_TOP=5' - 2 1/4"; TYPE=1' - 0"; Type Comments=Vari-Plume Laboratory Exhaust Mixed-Flow High Pressure Inline Belt Drive With Isolation Box; UNIT_HEIGHT=3' - 11"; UNIT_HEIGHT*.75=2' - 11 1/4"; UNIT_OD=3' - 2 5/16"; UNIT_RADIUS=1' - 7 5/32"; UNIT_RADIUS*.6=1' - 5 1/4"; UNIT_RADIUS+4"=1' - 11 5/32"
- 270_QMXVP-27H-Isolation_Box: (A/2)+.25"=2' - 0 1/4"; (NOZZLE_HEIGHT-(NOZZLE_HEIGHT/8*2))/2=1' - 10 3/4"; (NOZZLE_WB_OD-NOZZLE_TOP_OD)/2=0' - 5 11/32"; A=4' - 0"; A/2=2' - 0"; B=10' - 8"; B/2=5' - 4"; C=5' - 3"; C/2=2' - 7 1/2"; E=3' - 10 15/16"; GA=0' - 0 3/32"; Model=QMXVP-Isolation Box; NOZZLE_BOTTOM_ID=3' - 2 5/16"; NOZZLE_BOTTOM_RAD=1' - 7 5/32"; NOZZLE_HEIGHT=5' - 0 5/8"; NOZZLE_HEIGHT/7*2=1' - 3 5/32"; NOZZLE_SIZE=27' - 0"; NOZZLE_TOP_OD=3' - 3 11/16"; NOZZLE_TOP_RAD=1' - 7 27/32"; NOZZLE_WB/4=1' - 0 3/16"; NOZZLE_WB_OD=5' - 1"; NOZZLE_WB_RAD=2' - 6 1/2"; NOZZLE_WB_RAD-2"=2' - 4 1/2"; RO=3' - 4 3/4"; RO/2=1' - 8 3/8"; TRANSITION_TOP=5' - 2 1/4"; TYPE=0' - 0"; Type Comments=Vari-Plume Laboratory Exhaust Mixed-Flow Inline Belt Drive With Isolation Box; UNIT_HEIGHT=3' - 11"; UNIT_HEIGHT*.75=2' - 11 1/4"; UNIT_OD=3' - 2 5/16"; UNIT_RADIUS=1' - 7 5/32"; UNIT_RADIUS*.6=1' - 5 1/4"; UNIT_RADIUS+4"=1' - 11 5/32"
- 270_QMXVP-27L-Isolation_Box: (A/2)+.25"=2' - 0 1/4"; (NOZZLE_HEIGHT-(NOZZLE_HEIGHT/8*2))/2=1' - 10 3/4"; (NOZZLE_WB_OD-NOZZLE_TOP_OD)/2=0' - 5 11/32"; A=4' - 0"; A/2=2' - 0"; B=10' - 8"; B/2=5' - 4"; C=5' - 3"; C/2=2' - 7 1/2"; E=3' - 10 15/16"; GA=0' - 0 3/32"; Model=QMXVP-Isolation Box; NOZZLE_BOTTOM_ID=3' - 2 5/16"; NOZZLE_BOTTOM_RAD=1' - 7 5/32"; NOZZLE_HEIGHT=5' - 0 5/8"; NOZZLE_HEIGHT/7*2=1' - 3 5/32"; NOZZLE_SIZE=27' - 0"; NOZZLE_TOP_OD=3' - 3 11/16"; NOZZLE_TOP_RAD=1' - 7 27/32"; NOZZLE_WB/4=1' - 0 3/16"; NOZZLE_WB_OD=5' - 1"; NOZZLE_WB_RAD=2' - 6 1/2"; NOZZLE_WB_RAD-2"=2' - 4 1/2"; RO=3' - 4 3/4"; RO/2=1' - 8 3/8"; TRANSITION_TOP=5' - 2 1/4"; TYPE=0' - 0"; Type Comments=Vari-Plume Laboratory Exhaust Mixed-Flow Inline Belt Drive With Isolation Box; UNIT_HEIGHT=3' - 11"; UNIT_HEIGHT*.75=2' - 11 1/4"; UNIT_OD=3' - 2 5/16"; UNIT_RADIUS=1' - 7 5/32"; UNIT_RADIUS*.6=1' - 5 1/4"; UNIT_RADIUS+4"=1' - 11 5/32"
- 300_QMXHPVP-27H-Isolation_Box: (A/2)+.25"=2' - 2 1/4"; (NOZZLE_HEIGHT-(NOZZLE_HEIGHT/8*2))/2=1' - 10 3/4"; (NOZZLE_WB_OD-NOZZLE_TOP_OD)/2=0' - 5 11/32"; A=4' - 4"; A/2=2' - 2"; B=12' - 4"; B/2=6' - 2"; C=5' - 7"; C/2=2' - 9 1/2"; E=4' - 2 15/16"; GA=0' - 0 3/32"; Model=QMXHPVP-Isolation Box; NOZZLE_BOTTOM_ID=3' - 2 5/16"; NOZZLE_BOTTOM_RAD=1' - 7 5/32"; NOZZLE_HEIGHT=5' - 0 5/8"; NOZZLE_HEIGHT/7*2=1' - 3 5/32"; NOZZLE_SIZE=27' - 0"; NOZZLE_TOP_OD=3' - 3 11/16"; NOZZLE_TOP_RAD=1' - 7 27/32"; NOZZLE_WB/4=1' - 0 3/16"; NOZZLE_WB_OD=5' - 1"; NOZZLE_WB_RAD=2' - 6 1/2"; NOZZLE_WB_RAD-2"=2' - 4 1/2"; RO=3' - 8 3/4"; RO/2=1' - 10 3/8"; TRANSITION_TOP=6' - 5 1/4"; TYPE=1' - 0"; Type Comments=Vari-Plume Laboratory Exhaust Mixed-Flow High Pressure Inline Belt Drive With Isolation Box; UNIT_HEIGHT=4' - 6"; UNIT_HEIGHT*.75=3' - 4 1/2"; UNIT_OD=3' - 6 1/2"; UNIT_RADIUS=1' - 9 1/4"; UNIT_RADIUS*.6=1' - 7 1/8"; UNIT_RADIUS+4"=2' - 1 1/4"
- 300_QMXHPVP-27L-Isolation_Box: (A/2)+.25"=2' - 2 1/4"; (NOZZLE_HEIGHT-(NOZZLE_HEIGHT/8*2))/2=1' - 10 3/4"; (NOZZLE_WB_OD-NOZZLE_TOP_OD)/2=0' - 5 11/32"; A=4' - 4"; A/2=2' - 2"; B=12' - 4"; B/2=6' - 2"; C=5' - 7"; C/2=2' - 9 1/2"; E=4' - 2 15/16"; GA=0' - 0 3/32"; Model=QMXHPVP-Isolation Box; NOZZLE_BOTTOM_ID=3' - 2 5/16"; NOZZLE_BOTTOM_RAD=1' - 7 5/32"; NOZZLE_HEIGHT=5' - 0 5/8"; NOZZLE_HEIGHT/7*2=1' - 3 5/32"; NOZZLE_SIZE=27' - 0"; NOZZLE_TOP_OD=3' - 3 11/16"; NOZZLE_TOP_RAD=1' - 7 27/32"; NOZZLE_WB/4=1' - 0 3/16"; NOZZLE_WB_OD=5' - 1"; NOZZLE_WB_RAD=2' - 6 1/2"; NOZZLE_WB_RAD-2"=2' - 4 1/2"; RO=3' - 8 3/4"; RO/2=1' - 10 3/8"; TRANSITION_TOP=6' - 5 1/4"; TYPE=1' - 0"; Type Comments=Vari-Plume Laboratory Exhaust Mixed-Flow High Pressure Inline Belt Drive With Isolation Box; UNIT_HEIGHT=4' - 6"; UNIT_HEIGHT*.75=3' - 4 1/2"; UNIT_OD=3' - 6 1/2"; UNIT_RADIUS=1' - 9 1/4"; UNIT_RADIUS*.6=1' - 7 1/8"; UNIT_RADIUS+4"=2' - 1 1/4"
- 300_QMXVP-27H-Isolation_Box: (A/2)+.25"=2' - 2 1/4"; (NOZZLE_HEIGHT-(NOZZLE_HEIGHT/8*2))/2=1' - 10 3/4"; (NOZZLE_WB_OD-NOZZLE_TOP_OD)/2=0' - 5 11/32"; A=4' - 4"; A/2=2' - 2"; B=12' - 4"; B/2=6' - 2"; C=5' - 7"; C/2=2' - 9 1/2"; E=4' - 2 15/16"; GA=0' - 0 3/32"; Model=QMXVP-Isolation Box; NOZZLE_BOTTOM_ID=3' - 2 5/16"; NOZZLE_BOTTOM_RAD=1' - 7 5/32"; NOZZLE_HEIGHT=5' - 0 5/8"; NOZZLE_HEIGHT/7*2=1' - 3 5/32"; NOZZLE_SIZE=27' - 0"; NOZZLE_TOP_OD=3' - 3 11/16"; NOZZLE_TOP_RAD=1' - 7 27/32"; NOZZLE_WB/4=1' - 0 3/16"; NOZZLE_WB_OD=5' - 1"; NOZZLE_WB_RAD=2' - 6 1/2"; NOZZLE_WB_RAD-2"=2' - 4 1/2"; RO=3' - 8 3/4"; RO/2=1' - 10 3/8"; TRANSITION_TOP=6' - 5 1/4"; TYPE=0' - 0"; Type Comments=Vari-Plume Laboratory Exhaust Mixed-Flow Inline Belt Drive With Isolation Box; UNIT_HEIGHT=4' - 6"; UNIT_HEIGHT*.75=3' - 4 1/2"; UNIT_OD=3' - 6 1/2"; UNIT_RADIUS=1' - 9 1/4"; UNIT_RADIUS*.6=1' - 7 1/8"; UNIT_RADIUS+4"=2' - 1 1/4"
- 300_QMXVP-27L-Isolation_Box: (A/2)+.25"=2' - 2 1/4"; (NOZZLE_HEIGHT-(NOZZLE_HEIGHT/8*2))/2=1' - 10 3/4"; (NOZZLE_WB_OD-NOZZLE_TOP_OD)/2=0' - 5 11/32"; A=4' - 4"; A/2=2' - 2"; B=12' - 4"; B/2=6' - 2"; C=5' - 7"; C/2=2' - 9 1/2"; E=4' - 2 15/16"; GA=0' - 0 3/32"; Model=QMXVP-Isolation Box; NOZZLE_BOTTOM_ID=3' - 2 5/16"; NOZZLE_BOTTOM_RAD=1' - 7 5/32"; NOZZLE_HEIGHT=5' - 0 5/8"; NOZZLE_HEIGHT/7*2=1' - 3 5/32"; NOZZLE_SIZE=27' - 0"; NOZZLE_TOP_OD=3' - 3 11/16"; NOZZLE_TOP_RAD=1' - 7 27/32"; NOZZLE_WB/4=1' - 0 3/16"; NOZZLE_WB_OD=5' - 1"; NOZZLE_WB_RAD=2' - 6 1/2"; NOZZLE_WB_RAD-2"=2' - 4 1/2"; RO=3' - 8 3/4"; RO/2=1' - 10 3/8"; TRANSITION_TOP=6' - 5 1/4"; TYPE=0' - 0"; Type Comments=Vari-Plume Laboratory Exhaust Mixed-Flow Inline Belt Drive With Isolation Box; UNIT_HEIGHT=4' - 6"; UNIT_HEIGHT*.75=3' - 4 1/2"; UNIT_OD=3' - 6 1/2"; UNIT_RADIUS=1' - 9 1/4"; UNIT_RADIUS*.6=1' - 7 1/8"; UNIT_RADIUS+4"=2' - 1 1/4"
- 330_QMXHPVP-27H-Isolation_Box: (A/2)+.25"=2' - 4 1/4"; (NOZZLE_HEIGHT-(NOZZLE_HEIGHT/8*2))/2=1' - 10 3/4"; (NOZZLE_WB_OD-NOZZLE_TOP_OD)/2=0' - 5 11/32"; A=4' - 8"; A/2=2' - 4"; B=12' - 10"; B/2=6' - 5"; C=6' - 1"; C/2=3' - 0 1/2"; E=4' - 6 13/16"; GA=0' - 0 3/32"; Model=QMXHPVP-Isolation Box; NOZZLE_BOTTOM_ID=3' - 2 5/16"; NOZZLE_BOTTOM_RAD=1' - 7 5/32"; NOZZLE_HEIGHT=5' - 0 5/8"; NOZZLE_HEIGHT/7*2=1' - 3 5/32"; NOZZLE_SIZE=27' - 0"; NOZZLE_TOP_OD=3' - 3 11/16"; NOZZLE_TOP_RAD=1' - 7 27/32"; NOZZLE_WB/4=1' - 0 3/16"; NOZZLE_WB_OD=5' - 1"; NOZZLE_WB_RAD=2' - 6 1/2"; NOZZLE_WB_RAD-2"=2' - 4 1/2"; RO=4' - 0 5/8"; RO/2=2' - 0 5/16"; TRANSITION_TOP=7' - 5 3/4"; TYPE=1' - 0"; Type Comments=Vari-Plume Laboratory Exhaust Mixed-Flow High Pressure Inline Belt Drive With Isolation Box; UNIT_HEIGHT=4' - 10 1/2"; UNIT_HEIGHT*.75=3' - 7 7/8"; UNIT_OD=3' - 10 3/4"; UNIT_RADIUS=1' - 11 3/8"; UNIT_RADIUS*.6=1' - 9 1/32"; UNIT_RADIUS+4"=2' - 3 3/8"
- 330_QMXHPVP-27L-Isolation_Box: (A/2)+.25"=2' - 4 1/4"; (NOZZLE_HEIGHT-(NOZZLE_HEIGHT/8*2))/2=1' - 10 3/4"; (NOZZLE_WB_OD-NOZZLE_TOP_OD)/2=0' - 5 11/32"; A=4' - 8"; A/2=2' - 4"; B=12' - 10"; B/2=6' - 5"; C=6' - 1"; C/2=3' - 0 1/2"; E=4' - 6 13/16"; GA=0' - 0 3/32"; Model=QMXHPVP-Isolation Box; NOZZLE_BOTTOM_ID=3' - 2 5/16"; NOZZLE_BOTTOM_RAD=1' - 7 5/32"; NOZZLE_HEIGHT=5' - 0 5/8"; NOZZLE_HEIGHT/7*2=1' - 3 5/32"; NOZZLE_SIZE=27' - 0"; NOZZLE_TOP_OD=3' - 3 11/16"; NOZZLE_TOP_RAD=1' - 7 27/32"; NOZZLE_WB/4=1' - 0 3/16"; NOZZLE_WB_OD=5' - 1"; NOZZLE_WB_RAD=2' - 6 1/2"; NOZZLE_WB_RAD-2"=2' - 4 1/2"; RO=4' - 0 5/8"; RO/2=2' - 0 5/16"; TRANSITION_TOP=7' - 5 3/4"; TYPE=1' - 0"; Type Comments=Vari-Plume Laboratory Exhaust Mixed-Flow High Pressure Inline Belt Drive With Isolation Box; UNIT_HEIGHT=4' - 10 1/2"; UNIT_HEIGHT*.75=3' - 7 7/8"; UNIT_OD=3' - 10 3/4"; UNIT_RADIUS=1' - 11 3/8"; UNIT_RADIUS*.6=1' - 9 1/32"; UNIT_RADIUS+4"=2' - 3 3/8"
- 330_QMXVP-27H-Isolation_Box: (A/2)+.25"=2' - 4 1/4"; (NOZZLE_HEIGHT-(NOZZLE_HEIGHT/8*2))/2=1' - 10 3/4"; (NOZZLE_WB_OD-NOZZLE_TOP_OD)/2=0' - 5 11/32"; A=4' - 8"; A/2=2' - 4"; B=12' - 10"; B/2=6' - 5"; C=6' - 1"; C/2=3' - 0 1/2"; E=4' - 6 13/16"; GA=0' - 0 3/32"; Model=QMXVP-Isolation Box; NOZZLE_BOTTOM_ID=3' - 2 5/16"; NOZZLE_BOTTOM_RAD=1' - 7 5/32"; NOZZLE_HEIGHT=5' - 0 5/8"; NOZZLE_HEIGHT/7*2=1' - 3 5/32"; NOZZLE_SIZE=27' - 0"; NOZZLE_TOP_OD=3' - 3 11/16"; NOZZLE_TOP_RAD=1' - 7 27/32"; NOZZLE_WB/4=1' - 0 3/16"; NOZZLE_WB_OD=5' - 1"; NOZZLE_WB_RAD=2' - 6 1/2"; NOZZLE_WB_RAD-2"=2' - 4 1/2"; RO=4' - 0 5/8"; RO/2=2' - 0 5/16"; TRANSITION_TOP=7' - 5 3/4"; TYPE=0' - 0"; Type Comments=Vari-Plume Laboratory Exhaust Mixed-Flow Inline Belt Drive With Isolation Box; UNIT_HEIGHT=4' - 10 1/2"; UNIT_HEIGHT*.75=3' - 7 7/8"; UNIT_OD=3' - 10 3/4"; UNIT_RADIUS=1' - 11 3/8"; UNIT_RADIUS*.6=1' - 9 1/32"; UNIT_RADIUS+4"=2' - 3 3/8"
- 330_QMXVP-27L-Isolation_Box: (A/2)+.25"=2' - 4 1/4"; (NOZZLE_HEIGHT-(NOZZLE_HEIGHT/8*2))/2=1' - 10 3/4"; (NOZZLE_WB_OD-NOZZLE_TOP_OD)/2=0' - 5 11/32"; A=4' - 8"; A/2=2' - 4"; B=12' - 10"; B/2=6' - 5"; C=6' - 1"; C/2=3' - 0 1/2"; E=4' - 6 13/16"; GA=0' - 0 3/32"; Model=QMXVP-Isolation Box; NOZZLE_BOTTOM_ID=3' - 2 5/16"; NOZZLE_BOTTOM_RAD=1' - 7 5/32"; NOZZLE_HEIGHT=5' - 0 5/8"; NOZZLE_HEIGHT/7*2=1' - 3 5/32"; NOZZLE_SIZE=27' - 0"; NOZZLE_TOP_OD=3' - 3 11/16"; NOZZLE_TOP_RAD=1' - 7 27/32"; NOZZLE_WB/4=1' - 0 3/16"; NOZZLE_WB_OD=5' - 1"; NOZZLE_WB_RAD=2' - 6 1/2"; NOZZLE_WB_RAD-2"=2' - 4 1/2"; RO=4' - 0 5/8"; RO/2=2' - 0 5/16"; TRANSITION_TOP=7' - 5 3/4"; TYPE=0' - 0"; Type Comments=Vari-Plume Laboratory Exhaust Mixed-Flow Inline Belt Drive With Isolation Box; UNIT_HEIGHT=4' - 10 1/2"; UNIT_HEIGHT*.75=3' - 7 7/8"; UNIT_OD=3' - 10 3/4"; UNIT_RADIUS=1' - 11 3/8"; UNIT_RADIUS*.6=1' - 9 1/32"; UNIT_RADIUS+4"=2' - 3 3/8"
- 365_QMXHPVP-27H-Isolation_Box: (A/2)+.25"=2' - 7 1/4"; (NOZZLE_HEIGHT-(NOZZLE_HEIGHT/8*2))/2=1' - 10 3/4"; (NOZZLE_WB_OD-NOZZLE_TOP_OD)/2=0' - 5 11/32"; A=5' - 2"; A/2=2' - 7"; B=14' - 7"; B/2=7' - 3 1/2"; C=6' - 7"; C/2=3' - 3 1/2"; E=5' - 0 3/4"; GA=0' - 0 3/32"; Model=QMXHPVP-Isolation Box; NOZZLE_BOTTOM_ID=3' - 2 5/16"; NOZZLE_BOTTOM_RAD=1' - 7 5/32"; NOZZLE_HEIGHT=5' - 0 5/8"; NOZZLE_HEIGHT/7*2=1' - 3 5/32"; NOZZLE_SIZE=27' - 0"; NOZZLE_TOP_OD=3' - 3 11/16"; NOZZLE_TOP_RAD=1' - 7 27/32"; NOZZLE_WB/4=1' - 0 3/16"; NOZZLE_WB_OD=5' - 1"; NOZZLE_WB_RAD=2' - 6 1/2"; NOZZLE_WB_RAD-2"=2' - 4 1/2"; RO=4' - 6 1/2"; RO/2=2' - 3 1/4"; TRANSITION_TOP=8' - 8 1/4"; TYPE=1' - 0"; Type Comments=Vari-Plume Laboratory Exhaust Mixed-Flow High Pressure Inline Belt Drive With Isolation Box; UNIT_HEIGHT=5' - 4"; UNIT_HEIGHT*.75=4' - 0"; UNIT_OD=4' - 3 3/4"; UNIT_RADIUS=2' - 1 7/8"; UNIT_RADIUS*.6=1' - 11 9/32"; UNIT_RADIUS+4"=2' - 5 7/8"
- 365_QMXHPVP-27L-Isolation_Box: (A/2)+.25"=2' - 7 1/4"; (NOZZLE_HEIGHT-(NOZZLE_HEIGHT/8*2))/2=1' - 10 3/4"; (NOZZLE_WB_OD-NOZZLE_TOP_OD)/2=0' - 5 11/32"; A=5' - 2"; A/2=2' - 7"; B=14' - 7"; B/2=7' - 3 1/2"; C=6' - 7"; C/2=3' - 3 1/2"; E=5' - 0 3/4"; GA=0' - 0 3/32"; Model=QMXHPVP-Isolation Box; NOZZLE_BOTTOM_ID=3' - 2 5/16"; NOZZLE_BOTTOM_RAD=1' - 7 5/32"; NOZZLE_HEIGHT=5' - 0 5/8"; NOZZLE_HEIGHT/7*2=1' - 3 5/32"; NOZZLE_SIZE=27' - 0"; NOZZLE_TOP_OD=3' - 3 11/16"; NOZZLE_TOP_RAD=1' - 7 27/32"; NOZZLE_WB/4=1' - 0 3/16"; NOZZLE_WB_OD=5' - 1"; NOZZLE_WB_RAD=2' - 6 1/2"; NOZZLE_WB_RAD-2"=2' - 4 1/2"; RO=4' - 6 1/2"; RO/2=2' - 3 1/4"; TRANSITION_TOP=8' - 8 1/4"; TYPE=1' - 0"; Type Comments=Vari-Plume Laboratory Exhaust Mixed-Flow High Pressure Inline Belt Drive With Isolation Box; UNIT_HEIGHT=5' - 4"; UNIT_HEIGHT*.75=4' - 0"; UNIT_OD=4' - 3 3/4"; UNIT_RADIUS=2' - 1 7/8"; UNIT_RADIUS*.6=1' - 11 9/32"; UNIT_RADIUS+4"=2' - 5 7/8"
- 365_QMXVP-27H-Isolation_Box: (A/2)+.25"=2' - 7 1/4"; (NOZZLE_HEIGHT-(NOZZLE_HEIGHT/8*2))/2=1' - 10 3/4"; (NOZZLE_WB_OD-NOZZLE_TOP_OD)/2=0' - 5 11/32"; A=5' - 2"; A/2=2' - 7"; B=14' - 7"; B/2=7' - 3 1/2"; C=6' - 7"; C/2=3' - 3 1/2"; E=5' - 0 3/4"; GA=0' - 0 3/32"; Model=QMXVP-Isolation Box; NOZZLE_BOTTOM_ID=3' - 2 5/16"; NOZZLE_BOTTOM_RAD=1' - 7 5/32"; NOZZLE_HEIGHT=5' - 0 5/8"; NOZZLE_HEIGHT/7*2=1' - 3 5/32"; NOZZLE_SIZE=27' - 0"; NOZZLE_TOP_OD=3' - 3 11/16"; NOZZLE_TOP_RAD=1' - 7 27/32"; NOZZLE_WB/4=1' - 0 3/16"; NOZZLE_WB_OD=5' - 1"; NOZZLE_WB_RAD=2' - 6 1/2"; NOZZLE_WB_RAD-2"=2' - 4 1/2"; RO=4' - 6 1/2"; RO/2=2' - 3 1/4"; TRANSITION_TOP=8' - 8 1/4"; TYPE=0' - 0"; Type Comments=Vari-Plume Laboratory Exhaust Mixed-Flow Inline Belt Drive With Isolation Box; UNIT_HEIGHT=5' - 4"; UNIT_HEIGHT*.75=4' - 0"; UNIT_OD=4' - 3 3/4"; UNIT_RADIUS=2' - 1 7/8"; UNIT_RADIUS*.6=1' - 11 9/32"; UNIT_RADIUS+4"=2' - 5 7/8"
- 365_QMXVP-27L-Isolation_Box: (A/2)+.25"=2' - 7 1/4"; (NOZZLE_HEIGHT-(NOZZLE_HEIGHT/8*2))/2=1' - 10 3/4"; (NOZZLE_WB_OD-NOZZLE_TOP_OD)/2=0' - 5 11/32"; A=5' - 2"; A/2=2' - 7"; B=14' - 7"; B/2=7' - 3 1/2"; C=6' - 7"; C/2=3' - 3 1/2"; E=5' - 0 3/4"; GA=0' - 0 3/32"; Model=QMXVP-Isolation Box; NOZZLE_BOTTOM_ID=3' - 2 5/16"; NOZZLE_BOTTOM_RAD=1' - 7 5/32"; NOZZLE_HEIGHT=5' - 0 5/8"; NOZZLE_HEIGHT/7*2=1' - 3 5/32"; NOZZLE_SIZE=27' - 0"; NOZZLE_TOP_OD=3' - 3 11/16"; NOZZLE_TOP_RAD=1' - 7 27/32"; NOZZLE_WB/4=1' - 0 3/16"; NOZZLE_WB_OD=5' - 1"; NOZZLE_WB_RAD=2' - 6 1/2"; NOZZLE_WB_RAD-2"=2' - 4 1/2"; RO=4' - 6 1/2"; RO/2=2' - 3 1/4"; TRANSITION_TOP=8' - 8 1/4"; TYPE=0' - 0"; Type Comments=Vari-Plume Laboratory Exhaust Mixed-Flow Inline Belt Drive With Isolation Box; UNIT_HEIGHT=5' - 4"; UNIT_HEIGHT*.75=4' - 0"; UNIT_OD=4' - 3 3/4"; UNIT_RADIUS=2' - 1 7/8"; UNIT_RADIUS*.6=1' - 11 9/32"; UNIT_RADIUS+4"=2' - 5 7/8"
- 402_QMXHPVP-27H-Isolation_Box: (A/2)+.25"=2' - 9 3/4"; (NOZZLE_HEIGHT-(NOZZLE_HEIGHT/8*2))/2=1' - 10 3/4"; (NOZZLE_WB_OD-NOZZLE_TOP_OD)/2=0' - 5 11/32"; A=5' - 7"; A/2=2' - 9 1/2"; B=15' - 3"; B/2=7' - 7 1/2"; C=7' - 4"; C/2=3' - 8"; E=5' - 5 3/4"; GA=0' - 0 3/32"; Model=QMXHPVP-Isolation Box; NOZZLE_BOTTOM_ID=3' - 2 5/16"; NOZZLE_BOTTOM_RAD=1' - 7 5/32"; NOZZLE_HEIGHT=5' - 0 5/8"; NOZZLE_HEIGHT/7*2=1' - 3 5/32"; NOZZLE_SIZE=27' - 0"; NOZZLE_TOP_OD=3' - 3 11/16"; NOZZLE_TOP_RAD=1' - 7 27/32"; NOZZLE_WB/4=1' - 0 3/16"; NOZZLE_WB_OD=5' - 1"; NOZZLE_WB_RAD=2' - 6 1/2"; NOZZLE_WB_RAD-2"=2' - 4 1/2"; RO=4' - 11 7/16"; RO/2=2' - 5 23/32"; TRANSITION_TOP=9' - 10 3/4"; TYPE=1' - 0"; Type Comments=Vari-Plume Laboratory Exhaust Mixed-Flow High Pressure Inline Belt Drive With Isolation Box; UNIT_HEIGHT=5' - 8 1/2"; UNIT_HEIGHT*.75=4' - 3 3/8"; UNIT_OD=4' - 8 15/16"; UNIT_RADIUS=2' - 4 15/32"; UNIT_RADIUS*.6=2' - 1 5/8"; UNIT_RADIUS+4"=2' - 8 15/32"
- 402_QMXHPVP-27L-Isolation_Box: (A/2)+.25"=2' - 9 3/4"; (NOZZLE_HEIGHT-(NOZZLE_HEIGHT/8*2))/2=1' - 10 3/4"; (NOZZLE_WB_OD-NOZZLE_TOP_OD)/2=0' - 5 11/32"; A=5' - 7"; A/2=2' - 9 1/2"; B=15' - 3"; B/2=7' - 7 1/2"; C=7' - 4"; C/2=3' - 8"; E=5' - 5 3/4"; GA=0' - 0 3/32"; Model=QMXHPVP-Isolation Box; NOZZLE_BOTTOM_ID=3' - 2 5/16"; NOZZLE_BOTTOM_RAD=1' - 7 5/32"; NOZZLE_HEIGHT=5' - 0 5/8"; NOZZLE_HEIGHT/7*2=1' - 3 5/32"; NOZZLE_SIZE=27' - 0"; NOZZLE_TOP_OD=3' - 3 11/16"; NOZZLE_TOP_RAD=1' - 7 27/32"; NOZZLE_WB/4=1' - 0 3/16"; NOZZLE_WB_OD=5' - 1"; NOZZLE_WB_RAD=2' - 6 1/2"; NOZZLE_WB_RAD-2"=2' - 4 1/2"; RO=4' - 11 7/16"; RO/2=2' - 5 23/32"; TRANSITION_TOP=9' - 10 3/4"; TYPE=1' - 0"; Type Comments=Vari-Plume Laboratory Exhaust Mixed-Flow High Pressure Inline Belt Drive With Isolation Box; UNIT_HEIGHT=5' - 8 1/2"; UNIT_HEIGHT*.75=4' - 3 3/8"; UNIT_OD=4' - 8 15/16"; UNIT_RADIUS=2' - 4 15/32"; UNIT_RADIUS*.6=2' - 1 5/8"; UNIT_RADIUS+4"=2' - 8 15/32"
- 402_QMXVP-27H-Isolation_Box: (A/2)+.25"=2' - 9 3/4"; (NOZZLE_HEIGHT-(NOZZLE_HEIGHT/8*2))/2=1' - 10 3/4"; (NOZZLE_WB_OD-NOZZLE_TOP_OD)/2=0' - 5 11/32"; A=5' - 7"; A/2=2' - 9 1/2"; B=15' - 3"; B/2=7' - 7 1/2"; C=7' - 4"; C/2=3' - 8"; E=5' - 5 3/4"; GA=0' - 0 3/32"; Model=QMXVP-Isolation Box; NOZZLE_BOTTOM_ID=3' - 2 5/16"; NOZZLE_BOTTOM_RAD=1' - 7 5/32"; NOZZLE_HEIGHT=5' - 0 5/8"; NOZZLE_HEIGHT/7*2=1' - 3 5/32"; NOZZLE_SIZE=27' - 0"; NOZZLE_TOP_OD=3' - 3 11/16"; NOZZLE_TOP_RAD=1' - 7 27/32"; NOZZLE_WB/4=1' - 0 3/16"; NOZZLE_WB_OD=5' - 1"; NOZZLE_WB_RAD=2' - 6 1/2"; NOZZLE_WB_RAD-2"=2' - 4 1/2"; RO=4' - 11 7/16"; RO/2=2' - 5 23/32"; TRANSITION_TOP=9' - 10 3/4"; TYPE=0' - 0"; Type Comments=Vari-Plume Laboratory Exhaust Mixed-Flow Inline Belt Drive With Isolation Box; UNIT_HEIGHT=5' - 8 1/2"; UNIT_HEIGHT*.75=4' - 3 3/8"; UNIT_OD=4' - 8 15/16"; UNIT_RADIUS=2' - 4 15/32"; UNIT_RADIUS*.6=2' - 1 5/8"; UNIT_RADIUS+4"=2' - 8 15/32"
- 402_QMXVP-27L-Isolation_Box: (A/2)+.25"=2' - 9 3/4"; (NOZZLE_HEIGHT-(NOZZLE_HEIGHT/8*2))/2=1' - 10 3/4"; (NOZZLE_WB_OD-NOZZLE_TOP_OD)/2=0' - 5 11/32"; A=5' - 7"; A/2=2' - 9 1/2"; B=15' - 3"; B/2=7' - 7 1/2"; C=7' - 4"; C/2=3' - 8"; E=5' - 5 3/4"; GA=0' - 0 3/32"; Model=QMXVP-Isolation Box; NOZZLE_BOTTOM_ID=3' - 2 5/16"; NOZZLE_BOTTOM_RAD=1' - 7 5/32"; NOZZLE_HEIGHT=5' - 0 5/8"; NOZZLE_HEIGHT/7*2=1' - 3 5/32"; NOZZLE_SIZE=27' - 0"; NOZZLE_TOP_OD=3' - 3 11/16"; NOZZLE_TOP_RAD=1' - 7 27/32"; NOZZLE_WB/4=1' - 0 3/16"; NOZZLE_WB_OD=5' - 1"; NOZZLE_WB_RAD=2' - 6 1/2"; NOZZLE_WB_RAD-2"=2' - 4 1/2"; RO=4' - 11 7/16"; RO/2=2' - 5 23/32"; TRANSITION_TOP=9' - 10 3/4"; TYPE=0' - 0"; Type Comments=Vari-Plume Laboratory Exhaust Mixed-Flow Inline Belt Drive With Isolation Box; UNIT_HEIGHT=5' - 8 1/2"; UNIT_HEIGHT*.75=4' - 3 3/8"; UNIT_OD=4' - 8 15/16"; UNIT_RADIUS=2' - 4 15/32"; UNIT_RADIUS*.6=2' - 1 5/8"; UNIT_RADIUS+4"=2' - 8 15/32"

## geometry (parser evidence)
native form markers: Sweep x3
no freeform markers — native parametric forms only
